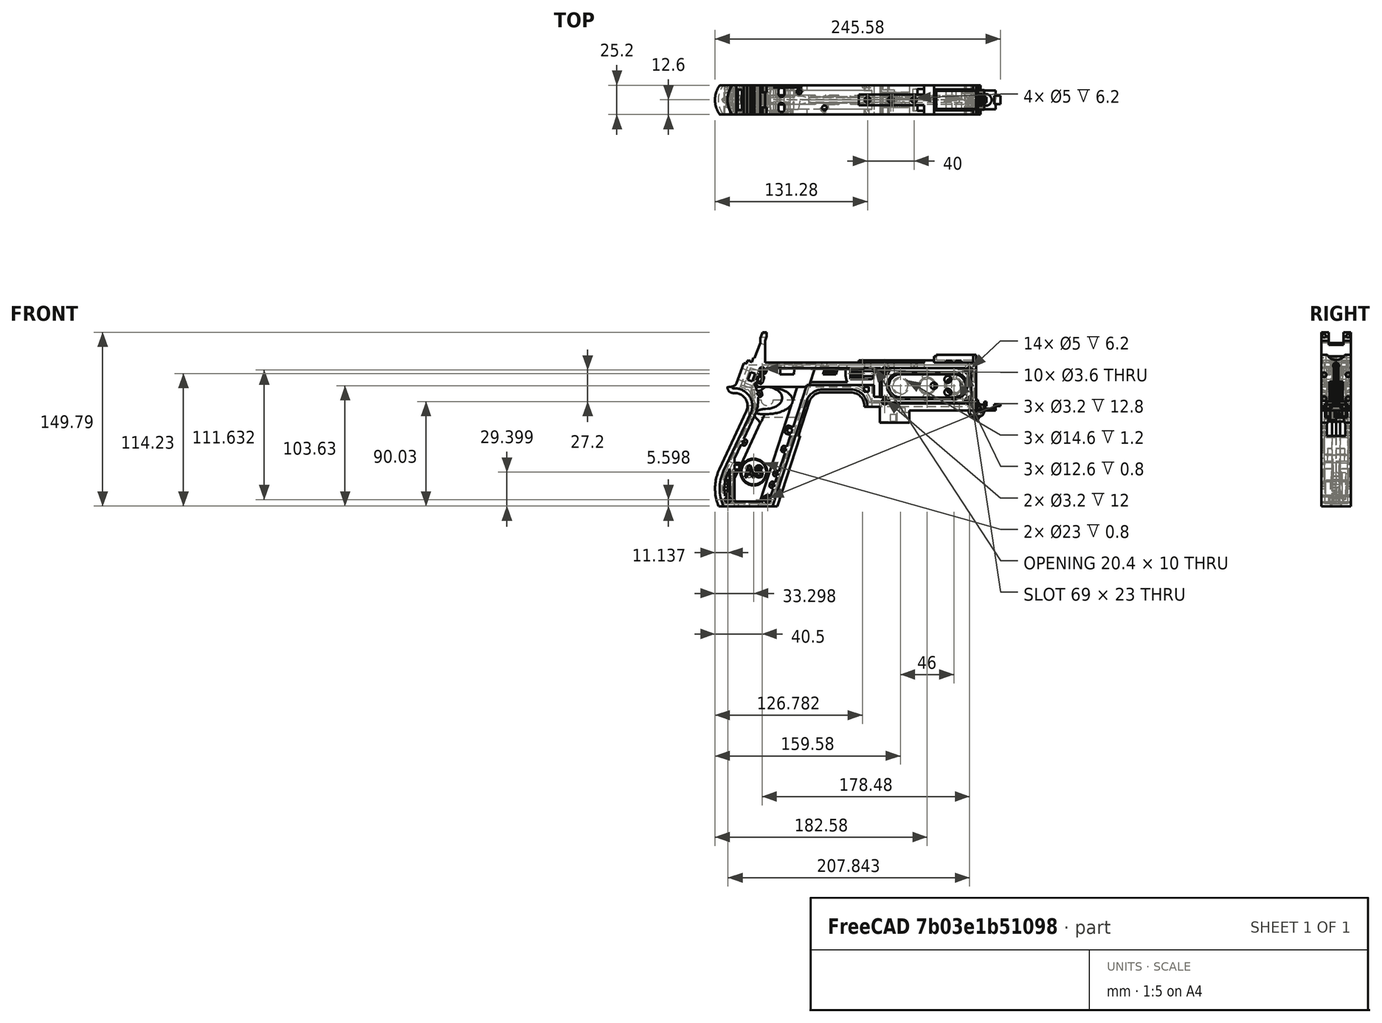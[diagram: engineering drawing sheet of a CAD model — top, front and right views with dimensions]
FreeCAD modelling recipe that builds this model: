
FCSTD DOCUMENT  (FreeCAD 1.0R39319 (Git))
Label: PICON-OF_ver_62
License: All rights reserved
LicenseURL: https://en.wikipedia.org/wiki/All_rights_reserved
objects: Sketcher::SketchObject×132, Part::Extrusion×66, Part::Cut×51, PartDesign::Pad×34, PartDesign::Pocket×21, PartDesign::Chamfer×15, PartDesign::Body×11, PartDesign::Fillet×6, Part::MultiFuse×5, Part::Part2DObjectPython×4, PartDesign::SubtractivePipe×4, PartDesign::SubtractiveLoft×4, PartDesign::Plane×3, PartDesign::SubShapeBinder×2, Part::Sweep×1, PartDesign::ShapeBinder×1, Mesh::Feature×1, PartDesign::Point×1, PartDesign::Groove×1
note: 664 computed .brp shape members not serialized (recipe doc carries the construction recipe); baked Part::Feature solids carry a one-line shape summary decoded from their .brp

FEATURE [Sketcher::SketchObject] Sketch  label="corpo principale"
  ArcFitTolerance = 1e-06
  AttacherType = Attacher::AttachEngine3D
  AttachmentSupport = -> [XZ_Plane]
  FullyConstrained = true
  MakeInternals = false
  MapMode = 5
  Placement = pos=(0,0,0) rot=(1,0,0;1.5708rad)
  sketch-geometry (65):
    g0: LineSegment StartX=0 StartY=0 StartZ=0 EndX=-57.2 EndY=0 EndZ=0
    g1: LineSegment StartX=-57.2 StartY=0 StartZ=0 EndX=-57.2 EndY=-10.4 EndZ=0
    g2: LineSegment StartX=-57.2 StartY=-10.4 StartZ=0 EndX=-82.8 EndY=-10.4 EndZ=0
    g3: LineSegment StartX=-82.8 StartY=-10.4 StartZ=0 EndX=-82.8 EndY=3.2 EndZ=0
    g4: LineSegment StartX=-82.8 StartY=3.2 StartZ=0 EndX=-93.6 EndY=3.2 EndZ=0
    g5: LineSegment StartX=-93.6 StartY=3.2 StartZ=0 EndX=-93.6 EndY=4 EndZ=0
    g6: LineSegment StartX=-107.6 StartY=18 StartZ=0 EndX=-132.428 EndY=18 EndZ=0
    g7: LineSegment StartX=-145.743 StartY=8.32624 StartZ=0 EndX=-175.232 EndY=-82.4316 EndZ=0
    g8: LineSegment StartX=-175.232 StartY=-82.4316 StartZ=0 EndX=-217.232 EndY=-82.4316 EndZ=0
    g9: LineSegment StartX=-217.232 StartY=-52.1862 StartZ=0 EndX=-193.988 EndY=-2.33927 EndZ=0
    g10: LineSegment StartX=-206.196 StartY=23.0857 StartZ=0 EndX=-199.861 EndY=40.4914 EndZ=0
    g11: LineSegment StartX=-199.861 StartY=40.4914 StartZ=0 EndX=-197.061 EndY=40.4914 EndZ=0
    g12: LineSegment StartX=-197.061 StartY=40.4914 StartZ=0 EndX=-197.061 EndY=42.8914 EndZ=0
    g13: LineSegment StartX=-197.061 StartY=42.8914 StartZ=0 EndX=-194.261 EndY=42.8914 EndZ=0
    g14: LineSegment StartX=-194.261 StartY=42.8914 StartZ=0 EndX=-194.535 EndY=42.1397 EndZ=0
    g15: LineSegment StartX=-194.535 StartY=42.1397 StartZ=0 EndX=-193.031 EndY=41.5924 EndZ=0
    g16: LineSegment StartX=-193.031 StartY=41.5924 StartZ=0 EndX=-191.663 EndY=45.3512 EndZ=0
    g17: LineSegment StartX=-191.663 StartY=45.3512 StartZ=0 EndX=-190.536 EndY=44.9408 EndZ=0
    g18: LineSegment StartX=-190.536 StartY=44.9408 StartZ=0 EndX=-185.747 EndY=58.0965 EndZ=0
    g19: LineSegment StartX=-185.747 StartY=58.0965 StartZ=0 EndX=-185.747 EndY=62.0965 EndZ=0
    g20: LineSegment StartX=-185.747 StartY=62.0965 StartZ=0 EndX=-183.832 EndY=67.3588 EndZ=0
    g21: LineSegment StartX=-183.832 StartY=67.3588 StartZ=0 EndX=-180.232 EndY=67.3588 EndZ=0
    g22: LineSegment StartX=-180.232 StartY=67.3588 StartZ=0 EndX=-180.232 EndY=63.7588 EndZ=0
    g23: LineSegment StartX=-180.232 StartY=63.7588 StartZ=0 EndX=-181.6 EndY=60 EndZ=0
    g24: LineSegment StartX=-181.6 StartY=60 StartZ=0 EndX=-181.6 EndY=41.2 EndZ=0
    g25: LineSegment StartX=-181.6 StartY=41.2 StartZ=0 EndX=-100.8 EndY=41.2 EndZ=0
    g26: LineSegment StartX=-36 StartY=43.2 StartZ=0 EndX=-36 EndY=41.2 EndZ=0
    g27: LineSegment StartX=0 StartY=48 StartZ=0 EndX=0 EndY=0 EndZ=0
    g28: LineSegment StartX=-209.901 StartY=19.85 StartZ=0 EndX=-209.901 EndY=20.1 EndZ=0
    g29: LineSegment StartX=-208.001 StartY=22 StartZ=0 EndX=-207.747 EndY=22 EndZ=0
    g30: LineSegment StartX=-207.583 StartY=19 StartZ=0 EndX=-209.051 EndY=19 EndZ=0
    g31: ArcOfCircle CenterX=-208.001 CenterY=20.1 CenterZ=0 NormalX=0 NormalY=0 NormalZ=1 AngleXU=0 Radius=1.9 StartAngle=1.5708 EndAngle=3.14159
    g32: GeomPoint [constr] X=-209.901 Y=22 Z=0
    g33: ArcOfCircle CenterX=-209.051 CenterY=19.85 CenterZ=0 NormalX=0 NormalY=0 NormalZ=1 AngleXU=0 Radius=0.85 StartAngle=3.14159 EndAngle=4.71239
    g34: GeomPoint [constr] X=-209.901 Y=19 Z=0
    g35: ArcOfCircle CenterX=-207.747 CenterY=23.65 CenterZ=0 NormalX=0 NormalY=0 NormalZ=1 AngleXU=0 Radius=1.65 StartAngle=4.71239 EndAngle=5.93412
    g36: GeomPoint [constr] X=-206.591 Y=22 Z=0
    g37: LineSegment StartX=-4 StartY=6 StartZ=0 EndX=-4 EndY=36.4 EndZ=0
    g38: LineSegment StartX=-4 StartY=36.4 StartZ=0 EndX=-185.2 EndY=36.4 EndZ=0
    g39: LineSegment StartX=-185.2 StartY=36.4 StartZ=0 EndX=-190.441 EndY=22 EndZ=0
    g40: LineSegment StartX=-214.575 StartY=-78.4316 StartZ=0 EndX=-178.142 EndY=-78.4316 EndZ=0
    g41: LineSegment StartX=-178.142 StartY=-78.4316 StartZ=0 EndX=-145.51 EndY=22 EndZ=0
    g42: LineSegment StartX=-145.51 StartY=22 StartZ=0 EndX=-87.91 EndY=22 EndZ=0
    g43: LineSegment StartX=-87.91 StartY=22 StartZ=0 EndX=-87.91 EndY=11.6 EndZ=0
    g44: LineSegment StartX=-87.91 StartY=11.6 StartZ=0 EndX=-80.11 EndY=11.6 EndZ=0
    g45: LineSegment StartX=-80.11 StartY=11.6 StartZ=0 EndX=-80.11 EndY=6 EndZ=0
    g46: LineSegment StartX=-80.11 StartY=6 StartZ=0 EndX=-4 EndY=6 EndZ=0
    g47: LineSegment StartX=-190.363 StartY=-4.02975 StartZ=0 EndX=-213.607 EndY=-53.8767 EndZ=0
    g48: ArcOfCircle CenterX=-132.428 CenterY=4 CenterZ=0 NormalX=0 NormalY=0 NormalZ=1 AngleXU=0 Radius=14 StartAngle=1.5708 EndAngle=2.82743
    g49: GeomPoint [constr] X=-142.6 Y=18 Z=0
    g50: ArcOfCircle CenterX=-107.6 CenterY=4 CenterZ=0 NormalX=0 NormalY=0 NormalZ=1 AngleXU=0 Radius=14 StartAngle=0 EndAngle=1.5708
    g51: GeomPoint [constr] X=-93.6 Y=18 Z=0
    g52: ArcOfCircle CenterX=-184.801 CenterY=-67.3089 CenterZ=0 NormalX=0 NormalY=0 NormalZ=1 AngleXU=0 Radius=35.7833 StartAngle=2.70526 EndAngle=3.57792
    g53: ArcOfCircle CenterX=-207.583 CenterY=4 CenterZ=0 NormalX=0 NormalY=0 NormalZ=1 AngleXU=0 Radius=15 StartAngle=5.84685 EndAngle=7.85398
    g54: LineSegment [constr] StartX=-213.607 StartY=-53.8767 StartZ=0 EndX=-217.232 EndY=-52.1862 EndZ=0
    g55: ArcOfCircle CenterX=-184.801 CenterY=-67.3089 CenterZ=0 NormalX=0 NormalY=0 NormalZ=1 AngleXU=0 Radius=31.7833 StartAngle=2.70526 EndAngle=3.49911
    g56: ArcOfCircle CenterX=-218.095 CenterY=8.90192 CenterZ=0 NormalX=0 NormalY=0 NormalZ=1 AngleXU=0 Radius=30.5989 StartAngle=5.84685 EndAngle=6.72553
    g57: LineSegment StartX=-44.6 StartY=43.2 StartZ=0 EndX=-36 EndY=43.2 EndZ=0
    g58: LineSegment StartX=-100.8 StartY=41.2 StartZ=0 EndX=-44.6 EndY=41.2 EndZ=0
    g59: LineSegment StartX=-44.6 StartY=41.2 StartZ=0 EndX=-44.6 EndY=43.2 EndZ=0
    g60: LineSegment StartX=-2.4 StartY=48 StartZ=0 EndX=0 EndY=48 EndZ=0
    g61: LineSegment StartX=-36 StartY=41.2 StartZ=0 EndX=-2.4 EndY=41.2 EndZ=0
    g62: LineSegment StartX=-2.4 StartY=41.2 StartZ=0 EndX=-2.4 EndY=48 EndZ=0
    g63: LineSegment [constr] StartX=-181.6 StartY=36.4 StartZ=0 EndX=-152.209 EndY=36.4 EndZ=0
    g64: LineSegment [constr] StartX=-181.6 StartY=36.4 StartZ=0 EndX=-130.41 EndY=36.4 EndZ=0
  constraints (183):
    c: Coincident(g-1,g0)
    c: PointOnObject(g0,g-1)
    c: Coincident(g0,g1)
    c: Vertical(g1)
    c: Coincident(g1,g2)
    c: Horizontal(g2)
    c: Coincident(g2,g3)
    c: Vertical(g3)
    c: Coincident(g3,g4)
    c: Coincident(g4,g5)
    c: Vertical(g5)
    c: Horizontal(g6)
    c: Coincident(g7,g8)
    c: Horizontal(g8)
    c: Coincident(g10,g11)
    c: Horizontal(g11)
    c: Coincident(g11,g12)
    c: Vertical(g12)
    c: Coincident(g12,g13)
    c: Horizontal(g13)
    c: Coincident(g13,g14)
    c: Coincident(g14,g15)
    c: Coincident(g15,g16)
    c: Coincident(g16,g17)
    c: Coincident(g17,g18)
    c: Coincident(g18,g19)
    c: Vertical(g19)
    c: Coincident(g19,g20)
    c: Coincident(g20,g21)
    c: Horizontal(g21)
    c: Coincident(g21,g22)
    c: Vertical(g22)
    c: Coincident(g22,g23)
    c: Coincident(g23,g24)
    c: Vertical(g24)
    c: Coincident(g24,g25)
    c: Horizontal(g25)
    c: Coincident(g57,g26)
    c: Vertical(g26)
    c: Coincident(g26,g61)
    c: PointOnObject(g60,g-2)
    c: Coincident(g60,g27)
    c: Coincident(g27,g0)
    c: DistanceY(g27,g27) = 48
    c: DistanceY(g1,g1) = 10.4
    c: DistanceX(g0,g0) = 57.2
    c: DistanceX(g2,g2) = 25.6
    c: Horizontal(g4)
    c: DistanceY(g3,g3) = 13.6
    c: DistanceX(g4,g4) = 10.8
    c: DistanceY(g5,g51) = 14.8
    c: DistanceX(g49,g51) = 49
    c: Distance(g7,g49) = 105.6
    c: DistanceX(g61,g60) = 36
    c: DistanceX(g25,g25) = 80.8
    c: DistanceY(g24,g24) = 18.8
    c: DistanceY(g22,g22) = 3.6
    c: Distance(g23) = 4
    c: Angle(g-1,g23) = 1.22173
    c: DistanceX(g21,g21) = 3.6
    c: Distance(g20) = 5.6
    c: Angle(g-1,g20) = 1.22173
    c: DistanceY(g19,g19) = 4
    c: Distance(g18) = 14
    c: Angle(g-1,g18) = 1.22173
    c: Distance(g17) = 1.2
    c: Distance(g16) = 4
    c: Angle(g16) = 1.22173
    c: Perpendicular(g18,g17)
    c: Distance(g15) = 1.6
    c: Perpendicular(g16,g15)
    c: Distance(g14) = 0.8
    c: DistanceX(g13,g13) = 2.8
    c: Perpendicular(g15,g14)
    c: DistanceY(g12,g12) = 2.4
    c: DistanceX(g11,g11) = 2.8
    c: Distance(g9) = 55
    c: Angle(g9,g-1) = 2.00713
    c: Horizontal(g29)
    c: Vertical(g28)
    c: Horizontal(g30)
    c: PointOnObject(g32,g29)
    c: PointOnObject(g32,g28)
    c: Tangent(g29,g31) = 1.5708
    c: Tangent(g28,g31) = 1.5708
    c: PointOnObject(g34,g28)
    c: PointOnObject(g34,g30)
    c: Tangent(g28,g33) = 1.5708
    c: Tangent(g30,g33) = 1.5708
    c: PointOnObject(g36,g29)
    c: PointOnObject(g36,g10)
    c: Tangent(g29,g35) = -1.5708
    c: Tangent(g10,g35) = -1.5708
    c: Angle(g-1,g10) = 1.22173
    c: Radius(g35) = 1.65
    c: Vertical(g37)
    c: Coincident(g37,g38)
    c: Horizontal(g38)
    c: Coincident(g38,g39)
    c: Horizontal(g40)
    c: Coincident(g40,g41)
    c: Coincident(g41,g42)
    c: Horizontal(g42)
    c: Coincident(g42,g43)
    c: Vertical(g43)
    c: Coincident(g43,g44)
    c: Horizontal(g44)
    c: Coincident(g44,g45)
    c: Vertical(g45)
    c: Coincident(g45,g46)
    c: Coincident(g46,g37)
    c: Horizontal(g46)
    c: DistanceY(g0,g37) = 6
    c: DistanceX(g37,g0) = 4
    c: DistanceY(g37,g25) = 4.8
    c: DistanceX(g38,g38) = 181.2
    c: DistanceX(g42,g42) = 57.6
    c: DistanceY(g49,g41) = 4
    c: DistanceX(g41,g49) = 2.91
    c: DistanceY(g43,g43) = 10.4
    c: DistanceX(g44,g44) = 7.8
    c: DistanceY(g7,g40) = 4
    c: Distance(g47) = 55
    c: Angle(g-1,g39) = 1.22173
    c: PointOnObject(g49,g7)
    c: PointOnObject(g49,g6)
    c: Tangent(g7,g48) = -1.5708
    c: Tangent(g6,g48) = -1.5708
    c: PointOnObject(g51,g5)
    c: PointOnObject(g51,g6)
    c: Tangent(g5,g50) = -1.5708
    c: Tangent(g6,g50) = -1.5708
    c: Radius(g50) = 14
    c: Radius(g48) = 14
    c: DistanceX(g8,g8) = 42
    c: Angle(g7,g-1) = 1.88496
    c: Parallel(g41,g7)
    c: Parallel(g47,g9)
    c: Coincident(g52,g8)
    c: Tangent(g52,g9) = 1.5708
    c: DistanceX(g9,g8) = 0
    c: Tangent(g53,g9) = -1.5708
    c: Tangent(g53,g30) = -1.5708
    c: Diameter(g53) = 30
    c: DistanceY(g53,g0) = -4
    c: Coincident(g54,g47)
    c: Distance(g54) = 4
    c: Coincident(g54,g9)
    c: Coincident(g55,g40)
    c: Tangent(g55,g47) = -1.5708
    c: Coincident(g52,g55)
    c: Coincident(g56,g39)
    c: Tangent(g56,g47) = 1.5708
    c: Horizontal(g57)
    c: DistanceX(g57,g57) = 8.6
    c: Coincident(g58,g25)
    c: Horizontal(g58)
    c: Coincident(g59,g58)
    c: Vertical(g59)
    c: DistanceY(g58,g57) = 2
    c: DistanceX(g58,g58) = 56.2
    c: Coincident(g59,g57)
    c: DistanceY(g41,g36) = 0
    c: DistanceY(g36,g39) = 0
    c: DistanceY(g28,g28) = 0.25
    c: DistanceX(g30,g36) = 2.46
    c: DistanceX(g28,g29) = 1.9
    c: Coincident(g62,g60)
    c: Horizontal(g60)
    c: DistanceX(g62,g27) = 2.4
    c: Coincident(g61,g62)
    c: DistanceY(g26,g26) = 2
    c: Vertical(g62)
    c: DistanceY(g61,g60) = 6.8
    c: Horizontal(g61)
    c: Distance(g63) = 29.391
    c: PointOnObject(g63,g38)
    c: PointOnObject(g63,g38)
    c: Distance(g64) = 51.19
    c: PointOnObject(g64,g38)
    c: PointOnObject(g64,g38)
    c: DistanceX(g24,g63) = 0
    c: DistanceX(g24,g64) = 0
FEATURE [Part::Extrusion] Extrude  label="Extrude corpo principale"
  Base = -> Sketch
  Dir = (0,-1,2e-16)
  DirMode = 2
  FaceMakerClass = Part::FaceMakerBullseye
  FaceMakerMode = 3
  LengthFwd = 25.2
  LengthRev = 12.6
  Solid = true
  Symmetric = true
FEATURE [Sketcher::SketchObject] Sketch002  label="scavo grilletto"
  ArcFitTolerance = 1e-06
  AttachmentSupport = -> [XZ_Plane]
  ExternalGeometry = -> [Sketch]
  FullyConstrained = true
  MakeInternals = false
  MapMode = 5
  Placement = pos=(0,0,0) rot=(1,0,0;1.5708rad)
  sketch-geometry (4):
    g0: LineSegment StartX=-89.51 StartY=22 StartZ=0 EndX=-152.71 EndY=22 EndZ=0
    g1: LineSegment StartX=-152.71 StartY=22 StartZ=0 EndX=-167.006 EndY=-22 EndZ=0
    g2: LineSegment StartX=-167.006 StartY=-22 StartZ=0 EndX=-89.51 EndY=-22 EndZ=0
    g3: LineSegment StartX=-89.51 StartY=-22 StartZ=0 EndX=-89.51 EndY=22 EndZ=0
  constraints (12):
    c: Horizontal(g0)
    c: Coincident(g0,g1)
    c: Coincident(g1,g2)
    c: Horizontal(g2)
    c: Coincident(g2,g3)
    c: Coincident(g3,g0)
    c: Vertical(g3)
    c: Angle(g1,g0) = 1.88496
    c: DistanceY(g3,g3) = 44
    c: DistanceX(g0,g0) = 63.2
    c: DistanceX(g0,g-3) = 1.6
    c: DistanceY(g-3,g0) = 0
FEATURE [Sketcher::SketchObject] Sketch004  label="traiettoria arrotondamento impugnatura anteriore"
  ArcFitTolerance = 1e-06
  AttachmentSupport = -> [XZ_Plane]
  ExternalGeometry = -> [Sketch]
  FullyConstrained = true
  MakeInternals = false
  MapMode = 5
  Placement = pos=(0,0,0) rot=(1,0,0;1.5708rad)
  sketch-geometry (13):
    g0: LineSegment StartX=-175.232 StartY=-82.4316 StartZ=0 EndX=-145.743 EndY=8.32624 EndZ=0
    g1: LineSegment StartX=-93.6 StartY=3.2 StartZ=0 EndX=-93.6 EndY=4 EndZ=0
    g2: LineSegment StartX=-132.428 StartY=18 StartZ=0 EndX=-107.6 EndY=18 EndZ=0
    g3: ArcOfCircle CenterX=-132.428 CenterY=4 CenterZ=0 NormalX=0 NormalY=0 NormalZ=1 AngleXU=0 Radius=14 StartAngle=1.5708 EndAngle=2.82743
    g4: ArcOfCircle CenterX=-107.6 CenterY=4 CenterZ=0 NormalX=0 NormalY=0 NormalZ=1 AngleXU=0 Radius=14 StartAngle=0 EndAngle=1.5708
    g5: LineSegment StartX=-175.232 StartY=-82.4316 StartZ=0 EndX=-217.232 EndY=-82.4316 EndZ=0
    g6: LineSegment StartX=-217.232 StartY=-52.1862 StartZ=0 EndX=-193.988 EndY=-2.33927 EndZ=0
    g7: LineSegment StartX=-209.051 StartY=19 StartZ=0 EndX=-207.583 EndY=19 EndZ=0
    g8: LineSegment StartX=-209.901 StartY=20.1 StartZ=0 EndX=-209.901 EndY=19.85 EndZ=0
    g9: ArcOfCircle CenterX=-184.801 CenterY=-67.3089 CenterZ=0 NormalX=0 NormalY=0 NormalZ=1 AngleXU=0 Radius=35.7833 StartAngle=2.70526 EndAngle=3.57792
    g10: ArcOfCircle CenterX=-207.583 CenterY=4 CenterZ=0 NormalX=0 NormalY=0 NormalZ=1 AngleXU=0 Radius=15 StartAngle=5.84685 EndAngle=7.85398
    g11: ArcOfCircle CenterX=-209.051 CenterY=19.85 CenterZ=0 NormalX=0 NormalY=0 NormalZ=1 AngleXU=0 Radius=0.85 StartAngle=3.14159 EndAngle=4.71239
    g12: ArcOfCircle CenterX=-208.001 CenterY=20.1 CenterZ=0 NormalX=0 NormalY=0 NormalZ=1 AngleXU=0 Radius=1.9 StartAngle=1.5708 EndAngle=3.14159
  constraints (26):
    c: Coincident(g0,g-3)
    c: Coincident(g0,g-6)
    c: Coincident(g1,g-8)
    c: Coincident(g1,g-7)
    c: Coincident(g2,g-5)
    c: Coincident(g2,g-4)
    c: Coincident(g3,g2)
    c: Tangent(g3,g0) = 1.5708
    c: Coincident(g4,g1)
    c: Tangent(g4,g2) = 1.5708
    c: Coincident(g5,g0)
    c: Coincident(g5,g-9)
    c: Coincident(g6,g-12)
    c: Coincident(g6,g-11)
    c: Coincident(g7,g-15)
    c: Coincident(g7,g-14)
    c: Coincident(g8,g-16)
    c: Coincident(g8,g-17)
    c: Tangent(g9,g6) = 1.5708
    c: Coincident(g9,g5)
    c: Coincident(g10,g7)
    c: Tangent(g10,g6) = -1.5708
    c: Tangent(g11,g7) = -1.5708
    c: Coincident(g11,g8)
    c: Tangent(g12,g8) = -1.5708
    c: Coincident(g12,g-17)
FEATURE [PartDesign::Plane] DatumPlane  label="Piano per disegno arrotondamento impugnatura"
  AttachmentSupport = -> [Sketch]
  Length = 73.6581
  MapMode = 7
  Placement = pos=(-145.743,1.8e-15,8.32624) rot=(0.154555,0.154555,0.97582;1.59527rad)
  ResizeMode = 0
  Width = 303.511
FEATURE [Sketcher::SketchObject] Sketch005  label="forma arrotondamento impugnatura anteriore"
  ArcFitTolerance = 1e-06
  AttachmentSupport = -> [DatumPlane]
  FullyConstrained = true
  MakeInternals = false
  MapMode = 5
  Placement = pos=(-145.743,1.8e-15,8.32624) rot=(0.154555,0.154555,0.97582;1.59527rad)
  sketch-geometry (5):
    g0: GeomPoint [constr] X=0 Y=-4 Z=0
    g1: GeomPoint [constr] X=-12.6 Y=7.1e-15 Z=0
    g2: GeomPoint [constr] X=12.6 Y=4.97e-14 Z=0
    g3: LineSegment StartX=-12.6 StartY=7.1e-15 StartZ=0 EndX=12.6 EndY=4.97e-14 EndZ=0
    g4: ArcOfCircle CenterX=-3.88e-14 CenterY=17.845 CenterZ=0 NormalX=0 NormalY=0 NormalZ=1 AngleXU=0 Radius=21.845 StartAngle=4.09759 EndAngle=5.32718
  constraints (11):
    c: DistanceY(g0,g-1) = 4
    c: DistanceX(g-1,g0) = 0
    c: DistanceX(g1,g-1) = 12.6
    c: DistanceX(g-1,g2) = 12.6
    c: DistanceY(g-1,g2) = 0
    c: DistanceY(g-1,g1) = 0
    c: Coincident(g3,g1)
    c: Coincident(g3,g2)
    c: Coincident(g4,g1)
    c: Coincident(g4,g2)
    c: PointOnObject(g0,g4)
FEATURE [Part::Sweep] Sweep  label="Sweep impugnatura"
  Frenet = true
  Sections = -> [Sketch005]
  Solid = true
  Spine = -> Sketch [Edge32,Edge33,Edge34,Edge35,Edge36,Edge37,Edge38,Edge39,Edge40,Edge41,Edge42,Edge43,Edge44]
  Transition = 1
FEATURE [Sketcher::SketchObject] Sketch008  label="buchi e pulizie varie"
  ArcFitTolerance = 1e-06
  AttachmentSupport = -> [XZ_Plane]
  ExternalGeometry = -> [Sketch]
  FullyConstrained = true
  MakeInternals = false
  MapMode = 5
  Placement = pos=(0,0,0) rot=(1,0,0;1.5708rad)
  sketch-geometry (26):
    g0: LineSegment StartX=-96.278 StartY=20.155 StartZ=0 EndX=-92.278 EndY=20.155 EndZ=0
    g1: LineSegment StartX=-92.278 StartY=20.155 StartZ=0 EndX=-92.278 EndY=16.155 EndZ=0
    g2: LineSegment StartX=-92.278 StartY=16.155 StartZ=0 EndX=-96.278 EndY=16.155 EndZ=0
    g3: LineSegment StartX=-96.278 StartY=16.155 StartZ=0 EndX=-96.278 EndY=20.155 EndZ=0
    g4: LineSegment StartX=-222.232 StartY=-82.4316 StartZ=0 EndX=-170.232 EndY=-82.4316 EndZ=0
    g5: LineSegment StartX=-170.232 StartY=-82.4316 StartZ=0 EndX=-170.232 EndY=-86.4316 EndZ=0
    g6: LineSegment StartX=-170.232 StartY=-86.4316 StartZ=0 EndX=-222.232 EndY=-86.4316 EndZ=0
    g7: LineSegment StartX=-222.232 StartY=-86.4316 StartZ=0 EndX=-222.232 EndY=-82.4316 EndZ=0
    g8: LineSegment StartX=-213.901 StartY=20.1 StartZ=0 EndX=-213.901 EndY=26 EndZ=0
    g9: LineSegment StartX=-213.901 StartY=26 StartZ=0 EndX=-206.196 EndY=26 EndZ=0
    g10: LineSegment StartX=-17.4 StartY=42.8 StartZ=0 EndX=-12.4 EndY=42.8 EndZ=0
    g11: LineSegment StartX=-12.4 StartY=42.8 StartZ=0 EndX=-12.4 EndY=41.2 EndZ=0
    g12: LineSegment StartX=-12.4 StartY=41.2 StartZ=0 EndX=-17.4 EndY=41.2 EndZ=0
    g13: LineSegment StartX=-17.4 StartY=41.2 StartZ=0 EndX=-17.4 EndY=42.8 EndZ=0
    g14: LineSegment StartX=-25.9 StartY=42.8 StartZ=0 EndX=-20.9 EndY=42.8 EndZ=0
    g15: LineSegment StartX=-20.9 StartY=42.8 StartZ=0 EndX=-20.9 EndY=41.2 EndZ=0
    g16: LineSegment StartX=-20.9 StartY=41.2 StartZ=0 EndX=-25.9 EndY=41.2 EndZ=0
    g17: LineSegment StartX=-25.9 StartY=41.2 StartZ=0 EndX=-25.9 EndY=42.8 EndZ=0
    g18: GeomPoint [constr] X=-206.196 Y=23.0857 Z=0
    g19: GeomPoint [constr] X=-213.901 Y=20.1 Z=0
    g20: BSplineCurve PolesCount=4 KnotsCount=2 Degree=3 IsPeriodic=0
    g21-g24: Circle [constr] x4 (B-spline internal-alignment scaffolding for g20; pole/knot coordinates omitted)
    g25: LineSegment StartX=-206.196 StartY=26 StartZ=0 EndX=-206.196 EndY=23.0857 EndZ=0
  constraints (73):
    c: Horizontal(g0)
    c: Coincident(g1,g0)
    c: Vertical(g1)
    c: Coincident(g2,g1)
    c: Horizontal(g2)
    c: Coincident(g3,g2)
    c: Coincident(g3,g0)
    c: Vertical(g3)
    c: DistanceX(g0,g-4) = 4.368
    c: DistanceY(g0,g-4) = 1.845
    c: DistanceY(g1,g1) = 4
    c: DistanceX(g2,g2) = 4
    c: Horizontal(g4)
    c: Coincident(g5,g4)
    c: Vertical(g5)
    c: Coincident(g6,g5)
    c: Horizontal(g6)
    c: Coincident(g7,g6)
    c: Coincident(g7,g4)
    c: Vertical(g7)
    c: DistanceY(g7,g7) = 4
    c: DistanceX(g4,g-5) = 5
    c: DistanceX(g-5,g4) = 5
    c: DistanceY(g4,g-5) = 0
    c: Coincident(g9,g8)
    c: Parallel(g9,g-6)
    c: DistanceX(g8,g-8) = 4
    c: Horizontal(g10)
    c: Coincident(g11,g10)
    c: Vertical(g11)
    c: Coincident(g12,g11)
    c: Horizontal(g12)
    c: Coincident(g13,g12)
    c: Coincident(g13,g10)
    c: Vertical(g13)
    c: Horizontal(g14)
    c: Coincident(g15,g14)
    c: Vertical(g15)
    c: Coincident(g16,g15)
    c: Horizontal(g16)
    c: Coincident(g17,g16)
    c: Coincident(g17,g14)
    c: Vertical(g17)
    c: DistanceY(g11,g10) = 1.6
    c: DistanceX(g10,g10) = 5
    c: DistanceY(g15,g14) = 1.6
    c: DistanceX(g14,g14) = 5
    c: DistanceX(g15,g12) = 3.5
    c: DistanceX(g11,g-9) = 10
    c: DistanceY(g-9,g11) = 0
    c: DistanceY(g-9,g15) = 0
    c: Perpendicular(g8,g9)
    c: DistanceY(g-7,g9) = 4
    c: DistanceY(g8,g-8) = 0
    c: InternalAlignment(g18,g20)
    c: InternalAlignment(g19,g20)
    c: InternalAlignment(g21,g20)
    c: Weight(g21) = 1
    c: InternalAlignment(g22,g20)
    c: Equal(g22,g21)
    c: InternalAlignment(g23,g20)
    c: Equal(g23,g21)
    c: InternalAlignment(g24,g20)
    c: Equal(g24,g21)
    c: Coincident(g18,g-12)
    c: Coincident(g19,g8)
    c: Coincident(g25,g9)
    c: Coincident(g25,g20)
    c: Vertical(g25)
    c: DistanceY(g20,g23) = 0
    c: DistanceY(g22,g18) = 2.26
    c: DistanceX(g22,g18) = 0.93
    c: DistanceX(g20,g23) = 2.9
FEATURE [Part::Extrusion] Extrude004  label="Extrude Buchi e pulizie varie"
  Base = -> Sketch008
  Dir = (0,-1,2e-16)
  DirMode = 2
  FaceMakerClass = Part::FaceMakerBullseye
  FaceMakerMode = 3
  LengthFwd = 25.2
  LengthRev = 0
  Solid = true
  Symmetric = true
FEATURE [Sketcher::SketchObject] Sketch009  label="rinforzi"
  ArcFitTolerance = 1e-06
  AttachmentSupport = -> [XZ_Plane]
  ExternalGeometry = -> [Sketch]
  FullyConstrained = true
  MakeInternals = false
  MapMode = 5
  Placement = pos=(0,0,0) rot=(1,0,0;1.5708rad)
  sketch-geometry (9):
    g0: LineSegment StartX=-87.91 StartY=22 StartZ=0 EndX=-87.91 EndY=36.4 EndZ=0
    g1: LineSegment StartX=-87.91 StartY=36.4 StartZ=0 EndX=-97.91 EndY=36.4 EndZ=0
    g2: LineSegment StartX=-97.91 StartY=36.4 StartZ=0 EndX=-97.91 EndY=22 EndZ=0
    g3: LineSegment StartX=-97.91 StartY=22 StartZ=0 EndX=-87.91 EndY=22 EndZ=0
    g4: LineSegment StartX=-149.713 StartY=9.06563 StartZ=0 EndX=-154.586 EndY=-5.93437 EndZ=0
    g5: LineSegment StartX=-154.586 StartY=-5.93437 StartZ=0 EndX=-191.863 EndY=-5.93437 EndZ=0
    g6: LineSegment StartX=-191.863 StartY=-5.93437 StartZ=0 EndX=-191.863 EndY=9.06563 EndZ=0
    g7: LineSegment StartX=-191.863 StartY=9.06563 StartZ=0 EndX=-149.713 EndY=9.06563 EndZ=0
    g8: LineSegment [constr] StartX=-145.51 StartY=22 StartZ=0 EndX=-149.713 EndY=9.06563 EndZ=0
  constraints (25):
    c: Vertical(g0)
    c: Coincident(g1,g0)
    c: Horizontal(g1)
    c: Coincident(g2,g1)
    c: Vertical(g2)
    c: Coincident(g3,g2)
    c: Coincident(g3,g0)
    c: Horizontal(g3)
    c: Coincident(g0,g-4)
    c: DistanceX(g3,g3) = 10
    c: DistanceY(g0,g-3) = 0
    c: Coincident(g5,g4)
    c: Horizontal(g5)
    c: Coincident(g6,g5)
    c: Vertical(g6)
    c: Coincident(g7,g6)
    c: Coincident(g7,g4)
    c: Horizontal(g7)
    c: Distance(g8) = 13.6
    c: Parallel(g-6,g8)
    c: Coincident(g-6,g8)
    c: Parallel(g4,g-6)
    c: DistanceY(g4,g4) = 15
    c: Coincident(g4,g8)
    c: DistanceX(g-5,g5) = -1.5
FEATURE [Part::Extrusion] Extrude001  label="Extrude scavo grilletto"
  Base = -> Sketch002
  Dir = (0,-1,2e-16)
  DirMode = 2
  FaceMakerClass = Part::FaceMakerBullseye
  FaceMakerMode = 3
  LengthFwd = 16
  LengthRev = 0
  Solid = true
  Symmetric = true
FEATURE [Part::Extrusion] Extrude005  label="Extrude Rinforzi"
  Base = -> Sketch009
  Dir = (0,-1,2e-16)
  DirMode = 2
  FaceMakerClass = Part::FaceMakerBullseye
  FaceMakerMode = 3
  LengthFwd = 2
  LengthRev = 0
  Placement = pos=(0,12.6,0) rot=(0,0,1;0rad)
  Solid = true
  Symmetric = false
FEATURE [PartDesign::ShapeBinder] CopyCut
  TraceSupport = false
FEATURE [PartDesign::Plane] DatumPlane001
  AttachmentSupport = -> [CopyCut]
  Length = 283.944
  MapMode = 5
  Placement = pos=(0,12.6,0) rot=(0,0.707107,0.707107;3.14159rad)
  ResizeMode = 0
  Width = 188.15
FEATURE [Sketcher::SketchObject] Sketch010  label="buco neopixel"
  ArcFitTolerance = 1e-06
  AttachmentSupport = -> [XZ_Plane]
  ExternalGeometry = -> [Sketch]
  FullyConstrained = true
  MakeInternals = false
  MapMode = 5
  Placement = pos=(0,0,0) rot=(1,0,0;1.5708rad)
  sketch-geometry (5):
    g0: LineSegment [constr] StartX=-199.861 StartY=40.4914 StartZ=0 EndX=-201.368 EndY=36.3521 EndZ=0
    g1: LineSegment StartX=-201.368 StartY=36.3521 StartZ=0 EndX=-204.932 EndY=26.5605 EndZ=0
    g2: LineSegment StartX=-201.368 StartY=36.3521 StartZ=0 EndX=-180.2 EndY=28.6477 EndZ=0
    g3: LineSegment StartX=-180.2 StartY=28.6477 StartZ=0 EndX=-183.764 EndY=18.8561 EndZ=0
    g4: LineSegment StartX=-183.764 StartY=18.8561 StartZ=0 EndX=-204.932 EndY=26.5605 EndZ=0
  constraints (14):
    c: Parallel(g0,g-3)
    c: Distance(g0) = 4.405
    c: Coincident(g0,g-3)
    c: Coincident(g2,g1)
    c: Coincident(g3,g2)
    c: Coincident(g4,g3)
    c: Coincident(g4,g1)
    c: Parallel(g1,g-3)
    c: Distance(g1) = 10.42
    c: Coincident(g1,g0)
    c: Parallel(g2,g4)
    c: Perpendicular(g1,g2)
    c: DistanceX(g-4,g2) = 5
    c: Parallel(g3,g1)
FEATURE [Part::Extrusion] Extrude006  label="Extrude buco neopixel"
  Base = -> Sketch010
  Dir = (0,-1,2e-16)
  DirMode = 2
  FaceMakerClass = Part::FaceMakerBullseye
  FaceMakerMode = 3
  LengthFwd = 17.2
  LengthRev = 0
  Solid = true
  Symmetric = true
FEATURE [Sketcher::SketchObject] Sketch011  label="fermo grilletto"
  ArcFitTolerance = 1e-06
  AttachmentSupport = -> [XZ_Plane]
  ExternalGeometry = -> [Sketch]
  FullyConstrained = true
  MakeInternals = false
  MapMode = 5
  Placement = pos=(0,0,0) rot=(1,0,0;1.5708rad)
  sketch-geometry (18):
    g0: LineSegment [constr] StartX=-145.51 StartY=22 StartZ=0 EndX=-157.347 EndY=-14.4293 EndZ=0
    g1: LineSegment [constr] StartX=-157.347 StartY=-14.4293 StartZ=0 EndX=-157.841 EndY=-15.951 EndZ=0
    g2: LineSegment StartX=-161.151 StartY=-13.1932 StartZ=0 EndX=-155.825 EndY=-14.9237 EndZ=0
    g3: LineSegment StartX=-163.167 StartY=-14.2205 StartZ=0 EndX=-164.403 EndY=-18.0247 EndZ=0
    g4: LineSegment StartX=-163.376 StartY=-20.0408 StartZ=0 EndX=-158.05 EndY=-21.7713 EndZ=0
    g5: LineSegment StartX=-158.05 StartY=-21.7713 StartZ=0 EndX=-155.825 EndY=-14.9237 EndZ=0
    g6: LineSegment StartX=-161.645 StartY=-14.7149 StartZ=0 EndX=-157.841 EndY=-15.951 EndZ=0
    g7: LineSegment StartX=-157.841 StartY=-15.951 StartZ=0 EndX=-159.077 EndY=-19.7552 EndZ=0
    g8: LineSegment StartX=-159.077 StartY=-19.7552 StartZ=0 EndX=-162.881 EndY=-18.5191 EndZ=0
    g9: LineSegment StartX=-162.881 StartY=-18.5191 StartZ=0 EndX=-161.645 EndY=-14.7149 EndZ=0
    g10: LineSegment [constr] StartX=-161.645 StartY=-14.7149 StartZ=0 EndX=-161.151 EndY=-13.1932 EndZ=0
    g11: LineSegment [constr] StartX=-159.077 StartY=-19.7552 StartZ=0 EndX=-157.555 EndY=-20.2496 EndZ=0
    g12: LineSegment [constr] StartX=-159.077 StartY=-19.7552 StartZ=0 EndX=-159.572 EndY=-21.2769 EndZ=0
    g13: LineSegment [constr] StartX=-161.645 StartY=-14.7149 StartZ=0 EndX=-163.167 EndY=-14.2205 EndZ=0
    g14: ArcOfCircle CenterX=-161.645 CenterY=-14.7149 CenterZ=0 NormalX=0 NormalY=0 NormalZ=1 AngleXU=0 Radius=1.6 StartAngle=1.25664 EndAngle=2.82743
    g15: GeomPoint [constr] X=-162.673 Y=-12.6988 Z=0
    g16: ArcOfCircle CenterX=-162.881 CenterY=-18.5191 CenterZ=0 NormalX=0 NormalY=0 NormalZ=1 AngleXU=0 Radius=1.6 StartAngle=2.82743 EndAngle=4.39823
    g17: GeomPoint [constr] X=-164.897 Y=-19.5464 Z=0
  constraints (48):
    c: Parallel(g0,g-3)
    c: Distance(g0) = 38.304
    c: Coincident(g0,g-3)
    c: Parallel(g1,g-3)
    c: Distance(g1) = 1.6
    c: Coincident(g1,g0)
    c: Coincident(g5,g4)
    c: Coincident(g5,g2)
    c: Coincident(g7,g6)
    c: Coincident(g8,g7)
    c: Coincident(g9,g8)
    c: Coincident(g9,g6)
    c: Parallel(g7,g-3)
    c: Parallel(g9,g7)
    c: Perpendicular(g6,g7)
    c: Parallel(g6,g8)
    c: Distance(g6) = 4
    c: Distance(g9) = 4
    c: Parallel(g5,g7)
    c: Parallel(g9,g3)
    c: Parallel(g2,g6)
    c: Parallel(g4,g8)
    c: Parallel(g13,g6)
    c: Parallel(g10,g9)
    c: Parallel(g11,g8)
    c: Parallel(g12,g7)
    c: Distance(g10) = 1.6
    c: Distance(g13) = 1.6
    c: Distance(g12) = 1.6
    c: Distance(g11) = 1.6
    c: Coincident(g10,g6)
    c: Coincident(g13,g6)
    c: Coincident(g12,g7)
    c: Coincident(g11,g7)
    c: Distance(g10,g15) = 1.6
    c: Distance(g15,g13) = 1.6
    c: Distance(g4,g12) = 1.6
    c: Distance(g4,g11) = 1.6
    c: PointOnObject(g15,g2)
    c: Tangent(g3,g14) = -1.5708
    c: Tangent(g2,g14) = 1.5708
    c: PointOnObject(g17,g4)
    c: PointOnObject(g17,g3)
    c: Tangent(g4,g16) = -1.5708
    c: Tangent(g3,g16) = -1.5708
    c: Equal(g16,g14)
    c: Coincident(g16,g8)
    c: Coincident(g6,g1)
FEATURE [Part::Extrusion] Extrude007  label="Extrude fermo grilletto"
  Base = -> Sketch011
  Dir = (0,-1,2e-16)
  DirMode = 2
  FaceMakerClass = Part::FaceMakerBullseye
  FaceMakerMode = 3
  LengthFwd = 25.2
  LengthRev = 0
  Solid = true
  Symmetric = true
FEATURE [Sketcher::SketchObject] Sketch012  label="buco oled"
  ArcFitTolerance = 1e-06
  AttachmentSupport = -> [XZ_Plane]
  ExternalGeometry = -> [Sketch]
  FullyConstrained = true
  MakeInternals = false
  MapMode = 5
  Placement = pos=(0,0,0) rot=(1,0,0;1.5708rad)
  sketch-geometry (4):
    g0: LineSegment StartX=-185.747 StartY=58.0965 StartZ=0 EndX=-180.232 EndY=56.0891 EndZ=0
    g1: LineSegment StartX=-185.747 StartY=58.0965 StartZ=0 EndX=-185.747 EndY=67.3588 EndZ=0
    g2: LineSegment StartX=-185.747 StartY=67.3588 StartZ=0 EndX=-180.232 EndY=67.3588 EndZ=0
    g3: LineSegment StartX=-180.232 StartY=67.3588 StartZ=0 EndX=-180.232 EndY=56.0891 EndZ=0
  constraints (10):
    c: Coincident(g1,g0)
    c: Coincident(g2,g1)
    c: Coincident(g3,g2)
    c: Coincident(g3,g0)
    c: Parallel(g1,g-5)
    c: Perpendicular(g-3,g0)
    c: Parallel(g2,g-6)
    c: Parallel(g3,g-4)
    c: Coincident(g0,g-5)
    c: Coincident(g2,g-6)
FEATURE [Part::Extrusion] Extrude008  label="Extrude buco oled"
  Base = -> Sketch012
  Dir = (0,-1,2e-16)
  DirMode = 2
  FaceMakerClass = Part::FaceMakerBullseye
  FaceMakerMode = 3
  LengthFwd = 12.8
  LengthRev = 0
  Solid = true
  Symmetric = true
FEATURE [Sketcher::SketchObject] Sketch013  label="buco pompa"
  ArcFitTolerance = 1e-06
  AttachmentSupport = -> [XZ_Plane]
  ExternalGeometry = -> [Sketch]
  FullyConstrained = true
  MakeInternals = false
  MapMode = 5
  Placement = pos=(0,0,0) rot=(1,0,0;1.5708rad)
  sketch-geometry (8):
    g0: LineSegment StartX=-82.8 StartY=-10.4 StartZ=0 EndX=-82.8 EndY=-9.6 EndZ=0
    g1: LineSegment StartX=-82.8 StartY=-9.6 StartZ=0 EndX=-67.9 EndY=-9.6 EndZ=0
    g2: LineSegment StartX=-67.9 StartY=-9.6 StartZ=0 EndX=-67.9 EndY=6 EndZ=0
    g3: LineSegment StartX=-67.9 StartY=6 StartZ=0 EndX=-65.9 EndY=6 EndZ=0
    g4: LineSegment StartX=-65.9 StartY=6 StartZ=0 EndX=-65.9 EndY=-1.7 EndZ=0
    g5: LineSegment StartX=-65.9 StartY=-1.7 StartZ=0 EndX=-57.2 EndY=-1.7 EndZ=0
    g6: LineSegment StartX=-57.2 StartY=-1.7 StartZ=0 EndX=-57.2 EndY=-10.4 EndZ=0
    g7: LineSegment StartX=-57.2 StartY=-10.4 StartZ=0 EndX=-82.8 EndY=-10.4 EndZ=0
  constraints (22):
    c: Vertical(g0)
    c: Coincident(g1,g0)
    c: Horizontal(g1)
    c: Coincident(g2,g1)
    c: Vertical(g2)
    c: Coincident(g3,g2)
    c: Horizontal(g3)
    c: Coincident(g4,g3)
    c: Vertical(g4)
    c: Coincident(g5,g4)
    c: Horizontal(g5)
    c: Coincident(g6,g5)
    c: Vertical(g6)
    c: Coincident(g7,g6)
    c: Coincident(g7,g0)
    c: DistanceY(g0,g0) = 0.8
    c: DistanceY(g6,g6) = 8.7
    c: DistanceX(g1,g1) = 14.9
    c: DistanceX(g3,g3) = 2
    c: Coincident(g0,g-4)
    c: DistanceY(g2,g-6) = 0
    c: Coincident(g6,g-5)
FEATURE [Part::Extrusion] Extrude009  label="Extrude buco pompa"
  Base = -> Sketch013
  Dir = (0,-1,2e-16)
  DirMode = 2
  FaceMakerClass = Part::FaceMakerBullseye
  FaceMakerMode = 3
  LengthFwd = 13.2
  LengthRev = 0
  Solid = true
  Symmetric = true
FEATURE [Sketcher::SketchObject] Sketch014  label="buco frontale"
  ArcFitTolerance = 1e-06
  AttachmentSupport = -> [XZ_Plane]
  ExternalGeometry = -> [Sketch]
  FullyConstrained = true
  MakeInternals = false
  MapMode = 5
  Placement = pos=(0,0,0) rot=(1,0,0;1.5708rad)
  sketch-geometry (10):
    g0: LineSegment StartX=0 StartY=0 StartZ=0 EndX=0 EndY=24.671 EndZ=0
    g1: LineSegment StartX=0 StartY=24.671 StartZ=0 EndX=-4 EndY=24.671 EndZ=0
    g2: LineSegment StartX=-4 StartY=24.671 StartZ=0 EndX=-4 EndY=16 EndZ=0
    g3: LineSegment StartX=-4 StartY=16 StartZ=0 EndX=-2.4 EndY=16 EndZ=0
    g4: LineSegment StartX=-2.4 StartY=16 StartZ=0 EndX=-2.4 EndY=10 EndZ=0
    g5: LineSegment StartX=-2.4 StartY=10 StartZ=0 EndX=-12 EndY=10 EndZ=0
    g6: LineSegment StartX=-12 StartY=10 StartZ=0 EndX=-12 EndY=6 EndZ=0
    g7: LineSegment StartX=-12 StartY=6 StartZ=0 EndX=-2.4 EndY=6 EndZ=0
    g8: LineSegment StartX=-2.4 StartY=6 StartZ=0 EndX=-2.4 EndY=0 EndZ=0
    g9: LineSegment StartX=-2.4 StartY=0 StartZ=0 EndX=0 EndY=0 EndZ=0
  constraints (29):
    c: Vertical(g0)
    c: Coincident(g1,g0)
    c: Horizontal(g1)
    c: Coincident(g2,g1)
    c: Vertical(g2)
    c: Coincident(g3,g2)
    c: Horizontal(g3)
    c: Coincident(g4,g3)
    c: Vertical(g4)
    c: Coincident(g5,g4)
    c: Horizontal(g5)
    c: Coincident(g6,g5)
    c: Vertical(g6)
    c: Coincident(g7,g6)
    c: Coincident(g8,g7)
    c: Vertical(g8)
    c: Coincident(g9,g8)
    c: Coincident(g9,g0)
    c: Horizontal(g9)
    c: DistanceY(g0,g0) = 24.671
    c: Horizontal(g7)
    c: DistanceY(g6,g6) = 4
    c: DistanceY(g4,g4) = 6
    c: DistanceX(g9,g9) = 2.4
    c: Coincident(g0,g-1)
    c: DistanceY(g-3,g7) = 0
    c: DistanceX(g8,g4) = 0
    c: DistanceX(g-3,g1) = 0
    c: DistanceX(g6,g-3) = 8
FEATURE [Part::Extrusion] Extrude010  label="Extrude buco frontale"
  Base = -> Sketch014
  Dir = (0,-1,2e-16)
  DirMode = 2
  FaceMakerClass = Part::FaceMakerBullseye
  FaceMakerMode = 3
  LengthFwd = 11.2
  LengthRev = 0
  Solid = true
  Symmetric = true
FEATURE [Sketcher::SketchObject] Sketch015  label="guida rail"
  ArcFitTolerance = 1e-06
  AttachmentSupport = -> [XZ_Plane]
  ExternalGeometry = -> [Sketch]
  FullyConstrained = true
  MakeInternals = false
  MapMode = 5
  Placement = pos=(0,0,0) rot=(1,0,0;1.5708rad)
  sketch-geometry (4):
    g0: LineSegment StartX=-100.8 StartY=43.2 StartZ=0 EndX=-44.6 EndY=43.2 EndZ=0
    g1: LineSegment StartX=-44.6 StartY=43.2 StartZ=0 EndX=-44.6 EndY=41.2 EndZ=0
    g2: LineSegment StartX=-44.6 StartY=41.2 StartZ=0 EndX=-100.8 EndY=41.2 EndZ=0
    g3: LineSegment StartX=-100.8 StartY=41.2 StartZ=0 EndX=-100.8 EndY=43.2 EndZ=0
  constraints (9):
    c: Horizontal(g0)
    c: Coincident(g1,g0)
    c: Coincident(g2,g1)
    c: Coincident(g3,g2)
    c: Coincident(g3,g0)
    c: Vertical(g3)
    c: Coincident(g2,g-3)
    c: Coincident(g1,g-3)
    c: Coincident(g0,g-4)
FEATURE [Part::Extrusion] Extrude011  label="Extrude guida rail"
  Base = -> Sketch015
  Dir = (0,-1,2e-16)
  DirMode = 2
  FaceMakerClass = Part::FaceMakerBullseye
  FaceMakerMode = 3
  LengthFwd = 9
  LengthRev = 0
  Solid = true
  Symmetric = true
FEATURE [Sketcher::SketchObject] Sketch016  label="guide per coperture laterali"
  ArcFitTolerance = 1e-06
  AttachmentSupport = -> [XZ_Plane]
  ExternalGeometry = -> [Sketch]
  FullyConstrained = true
  MakeInternals = false
  MapMode = 5
  Placement = pos=(0,0,0) rot=(1,0,0;1.5708rad)
  sketch-geometry (14):
    g0: Circle CenterX=-5.6 CenterY=7.6 CenterZ=0 NormalX=0 NormalY=0 NormalZ=1 AngleXU=0 Radius=1.6
    g1: Circle CenterX=-5.6 CenterY=7.6 CenterZ=0 NormalX=0 NormalY=0 NormalZ=1 AngleXU=0 Radius=4
    g2: Circle CenterX=-5.6 CenterY=34.8 CenterZ=0 NormalX=0 NormalY=0 NormalZ=1 AngleXU=0 Radius=1.6
    g3: Circle CenterX=-5.6 CenterY=34.8 CenterZ=0 NormalX=0 NormalY=0 NormalZ=1 AngleXU=0 Radius=4
    g4: Circle CenterX=-184.08 CenterY=34.8 CenterZ=0 NormalX=0 NormalY=0 NormalZ=1 AngleXU=0 Radius=1.6
    g5: Circle CenterX=-184.08 CenterY=34.8 CenterZ=0 NormalX=0 NormalY=0 NormalZ=1 AngleXU=0 Radius=4
    g6: Circle CenterX=-179.305 CenterY=-76.8316 CenterZ=0 NormalX=0 NormalY=0 NormalZ=1 AngleXU=0 Radius=1.6
    g7: Circle CenterX=-179.305 CenterY=-76.8316 CenterZ=0 NormalX=0 NormalY=0 NormalZ=1 AngleXU=0 Radius=4
    g8: Circle CenterX=-213.443 CenterY=-76.8316 CenterZ=0 NormalX=0 NormalY=0 NormalZ=1 AngleXU=0 Radius=1.6
    g9: Circle CenterX=-213.443 CenterY=-76.8316 CenterZ=0 NormalX=0 NormalY=0 NormalZ=1 AngleXU=0 Radius=4
    g10: Circle CenterX=-78.51 CenterY=7.6 CenterZ=0 NormalX=0 NormalY=0 NormalZ=1 AngleXU=0 Radius=1.6
    g11: Circle CenterX=-78.51 CenterY=7.6 CenterZ=0 NormalX=0 NormalY=0 NormalZ=1 AngleXU=0 Radius=4
    g12: Circle CenterX=-78.51 CenterY=34.8 CenterZ=0 NormalX=0 NormalY=0 NormalZ=1 AngleXU=0 Radius=1.6
    g13: Circle CenterX=-78.51 CenterY=34.8 CenterZ=0 NormalX=0 NormalY=0 NormalZ=1 AngleXU=0 Radius=4
  constraints (35):
    c: Diameter(g0) = 3.2
    c: Diameter(g1) = 8
    c: Coincident(g0,g1)
    c: Diameter(g2) = 3.2
    c: Diameter(g3) = 8
    c: Coincident(g3,g2)
    c: Tangent(g2,g-7)
    c: Diameter(g4) = 3.2
    c: Diameter(g5) = 8
    c: Coincident(g5,g4)
    c: Tangent(g4,g-7)
    c: Tangent(g4,g-8)
    c: Diameter(g6) = 3.2
    c: Diameter(g7) = 8
    c: Coincident(g7,g6)
    c: Tangent(g6,g-9)
    c: Tangent(g6,g-10)
    c: Diameter(g8) = 3.2
    c: Diameter(g9) = 8
    c: Coincident(g9,g8)
    c: Tangent(g8,g-10)
    c: Tangent(g8,g-11)
    c: Diameter(g10) = 3.2
    c: Diameter(g11) = 8
    c: Diameter(g12) = 3.2
    c: Diameter(g13) = 8
    c: Coincident(g12,g13)
    c: Coincident(g10,g11)
    c: Tangent(g12,g-7)
    c: DistanceX(g12,g10) = 0
    c: Tangent(g2,g-6)
    c: Tangent(g0,g-6)
    c: Tangent(g0,g-3)
    c: Tangent(g10,g-3)
    c: Tangent(g10,g-4)
FEATURE [Part::Extrusion] Extrude012  label="extrude guide per coperture laterali"
  Base = -> Sketch016
  Dir = (0,-1,2e-16)
  DirMode = 2
  FaceMakerClass = Part::FaceMakerBullseye
  FaceMakerMode = 3
  LengthFwd = 25.2
  LengthRev = 0
  Solid = true
  Symmetric = true
FEATURE [Sketcher::SketchObject] Sketch017  label="supporto CAM"
  ArcFitTolerance = 1e-06
  AttachmentSupport = -> [XZ_Plane]
  ExternalGeometry = -> [Sketch]
  FullyConstrained = true
  MakeInternals = false
  MapMode = 5
  Placement = pos=(0,0,0) rot=(1,0,0;1.5708rad)
  sketch-geometry (6):
    g0: LineSegment StartX=-2.4 StartY=48 StartZ=0 EndX=-2.4 EndY=41.2 EndZ=0
    g1: LineSegment StartX=-2.4 StartY=48 StartZ=0 EndX=-34 EndY=48 EndZ=0
    g2: LineSegment StartX=-34 StartY=48 StartZ=0 EndX=-34 EndY=46.72 EndZ=0
    g3: LineSegment StartX=-34 StartY=46.72 StartZ=0 EndX=-36 EndY=46.72 EndZ=0
    g4: LineSegment StartX=-36 StartY=46.72 StartZ=0 EndX=-36 EndY=41.2 EndZ=0
    g5: LineSegment StartX=-36 StartY=41.2 StartZ=0 EndX=-2.4 EndY=41.2 EndZ=0
  constraints (15):
    c: Coincident(g1,g0)
    c: Horizontal(g1)
    c: Coincident(g2,g1)
    c: Vertical(g2)
    c: Coincident(g3,g2)
    c: Horizontal(g3)
    c: Coincident(g4,g3)
    c: Coincident(g5,g4)
    c: DistanceX(g1,g0) = 31.6
    c: Coincident(g5,g0)
    c: Vertical(g4)
    c: DistanceY(g2,g1) = 1.28
    c: Coincident(g0,g-3)
    c: Coincident(g0,g-3)
    c: Coincident(g4,g-4)
FEATURE [Part::Extrusion] Extrude013  label="Extrude supporto CAM"
  Base = -> Sketch017
  Dir = (0,-1,2e-16)
  DirMode = 2
  FaceMakerClass = Part::FaceMakerBullseye
  FaceMakerMode = 3
  LengthFwd = 17.8
  LengthRev = 0
  Solid = true
  Symmetric = true
FEATURE [Sketcher::SketchObject] Sketch018  label="Scavo CAM"
  ArcFitTolerance = 1e-06
  AttachmentSupport = -> [YZ_Plane]
  ExternalGeometry = -> [Sketch]
  FullyConstrained = true
  MakeInternals = false
  MapMode = 5
  Placement = pos=(0,0,0) rot=(0.57735,0.57735,0.57735;2.0944rad)
  sketch-geometry (4):
    g0: LineSegment StartX=-7.73 StartY=48 StartZ=0 EndX=7.73 EndY=48 EndZ=0
    g1: LineSegment [constr] StartX=1.07e-14 StartY=48 StartZ=0 EndX=0 EndY=43.5155 EndZ=0
    g2: ArcOfCircle CenterX=9e-15 CenterY=52.42 CenterZ=0 NormalX=0 NormalY=0 NormalZ=1 AngleXU=0 Radius=8.90445 StartAngle=3.66102 EndAngle=5.76376
    g3: Circle [constr] CenterX=9e-15 CenterY=52.42 CenterZ=0 NormalX=0 NormalY=0 NormalZ=1 AngleXU=0 Radius=8.9
  constraints (13):
    c: Horizontal(g0)
    c: DistanceY(g-3,g0) = 0
    c: DistanceX(g0,g0) = 15.46
    c: DistanceX(g0,g-3) = 7.73
    c: DistanceX(g-3) = 0
    c: Coincident(g1,g-3)
    c: PointOnObject(g1,g-2)
    c: Coincident(g2,g0)
    c: Coincident(g2,g0)
    c: PointOnObject(g1,g2)
    c: Diameter(g3) = 17.8
    c: DistanceY(g1,g3) = 4.42
    c: Coincident(g2,g3)
FEATURE [Part::Extrusion] Extrude014  label="Extrude Scavo CAM"
  Base = -> Sketch018
  Dir = (1,0,0)
  DirMode = 2
  FaceMakerClass = Part::FaceMakerBullseye
  FaceMakerMode = 3
  LengthFwd = -34
  LengthRev = 0
  Solid = true
  Symmetric = false
FEATURE [Sketcher::SketchObject] Sketch019  label="scavo rumble"
  ArcFitTolerance = 1e-06
  AttachmentSupport = -> [XZ_Plane]
  ExternalGeometry = -> [Sketch]
  FullyConstrained = true
  MakeInternals = false
  MapMode = 5
  Placement = pos=(0,0,0) rot=(1,0,0;1.5708rad)
  sketch-geometry (6):
    g0: LineSegment StartX=-168.716 StartY=-37.1227 StartZ=0 EndX=-163.58 EndY=-38.7914 EndZ=0
    g1: LineSegment StartX=-163.58 StartY=-38.7914 StartZ=0 EndX=-170.687 EndY=-60.6657 EndZ=0
    g2: LineSegment StartX=-170.687 StartY=-60.6657 StartZ=0 EndX=-175.823 EndY=-58.997 EndZ=0
    g3: LineSegment StartX=-175.823 StartY=-58.997 StartZ=0 EndX=-168.716 EndY=-37.1227 EndZ=0
    g4: LineSegment [constr] StartX=-145.51 StartY=22 StartZ=0 EndX=-165.102 EndY=-38.297 EndZ=0
    g5: LineSegment [constr] StartX=-163.58 StartY=-38.7914 StartZ=0 EndX=-165.102 EndY=-38.297 EndZ=0
  constraints (17):
    c: Coincident(g1,g0)
    c: Coincident(g2,g1)
    c: Coincident(g3,g2)
    c: Coincident(g3,g0)
    c: Parallel(g3,g-3)
    c: Parallel(g3,g1)
    c: Perpendicular(g3,g0)
    c: Perpendicular(g2,g3)
    c: Distance(g2,g0) = 23
    c: Parallel(g4,g-3)
    c: Distance(g4) = 63.4
    c: Coincident(g4,g-3)
    c: Parallel(g5,g0)
    c: Coincident(g5,g0)
    c: Coincident(g5,g4)
    c: Distance(g4,g0) = 3.8
    c: Distance(g4,g0) = 1.6
FEATURE [Part::Extrusion] Extrude015  label="scavo rumble001"
  Base = -> Sketch019
  Dir = (0,-1,2e-16)
  DirMode = 2
  FaceMakerClass = Part::FaceMakerBullseye
  FaceMakerMode = 3
  LengthFwd = 21
  LengthRev = 0
  Solid = true
  Symmetric = true
FEATURE [Sketcher::SketchObject] Sketch020  label="fermo rumble"
  ArcFitTolerance = 1e-06
  AttachmentSupport = -> [XZ_Plane]
  ExternalGeometry = -> [Sketch019,Sketch]
  FullyConstrained = true
  MakeInternals = false
  MapMode = 5
  Placement = pos=(0,0,0) rot=(1,0,0;1.5708rad)
  sketch-geometry (16):
    g0: LineSegment [constr] StartX=-170.849 StartY=-55.9866 StartZ=0 EndX=-172.209 EndY=-60.1713 EndZ=0
    g1: LineSegment [constr] StartX=-172.209 StartY=-60.1713 StartZ=0 EndX=-170.687 EndY=-60.6657 EndZ=0
    g2: LineSegment StartX=-172.262 StartY=-53.2145 StartZ=0 EndX=-170.17 EndY=-53.8943 EndZ=0
    g3: LineSegment StartX=-170.17 StartY=-53.8943 StartZ=0 EndX=-170.849 EndY=-55.9866 EndZ=0
    g4: LineSegment StartX=-170.849 StartY=-55.9866 StartZ=0 EndX=-172.942 EndY=-55.3068 EndZ=0
    g5: LineSegment StartX=-172.942 StartY=-55.3068 StartZ=0 EndX=-172.262 EndY=-53.2145 EndZ=0
    g6: LineSegment StartX=-171.767 StartY=-51.6928 StartZ=0 EndX=-168.344 EndY=-52.8052 EndZ=0
    g7: LineSegment StartX=-168.344 StartY=-52.8052 StartZ=0 EndX=-169.951 EndY=-57.7507 EndZ=0
    g8: LineSegment StartX=-169.951 StartY=-57.7507 StartZ=0 EndX=-173.374 EndY=-56.6383 EndZ=0
    g9: LineSegment StartX=-174.402 StartY=-54.6222 StartZ=0 EndX=-173.784 EndY=-52.72 EndZ=0
    g10: LineSegment [constr] StartX=-173.784 StartY=-52.72 StartZ=0 EndX=-173.289 EndY=-51.1984 EndZ=0
    g11: LineSegment [constr] StartX=-173.289 StartY=-51.1984 StartZ=0 EndX=-171.767 EndY=-51.6928 EndZ=0
    g12: ArcOfCircle CenterX=-172.88 CenterY=-55.1166 CenterZ=0 NormalX=0 NormalY=0 NormalZ=1 AngleXU=0 Radius=1.6 StartAngle=2.82743 EndAngle=4.39823
    g13: GeomPoint [constr] X=-174.896 Y=-56.1438 Z=0
    g14: ArcOfCircle CenterX=-172.262 CenterY=-53.2145 CenterZ=0 NormalX=0 NormalY=0 NormalZ=1 AngleXU=0 Radius=1.6 StartAngle=1.25664 EndAngle=2.82743
    g15: GeomPoint [constr] X=-173.289 Y=-51.1984 Z=0
  constraints (42):
    c: Parallel(g0,g-4)
    c: Distance(g0) = 4.4
    c: Coincident(g1,g0)
    c: Perpendicular(g0,g1)
    c: Distance(g1) = 1.6
    c: Coincident(g1,g-5)
    c: Coincident(g3,g2)
    c: Coincident(g4,g3)
    c: Coincident(g5,g4)
    c: Coincident(g5,g2)
    c: Parallel(g3,g-4)
    c: Parallel(g3,g5)
    c: Perpendicular(g2,g3)
    c: Parallel(g4,g2)
    c: Distance(g2) = 2.2
    c: Distance(g3) = 2.2
    c: Coincident(g7,g6)
    c: Coincident(g8,g7)
    c: Parallel(g7,g-4)
    c: Parallel(g7,g9)
    c: Perpendicular(g6,g7)
    c: Parallel(g6,g8)
    c: Distance(g6,g15) = 5.2
    c: Distance(g7) = 5.2
    c: Coincident(g11,g10)
    c: Parallel(g10,g9)
    c: Parallel(g11,g6)
    c: Distance(g10) = 1.6
    c: Distance(g11) = 1.6
    c: Coincident(g10,g15)
    c: Distance(g11,g2) = 1.6
    c: Distance(g2,g10) = 1.6
    c: PointOnObject(g13,g8)
    c: PointOnObject(g13,g9)
    c: Tangent(g8,g12) = 1.5708
    c: Tangent(g9,g12) = 1.5708
    c: PointOnObject(g15,g9)
    c: Tangent(g6,g14) = 1.5708
    c: Tangent(g9,g14) = 1.5708
    c: Equal(g12,g14)
    c: Coincident(g6,g11)
    c: Coincident(g3,g0)
FEATURE [Part::Extrusion] Extrude016  label="Extrude fermo rumble"
  Base = -> Sketch020
  Dir = (0,-1,2e-16)
  DirMode = 2
  FaceMakerClass = Part::FaceMakerBullseye
  FaceMakerMode = 3
  LengthFwd = 25.2
  LengthRev = 0
  Solid = true
  Symmetric = true
FEATURE [Sketcher::SketchObject] Sketch021  label="perno fermo rumble001"
  ArcFitTolerance = 1e-06
  AttachmentSupport = -> [XZ_Plane001]
  FullyConstrained = true
  MakeInternals = false
  MapMode = 5
  Placement = pos=(0,0,0) rot=(1,0,0;1.5708rad)
  sketch-geometry (16):
    g0: LineSegment StartX=0 StartY=0.45 StartZ=0 EndX=0 EndY=1.55 EndZ=0
    g1: LineSegment StartX=0.45 StartY=2 StartZ=0 EndX=1.55 EndY=2 EndZ=0
    g2: LineSegment StartX=2 StartY=1.55 StartZ=0 EndX=2 EndY=0.45 EndZ=0
    g3: LineSegment StartX=1.55 StartY=0 StartZ=0 EndX=0.45 EndY=0 EndZ=0
    g4: ArcOfCircle [constr] CenterX=0.45 CenterY=1.55 CenterZ=0 NormalX=0 NormalY=0 NormalZ=1 AngleXU=0 Radius=0.45 StartAngle=1.5708 EndAngle=3.14159
    g5: GeomPoint [constr] X=0 Y=2 Z=0
    g6: LineSegment StartX=0.45 StartY=2 StartZ=0 EndX=0 EndY=1.55 EndZ=0
    g7: ArcOfCircle [constr] CenterX=1.55 CenterY=1.55 CenterZ=0 NormalX=0 NormalY=0 NormalZ=1 AngleXU=0 Radius=0.45 StartAngle=0 EndAngle=1.5708
    g8: GeomPoint [constr] X=2 Y=2 Z=0
    g9: LineSegment StartX=2 StartY=1.55 StartZ=0 EndX=1.55 EndY=2 EndZ=0
    g10: ArcOfCircle [constr] CenterX=1.55 CenterY=0.45 CenterZ=0 NormalX=0 NormalY=0 NormalZ=1 AngleXU=0 Radius=0.45 StartAngle=4.71239 EndAngle=6.28319
    g11: GeomPoint [constr] X=2 Y=0 Z=0
    g12: LineSegment StartX=1.55 StartY=0 StartZ=0 EndX=2 EndY=0.45 EndZ=0
    g13: ArcOfCircle [constr] CenterX=0.45 CenterY=0.45 CenterZ=0 NormalX=0 NormalY=0 NormalZ=1 AngleXU=0 Radius=0.45 StartAngle=3.14159 EndAngle=4.71239
    g14: GeomPoint [constr] X=0 Y=0 Z=0
    g15: LineSegment StartX=0 StartY=0.45 StartZ=0 EndX=0.45 EndY=0 EndZ=0
  constraints (35):
    c: Coincident(g14,g-1)
    c: PointOnObject(g5,g-2)
    c: Horizontal(g1)
    c: Vertical(g2)
    c: Horizontal(g3)
    c: DistanceX(g5,g8) = 2
    c: DistanceY(g11,g8) = 2
    c: PointOnObject(g5,g0)
    c: PointOnObject(g5,g1)
    c: Tangent(g0,g4) = 1.5708
    c: Tangent(g1,g4) = 1.5708
    c: Coincident(g6,g0)
    c: Coincident(g6,g1)
    c: PointOnObject(g8,g2)
    c: PointOnObject(g8,g1)
    c: Tangent(g2,g7) = 1.5708
    c: Tangent(g1,g7) = 1.5708
    c: Coincident(g9,g2)
    c: Coincident(g9,g1)
    c: PointOnObject(g11,g2)
    c: PointOnObject(g11,g3)
    c: Tangent(g2,g10) = 1.5708
    c: Tangent(g3,g10) = 1.5708
    c: Coincident(g12,g2)
    c: Coincident(g12,g3)
    c: PointOnObject(g14,g0)
    c: PointOnObject(g14,g3)
    c: Tangent(g0,g13) = 1.5708
    c: Tangent(g3,g13) = 1.5708
    c: Coincident(g15,g0)
    c: Coincident(g15,g3)
    c: Equal(g6,g9)
    c: Equal(g9,g12)
    c: Equal(g12,g15)
    c: DistanceX(g14,g3) = 0.45
FEATURE [Sketcher::SketchObject] Sketch022  label="fori per M3x5(OD)x6(L)"
  ArcFitTolerance = 1e-06
  AttachmentSupport = -> [XZ_Plane]
  ExternalGeometry = -> [Sketch016]
  FullyConstrained = true
  MakeInternals = false
  MapMode = 5
  Placement = pos=(0,0,0) rot=(1,0,0;1.5708rad)
  sketch-geometry (7):
    g0: Circle CenterX=-5.6 CenterY=34.8 CenterZ=0 NormalX=0 NormalY=0 NormalZ=1 AngleXU=0 Radius=2.5
    g1: Circle CenterX=-5.6 CenterY=7.6 CenterZ=0 NormalX=0 NormalY=0 NormalZ=1 AngleXU=0 Radius=2.5
    g2: Circle CenterX=-78.51 CenterY=34.8 CenterZ=0 NormalX=0 NormalY=0 NormalZ=1 AngleXU=0 Radius=2.5
    g3: Circle CenterX=-78.51 CenterY=7.6 CenterZ=0 NormalX=0 NormalY=0 NormalZ=1 AngleXU=0 Radius=2.5
    g4: Circle CenterX=-184.08 CenterY=34.8 CenterZ=0 NormalX=0 NormalY=0 NormalZ=1 AngleXU=0 Radius=2.5
    g5: Circle CenterX=-179.305 CenterY=-76.8316 CenterZ=0 NormalX=0 NormalY=0 NormalZ=1 AngleXU=0 Radius=2.5
    g6: Circle CenterX=-213.443 CenterY=-76.8316 CenterZ=0 NormalX=0 NormalY=0 NormalZ=1 AngleXU=0 Radius=2.5
  constraints (14):
    c: Diameter(g0) = 5
    c: Diameter(g1) = 5
    c: Diameter(g2) = 5
    c: Diameter(g3) = 5
    c: Diameter(g4) = 5
    c: Diameter(g5) = 5
    c: Diameter(g6) = 5
    c: Coincident(g0,g-8)
    c: Coincident(g1,g-9)
    c: Coincident(g2,g-6)
    c: Coincident(g3,g-7)
    c: Coincident(g4,g-5)
    c: Coincident(g5,g-4)
    c: Coincident(g6,g-3)
FEATURE [Part::Extrusion] Extrude018  label="Extrude fori M3x5x6 - dx"
  Base = -> Sketch022
  Dir = (0,-1,2e-16)
  DirMode = 2
  FaceMakerClass = Part::FaceMakerBullseye
  FaceMakerMode = 3
  LengthFwd = 6.2
  LengthRev = 0
  Placement = pos=(0,-9.5,0) rot=(0,0,1;0rad)
  Solid = true
  Symmetric = true
FEATURE [Part::Extrusion] Extrude019  label="Extrude fori M3x5x6 - sx"
  Base = -> Sketch022
  Dir = (0,-1,2e-16)
  DirMode = 2
  FaceMakerClass = Part::FaceMakerBullseye
  FaceMakerMode = 3
  LengthFwd = 6.2
  LengthRev = 0
  Placement = pos=(0,9.5,0) rot=(0,0,1;0rad)
  Solid = true
  Symmetric = true
FEATURE [Sketcher::SketchObject] Sketch023  label="foro anteriore M3x5x6"
  ArcFitTolerance = 1e-06
  AttachmentSupport = -> [YZ_Plane]
  FullyConstrained = true
  MakeInternals = false
  MapMode = 5
  Placement = pos=(0,0,0) rot=(0.57735,0.57735,0.57735;2.0944rad)
  sketch-geometry (2):
    g0: LineSegment [constr] StartX=0 StartY=0 StartZ=0 EndX=0 EndY=38.6 EndZ=0
    g1: Circle CenterX=0 CenterY=38.6 CenterZ=0 NormalX=0 NormalY=0 NormalZ=1 AngleXU=0 Radius=2.5
  constraints (5):
    c: Coincident(g0,g-1)
    c: PointOnObject(g0,g-2)
    c: DistanceY(g0,g0) = 38.6
    c: Diameter(g1) = 5
    c: Coincident(g1,g0)
FEATURE [Part::Extrusion] Extrude020  label="Extrude foro anteriore M3x5x6"
  Base = -> Sketch023
  Dir = (1,0,0)
  DirMode = 2
  FaceMakerClass = Part::FaceMakerBullseye
  FaceMakerMode = 3
  LengthFwd = -6.2
  LengthRev = 0
  Solid = true
  Symmetric = false
FEATURE [Sketcher::SketchObject] Sketch024  label="fori per viti frontale"
  ArcFitTolerance = 1e-06
  AttachmentSupport = -> [YZ_Plane]
  FullyConstrained = true
  MakeInternals = false
  MapMode = 5
  Placement = pos=(0,0,0) rot=(0.57735,0.57735,0.57735;2.0944rad)
  sketch-geometry (9):
    g0: LineSegment [constr] StartX=-10.3 StartY=30.721 StartZ=0 EndX=10.3 EndY=30.721 EndZ=0
    g1: LineSegment [constr] StartX=10.3 StartY=30.721 StartZ=0 EndX=10.3 EndY=10.121 EndZ=0
    g2: LineSegment [constr] StartX=10.3 StartY=10.121 StartZ=0 EndX=-10.3 EndY=10.121 EndZ=0
    g3: LineSegment [constr] StartX=-10.3 StartY=10.121 StartZ=0 EndX=-10.3 EndY=30.721 EndZ=0
    g4: LineSegment [constr] StartX=0 StartY=0 StartZ=0 EndX=0 EndY=10.121 EndZ=0
    g5: Circle CenterX=-10.3 CenterY=30.721 CenterZ=0 NormalX=0 NormalY=0 NormalZ=1 AngleXU=0 Radius=2
    g6: Circle CenterX=10.3 CenterY=30.721 CenterZ=0 NormalX=0 NormalY=0 NormalZ=1 AngleXU=0 Radius=2
    g7: Circle CenterX=-10.3 CenterY=10.121 CenterZ=0 NormalX=0 NormalY=0 NormalZ=1 AngleXU=0 Radius=2
    g8: Circle CenterX=10.3 CenterY=10.121 CenterZ=0 NormalX=0 NormalY=0 NormalZ=1 AngleXU=0 Radius=2
  constraints (22):
    c: Horizontal(g0)
    c: Coincident(g1,g0)
    c: Vertical(g1)
    c: Coincident(g2,g1)
    c: Horizontal(g2)
    c: Coincident(g3,g2)
    c: Coincident(g3,g0)
    c: Vertical(g3)
    c: DistanceX(g0,g0) = 20.6
    c: DistanceY(g3,g3) = 20.6
    c: Coincident(g4,g-1)
    c: PointOnObject(g4,g-2)
    c: DistanceY(g4,g4) = 10.121
    c: Symmetric(g2,g2,g4)
    c: Diameter(g5) = 4
    c: Diameter(g6) = 4
    c: Diameter(g7) = 4
    c: Diameter(g8) = 4
    c: Coincident(g5,g0)
    c: Coincident(g6,g0)
    c: Coincident(g7,g2)
    c: Coincident(g8,g1)
FEATURE [Part::Extrusion] Extrude021  label="Extrude fori per viti frontale"
  Base = -> Sketch024
  Dir = (1,0,0)
  DirMode = 2
  FaceMakerClass = Part::FaceMakerBullseye
  FaceMakerMode = 3
  LengthFwd = -2.4
  LengthRev = 0
  Solid = true
  Symmetric = false
FEATURE [Sketcher::SketchObject] Sketch025  label="foro per filo CAM"
  ArcFitTolerance = 1e-06
  AttachmentSupport = -> [XZ_Plane]
  ExternalGeometry = -> [Sketch]
  FullyConstrained = true
  MakeInternals = false
  MapMode = 5
  Placement = pos=(0,0,0) rot=(1,0,0;1.5708rad)
  sketch-geometry (4):
    g0: LineSegment StartX=-44.6 StartY=41.2 StartZ=0 EndX=-44.6 EndY=36.4 EndZ=0
    g1: LineSegment StartX=-44.6 StartY=36.4 StartZ=0 EndX=-54.6 EndY=36.4 EndZ=0
    g2: LineSegment StartX=-54.6 StartY=36.4 StartZ=0 EndX=-50.4 EndY=41.2 EndZ=0
    g3: LineSegment StartX=-50.4 StartY=41.2 StartZ=0 EndX=-44.6 EndY=41.2 EndZ=0
  constraints (11):
    c: Vertical(g0)
    c: Coincident(g1,g0)
    c: Horizontal(g1)
    c: Coincident(g2,g1)
    c: Coincident(g3,g2)
    c: Coincident(g3,g0)
    c: Horizontal(g3)
    c: Coincident(g0,g-3)
    c: DistanceY(g0,g-4) = 0
    c: DistanceX(g3,g3) = 5.8
    c: DistanceX(g1,g1) = 10
FEATURE [Part::Extrusion] Extrude022  label="Extrude foro per filo CAM dx"
  Base = -> Sketch025
  Dir = (0,-1,2e-16)
  DirMode = 2
  FaceMakerClass = Part::FaceMakerBullseye
  FaceMakerMode = 3
  LengthFwd = 4.9
  LengthRev = 0
  Placement = pos=(0,6.95,0) rot=(0,0,1;0rad)
  Solid = true
  Symmetric = true
FEATURE [Part::Extrusion] Extrude023  label="Extrude foro per filo CAM sx"
  Base = -> Sketch025
  Dir = (0,-1,2e-16)
  DirMode = 2
  FaceMakerClass = Part::FaceMakerBullseye
  FaceMakerMode = 3
  LengthFwd = 4.9
  LengthRev = 0
  Placement = pos=(0,-6.95,0) rot=(0,0,1;0rad)
  Solid = true
  Symmetric = true
FEATURE [Sketcher::SketchObject] Sketch026  label="foro sotto anteriore M3x5x6"
  ArcFitTolerance = 1e-06
  AttachmentSupport = -> [XY_Plane]
  FullyConstrained = true
  MakeInternals = false
  MapMode = 5
  sketch-geometry (2):
    g0: LineSegment [constr] StartX=0 StartY=0 StartZ=0 EndX=-16.5 EndY=0 EndZ=0
    g1: Circle CenterX=-16.5 CenterY=0 CenterZ=0 NormalX=0 NormalY=0 NormalZ=1 AngleXU=0 Radius=2.5
  constraints (5):
    c: Distance(g0) = 16.5
    c: Coincident(g0,g-1)
    c: PointOnObject(g0,g-1)
    c: Diameter(g1) = 5
    c: Coincident(g0,g1)
FEATURE [Sketcher::SketchObject] Sketch027  label="foro sotto posteriore M3x5x6"
  ArcFitTolerance = 1e-06
  AttachmentSupport = -> [XY_Plane]
  ExternalGeometry = -> [Sketch]
  FullyConstrained = true
  MakeInternals = false
  MapMode = 5
  sketch-geometry (2):
    g0: LineSegment [constr] StartX=-82.8 StartY=2e-16 StartZ=0 EndX=-71.3 EndY=2e-16 EndZ=0
    g1: Circle CenterX=-71.3 CenterY=2e-16 CenterZ=0 NormalX=0 NormalY=0 NormalZ=1 AngleXU=0 Radius=2.5
  constraints (5):
    c: Distance(g0) = 11.5
    c: Coincident(g0,g-3)
    c: PointOnObject(g0,g-3)
    c: Diameter(g1) = 5
    c: Coincident(g1,g0)
FEATURE [Sketcher::SketchObject] Sketch029  label="fori sotto impugnatura"
  ArcFitTolerance = 1e-06
  AttachmentSupport = -> [XY_Plane]
  ExternalGeometry = -> [Sketch]
  FullyConstrained = true
  MakeInternals = false
  MapMode = 5
  sketch-geometry (15):
    g0: LineSegment [constr] StartX=-175.232 StartY=-1.83e-14 StartZ=0 EndX=-191.232 EndY=0 EndZ=0
    g1: Circle CenterX=-191.232 CenterY=0 CenterZ=0 NormalX=0 NormalY=0 NormalZ=1 AngleXU=0 Radius=3.95
    g2: LineSegment [constr] StartX=-175.232 StartY=-1.83e-14 StartZ=0 EndX=-204.275 EndY=0 EndZ=0
    g3: LineSegment StartX=-204.275 StartY=3.525 StartZ=0 EndX=-204.275 EndY=-3.525 EndZ=0
    g4: LineSegment StartX=-205.4 StartY=-4.65 StartZ=0 EndX=-206.65 EndY=-4.65 EndZ=0
    g5: LineSegment StartX=-207.775 StartY=-3.525 StartZ=0 EndX=-207.775 EndY=3.525 EndZ=0
    g6: LineSegment StartX=-206.65 StartY=4.65 StartZ=0 EndX=-205.4 EndY=4.65 EndZ=0
    g7: ArcOfCircle CenterX=-206.65 CenterY=3.525 CenterZ=0 NormalX=0 NormalY=0 NormalZ=1 AngleXU=0 Radius=1.125 StartAngle=1.5708 EndAngle=3.14159
    g8: GeomPoint [constr] X=-207.775 Y=4.65 Z=0
    g9: ArcOfCircle CenterX=-205.4 CenterY=3.525 CenterZ=0 NormalX=0 NormalY=0 NormalZ=1 AngleXU=0 Radius=1.125 StartAngle=0 EndAngle=1.5708
    g10: GeomPoint [constr] X=-204.275 Y=4.65 Z=0
    g11: ArcOfCircle CenterX=-205.4 CenterY=-3.525 CenterZ=0 NormalX=0 NormalY=0 NormalZ=1 AngleXU=0 Radius=1.125 StartAngle=4.71239 EndAngle=6.28319
    g12: GeomPoint [constr] X=-204.275 Y=-4.65 Z=0
    g13: ArcOfCircle CenterX=-206.65 CenterY=-3.525 CenterZ=0 NormalX=0 NormalY=0 NormalZ=1 AngleXU=0 Radius=1.125 StartAngle=3.14159 EndAngle=4.71239
    g14: GeomPoint [constr] X=-207.775 Y=-4.65 Z=0
  constraints (35):
    c: Distance(g0) = 16
    c: Coincident(g0,g-3)
    c: PointOnObject(g0,g-1)
    c: Diameter(g1) = 7.9
    c: Coincident(g1,g0)
    c: Coincident(g2,g0)
    c: PointOnObject(g2,g-1)
    c: Vertical(g3)
    c: Horizontal(g4)
    c: Vertical(g5)
    c: Horizontal(g6)
    c: DistanceY(g12,g10) = 9.3
    c: DistanceX(g8,g10) = 3.5
    c: Symmetric(g10,g12,g2)
    c: PointOnObject(g8,g5)
    c: PointOnObject(g8,g6)
    c: Tangent(g5,g7) = 1.5708
    c: Tangent(g6,g7) = 1.5708
    c: PointOnObject(g10,g3)
    c: PointOnObject(g10,g6)
    c: Tangent(g3,g9) = 1.5708
    c: Tangent(g6,g9) = 1.5708
    c: PointOnObject(g12,g3)
    c: PointOnObject(g12,g4)
    c: Tangent(g3,g11) = 1.5708
    c: Tangent(g4,g11) = 1.5708
    c: PointOnObject(g14,g4)
    c: PointOnObject(g14,g5)
    c: Tangent(g4,g13) = 1.5708
    c: Tangent(g5,g13) = 1.5708
    c: Equal(g7,g9)
    c: Equal(g9,g11)
    c: Equal(g11,g13)
    c: DistanceX(g6,g6) = 1.25
    c: DistanceX(g-5,g5) = 6.8
FEATURE [Sketcher::SketchObject] Sketch030  label="fori superiori per solenoide e oled"
  ArcFitTolerance = 1e-06
  AttachmentSupport = -> [XY_Plane]
  ExternalGeometry = -> [Sketch]
  FullyConstrained = true
  MakeInternals = false
  MapMode = 5
  sketch-geometry (33):
    g0: LineSegment [constr] StartX=-181.6 StartY=1.12e-14 StartZ=0 EndX=-169.91 EndY=0 EndZ=0
    g1: LineSegment [constr] StartX=-169.91 StartY=0 StartZ=0 EndX=-169.91 EndY=-2.6 EndZ=0
    g2: LineSegment [constr] StartX=-169.91 StartY=0 StartZ=0 EndX=-169.91 EndY=2.6 EndZ=0
    g3: LineSegment StartX=-169.91 StartY=4.975 StartZ=0 EndX=-169.91 EndY=8.225 EndZ=0
    g4: LineSegment StartX=-167.535 StartY=10.6 StartZ=0 EndX=-167.285 EndY=10.6 EndZ=0
    g5: LineSegment StartX=-164.91 StartY=8.225 StartZ=0 EndX=-164.91 EndY=4.975 EndZ=0
    g6: LineSegment StartX=-167.285 StartY=2.6 StartZ=0 EndX=-167.535 EndY=2.6 EndZ=0
    g7: LineSegment StartX=-169.91 StartY=-4.975 StartZ=0 EndX=-169.91 EndY=-8.225 EndZ=0
    g8: LineSegment StartX=-167.535 StartY=-10.6 StartZ=0 EndX=-167.285 EndY=-10.6 EndZ=0
    g9: LineSegment StartX=-164.91 StartY=-8.225 StartZ=0 EndX=-164.91 EndY=-4.975 EndZ=0
    g10: LineSegment StartX=-167.285 StartY=-2.6 StartZ=0 EndX=-167.535 EndY=-2.6 EndZ=0
    g11: ArcOfCircle CenterX=-167.535 CenterY=8.225 CenterZ=0 NormalX=0 NormalY=0 NormalZ=1 AngleXU=0 Radius=2.375 StartAngle=1.5708 EndAngle=3.14159
    g12: GeomPoint [constr] X=-169.91 Y=10.6 Z=0
    g13: ArcOfCircle CenterX=-167.285 CenterY=8.225 CenterZ=0 NormalX=0 NormalY=0 NormalZ=1 AngleXU=0 Radius=2.375 StartAngle=0 EndAngle=1.5708
    g14: GeomPoint [constr] X=-164.91 Y=10.6 Z=0
    g15: ArcOfCircle CenterX=-167.285 CenterY=4.975 CenterZ=0 NormalX=0 NormalY=0 NormalZ=1 AngleXU=0 Radius=2.375 StartAngle=4.71239 EndAngle=6.28319
    g16: GeomPoint [constr] X=-164.91 Y=2.6 Z=0
    g17: ArcOfCircle CenterX=-167.535 CenterY=4.975 CenterZ=0 NormalX=0 NormalY=0 NormalZ=1 AngleXU=0 Radius=2.375 StartAngle=3.14159 EndAngle=4.71239
    g18: GeomPoint [constr] X=-169.91 Y=2.6 Z=0
    g19: ArcOfCircle CenterX=-167.535 CenterY=-4.975 CenterZ=0 NormalX=0 NormalY=0 NormalZ=1 AngleXU=0 Radius=2.375 StartAngle=1.5708 EndAngle=3.14159
    g20: GeomPoint [constr] X=-169.91 Y=-2.6 Z=0
    g21: ArcOfCircle CenterX=-167.285 CenterY=-4.975 CenterZ=0 NormalX=0 NormalY=0 NormalZ=1 AngleXU=0 Radius=2.375 StartAngle=0 EndAngle=1.5708
    g22: GeomPoint [constr] X=-164.91 Y=-2.6 Z=0
    g23: ArcOfCircle CenterX=-167.285 CenterY=-8.225 CenterZ=0 NormalX=0 NormalY=0 NormalZ=1 AngleXU=0 Radius=2.375 StartAngle=4.71239 EndAngle=6.28319
    g24: GeomPoint [constr] X=-164.91 Y=-10.6 Z=0
    g25: ArcOfCircle CenterX=-167.535 CenterY=-8.225 CenterZ=0 NormalX=0 NormalY=0 NormalZ=1 AngleXU=0 Radius=2.375 StartAngle=3.14159 EndAngle=4.71239
    g26: GeomPoint [constr] X=-169.91 Y=-10.6 Z=0
    g27: LineSegment [constr] StartX=-181.6 StartY=1.12e-14 StartZ=0 EndX=-152.209 EndY=0 EndZ=0
    g28: LineSegment [constr] StartX=-181.6 StartY=1.12e-14 StartZ=0 EndX=-130.41 EndY=0 EndZ=0
    g29: LineSegment [constr] StartX=-152.209 StartY=0 StartZ=0 EndX=-152.209 EndY=6.95 EndZ=0
    g30: LineSegment [constr] StartX=-130.41 StartY=0 StartZ=0 EndX=-130.41 EndY=-6.95 EndZ=0
    g31: Circle CenterX=-152.209 CenterY=6.95 CenterZ=0 NormalX=0 NormalY=0 NormalZ=1 AngleXU=0 Radius=2.1
    g32: Circle CenterX=-130.41 CenterY=-6.95 CenterZ=0 NormalX=0 NormalY=0 NormalZ=1 AngleXU=0 Radius=2.1
  constraints (79):
    c: Distance(g0) = 11.69
    c: PointOnObject(g0,g-1)
    c: Coincident(g-4,g0)
    c: Distance(g1) = 2.6
    c: Coincident(g1,g0)
    c: Vertical(g1)
    c: Distance(g2) = 2.6
    c: Coincident(g2,g0)
    c: Vertical(g2)
    c: Distance(g18,g12) = 8
    c: Coincident(g18,g2)
    c: Vertical(g3)
    c: Distance(g14,g12) = 5
    c: Horizontal(g4)
    c: Distance(g16,g14) = 8
    c: Vertical(g5)
    c: Distance(g26,g20) = 8
    c: Coincident(g20,g1)
    c: Vertical(g7)
    c: Distance(g26,g24) = 5
    c: Horizontal(g8)
    c: Distance(g24,g22) = 8
    c: Vertical(g9)
    c: PointOnObject(g12,g3)
    c: PointOnObject(g12,g4)
    c: Tangent(g3,g11) = 1.5708
    c: Tangent(g4,g11) = 1.5708
    c: PointOnObject(g14,g5)
    c: PointOnObject(g14,g4)
    c: Tangent(g5,g13) = 1.5708
    c: Tangent(g4,g13) = 1.5708
    c: PointOnObject(g16,g5)
    c: PointOnObject(g16,g6)
    c: Tangent(g5,g15) = 1.5708
    c: Tangent(g6,g15) = 1.5708
    c: PointOnObject(g18,g3)
    c: PointOnObject(g18,g6)
    c: Tangent(g3,g17) = 1.5708
    c: Tangent(g6,g17) = 1.5708
    c: Equal(g11,g13)
    c: Equal(g13,g15)
    c: Equal(g15,g17)
    c: DistanceX(g4,g4) = 0.25
    c: PointOnObject(g20,g7)
    c: PointOnObject(g20,g10)
    c: Tangent(g7,g19) = -1.5708
    c: Tangent(g10,g19) = -1.5708
    c: PointOnObject(g22,g9)
    c: PointOnObject(g22,g10)
    c: Tangent(g9,g21) = -1.5708
    c: Tangent(g10,g21) = -1.5708
    c: PointOnObject(g24,g9)
    c: PointOnObject(g24,g8)
    c: Tangent(g9,g23) = -1.5708
    c: Tangent(g8,g23) = -1.5708
    c: PointOnObject(g26,g8)
    c: PointOnObject(g26,g7)
    c: Tangent(g8,g25) = -1.5708
    c: Tangent(g7,g25) = -1.5708
    c: Equal(g19,g21)
    c: Equal(g21,g23)
    c: Equal(g23,g25)
    c: DistanceX(g10,g10) = 0.25
    c: Distance(g27) = 29.391
    c: Coincident(g27,g0)
    c: PointOnObject(g27,g-1)
    c: Distance(g28) = 51.19
    c: Coincident(g28,g0)
    c: PointOnObject(g28,g-1)
    c: Distance(g29) = 6.95
    c: Coincident(g29,g27)
    c: Vertical(g29)
    c: Distance(g30) = 6.95
    c: Coincident(g30,g28)
    c: Vertical(g30)
    c: Diameter(g31) = 4.2
    c: Diameter(g32) = 4.2
    c: Coincident(g32,g30)
    c: Coincident(g31,g29)
FEATURE [Sketcher::SketchObject] Sketch031  label="fori inferiori switch pompa"
  ArcFitTolerance = 1e-06
  AttachmentSupport = -> [XY_Plane]
  ExternalGeometry = -> [Sketch]
  FullyConstrained = true
  MakeInternals = false
  MapMode = 5
  sketch-geometry (4):
    g0: LineSegment [constr] StartX=-57.2 StartY=1.9e-15 StartZ=0 EndX=-62.45 EndY=1.9e-15 EndZ=0
    g1: LineSegment [constr] StartX=-62.45 StartY=3.25 StartZ=0 EndX=-62.45 EndY=-3.25 EndZ=0
    g2: Circle CenterX=-62.45 CenterY=3.25 CenterZ=0 NormalX=0 NormalY=0 NormalZ=1 AngleXU=0 Radius=1.6
    g3: Circle CenterX=-62.45 CenterY=-3.25 CenterZ=0 NormalX=0 NormalY=0 NormalZ=1 AngleXU=0 Radius=1.6
  constraints (10):
    c: Distance(g0) = 5.25
    c: Coincident(g0,g-3)
    c: PointOnObject(g0,g-3)
    c: Vertical(g1)
    c: DistanceY(g1,g1) = 6.5
    c: Symmetric(g1,g1,g0)
    c: Diameter(g2) = 3.2
    c: Diameter(g3) = 3.2
    c: Coincident(g2,g1)
    c: Coincident(g3,g1)
FEATURE [Sketcher::SketchObject] Sketch032  label="spazio per PILA 18650"
  ArcFitTolerance = 1e-06
  AttachmentSupport = -> [XY_Plane]
  ExternalGeometry = -> [Sketch]
  FullyConstrained = true
  MakeInternals = false
  MapMode = 5
  sketch-geometry (2):
    g0: LineSegment [constr] StartX=-178.142 StartY=-1.74e-14 StartZ=0 EndX=-191.142 EndY=-1.83e-14 EndZ=0
    g1: Circle CenterX=-191.142 CenterY=-1.83e-14 CenterZ=0 NormalX=0 NormalY=0 NormalZ=1 AngleXU=0 Radius=10.5
  constraints (5):
    c: Distance(g0) = 13
    c: Coincident(g0,g-3)
    c: PointOnObject(g0,g-4)
    c: Diameter(g1) = 21
    c: Coincident(g1,g0)
FEATURE [Part::Extrusion] Extrude030  label="Extrude spazio per PILA 18650"
  Base = -> Sketch032
  Dir = (0,0,1)
  DirLink = -> Sketch [Edge45]
  DirMode = 2
  FaceMakerClass = Part::FaceMakerBullseye
  FaceMakerMode = 3
  LengthFwd = 76
  LengthRev = 0
  Placement = pos=(6,0,-72) rot=(0,0,1;0rad)
  Solid = true
  Symmetric = false
FEATURE [Sketcher::SketchObject] Sketch033  label="fermo per scheda micro"
  ArcFitTolerance = 1e-06
  AttachmentSupport = -> [XZ_Plane]
  ExternalGeometry = -> [Sketch]
  FullyConstrained = true
  MakeInternals = false
  MapMode = 5
  Placement = pos=(0,0,0) rot=(1,0,0;1.5708rad)
  sketch-geometry (12):
    g0: LineSegment StartX=-11.6 StartY=6 StartZ=0 EndX=-4 EndY=6 EndZ=0
    g1: LineSegment StartX=-4 StartY=6 StartZ=0 EndX=-4 EndY=36.4 EndZ=0
    g2: LineSegment StartX=-4 StartY=36.4 StartZ=0 EndX=-11.6 EndY=36.4 EndZ=0
    g3: LineSegment StartX=-11.6 StartY=36.4 StartZ=0 EndX=-11.6 EndY=6 EndZ=0
    g4: LineSegment StartX=-80.11 StartY=11.6 StartZ=0 EndX=-70.51 EndY=11.6 EndZ=0
    g5: LineSegment StartX=-70.51 StartY=11.6 StartZ=0 EndX=-70.51 EndY=6 EndZ=0
    g6: LineSegment StartX=-70.51 StartY=6 StartZ=0 EndX=-80.11 EndY=6 EndZ=0
    g7: LineSegment StartX=-80.11 StartY=6 StartZ=0 EndX=-80.11 EndY=11.6 EndZ=0
    g8: LineSegment StartX=-78.51 StartY=36.4 StartZ=0 EndX=-70.51 EndY=36.4 EndZ=0
    g9: LineSegment StartX=-70.51 StartY=36.4 StartZ=0 EndX=-70.51 EndY=30.8 EndZ=0
    g10: LineSegment StartX=-70.51 StartY=30.8 StartZ=0 EndX=-78.51 EndY=30.8 EndZ=0
    g11: LineSegment StartX=-78.51 StartY=30.8 StartZ=0 EndX=-78.51 EndY=36.4 EndZ=0
  constraints (33):
    c: Horizontal(g0)
    c: Coincident(g1,g0)
    c: Coincident(g2,g1)
    c: Horizontal(g2)
    c: Coincident(g3,g2)
    c: Coincident(g3,g0)
    c: Vertical(g3)
    c: DistanceX(g2,g2) = 7.6
    c: Coincident(g1,g-3)
    c: Coincident(g0,g-3)
    c: Horizontal(g4)
    c: Coincident(g5,g4)
    c: Vertical(g5)
    c: Coincident(g6,g5)
    c: Horizontal(g6)
    c: Coincident(g7,g6)
    c: Coincident(g7,g4)
    c: Vertical(g7)
    c: DistanceY(g5,g5) = 5.6
    c: DistanceX(g4,g4) = 9.6
    c: Coincident(g9,g8)
    c: Vertical(g9)
    c: Coincident(g10,g9)
    c: Horizontal(g10)
    c: Coincident(g11,g10)
    c: Coincident(g11,g8)
    c: Vertical(g11)
    c: DistanceY(g9,g9) = 5.6
    c: DistanceX(g10,g10) = 8
    c: Coincident(g4,g-4)
    c: DistanceX(g4,g10) = 1.6
    c: Horizontal(g8)
    c: DistanceY(g8,g1) = 0
FEATURE [Sketcher::SketchObject] Sketch034  label="buchi guida rail"
  ArcFitTolerance = 1e-06
  AttachmentSupport = -> [XY_Plane]
  ExternalGeometry = -> [Sketch]
  FullyConstrained = true
  MakeInternals = false
  MapMode = 5
  sketch-geometry (6):
    g0: LineSegment [constr] StartX=-100.8 StartY=9.1e-15 StartZ=0 EndX=-93.3 EndY=0 EndZ=0
    g1: LineSegment [constr] StartX=-93.3 StartY=0 StartZ=0 EndX=-73.3 EndY=0 EndZ=0
    g2: LineSegment [constr] StartX=-73.3 StartY=0 StartZ=0 EndX=-53.3 EndY=0 EndZ=0
    g3: Circle CenterX=-93.3 CenterY=0 CenterZ=0 NormalX=0 NormalY=0 NormalZ=1 AngleXU=0 Radius=2.5
    g4: Circle CenterX=-73.3 CenterY=0 CenterZ=0 NormalX=0 NormalY=0 NormalZ=1 AngleXU=0 Radius=2.5
    g5: Circle CenterX=-53.3 CenterY=0 CenterZ=0 NormalX=0 NormalY=0 NormalZ=1 AngleXU=0 Radius=2.5
  constraints (15):
    c: Distance(g0) = 7.5
    c: Coincident(g0,g-3)
    c: PointOnObject(g0,g-1)
    c: Distance(g1) = 20
    c: Coincident(g1,g0)
    c: PointOnObject(g1,g-1)
    c: Distance(g2) = 20
    c: Coincident(g2,g1)
    c: PointOnObject(g2,g-1)
    c: Diameter(g3) = 5
    c: Diameter(g4) = 5
    c: Diameter(g5) = 5
    c: Coincident(g3,g0)
    c: Coincident(g4,g1)
    c: Coincident(g5,g2)
FEATURE [Part::Extrusion] Extrude032  label="Extrude buchi guida rail"
  Base = -> Sketch034
  Dir = (0,0,1)
  DirMode = 2
  FaceMakerClass = Part::FaceMakerBullseye
  FaceMakerMode = 3
  LengthFwd = -6.2
  LengthRev = 0
  Placement = pos=(0,0,43.2) rot=(0,0,1;0rad)
  Solid = true
  Symmetric = false
FEATURE [Part::Extrusion] Extrude033  label="Extrude fori superiori per solenoide e oled001"
  Base = -> Sketch030
  Dir = (0,0,1)
  DirMode = 2
  FaceMakerClass = Part::FaceMakerBullseye
  FaceMakerMode = 3
  LengthFwd = -4.8
  LengthRev = 0
  Placement = pos=(0,0,41.2) rot=(0,0,1;0rad)
  Solid = true
  Symmetric = false
FEATURE [Part::Extrusion] Extrude034  label="Extrude fori sotto impugnatura001"
  Base = -> Sketch029
  Dir = (0,0,1)
  DirMode = 2
  FaceMakerClass = Part::FaceMakerBullseye
  FaceMakerMode = 3
  LengthFwd = 5
  LengthRev = 0
  Placement = pos=(0,0,-83) rot=(0,0,1;0rad)
  Solid = true
  Symmetric = false
FEATURE [Part::Extrusion] Extrude035  label="Extrude fori inferiori switch pompa001"
  Base = -> Sketch031
  Dir = (0,0,1)
  DirMode = 2
  FaceMakerClass = Part::FaceMakerBullseye
  FaceMakerMode = 3
  LengthFwd = 4
  LengthRev = 0
  Placement = pos=(0,0,-1.7) rot=(0,0,1;0rad)
  Solid = true
  Symmetric = false
FEATURE [Part::Extrusion] Extrude036  label="Extrude foro sotto posteriore M3x5x007"
  Base = -> Sketch027
  Dir = (0,0,1)
  DirMode = 2
  FaceMakerClass = Part::FaceMakerBullseye
  FaceMakerMode = 3
  LengthFwd = 6.2
  LengthRev = 0
  Placement = pos=(0,0,-9.6) rot=(0,0,1;0rad)
  Solid = true
  Symmetric = false
FEATURE [Part::Extrusion] Extrude037  label="Extrude foro sotto anteriore M3x5x007"
  Base = -> Sketch026
  Dir = (0,0,1)
  DirMode = 2
  FaceMakerClass = Part::FaceMakerBullseye
  FaceMakerMode = 3
  LengthFwd = 6.2
  LengthRev = 0
  Solid = true
  Symmetric = false
FEATURE [Sketcher::SketchObject] Sketch035  label="foro per fissaggio micro"
  ArcFitTolerance = 1e-06
  AttachmentSupport = -> [XZ_Plane]
  ExternalGeometry = -> [Sketch,Sketch033]
  FullyConstrained = true
  MakeInternals = false
  MapMode = 5
  Placement = pos=(0,0,0) rot=(1,0,0;1.5708rad)
  sketch-geometry (3):
    g0: Circle CenterX=-7.8 CenterY=21.2 CenterZ=0 NormalX=0 NormalY=0 NormalZ=1 AngleXU=0 Radius=1.6
    g1: GeomPoint [constr] X=-4 Y=21.2 Z=0
    g2: LineSegment [constr] StartX=-4 StartY=21.2 StartZ=0 EndX=-11.6 EndY=21.2 EndZ=0
  constraints (6):
    c: Diameter(g0) = 3.2
    c: Symmetric(g-3,g-3,g1)
    c: Coincident(g2,g1)
    c: Horizontal(g2)
    c: DistanceX(g-4,g2) = 0
    c: Symmetric(g2,g1,g0)
FEATURE [Part::Extrusion] Extrude038  label="Extrude foro per fissaggio micro"
  Base = -> Sketch035
  Dir = (0,-1,2e-16)
  DirMode = 2
  FaceMakerClass = Part::FaceMakerBullseye
  FaceMakerMode = 3
  LengthFwd = 3
  LengthRev = 0
  Placement = pos=(0,8.6,0) rot=(0,0,1;0rad)
  Solid = true
  Symmetric = false
FEATURE [Sketcher::SketchObject] Sketch036  label="supporto per alimentatore"
  ArcFitTolerance = 1e-06
  AttachmentSupport = -> [XZ_Plane]
  ExternalGeometry = -> [Sketch,Sketch016,Sketch022]
  FullyConstrained = true
  MakeInternals = false
  MapMode = 5
  Placement = pos=(0,0,0) rot=(1,0,0;1.5708rad)
  sketch-geometry (5):
    g0: LineSegment StartX=-211.843 StartY=-50.0944 StartZ=0 EndX=-211.843 EndY=-80.4316 EndZ=0
    g1: LineSegment StartX=-211.843 StartY=-50.0944 StartZ=0 EndX=-207.775 EndY=-41.3701 EndZ=0
    g2: LineSegment [constr] StartX=-209.443 StartY=-50.0944 StartZ=0 EndX=-209.443 EndY=-80.4316 EndZ=0
    g3: LineSegment StartX=-207.775 StartY=-41.3701 StartZ=0 EndX=-207.775 EndY=-80.4316 EndZ=0
    g4: LineSegment StartX=-211.843 StartY=-80.4316 StartZ=0 EndX=-207.775 EndY=-80.4316 EndZ=0
  constraints (15):
    c: Vertical(g0)
    c: Coincident(g1,g0)
    c: Vertical(g2)
    c: Tangent(g2,g-5)
    c: Coincident(g3,g1)
    c: Vertical(g3)
    c: DistanceY(g-3,g3) = -2
    c: Tangent(g1,g-8)
    c: DistanceY(g-3,g0) = -2
    c: Coincident(g4,g0)
    c: Coincident(g4,g3)
    c: Tangent(g0,g-6)
    c: DistanceY(g-3,g2) = -2
    c: DistanceY(g2,g0) = 0
    c: DistanceX(g-3,g3) = 6.8
FEATURE [Part::Extrusion] Extrude039  label="Extrude039 supporto alimentatore"
  Base = -> Sketch036
  Dir = (0,-1,2e-16)
  DirMode = 2
  FaceMakerClass = Part::FaceMakerBullseye
  FaceMakerMode = 3
  LengthFwd = 25.2
  LengthRev = 0
  Solid = true
  Symmetric = true
FEATURE [Sketcher::SketchObject] Sketch037  label="scavo per alimentatore"
  ArcFitTolerance = 1e-06
  AttachmentSupport = -> [XZ_Plane]
  ExternalGeometry = -> [Sketch036]
  FullyConstrained = true
  MakeInternals = false
  MapMode = 5
  Placement = pos=(0,0,0) rot=(1,0,0;1.5708rad)
  sketch-geometry (4):
    g0: LineSegment StartX=-209.575 StartY=-50.4316 StartZ=0 EndX=-209.575 EndY=-80.4316 EndZ=0
    g1: LineSegment StartX=-209.575 StartY=-50.4316 StartZ=0 EndX=-207.775 EndY=-50.4316 EndZ=0
    g2: LineSegment StartX=-207.775 StartY=-50.4316 StartZ=0 EndX=-207.775 EndY=-80.4316 EndZ=0
    g3: LineSegment StartX=-207.775 StartY=-80.4316 StartZ=0 EndX=-209.575 EndY=-80.4316 EndZ=0
  constraints (11):
    c: Vertical(g0)
    c: Coincident(g1,g0)
    c: Horizontal(g1)
    c: Coincident(g2,g1)
    c: Vertical(g2)
    c: Coincident(g3,g2)
    c: Coincident(g3,g0)
    c: Horizontal(g3)
    c: DistanceX(g1,g1) = 1.8
    c: Coincident(g2,g-3)
    c: DistanceY(g2,g2) = 30
FEATURE [Part::Extrusion] Extrude040  label="Extrude040 scavo alimentatore"
  Base = -> Sketch037
  Dir = (0,-1,2e-16)
  DirMode = 2
  FaceMakerClass = Part::FaceMakerBullseye
  FaceMakerMode = 3
  LengthFwd = 19.5
  LengthRev = 0
  Solid = true
  Symmetric = true
FEATURE [Part::Extrusion] Extrude031  label="Extrude fermo per scheda micro"
  Base = -> Sketch033
  Dir = (0,-1,2e-16)
  DirMode = 2
  FaceMakerClass = Part::FaceMakerBullseye
  FaceMakerMode = 3
  LengthFwd = 3
  LengthRev = 0
  Placement = pos=(0,8.6,0) rot=(0,0,1;0rad)
  Solid = true
  Symmetric = false
FEATURE [Sketcher::SketchObject] Sketch038  label="scavo driver solenoide"
  ArcFitTolerance = 1e-06
  AttachmentSupport = -> [XZ_Plane]
  ExternalGeometry = -> [Sketch,Sketch036]
  FullyConstrained = true
  MakeInternals = false
  MapMode = 5
  Placement = pos=(0,0,0) rot=(1,0,0;1.5708rad)
  sketch-geometry (7):
    g0: LineSegment StartX=-192.222 StartY=-8.0175 StartZ=0 EndX=-194.941 EndY=-6.74965 EndZ=0
    g1: LineSegment StartX=-194.941 StartY=-6.74965 StartZ=0 EndX=-212.269 EndY=-43.9083 EndZ=0
    g2: LineSegment StartX=-192.222 StartY=-8.0175 StartZ=0 EndX=-188.779 EndY=-9.62345 EndZ=0
    g3: LineSegment StartX=-188.779 StartY=-9.62345 StartZ=0 EndX=-205.357 EndY=-45.1761 EndZ=0
    g4: LineSegment StartX=-205.357 StartY=-45.1761 StartZ=0 EndX=-209.55 EndY=-45.1761 EndZ=0
    g5: LineSegment [constr] StartX=-212.269 StartY=-43.9083 StartZ=0 EndX=-209.55 EndY=-45.1761 EndZ=0
    g6: LineSegment StartX=-212.269 StartY=-43.9083 StartZ=0 EndX=-209.55 EndY=-45.1761 EndZ=0
  constraints (20):
    c: Coincident(g1,g0)
    c: Coincident(g3,g2)
    c: Coincident(g4,g3)
    c: Distance(g2) = 3.8
    c: Distance(g1) = 41
    c: Coincident(g5,g1)
    c: Distance(g5) = 3
    c: Perpendicular(g5,g-3)
    c: Parallel(g1,g-3)
    c: Perpendicular(g1,g0)
    c: Distance(g0) = 3
    c: Coincident(g6,g1)
    c: Parallel(g3,g-3)
    c: Perpendicular(g2,g3)
    c: Coincident(g2,g0)
    c: Perpendicular(g-4,g4)
    c: PointOnObject(g5,g-3)
    c: Distance(g-3,g5) = 9.6
    c: Coincident(g4,g5)
    c: Coincident(g6,g4)
FEATURE [Part::Extrusion] Extrude041  label="Extrude scavo driver solenoide"
  Base = -> Sketch038
  Dir = (0,-1,2e-16)
  DirMode = 2
  FaceMakerClass = Part::FaceMakerBullseye
  FaceMakerMode = 3
  LengthFwd = 20.6
  LengthRev = 0
  Solid = true
  Symmetric = true
FEATURE [Sketcher::SketchObject] Sketch039  label="scavo per cavo usb per micro"
  ArcFitTolerance = 1e-06
  AttachmentSupport = -> [XZ_Plane]
  ExternalGeometry = -> [Sketch,Sketch016]
  FullyConstrained = true
  MakeInternals = false
  MapMode = 5
  Placement = pos=(0,0,0) rot=(1,0,0;1.5708rad)
  sketch-geometry (4):
    g0: LineSegment StartX=-82.51 StartY=36.4 StartZ=0 EndX=-74.51 EndY=36.4 EndZ=0
    g1: LineSegment StartX=-74.51 StartY=36.4 StartZ=0 EndX=-74.51 EndY=30.8 EndZ=0
    g2: LineSegment StartX=-74.51 StartY=30.8 StartZ=0 EndX=-82.51 EndY=30.8 EndZ=0
    g3: LineSegment StartX=-82.51 StartY=30.8 StartZ=0 EndX=-82.51 EndY=36.4 EndZ=0
  constraints (11):
    c: Coincident(g1,g0)
    c: Vertical(g1)
    c: Coincident(g2,g1)
    c: Horizontal(g2)
    c: Coincident(g3,g2)
    c: Coincident(g3,g0)
    c: Vertical(g3)
    c: Tangent(g0,g-3)
    c: Tangent(g2,g-4)
    c: Tangent(g3,g-4)
    c: Tangent(g1,g-4)
FEATURE [Part::Extrusion] Extrude042  label="Extrude scavo per cavo usb per micro"
  Base = -> Sketch039
  Dir = (0,-1,2e-16)
  DirMode = 2
  FaceMakerClass = Part::FaceMakerBullseye
  FaceMakerMode = 3
  LengthFwd = 11.2
  LengthRev = 0
  Solid = true
  Symmetric = true
FEATURE [Sketcher::SketchObject] Sketch040  label="scavo saldature alimentatore connettore 5v"
  ArcFitTolerance = 1e-06
  AttachmentSupport = -> [XZ_Plane]
  ExternalGeometry = -> [Sketch037]
  FullyConstrained = true
  MakeInternals = false
  MapMode = 5
  Placement = pos=(0,0,0) rot=(1,0,0;1.5708rad)
  sketch-geometry (4):
    g0: LineSegment StartX=-211.175 StartY=-52.4316 StartZ=0 EndX=-211.175 EndY=-56.4316 EndZ=0
    g1: LineSegment StartX=-211.175 StartY=-52.4316 StartZ=0 EndX=-209.575 EndY=-52.4316 EndZ=0
    g2: LineSegment StartX=-209.575 StartY=-52.4316 StartZ=0 EndX=-209.575 EndY=-56.4316 EndZ=0
    g3: LineSegment StartX=-209.575 StartY=-56.4316 StartZ=0 EndX=-211.175 EndY=-56.4316 EndZ=0
  constraints (11):
    c: Vertical(g0)
    c: Coincident(g1,g0)
    c: Horizontal(g1)
    c: Coincident(g2,g1)
    c: Coincident(g3,g2)
    c: Coincident(g3,g0)
    c: Horizontal(g3)
    c: DistanceX(g1,g1) = 1.6
    c: DistanceY(g2,g2) = 4
    c: Tangent(g2,g-3)
    c: DistanceY(g1,g-3) = 2
FEATURE [Part::Extrusion] Extrude043  label="Extrude scavo saldature alimentatore connettore 5v"
  Base = -> Sketch040
  Dir = (0,-1,2e-16)
  DirMode = 2
  FaceMakerClass = Part::FaceMakerBullseye
  FaceMakerMode = 3
  LengthFwd = 8
  LengthRev = 0
  Solid = true
  Symmetric = true
FEATURE [Sketcher::SketchObject] Sketch041  label="scavo saldature alimentatore connettore 5v verticali"
  ArcFitTolerance = 1e-06
  AttachmentSupport = -> [XZ_Plane]
  ExternalGeometry = -> [Sketch037]
  FullyConstrained = true
  MakeInternals = false
  MapMode = 5
  Placement = pos=(0,0,0) rot=(1,0,0;1.5708rad)
  sketch-geometry (4):
    g0: LineSegment StartX=-211.175 StartY=-53.6316 StartZ=0 EndX=-209.575 EndY=-53.6316 EndZ=0
    g1: LineSegment StartX=-209.575 StartY=-53.6316 StartZ=0 EndX=-209.575 EndY=-76.6316 EndZ=0
    g2: LineSegment StartX=-209.575 StartY=-76.6316 StartZ=0 EndX=-211.175 EndY=-76.6316 EndZ=0
    g3: LineSegment StartX=-211.175 StartY=-76.6316 StartZ=0 EndX=-211.175 EndY=-53.6316 EndZ=0
  constraints (11):
    c: Horizontal(g0)
    c: Coincident(g1,g0)
    c: Coincident(g2,g1)
    c: Horizontal(g2)
    c: Coincident(g3,g2)
    c: Coincident(g3,g0)
    c: Vertical(g3)
    c: DistanceY(g3,g3) = 23
    c: DistanceX(g0,g0) = 1.6
    c: Tangent(g1,g-3)
    c: DistanceY(g0,g-3) = 3.2
FEATURE [Part::Extrusion] Extrude044  label="Extrude scavo saldature alimentatore connettore 5v verticali"
  Base = -> Sketch041
  Dir = (0,-1,2e-16)
  DirMode = 2
  FaceMakerClass = Part::FaceMakerBullseye
  FaceMakerMode = 3
  LengthFwd = 3.2
  LengthRev = 0
  Placement = pos=(0,8.3,0) rot=(0,0,1;0rad)
  Solid = true
  Symmetric = false
FEATURE [Sketcher::SketchObject] Sketch042  label="fermi per driver solenoide e alimentatore"
  ArcFitTolerance = 1e-06
  AttachmentSupport = -> [XZ_Plane]
  ExternalGeometry = -> [Sketch036,Sketch037,Sketch,Sketch038]
  FullyConstrained = true
  MakeInternals = false
  MapMode = 5
  Placement = pos=(0,0,0) rot=(1,0,0;1.5708rad)
  sketch-geometry (27):
    g0: LineSegment StartX=-200.506 StartY=-25.7811 StartZ=0 EndX=-201.436 EndY=-27.775 EndZ=0
    g1: LineSegment StartX=-201.436 StartY=-27.775 StartZ=0 EndX=-199.442 EndY=-28.7048 EndZ=0
    g2: LineSegment StartX=-199.442 StartY=-28.7048 StartZ=0 EndX=-198.512 EndY=-26.7109 EndZ=0
    g3: LineSegment StartX=-198.512 StartY=-26.7109 StartZ=0 EndX=-200.506 EndY=-25.7811 EndZ=0
    g4: LineSegment StartX=-201.28 StartY=-23.6549 StartZ=0 EndX=-203.562 EndY=-28.5489 EndZ=0
    g5: LineSegment StartX=-203.562 StartY=-28.5489 StartZ=0 EndX=-200.118 EndY=-30.1549 EndZ=0
    g6: LineSegment StartX=-197.992 StartY=-29.381 StartZ=0 EndX=-197.062 EndY=-27.3871 EndZ=0
    g7: LineSegment StartX=-197.836 StartY=-25.2608 StartZ=0 EndX=-201.28 EndY=-23.6549 EndZ=0
    g8: LineSegment [constr] StartX=-198.668 StartY=-30.8311 StartZ=0 EndX=-197.992 EndY=-29.381 EndZ=0
    g9: LineSegment [constr] StartX=-198.668 StartY=-30.8311 StartZ=0 EndX=-200.118 EndY=-30.1549 EndZ=0
    g10: ArcOfCircle CenterX=-198.512 CenterY=-26.7109 CenterZ=0 NormalX=0 NormalY=0 NormalZ=1 AngleXU=0 Radius=1.6 StartAngle=5.84685 EndAngle=7.41765
    g11: GeomPoint [constr] X=-196.386 Y=-25.937 Z=0
    g12: ArcOfCircle CenterX=-199.442 CenterY=-28.7048 CenterZ=0 NormalX=0 NormalY=0 NormalZ=1 AngleXU=0 Radius=1.6 StartAngle=4.27606 EndAngle=5.84685
    g13: GeomPoint [constr] X=-198.668 Y=-30.8311 Z=0
    g14: LineSegment StartX=-207.775 StartY=-46.8316 StartZ=0 EndX=-207.775 EndY=-50.8316 EndZ=0
    g15: LineSegment StartX=-207.775 StartY=-46.8316 StartZ=0 EndX=-203.775 EndY=-46.8316 EndZ=0
    g16: LineSegment StartX=-203.775 StartY=-46.8316 StartZ=0 EndX=-203.775 EndY=-50.8316 EndZ=0
    g17: LineSegment StartX=-207.775 StartY=-50.8316 StartZ=0 EndX=-203.775 EndY=-50.8316 EndZ=0
    g18: LineSegment StartX=-209.375 StartY=-52.4316 StartZ=0 EndX=-203.775 EndY=-52.4316 EndZ=0
    g19: LineSegment StartX=-202.175 StartY=-50.8316 StartZ=0 EndX=-202.175 EndY=-46.8316 EndZ=0
    g20: LineSegment StartX=-203.775 StartY=-45.2316 StartZ=0 EndX=-209.375 EndY=-45.2316 EndZ=0
    g21: LineSegment StartX=-209.375 StartY=-45.2316 StartZ=0 EndX=-209.375 EndY=-52.4316 EndZ=0
    g22: ArcOfCircle CenterX=-203.775 CenterY=-46.8316 CenterZ=0 NormalX=0 NormalY=0 NormalZ=1 AngleXU=0 Radius=1.6 StartAngle=1.8e-15 EndAngle=1.5708
    g23: GeomPoint [constr] X=-202.175 Y=-45.2316 Z=0
    g24: ArcOfCircle CenterX=-203.775 CenterY=-50.8316 CenterZ=0 NormalX=0 NormalY=0 NormalZ=1 AngleXU=0 Radius=1.6 StartAngle=4.71239 EndAngle=6.28319
    g25: GeomPoint [constr] X=-202.175 Y=-52.4316 Z=0
    g26: LineSegment [constr] StartX=-207.775 StartY=-50.4316 StartZ=0 EndX=-207.775 EndY=-50.8316 EndZ=0
  constraints (69):
    c: Coincident(g1,g0)
    c: Coincident(g2,g1)
    c: Coincident(g3,g2)
    c: Coincident(g3,g0)
    c: Parallel(g0,g2)
    c: Perpendicular(g3,g0)
    c: Perpendicular(g1,g0)
    c: Coincident(g5,g4)
    c: Coincident(g7,g4)
    c: Distance(g3) = 2.2
    c: Distance(g2) = 2.2
    c: Parallel(g6,g2)
    c: Parallel(g6,g4)
    c: Perpendicular(g5,g6)
    c: Perpendicular(g7,g6)
    c: Distance(g13,g11) = 5.4
    c: Distance(g5,g13) = 5.4
    c: Coincident(g9,g8)
    c: Distance(g8) = 1.6
    c: Distance(g9) = 1.6
    c: Perpendicular(g9,g8)
    c: Parallel(g8,g6)
    c: Coincident(g8,g13)
    c: Distance(g8,g1) = 1.6
    c: Distance(g9,g1) = 1.6
    c: Tangent(g0,g-5)
    c: Distance(g0,g-6) = 19.2
    c: PointOnObject(g11,g7)
    c: PointOnObject(g11,g6)
    c: Tangent(g7,g10) = -1.5708
    c: Tangent(g6,g10) = -1.5708
    c: PointOnObject(g13,g5)
    c: Tangent(g5,g12) = -1.5708
    c: Tangent(g6,g12) = -1.5708
    c: Equal(g10,g12)
    c: Coincident(g10,g2)
    c: Vertical(g14)
    c: Coincident(g15,g14)
    c: Horizontal(g15)
    c: Coincident(g16,g15)
    c: Vertical(g16)
    c: Coincident(g17,g14)
    c: Coincident(g17,g16)
    c: Horizontal(g17)
    c: Distance(g16) = 4
    c: Distance(g15) = 4
    c: Horizontal(g18)
    c: Vertical(g19)
    c: Horizontal(g20)
    c: Coincident(g21,g20)
    c: Coincident(g21,g18)
    c: Vertical(g21)
    c: Distance(g20,g23) = 7.2
    c: Distance(g25,g23) = 7.2
    c: DistanceY(g18,g14) = 1.6
    c: DistanceX(g18,g14) = 1.6
    c: PointOnObject(g23,g20)
    c: PointOnObject(g23,g19)
    c: Tangent(g20,g22) = -1.5708
    c: Tangent(g19,g22) = -1.5708
    c: PointOnObject(g25,g19)
    c: Tangent(g18,g24) = -1.5708
    c: Tangent(g19,g24) = -1.5708
    c: Equal(g22,g24)
    c: Coincident(g22,g15)
    c: Vertical(g26)
    c: Distance(g26) = 0.4
    c: Coincident(g26,g-4)
    c: Coincident(g14,g26)
FEATURE [Part::Extrusion] Extrude045  label="Extrude fermi per driver solenoide e alimentatore"
  Base = -> Sketch042
  Dir = (0,-1,2e-16)
  DirMode = 2
  FaceMakerClass = Part::FaceMakerBullseye
  FaceMakerMode = 3
  LengthFwd = 25.2
  LengthRev = 0
  Solid = true
  Symmetric = true
FEATURE [Sketcher::SketchObject] Sketch043  label="scavo pulizia fermo alimentatore"
  ArcFitTolerance = 1e-06
  AttachmentSupport = -> [XZ_Plane]
  ExternalGeometry = -> [Sketch042,Sketch036,Sketch037]
  FullyConstrained = true
  MakeInternals = false
  MapMode = 5
  Placement = pos=(0,0,0) rot=(1,0,0;1.5708rad)
  sketch-geometry (6):
    g0: LineSegment StartX=-209.375 StartY=-52.4316 StartZ=0 EndX=-209.375 EndY=-50.4316 EndZ=0
    g1: LineSegment StartX=-209.375 StartY=-50.4316 StartZ=0 EndX=-207.775 EndY=-50.4316 EndZ=0
    g2: LineSegment StartX=-207.775 StartY=-50.4316 StartZ=0 EndX=-207.775 EndY=-45.2316 EndZ=0
    g3: LineSegment StartX=-207.775 StartY=-45.2316 StartZ=0 EndX=-202.175 EndY=-45.2316 EndZ=0
    g4: LineSegment StartX=-202.175 StartY=-45.2316 StartZ=0 EndX=-202.175 EndY=-52.4316 EndZ=0
    g5: LineSegment StartX=-202.175 StartY=-52.4316 StartZ=0 EndX=-209.375 EndY=-52.4316 EndZ=0
  constraints (13):
    c: Vertical(g0)
    c: Coincident(g1,g0)
    c: Coincident(g2,g1)
    c: Coincident(g3,g2)
    c: Coincident(g4,g3)
    c: Coincident(g5,g4)
    c: Coincident(g5,g0)
    c: Horizontal(g5)
    c: Coincident(g0,g-6)
    c: Tangent(g1,g-8)
    c: Tangent(g2,g-4)
    c: Tangent(g3,g-7)
    c: Tangent(g4,g-3)
FEATURE [Part::Extrusion] Extrude046  label="Extrude scavo pulizia fermo alimentatore"
  Base = -> Sketch043
  Dir = (0,-1,2e-16)
  DirMode = 2
  FaceMakerClass = Part::FaceMakerBullseye
  FaceMakerMode = 3
  LengthFwd = 19.5
  LengthRev = 0
  Solid = true
  Symmetric = true
FEATURE [Sketcher::SketchObject] Sketch044  label="buchini per fissaggio oled"
  ArcFitTolerance = 1e-06
  AttachmentSupport = -> [YZ_Plane]
  ExternalGeometry = -> [Sketch]
  FullyConstrained = true
  MakeInternals = false
  MapMode = 5
  Placement = pos=(0,0,0) rot=(0.57735,0.57735,0.57735;2.0944rad)
  sketch-geometry (5):
    g0: LineSegment [constr] StartX=1.5e-14 StartY=67.3588 StartZ=0 EndX=0 EndY=64.3588 EndZ=0
    g1: LineSegment [constr] StartX=0 StartY=64.3588 StartZ=0 EndX=10.4 EndY=64.3588 EndZ=0
    g2: LineSegment [constr] StartX=0 StartY=64.3588 StartZ=0 EndX=-10.4 EndY=64.3588 EndZ=0
    g3: Circle CenterX=10.4 CenterY=64.3588 CenterZ=0 NormalX=0 NormalY=0 NormalZ=1 AngleXU=0 Radius=1.5
    g4: Circle CenterX=-10.4 CenterY=64.3588 CenterZ=0 NormalX=0 NormalY=0 NormalZ=1 AngleXU=0 Radius=1.5
  constraints (13):
    c: Distance(g0) = 3
    c: PointOnObject(g0,g-2)
    c: Coincident(g1,g0)
    c: Horizontal(g1)
    c: Coincident(g2,g0)
    c: Horizontal(g2)
    c: DistanceX(g1,g1) = 10.4
    c: Coincident(g3,g1)
    c: Diameter(g4) = 3
    c: Coincident(g4,g2)
    c: Coincident(g0,g-7)
    c: Equal(g1,g2)
    c: Equal(g4,g3)
FEATURE [Part::Extrusion] Extrude047  label="Extrude buchini per fissaggio oled"
  Base = -> Sketch044
  Dir = (1,0,0)
  DirMode = 2
  FaceMakerClass = Part::FaceMakerBullseye
  FaceMakerMode = 3
  LengthFwd = 10
  LengthRev = 0
  Placement = pos=(-186,0,0) rot=(0,0,1;0rad)
  Solid = true
  Symmetric = false
FEATURE [Sketcher::SketchObject] Sketch046  label="scavo 5x5 neopixel"
  ArcFitTolerance = 1e-06
  AttachmentSupport = -> [YZ_Plane002]
  FullyConstrained = true
  MakeInternals = false
  MapMode = 5
  Placement = pos=(0,0,0) rot=(0.57735,0.57735,0.57735;2.0944rad)
  sketch-geometry (4):
    g0: LineSegment StartX=-2.7 StartY=2.7 StartZ=0 EndX=2.7 EndY=2.7 EndZ=0
    g1: LineSegment StartX=2.7 StartY=2.7 StartZ=0 EndX=2.7 EndY=-2.7 EndZ=0
    g2: LineSegment StartX=2.7 StartY=-2.7 StartZ=0 EndX=-2.7 EndY=-2.7 EndZ=0
    g3: LineSegment StartX=-2.7 StartY=-2.7 StartZ=0 EndX=-2.7 EndY=2.7 EndZ=0
  constraints (11):
    c: Horizontal(g0)
    c: Coincident(g1,g0)
    c: Vertical(g1)
    c: Coincident(g2,g1)
    c: Horizontal(g2)
    c: Coincident(g3,g2)
    c: Coincident(g3,g0)
    c: Vertical(g3)
    c: DistanceX(g0,g0) = 5.4
    c: DistanceY(g1,g1) = 5.4
    c: Symmetric(g0,g1,g-1)
FEATURE [Sketcher::SketchObject] Sketch047  label="scavo 10x10 neopixel corpo"
  ArcFitTolerance = 1e-06
  AttachmentOffset = pos=(0,0,1) rot=(0,0,1;0rad)
  AttachmentSupport = -> [YZ_Plane002]
  FullyConstrained = true
  MakeInternals = false
  MapMode = 5
  Placement = pos=(1,0,0) rot=(0.57735,0.57735,0.57735;2.0944rad)
  sketch-geometry (4):
    g0: LineSegment StartX=-5 StartY=5.1 StartZ=0 EndX=5 EndY=5.1 EndZ=0
    g1: LineSegment StartX=5 StartY=5.1 StartZ=0 EndX=5 EndY=-5.1 EndZ=0
    g2: LineSegment StartX=5 StartY=-5.1 StartZ=0 EndX=-5 EndY=-5.1 EndZ=0
    g3: LineSegment StartX=-5 StartY=-5.1 StartZ=0 EndX=-5 EndY=5.1 EndZ=0
  constraints (11):
    c: Horizontal(g0)
    c: Coincident(g1,g0)
    c: Vertical(g1)
    c: Coincident(g2,g1)
    c: Horizontal(g2)
    c: Coincident(g3,g2)
    c: Coincident(g3,g0)
    c: Vertical(g3)
    c: DistanceX(g0,g0) = 10
    c: DistanceY(g1,g1) = 10.2
    c: Symmetric(g0,g2,g-1)
FEATURE [Sketcher::SketchObject] Sketch048  label="buco per perno blocco neopixel"
  ArcFitTolerance = 1e-06
  AttachmentSupport = -> [XZ_Plane002]
  FullyConstrained = true
  MakeInternals = false
  MapMode = 5
  Placement = pos=(0,0,0) rot=(1,0,0;1.5708rad)
  sketch-geometry (4):
    g0: LineSegment StartX=3 StartY=1.2 StartZ=0 EndX=3 EndY=-1.2 EndZ=0
    g1: LineSegment StartX=3 StartY=-1.2 StartZ=0 EndX=5.4 EndY=-1.2 EndZ=0
    g2: LineSegment StartX=5.4 StartY=-1.2 StartZ=0 EndX=5.4 EndY=1.2 EndZ=0
    g3: LineSegment StartX=5.4 StartY=1.2 StartZ=0 EndX=3 EndY=1.2 EndZ=0
  constraints (11):
    c: Coincident(g1,g0)
    c: Horizontal(g1)
    c: Coincident(g2,g1)
    c: Vertical(g2)
    c: Coincident(g3,g2)
    c: Coincident(g3,g0)
    c: Horizontal(g3)
    c: DistanceX(g1,g1) = 2.4
    c: DistanceY(g2,g2) = 2.4
    c: Symmetric(g0,g0,g-1)
    c: DistanceX(g-1,g0) = 3
FEATURE [Sketcher::SketchObject] Sketch045  label="blocco principale per neopixel"
  ArcFitTolerance = 1e-06
  AttachmentSupport = -> [XZ_Plane002]
  ExternalGeometry = -> [Sketch048]
  FullyConstrained = true
  MakeInternals = false
  MapMode = 5
  Placement = pos=(0,0,0) rot=(1,0,0;1.5708rad)
  sketch-geometry (6):
    g0: LineSegment StartX=0 StartY=5.1 StartZ=0 EndX=0 EndY=-5.1 EndZ=0
    g1: LineSegment StartX=0 StartY=-5.1 StartZ=0 EndX=3 EndY=-5.1 EndZ=0
    g2: LineSegment StartX=7 StartY=-1.1 StartZ=0 EndX=7 EndY=5.1 EndZ=0
    g3: LineSegment StartX=7 StartY=5.1 StartZ=0 EndX=0 EndY=5.1 EndZ=0
    g4: ArcOfCircle CenterX=3 CenterY=-1.1 CenterZ=0 NormalX=0 NormalY=0 NormalZ=1 AngleXU=0 Radius=4 StartAngle=4.71239 EndAngle=6.28319
    g5: GeomPoint [constr] X=7 Y=-5.1 Z=0
  constraints (15):
    c: Vertical(g0)
    c: Coincident(g1,g0)
    c: Horizontal(g1)
    c: Vertical(g2)
    c: Coincident(g3,g2)
    c: Coincident(g3,g0)
    c: Horizontal(g3)
    c: DistanceY(g0,g0) = 10.2
    c: Symmetric(g0,g0,g-1)
    c: DistanceX(g3,g3) = 7
    c: PointOnObject(g5,g2)
    c: PointOnObject(g5,g1)
    c: Tangent(g2,g4) = -1.5708
    c: Tangent(g1,g4) = -1.5708
    c: DistanceX(g-3,g1) = 0
FEATURE [Sketcher::SketchObject] Sketch049  label="rinforzi esterni per corpo neopoixel"
  ArcFitTolerance = 1e-06
  AttachmentSupport = -> [XZ_Plane002]
  ExternalGeometry = -> [Sketch045]
  FullyConstrained = true
  MakeInternals = false
  MapMode = 5
  Placement = pos=(0,0,0) rot=(1,0,0;1.5708rad)
  sketch-geometry (8):
    g0: LineSegment StartX=1 StartY=-4.1 StartZ=0 EndX=2 EndY=-4.1 EndZ=0
    g1: LineSegment StartX=2 StartY=-4.1 StartZ=0 EndX=2 EndY=-5.1 EndZ=0
    g2: LineSegment StartX=2 StartY=-5.1 StartZ=0 EndX=1 EndY=-5.1 EndZ=0
    g3: LineSegment StartX=1 StartY=-5.1 StartZ=0 EndX=1 EndY=-4.1 EndZ=0
    g4: LineSegment StartX=1 StartY=5.1 StartZ=0 EndX=2 EndY=5.1 EndZ=0
    g5: LineSegment StartX=2 StartY=5.1 StartZ=0 EndX=2 EndY=4.1 EndZ=0
    g6: LineSegment StartX=2 StartY=4.1 StartZ=0 EndX=1 EndY=4.1 EndZ=0
    g7: LineSegment StartX=1 StartY=4.1 StartZ=0 EndX=1 EndY=5.1 EndZ=0
  constraints (24):
    c: Horizontal(g0)
    c: Coincident(g1,g0)
    c: Vertical(g1)
    c: Coincident(g2,g1)
    c: Horizontal(g2)
    c: Coincident(g3,g2)
    c: Coincident(g3,g0)
    c: Vertical(g3)
    c: Horizontal(g4)
    c: Coincident(g5,g4)
    c: Vertical(g5)
    c: Coincident(g6,g5)
    c: Horizontal(g6)
    c: Coincident(g7,g6)
    c: Coincident(g7,g4)
    c: Vertical(g7)
    c: DistanceX(g4,g4) = 1
    c: DistanceY(g5,g5) = 1
    c: DistanceX(g0,g0) = 1
    c: DistanceY(g1,g1) = 1
    c: DistanceX(g-3,g4) = 1
    c: DistanceY(g-3,g4) = 0
    c: DistanceX(g-4,g2) = 1
    c: DistanceY(g2,g-4) = 0
FEATURE [Sketcher::SketchObject] Sketch052  label="scavo saldature driver solenoide"
  ArcFitTolerance = 1e-06
  AttachmentSupport = -> [XZ_Plane]
  ExternalGeometry = -> [Sketch038]
  FullyConstrained = true
  MakeInternals = false
  MapMode = 5
  Placement = pos=(0,0,0) rot=(1,0,0;1.5708rad)
  sketch-geometry (4):
    g0: LineSegment StartX=-195.304 StartY=-6.5806 StartZ=0 EndX=-196.994 EndY=-10.2058 EndZ=0
    g1: LineSegment StartX=-196.994 StartY=-10.2058 StartZ=0 EndX=-196.632 EndY=-10.3749 EndZ=0
    g2: LineSegment StartX=-196.632 StartY=-10.3749 StartZ=0 EndX=-194.941 EndY=-6.74965 EndZ=0
    g3: LineSegment StartX=-194.941 StartY=-6.74965 StartZ=0 EndX=-195.304 EndY=-6.5806 EndZ=0
  constraints (11):
    c: Coincident(g1,g0)
    c: Coincident(g2,g1)
    c: Coincident(g3,g2)
    c: Coincident(g3,g0)
    c: Parallel(g2,g0)
    c: Perpendicular(g2,g3)
    c: Perpendicular(g1,g2,g1) = 1.5708
    c: Parallel(g2,g-3)
    c: Distance(g2) = 4
    c: Distance(g3) = 0.4
    c: Coincident(g2,g-3)
FEATURE [Part::Extrusion] Extrude055  label="Extrude scavo saldature driver solenoide"
  Base = -> Sketch052
  Dir = (0,-1,2e-16)
  DirMode = 2
  FaceMakerClass = Part::FaceMakerBullseye
  FaceMakerMode = 3
  LengthFwd = 6
  LengthRev = 0
  Solid = true
  Symmetric = true
FEATURE [Sketcher::SketchObject] Sketch053  label="scavo saldature rumble"
  ArcFitTolerance = 1e-06
  AttachmentSupport = -> [XZ_Plane]
  ExternalGeometry = -> [Sketch019]
  FullyConstrained = true
  MakeInternals = false
  MapMode = 5
  Placement = pos=(0,0,0) rot=(1,0,0;1.5708rad)
  sketch-geometry (4):
    g0: LineSegment StartX=-169.451 StartY=-56.8615 StartZ=0 EndX=-170.687 EndY=-60.6657 EndZ=0
    g1: LineSegment StartX=-170.687 StartY=-60.6657 StartZ=0 EndX=-169.546 EndY=-61.0365 EndZ=0
    g2: LineSegment StartX=-169.546 StartY=-61.0365 StartZ=0 EndX=-168.31 EndY=-57.2323 EndZ=0
    g3: LineSegment StartX=-168.31 StartY=-57.2323 StartZ=0 EndX=-169.451 EndY=-56.8615 EndZ=0
  constraints (11):
    c: Coincident(g1,g0)
    c: Coincident(g2,g1)
    c: Coincident(g3,g2)
    c: Coincident(g3,g0)
    c: Parallel(g0,g2)
    c: Perpendicular(g3,g0)
    c: Perpendicular(g1,g0)
    c: Parallel(g0,g-3)
    c: Distance(g0) = 4
    c: Coincident(g0,g-3)
    c: Distance(g1) = 1.2
FEATURE [Part::Extrusion] Extrude056  label="Extrude scavo saldature rumble"
  Base = -> Sketch053
  Dir = (0,-1,2e-16)
  DirMode = 2
  FaceMakerClass = Part::FaceMakerBullseye
  FaceMakerMode = 3
  LengthFwd = 8.4
  LengthRev = 0
  Solid = true
  Symmetric = true
FEATURE [Sketcher::SketchObject] Sketch054  label="scavo saldature alimentatore connettore USB"
  ArcFitTolerance = 1e-06
  AttachmentSupport = -> [XZ_Plane]
  ExternalGeometry = -> [Sketch037]
  FullyConstrained = true
  MakeInternals = false
  MapMode = 5
  Placement = pos=(0,0,0) rot=(1,0,0;1.5708rad)
  sketch-geometry (4):
    g0: LineSegment StartX=-209.575 StartY=-80.4316 StartZ=0 EndX=-210.375 EndY=-80.4316 EndZ=0
    g1: LineSegment StartX=-210.375 StartY=-80.4316 StartZ=0 EndX=-210.375 EndY=-72.4316 EndZ=0
    g2: LineSegment StartX=-210.375 StartY=-72.4316 StartZ=0 EndX=-209.575 EndY=-72.4316 EndZ=0
    g3: LineSegment StartX=-209.575 StartY=-72.4316 StartZ=0 EndX=-209.575 EndY=-80.4316 EndZ=0
  constraints (11):
    c: Horizontal(g0)
    c: Coincident(g1,g0)
    c: Vertical(g1)
    c: Coincident(g2,g1)
    c: Horizontal(g2)
    c: Coincident(g3,g2)
    c: Coincident(g3,g0)
    c: Vertical(g3)
    c: DistanceX(g0,g0) = 0.8
    c: DistanceY(g3,g3) = 8
    c: Coincident(g0,g-4)
FEATURE [Part::Extrusion] Extrude057  label="Extrude scavo saldature alimentatore connettore USB"
  Base = -> Sketch054
  Dir = (0,-1,2e-16)
  DirMode = 2
  FaceMakerClass = Part::FaceMakerBullseye
  FaceMakerMode = 3
  LengthFwd = 11
  LengthRev = 0
  Solid = true
  Symmetric = true
FEATURE [Sketcher::SketchObject] Sketch055  label="buco interno per micro switch"
  ArcFitTolerance = 1e-06
  AttachmentSupport = -> [XZ_Plane]
  ExternalGeometry = -> [Sketch]
  FullyConstrained = true
  MakeInternals = false
  MapMode = 5
  Placement = pos=(0,0,0) rot=(1,0,0;1.5708rad)
  sketch-geometry (11):
    g0: LineSegment [constr] StartX=-194.483 StartY=34.2854 StartZ=0 EndX=-196.022 EndY=30.0568 EndZ=0
    g1: LineSegment [constr] StartX=-196.022 StartY=30.0568 StartZ=0 EndX=-197.561 EndY=25.8282 EndZ=0
    g2: LineSegment [constr] StartX=-196.022 StartY=30.0568 StartZ=0 EndX=-194.143 EndY=29.3727 EndZ=0
    g3: LineSegment [constr] StartX=-196.022 StartY=30.0568 StartZ=0 EndX=-197.902 EndY=30.7408 EndZ=0
    g4: LineSegment StartX=-196.362 StartY=34.9694 StartZ=0 EndX=-192.604 EndY=33.6014 EndZ=0
    g5: LineSegment StartX=-199.441 StartY=26.5122 StartZ=0 EndX=-195.682 EndY=25.1441 EndZ=0
    g6: LineSegment StartX=-192.604 StartY=33.6014 StartZ=0 EndX=-195.682 EndY=25.1441 EndZ=0
    g7: LineSegment StartX=-196.362 StartY=34.9694 StartZ=0 EndX=-199.441 EndY=26.5122 EndZ=0
    g8: GeomPoint [constr] X=-187.821 Y=29.2 Z=0
    g9: LineSegment [constr] StartX=-188.505 StartY=27.3206 StartZ=0 EndX=-196.022 EndY=30.0568 EndZ=0
    g10: LineSegment [constr] StartX=-187.821 StartY=29.2 StartZ=0 EndX=-188.505 EndY=27.3206 EndZ=0
  constraints (27):
    c: Coincident(g2,g0)
    c: Parallel(g0,g-3)
    c: Tangent(g1,g0) = -1.5708
    c: Perpendicular(g0,g2)
    c: Tangent(g2,g3)
    c: Distance(g0,g1) = 9
    c: Equal(g0,g1)
    c: Distance(g3,g2) = 4
    c: Equal(g2,g3)
    c: Parallel(g3,g4)
    c: Symmetric(g4,g4,g0)
    c: Parallel(g6,g1)
    c: Parallel(g7,g1)
    c: Symmetric(g6,g6,g2)
    c: Symmetric(g5,g5,g1)
    c: Symmetric(g7,g7,g3)
    c: Coincident(g7,g4)
    c: Coincident(g6,g4)
    c: Coincident(g5,g6)
    c: Symmetric(g-3,g-3,g8)
    c: Perpendicular(g-3,g9)
    c: Distance(g9) = 8
    c: Coincident(g3,g9)
    c: Coincident(g10,g8)
    c: Parallel(g10,g-3)
    c: Distance(g10) = 2
    c: Coincident(g10,g9)
FEATURE [Sketcher::SketchObject] Sketch056  label="buco esterno per micro switch"
  ArcFitTolerance = 1e-06
  AttachmentSupport = -> [XZ_Plane]
  ExternalGeometry = -> [Sketch055]
  FullyConstrained = true
  MakeInternals = false
  MapMode = 5
  Placement = pos=(0,0,0) rot=(1,0,0;1.5708rad)
  sketch-geometry (17):
    g0: GeomPoint [constr] X=-194.143 Y=29.3727 Z=0
    g1: GeomPoint [constr] X=-194.483 Y=34.2854 Z=0
    g2: GeomPoint [constr] X=-197.902 Y=30.7408 Z=0
    g3: GeomPoint [constr] X=-197.561 Y=25.8282 Z=0
    g4: GeomPoint [constr] X=-196.022 Y=30.0568 Z=0
    g5: LineSegment [constr] StartX=-194.483 StartY=34.2854 StartZ=0 EndX=-196.022 EndY=30.0568 EndZ=0
    g6: LineSegment [constr] StartX=-196.022 StartY=30.0568 StartZ=0 EndX=-197.561 EndY=25.8282 EndZ=0
    g7: LineSegment [constr] StartX=-197.902 StartY=30.7408 StartZ=0 EndX=-196.022 EndY=30.0568 EndZ=0
    g8: LineSegment [constr] StartX=-196.022 StartY=30.0568 StartZ=0 EndX=-194.143 EndY=29.3727 EndZ=0
    g9: LineSegment [constr] StartX=-195.338 StartY=31.9362 StartZ=0 EndX=-196.022 EndY=30.0568 EndZ=0
    g10: LineSegment [constr] StartX=-196.022 StartY=30.0568 StartZ=0 EndX=-196.706 EndY=28.1774 EndZ=0
    g11: LineSegment [constr] StartX=-196.022 StartY=30.0568 StartZ=0 EndX=-196.821 EndY=30.3475 EndZ=0
    g12: LineSegment [constr] StartX=-196.022 StartY=30.0568 StartZ=0 EndX=-195.223 EndY=29.7661 EndZ=0
    g13: LineSegment StartX=-194.539 StartY=31.6454 StartZ=0 EndX=-195.907 EndY=27.8867 EndZ=0
    g14: LineSegment StartX=-196.137 StartY=32.2269 StartZ=0 EndX=-197.505 EndY=28.4681 EndZ=0
    g15: LineSegment StartX=-196.137 StartY=32.2269 StartZ=0 EndX=-194.539 EndY=31.6454 EndZ=0
    g16: LineSegment StartX=-197.505 StartY=28.4681 StartZ=0 EndX=-195.907 EndY=27.8867 EndZ=0
  constraints (34):
    c: Symmetric(g-5,g-5,g1)
    c: Symmetric(g-5,g-6,g0)
    c: Symmetric(g-6,g-6,g3)
    c: Symmetric(g-5,g-6,g2)
    c: Coincident(g5,g1)
    c: Coincident(g5,g4)
    c: Coincident(g6,g4)
    c: Coincident(g6,g3)
    c: Equal(g5,g6)
    c: Coincident(g7,g2)
    c: Coincident(g7,g4)
    c: Coincident(g8,g4)
    c: Coincident(g8,g0)
    c: Equal(g7,g8)
    c: Coincident(g11,g9)
    c: Coincident(g12,g9)
    c: Tangent(g10,g9) = -1.5708
    c: Perpendicular(g11,g9)
    c: Parallel(g9,g-4)
    c: Equal(g9,g10)
    c: Parallel(g12,g11)
    c: Equal(g11,g12)
    c: Distance(g11,g12) = 1.7
    c: Distance(g9,g10) = 4
    c: Symmetric(g13,g13,g12)
    c: Parallel(g13,g9)
    c: Symmetric(g14,g14,g11)
    c: Symmetric(g15,g15,g9)
    c: Parallel(g15,g11)
    c: Symmetric(g16,g16,g10)
    c: Coincident(g16,g14)
    c: Coincident(g15,g14)
    c: Coincident(g13,g15)
    c: Coincident(g9,g4)
FEATURE [Sketcher::SketchObject] Sketch057  label="buco interno per SWITCH"
  ArcFitTolerance = 1e-06
  AttachmentSupport = -> [XZ_Plane]
  ExternalGeometry = -> [Sketch]
  FullyConstrained = true
  MakeInternals = false
  MapMode = 5
  Placement = pos=(0,0,0) rot=(1,0,0;1.5708rad)
  sketch-geometry (10):
    g0: GeomPoint [constr] X=-187.821 Y=29.2 Z=0
    g1: LineSegment [constr] StartX=-188.505 StartY=27.3206 StartZ=0 EndX=-193.203 EndY=29.0307 EndZ=0
    g2: LineSegment [constr] StartX=-190.809 StartY=35.6086 StartZ=0 EndX=-195.597 EndY=22.4529 EndZ=0
    g3: GeomPoint [constr] X=-193.203 Y=29.0307 Z=0
    g4: LineSegment [constr] StartX=-196.492 StartY=30.2278 StartZ=0 EndX=-189.914 EndY=27.8336 EndZ=0
    g5: LineSegment StartX=-194.098 StartY=36.8056 StartZ=0 EndX=-187.52 EndY=34.4115 EndZ=0
    g6: LineSegment StartX=-194.098 StartY=36.8056 StartZ=0 EndX=-198.886 EndY=23.6499 EndZ=0
    g7: LineSegment StartX=-187.52 StartY=34.4115 StartZ=0 EndX=-192.308 EndY=21.2558 EndZ=0
    g8: LineSegment StartX=-198.886 StartY=23.6499 StartZ=0 EndX=-192.308 EndY=21.2558 EndZ=0
    g9: LineSegment [constr] StartX=-187.821 StartY=29.2 StartZ=0 EndX=-188.505 EndY=27.3206 EndZ=0
  constraints (23):
    c: Symmetric(g-3,g-3,g0)
    c: Perpendicular(g1,g-3)
    c: Parallel(g2,g-3)
    c: Symmetric(g2,g2,g3)
    c: Perpendicular(g2,g4)
    c: Symmetric(g4,g4,g3)
    c: Distance(g2) = 14
    c: Distance(g4) = 7
    c: Distance(g1) = 5
    c: Parallel(g5,g4)
    c: Parallel(g7,g2)
    c: Symmetric(g5,g5,g2)
    c: Symmetric(g6,g6,g4)
    c: Symmetric(g7,g7,g4)
    c: Symmetric(g8,g8,g2)
    c: Coincident(g6,g5)
    c: Coincident(g7,g5)
    c: Coincident(g8,g7)
    c: Coincident(g3,g1)
    c: Coincident(g9,g0)
    c: Parallel(g9,g-3)
    c: Distance(g9) = 2
    c: Coincident(g1,g9)
FEATURE [Sketcher::SketchObject] Sketch058  label="buco esterno per SWITCH"
  ArcFitTolerance = 1e-06
  AttachmentSupport = -> [XZ_Plane]
  ExternalGeometry = -> [Sketch057]
  FullyConstrained = true
  MakeInternals = false
  MapMode = 5
  Placement = pos=(0,0,0) rot=(1,0,0;1.5708rad)
  sketch-geometry (12):
    g0: GeomPoint [constr] X=-190.809 Y=35.6086 Z=0
    g1: GeomPoint [constr] X=-196.492 Y=30.2278 Z=0
    g2: GeomPoint [constr] X=-189.914 Y=27.8336 Z=0
    g3: GeomPoint [constr] X=-195.597 Y=22.4529 Z=0
    g4: GeomPoint [constr] X=-193.203 Y=29.0307 Z=0
    g5: LineSegment [constr] StartX=-192.006 StartY=32.3196 StartZ=0 EndX=-194.4 EndY=25.7418 EndZ=0
    g6: GeomPoint [constr] X=-193.203 Y=29.0307 Z=0
    g7: LineSegment [constr] StartX=-195.082 StartY=29.7148 StartZ=0 EndX=-191.324 EndY=28.3467 EndZ=0
    g8: LineSegment StartX=-193.885 StartY=33.0037 StartZ=0 EndX=-190.127 EndY=31.6356 EndZ=0
    g9: LineSegment StartX=-190.127 StartY=31.6356 StartZ=0 EndX=-192.521 EndY=25.0578 EndZ=0
    g10: LineSegment StartX=-196.28 StartY=26.4258 StartZ=0 EndX=-192.521 EndY=25.0578 EndZ=0
    g11: LineSegment StartX=-193.885 StartY=33.0037 StartZ=0 EndX=-196.28 EndY=26.4258 EndZ=0
  constraints (21):
    c: Symmetric(g-6,g-6,g3)
    c: Symmetric(g-4,g-6,g2)
    c: Symmetric(g-5,g-4,g0)
    c: Symmetric(g-5,g-6,g1)
    c: Symmetric(g1,g2,g4)
    c: Parallel(g5,g-4)
    c: Symmetric(g5,g5,g6)
    c: Perpendicular(g7,g5)
    c: Symmetric(g7,g7,g6)
    c: Distance(g5) = 7
    c: Distance(g7) = 4
    c: Parallel(g8,g7)
    c: Parallel(g11,g5)
    c: Symmetric(g8,g8,g5)
    c: Symmetric(g9,g9,g7)
    c: Symmetric(g10,g10,g5)
    c: Symmetric(g11,g11,g7)
    c: Coincident(g11,g8)
    c: Coincident(g9,g8)
    c: Coincident(g9,g10)
    c: Coincident(g6,g4)
FEATURE [Part::Extrusion] Extrude060  label="Extrude buco interno per SWITCH destro"
  Base = -> Sketch057
  Dir = (0,-1,2e-16)
  DirMode = 2
  FaceMakerClass = Part::FaceMakerBullseye
  FaceMakerMode = 3
  LengthFwd = 13.2
  LengthRev = 0
  Placement = pos=(0,2.6,0) rot=(0,0,1;0rad)
  Solid = true
  Symmetric = false
FEATURE [Part::Extrusion] Extrude061  label="Extrude buco esterno per SWITCH destro"
  Base = -> Sketch058
  Dir = (0,-1,2e-16)
  DirMode = 2
  FaceMakerClass = Part::FaceMakerBullseye
  FaceMakerMode = 3
  LengthFwd = 2
  LengthRev = 0
  Placement = pos=(0,-10.6,0) rot=(0,0,1;0rad)
  Solid = true
  Symmetric = false
FEATURE [Sketcher::SketchObject] Sketch059  label="buco per spazio introduzione SWITCH"
  ArcFitTolerance = 1e-06
  AttachmentSupport = -> [XZ_Plane]
  ExternalGeometry = -> [Sketch057,Sketch010]
  FullyConstrained = true
  MakeInternals = false
  MapMode = 5
  Placement = pos=(0,0,0) rot=(1,0,0;1.5708rad)
  sketch-geometry (8):
    g0: LineSegment [constr] StartX=-201.368 StartY=36.3521 StartZ=0 EndX=-195.094 EndY=34.0687 EndZ=0
    g1: LineSegment [constr] StartX=-194.098 StartY=36.8056 StartZ=0 EndX=-195.094 EndY=34.0687 EndZ=0
    g2: LineSegment StartX=-198.658 StartY=24.2771 StartZ=0 EndX=-199.654 EndY=21.5401 EndZ=0
    g3: LineSegment StartX=-199.654 StartY=21.5401 StartZ=0 EndX=-181.196 EndY=14.822 EndZ=0
    g4: LineSegment StartX=-181.196 StartY=14.822 StartZ=0 EndX=-180.2 EndY=17.559 EndZ=0
    g5: LineSegment StartX=-180.2 StartY=17.559 StartZ=0 EndX=-198.658 EndY=24.2771 EndZ=0
    g6: LineSegment [constr] StartX=-204.932 StartY=26.5605 StartZ=0 EndX=-198.658 EndY=24.2771 EndZ=0
    g7: LineSegment [constr] StartX=-198.658 StartY=24.2771 StartZ=0 EndX=-199.654 EndY=21.5401 EndZ=0
  constraints (20):
    c: Parallel(g1,g-3)
    c: Parallel(g0,g-4)
    c: Coincident(g0,g-4)
    c: Coincident(g1,g-3)
    c: Coincident(g0,g1)
    c: Coincident(g3,g2)
    c: Coincident(g4,g3)
    c: Coincident(g5,g4)
    c: Coincident(g5,g2)
    c: Parallel(g5,g-5)
    c: Parallel(g3,g-5)
    c: Parallel(g4,g-6)
    c: DistanceX(g-6,g4) = 0
    c: Coincident(g6,g-5)
    c: Equal(g6,g0)
    c: Coincident(g7,g6)
    c: Equal(g7,g1)
    c: Tangent(g7,g-3)
    c: Coincident(g2,g6)
    c: Coincident(g2,g7)
FEATURE [Part::Extrusion] Extrude062  label="Extrude buco per spazio introduzione SWITCH"
  Base = -> Sketch059
  Dir = (0,-1,2e-16)
  DirMode = 2
  FaceMakerClass = Part::FaceMakerBullseye
  FaceMakerMode = 3
  LengthFwd = 13.2
  LengthRev = 0
  Solid = true
  Symmetric = true
FEATURE [Part::Extrusion] Extrude063  label="Extrude buco interno per SWITCH sinistro"
  Base = -> Sketch057
  Dir = (0,-1,2e-16)
  DirMode = 2
  FaceMakerClass = Part::FaceMakerBullseye
  FaceMakerMode = 3
  LengthFwd = 13.2
  LengthRev = 0
  Placement = pos=(0,10.6,0) rot=(0,0,1;0rad)
  Solid = true
  Symmetric = false
FEATURE [Part::Extrusion] Extrude064  label="Extrude buco esterno per SWITCH sinistro"
  Base = -> Sketch058
  Dir = (0,-1,2e-16)
  DirMode = 2
  FaceMakerClass = Part::FaceMakerBullseye
  FaceMakerMode = 3
  LengthFwd = 2
  LengthRev = 0
  Placement = pos=(0,12.6,0) rot=(0,0,1;0rad)
  Solid = true
  Symmetric = false
FEATURE [Sketcher::SketchObject] Sketch061  label="struttura esterna blocco switch"
  ArcFitTolerance = 1e-06
  AttachmentSupport = -> [XZ_Plane003]
  FullyConstrained = true
  MakeInternals = false
  MapMode = 5
  Placement = pos=(0,0,0) rot=(1,0,0;1.5708rad)
  sketch-geometry (5):
    g0: LineSegment StartX=-1 StartY=-5.1 StartZ=0 EndX=1 EndY=-5.1 EndZ=0
    g1: LineSegment StartX=1 StartY=-5.1 StartZ=0 EndX=1 EndY=5.1 EndZ=0
    g2: LineSegment StartX=1 StartY=5.1 StartZ=0 EndX=-1 EndY=5.1 EndZ=0
    g3: LineSegment StartX=-1 StartY=5.1 StartZ=0 EndX=-1 EndY=-5.1 EndZ=0
    g4: GeomPoint [constr] X=0 Y=0 Z=0
  constraints (12):
    c: Coincident(g0,g1)
    c: Coincident(g1,g2)
    c: Coincident(g2,g3)
    c: Coincident(g3,g0)
    c: Horizontal(g0)
    c: Horizontal(g2)
    c: Vertical(g1)
    c: Vertical(g3)
    c: Symmetric(g2,g0,g4)
    c: Distance(g1,g3) = 2
    c: Distance(g0,g2) = 10.2
    c: Coincident(g4,g-1)
FEATURE [Sketcher::SketchObject] Sketch062  label="struttura interna blocco switch"
  ArcFitTolerance = 1e-06
  AttachmentSupport = -> [XZ_Plane003]
  ExternalGeometry = -> [Sketch061]
  FullyConstrained = true
  MakeInternals = false
  MapMode = 5
  Placement = pos=(0,0,0) rot=(1,0,0;1.5708rad)
  sketch-geometry (5):
    g0: LineSegment StartX=-1 StartY=3.1 StartZ=0 EndX=-1 EndY=-3.1 EndZ=0
    g1: LineSegment StartX=-1 StartY=-3.1 StartZ=0 EndX=1 EndY=-3.1 EndZ=0
    g2: LineSegment StartX=1 StartY=-3.1 StartZ=0 EndX=1 EndY=3.1 EndZ=0
    g3: LineSegment StartX=1 StartY=3.1 StartZ=0 EndX=-1 EndY=3.1 EndZ=0
    g4: GeomPoint [constr] X=0 Y=0 Z=0
  constraints (12):
    c: Coincident(g0,g1)
    c: Coincident(g1,g2)
    c: Coincident(g2,g3)
    c: Coincident(g3,g0)
    c: Vertical(g0)
    c: Vertical(g2)
    c: Horizontal(g1)
    c: Horizontal(g3)
    c: Symmetric(g2,g0,g4)
    c: Coincident(g4,g-1)
    c: Distance(g0) = 6.2
    c: Equal(g3,g-3)
FEATURE [Sketcher::SketchObject] Sketch063  label="blocchi tra switch"
  ArcFitTolerance = 1e-06
  AttachmentSupport = -> [XZ_Plane003]
  ExternalGeometry = -> [Sketch061,Sketch062]
  FullyConstrained = true
  MakeInternals = false
  MapMode = 5
  Placement = pos=(0,0,0) rot=(1,0,0;1.5708rad)
  sketch-geometry (8):
    g0: LineSegment StartX=-3 StartY=5.1 StartZ=0 EndX=-1 EndY=5.1 EndZ=0
    g1: LineSegment StartX=-1 StartY=5.1 StartZ=0 EndX=-1 EndY=3.1 EndZ=0
    g2: LineSegment StartX=-1 StartY=3.1 StartZ=0 EndX=-3 EndY=3.1 EndZ=0
    g3: LineSegment StartX=-3 StartY=3.1 StartZ=0 EndX=-3 EndY=5.1 EndZ=0
    g4: LineSegment StartX=-3 StartY=-3.1 StartZ=0 EndX=-1 EndY=-3.1 EndZ=0
    g5: LineSegment StartX=-1 StartY=-3.1 StartZ=0 EndX=-1 EndY=-5.1 EndZ=0
    g6: LineSegment StartX=-1 StartY=-5.1 StartZ=0 EndX=-3 EndY=-5.1 EndZ=0
    g7: LineSegment StartX=-3 StartY=-5.1 StartZ=0 EndX=-3 EndY=-3.1 EndZ=0
  constraints (20):
    c: Horizontal(g0)
    c: Coincident(g1,g0)
    c: Coincident(g2,g1)
    c: Horizontal(g2)
    c: Coincident(g3,g2)
    c: Coincident(g3,g0)
    c: Vertical(g3)
    c: Horizontal(g4)
    c: Coincident(g5,g4)
    c: Coincident(g6,g5)
    c: Horizontal(g6)
    c: Coincident(g7,g6)
    c: Coincident(g7,g4)
    c: Vertical(g7)
    c: Coincident(g0,g-4)
    c: Coincident(g1,g-5)
    c: Coincident(g4,g-6)
    c: Coincident(g5,g-7)
    c: Distance(g0) = 2
    c: Distance(g4) = 2
FEATURE [Sketcher::SketchObject] Sketch066  label="piano per rampino"
  ArcFitTolerance = 1e-06
  AttachmentSupport = -> [XZ_Plane002]
  ExternalGeometry = -> [Sketch045]
  FullyConstrained = true
  MakeInternals = false
  MapMode = 5
  Placement = pos=(0,0,0) rot=(1,0,0;1.5708rad)
  sketch-geometry (4):
    g0: LineSegment StartX=5.4 StartY=5.1 StartZ=0 EndX=5.4 EndY=3.9 EndZ=0
    g1: LineSegment StartX=5.4 StartY=3.9 StartZ=0 EndX=7 EndY=3.9 EndZ=0
    g2: LineSegment StartX=7 StartY=3.9 StartZ=0 EndX=7 EndY=5.1 EndZ=0
    g3: LineSegment StartX=7 StartY=5.1 StartZ=0 EndX=5.4 EndY=5.1 EndZ=0
  constraints (11):
    c: Coincident(g0,g1)
    c: Coincident(g1,g2)
    c: Coincident(g2,g3)
    c: Coincident(g3,g0)
    c: Vertical(g0)
    c: Vertical(g2)
    c: Horizontal(g1)
    c: Horizontal(g3)
    c: Distance(g0,g2) = 1.6
    c: Distance(g1,g3) = 1.2
    c: Coincident(g2,g-3)
FEATURE [Sketcher::SketchObject] Sketch064  label="rampini_per_serraggio_struttura"
  ArcFitTolerance = 1e-06
  AttachmentSupport = -> [XZ_Plane002]
  ExternalGeometry = -> [Sketch066,Sketch045]
  FullyConstrained = true
  MakeInternals = false
  MapMode = 5
  Placement = pos=(0,0,0) rot=(1,0,0;1.5708rad)
  sketch-geometry (7):
    g0: LineSegment StartX=7 StartY=5.1 StartZ=0 EndX=7 EndY=3.9 EndZ=0
    g1: LineSegment StartX=7 StartY=3.9 StartZ=0 EndX=9 EndY=3.9 EndZ=0
    g2: LineSegment StartX=7 StartY=5.1 StartZ=0 EndX=7 EndY=5.1 EndZ=0
    g3: LineSegment StartX=7 StartY=5.1 StartZ=0 EndX=7 EndY=7.5 EndZ=0
    g4: LineSegment StartX=9 StartY=5.1 StartZ=0 EndX=9 EndY=3.9 EndZ=0
    g5: LineSegment StartX=7 StartY=7.5 StartZ=0 EndX=9 EndY=7.5 EndZ=0
    g6: LineSegment StartX=9 StartY=7.5 StartZ=0 EndX=9 EndY=5.1 EndZ=0
  constraints (20):
    c: Vertical(g0)
    c: Coincident(g1,g0)
    c: Horizontal(g1)
    c: Coincident(g2,g0)
    c: Horizontal(g2)
    c: Coincident(g3,g2)
    c: Vertical(g3)
    c: Coincident(g5,g3)
    c: Coincident(g4,g6)
    c: Coincident(g4,g1)
    c: Vertical(g4)
    c: Coincident(g0,g-3)
    c: DistanceY(g-4,g3) = 2.4
    c: DistanceX(g1,g1) = 2
    c: DistanceY(g2,g6) = 0
    c: DistanceX(g2,g2) = 0
    c: DistanceY(g0,g0) = 1.2
    c: Coincident(g5,g6)
    c: Horizontal(g5)
    c: Vertical(g6)
FEATURE [Sketcher::SketchObject] Sketch067  label="perno per blocco switch"
  ArcFitTolerance = 1e-06
  AttachmentSupport = -> [XZ_Plane]
  ExternalGeometry = -> [Sketch,Sketch010]
  FullyConstrained = true
  MakeInternals = false
  MapMode = 5
  Placement = pos=(0,0,0) rot=(1,0,0;1.5708rad)
  sketch-geometry (14):
    g0: LineSegment StartX=-191.073 StartY=24.9429 StartZ=0 EndX=-185.81 EndY=23.0276 EndZ=0
    g1: LineSegment StartX=-183.76 StartY=23.9839 StartZ=0 EndX=-182.392 EndY=27.7427 EndZ=0
    g2: LineSegment StartX=-183.348 StartY=29.7934 StartZ=0 EndX=-188.61 EndY=31.7087 EndZ=0
    g3: LineSegment StartX=-188.61 StartY=31.7087 StartZ=0 EndX=-191.073 EndY=24.9429 EndZ=0
    g4: GeomPoint [constr] X=-186.459 Y=27.0946 Z=0
    g5: LineSegment StartX=-189.022 StartY=25.8992 StartZ=0 EndX=-185.263 EndY=24.5311 EndZ=0
    g6: LineSegment StartX=-185.263 StartY=24.5311 StartZ=0 EndX=-183.895 EndY=28.2899 EndZ=0
    g7: LineSegment StartX=-183.895 StartY=28.2899 StartZ=0 EndX=-187.654 EndY=29.658 EndZ=0
    g8: LineSegment StartX=-187.654 StartY=29.658 StartZ=0 EndX=-189.022 EndY=25.8992 EndZ=0
    g9: GeomPoint [constr] X=-186.459 Y=27.0946 Z=0
    g10: ArcOfCircle CenterX=-185.263 CenterY=24.5311 CenterZ=0 NormalX=0 NormalY=0 NormalZ=1 AngleXU=0 Radius=1.6 StartAngle=4.36332 EndAngle=5.93412
    g11: GeomPoint [constr] X=-184.307 Y=22.4804 Z=0
    g12: ArcOfCircle CenterX=-183.895 CenterY=28.2899 CenterZ=0 NormalX=0 NormalY=0 NormalZ=1 AngleXU=0 Radius=1.6 StartAngle=5.93412 EndAngle=7.50492
    g13: GeomPoint [constr] X=-181.844 Y=29.2462 Z=0
  constraints (30):
    c: Coincident(g2,g3)
    c: Coincident(g3,g0)
    c: Symmetric(g13,g0,g4)
    c: Distance(g11,g3) = 7.2
    c: Distance(g0,g2) = 7.2
    c: Parallel(g3,g1)
    c: Parallel(g2,g0)
    c: Perpendicular(g2,g3)
    c: Coincident(g5,g6)
    c: Coincident(g6,g7)
    c: Coincident(g7,g8)
    c: Coincident(g8,g5)
    c: Symmetric(g7,g5,g9)
    c: Distance(g6,g8) = 4
    c: Distance(g5,g7) = 4
    c: Coincident(g9,g4)
    c: Parallel(g8,g6)
    c: Parallel(g7,g5)
    c: Perpendicular(g7,g8)
    c: Tangent(g8,g-3)
    c: Tangent(g2,g-4)
    c: PointOnObject(g11,g1)
    c: PointOnObject(g11,g0)
    c: Tangent(g1,g10) = -1.5708
    c: Tangent(g0,g10) = -1.5708
    c: PointOnObject(g13,g1)
    c: Tangent(g1,g12) = -1.5708
    c: Tangent(g2,g12) = -1.5708
    c: Equal(g10,g12)
    c: Coincident(g10,g5)
FEATURE [Part::Extrusion] Extrude072  label="Extrude perno per blocco switch"
  Base = -> Sketch067
  Dir = (0,-1,2e-16)
  DirMode = 2
  FaceMakerClass = Part::FaceMakerBullseye
  FaceMakerMode = 3
  LengthFwd = 25.2
  LengthRev = 0
  Solid = true
  Symmetric = true
FEATURE [Part::MultiFuse] Fusion
  Refine = true
  Shapes = -> [Extrude,Sweep,Extrude007,Extrude011,Extrude005,Extrude012,Extrude013,Extrude016,Extrude031,Extrude039,Extrude045,Extrude072]
FEATURE [Part::Cut] Cut
  Base = -> Fusion
  Refine = true
  Tool = -> Extrude001
FEATURE [Part::Cut] Cut001
  Base = -> Cut
  Refine = true
  Tool = -> Extrude004
FEATURE [Part::Cut] Cut002
  Base = -> Cut001
  Refine = true
  Tool = -> Extrude006
FEATURE [Part::Cut] Cut003
  Base = -> Cut002
  Refine = true
  Tool = -> Extrude008
FEATURE [Part::Cut] Cut004
  Base = -> Cut003
  Refine = true
  Tool = -> Extrude009
FEATURE [Part::Cut] Cut005
  Base = -> Cut004
  Refine = true
  Tool = -> Extrude010
FEATURE [Part::Cut] Cut006
  Base = -> Cut005
  Refine = true
  Tool = -> Extrude014
FEATURE [Part::Cut] Cut007
  Base = -> Cut006
  Refine = true
  Tool = -> Extrude015
FEATURE [Part::Cut] Cut008
  Base = -> Cut007
  Refine = true
  Tool = -> Extrude018
FEATURE [Part::Cut] Cut009
  Base = -> Cut008
  Refine = true
  Tool = -> Extrude019
FEATURE [Part::Cut] Cut010
  Base = -> Cut009
  Refine = true
  Tool = -> Extrude020
FEATURE [Part::Cut] Cut011
  Base = -> Cut010
  Refine = true
  Tool = -> Extrude021
FEATURE [Part::Cut] Cut012
  Base = -> Cut011
  Refine = true
  Tool = -> Extrude022
FEATURE [Part::Cut] Cut013
  Base = -> Cut012
  Refine = true
  Tool = -> Extrude023
FEATURE [Part::Cut] Cut014
  Base = -> Cut013
  Refine = true
  Tool = -> Extrude032
FEATURE [Part::Cut] Cut015
  Base = -> Cut014
  Refine = true
  Tool = -> Extrude033
FEATURE [Part::Cut] Cut016
  Base = -> Cut015
  Refine = true
  Tool = -> Extrude034
FEATURE [Part::Cut] Cut017
  Base = -> Cut016
  Refine = true
  Tool = -> Extrude035
FEATURE [Part::Cut] Cut018
  Base = -> Cut017
  Refine = true
  Tool = -> Extrude036
FEATURE [Part::Cut] Cut019
  Base = -> Cut018
  Refine = true
  Tool = -> Extrude037
FEATURE [Part::Cut] Cut020
  Base = -> Cut019
  Refine = true
  Tool = -> Extrude030
FEATURE [Part::Cut] Cut022
  Base = -> Cut020
  Refine = true
  Tool = -> Extrude038
FEATURE [Part::Cut] Cut023
  Base = -> Cut022
  Refine = true
  Tool = -> Extrude041
FEATURE [Part::Cut] Cut024
  Base = -> Cut023
  Refine = true
  Tool = -> Extrude040
FEATURE [Part::Cut] Cut025
  Base = -> Cut024
  Refine = true
  Tool = -> Extrude042
FEATURE [Part::Cut] Cut026
  Base = -> Cut025
  Refine = true
  Tool = -> Extrude043
FEATURE [Part::Cut] Cut027
  Base = -> Cut026
  Refine = true
  Tool = -> Extrude044
FEATURE [Part::Cut] Cut028
  Base = -> Cut027
  Refine = true
  Tool = -> Extrude046
FEATURE [Part::Cut] Cut029
  Base = -> Cut028
  Refine = true
  Tool = -> Extrude047
FEATURE [Part::Cut] Cut033
  Base = -> Cut029
  Refine = true
  Tool = -> Extrude055
FEATURE [Part::Cut] Cut034
  Base = -> Cut033
  Refine = true
  Tool = -> Extrude056
FEATURE [Part::Cut] Cut035
  Base = -> Cut034
  Refine = true
  Tool = -> Extrude057
FEATURE [Part::Cut] Cut037
  Base = -> Cut035
  Refine = true
  Tool = -> Extrude060
FEATURE [Part::Cut] Cut038
  Base = -> Cut037
  Refine = true
  Tool = -> Extrude061
FEATURE [Part::Cut] Cut039
  Base = -> Cut038
  Refine = true
  Tool = -> Extrude063
FEATURE [Part::Cut] Cut040
  Base = -> Cut039
  Refine = true
  Tool = -> Extrude064
FEATURE [Part::Cut] Cut041
  Base = -> Cut040
  Refine = true
  Tool = -> Extrude062
FEATURE [Sketcher::SketchObject] Sketch068  label="base con smusso sopra neopixel"
  ArcFitTolerance = 1e-06
  AttachmentSupport = -> [YZ_Plane002]
  FullyConstrained = true
  MakeInternals = false
  MapMode = 5
  Placement = pos=(0,0,0) rot=(0.57735,0.57735,0.57735;2.0944rad)
  sketch-geometry (5):
    g0: LineSegment StartX=-9.5 StartY=-6.1 StartZ=0 EndX=9.5 EndY=-6.1 EndZ=0
    g1: LineSegment StartX=9.5 StartY=-6.1 StartZ=0 EndX=9.5 EndY=6.1 EndZ=0
    g2: LineSegment StartX=9.5 StartY=6.1 StartZ=0 EndX=-9.5 EndY=6.1 EndZ=0
    g3: LineSegment StartX=-9.5 StartY=6.1 StartZ=0 EndX=-9.5 EndY=-6.1 EndZ=0
    g4: GeomPoint [constr] X=0 Y=0 Z=0
  constraints (12):
    c: Coincident(g0,g1)
    c: Coincident(g1,g2)
    c: Coincident(g2,g3)
    c: Coincident(g3,g0)
    c: Horizontal(g0)
    c: Horizontal(g2)
    c: Vertical(g1)
    c: Vertical(g3)
    c: Symmetric(g2,g0,g4)
    c: Distance(g1,g3) = 19
    c: Distance(g0,g2) = 12.2
    c: Coincident(g4,g-1)
FEATURE [Sketcher::SketchObject] Sketch069  label="cilindro minore"
  ArcFitTolerance = 1e-06
  AttachmentSupport = -> [XZ_Plane004]
  FullyConstrained = true
  MakeInternals = false
  MapMode = 5
  Placement = pos=(0,0,0) rot=(1,0,0;1.5708rad)
  sketch-geometry (1):
    g0: Circle CenterX=0 CenterY=0 CenterZ=0 NormalX=0 NormalY=0 NormalZ=1 AngleXU=0 Radius=5.8
  constraints (2):
    c: Diameter(g0) = 11.6
    c: Coincident(g0,g-1)
FEATURE [Sketcher::SketchObject] Sketch070  label="cilindro maggiore"
  ArcFitTolerance = 1e-06
  AttachmentSupport = -> [XZ_Plane004]
  ExternalGeometry = -> [Sketch069]
  FullyConstrained = true
  MakeInternals = false
  MapMode = 5
  Placement = pos=(0,0,0) rot=(1,0,0;1.5708rad)
  sketch-geometry (1):
    g0: Circle CenterX=0 CenterY=0 CenterZ=0 NormalX=0 NormalY=0 NormalZ=1 AngleXU=0 Radius=6.5
  constraints (2):
    c: Coincident(g0,g-1)
    c: Diameter(g0) = 13
FEATURE [Sketcher::SketchObject] Sketch071  label="buco interno"
  ArcFitTolerance = 1e-06
  AttachmentSupport = -> [XZ_Plane004]
  ExternalGeometry = -> [Sketch069]
  FullyConstrained = true
  MakeInternals = false
  MapMode = 5
  Placement = pos=(0,0,0) rot=(1,0,0;1.5708rad)
  sketch-geometry (1):
    g0: Circle CenterX=0 CenterY=0 CenterZ=0 NormalX=0 NormalY=0 NormalZ=1 AngleXU=0 Radius=5
  constraints (2):
    c: Coincident(g0,g-1)
    c: Diameter(g0) = 10
FEATURE [PartDesign::Pad] Pad
  Direction = (0,-1,2e-16)
  Length = 1.2
  Length2 = 10
  Placement = pos=(0,0,0) rot=(1,0,0;1.5708rad)
  Profile = -> Sketch070
  ReferenceAxis = -> Sketch070 [N_Axis]
  Refine = true
  Suppressed = false
  Type = 0
FEATURE [PartDesign::Pad] Pad001
  BaseFeature = -> Pad
  Direction = (0,-1,2e-16)
  Length = 5.6
  Length2 = 10
  Placement = pos=(0,0,0) rot=(1,0,0;1.5708rad)
  Profile = -> Sketch069
  ReferenceAxis = -> Sketch069 [N_Axis]
  Refine = true
  Suppressed = false
  Type = 0
FEATURE [PartDesign::Pocket] Pocket
  BaseFeature = -> Pad001
  Direction = (0,1,-2e-16)
  Length = 7
  Length2 = 5
  Midplane = true
  Placement = pos=(0,0,0) rot=(1,0,0;1.5708rad)
  Profile = -> Sketch071
  ReferenceAxis = -> Sketch071 [N_Axis]
  Refine = true
  Suppressed = false
  Type = 0
FEATURE [PartDesign::Fillet] Fillet
  Base = -> Pocket [Face7]
  BaseFeature = -> Pocket
  Placement = pos=(0,0,0) rot=(1,0,0;1.5708rad)
  Radius = 1
  Refine = true
  SupportTransform = false
  Suppressed = false
  UseAllEdges = false
FEATURE [PartDesign::Body] Body004  label="pulsanti lato sinistro"
  AllowCompound = false
  Group = -> [Sketch069,Sketch070,Sketch071,Pad,Pad001,Pocket,Fillet]
  Origin = -> Origin004
  Tip = -> Fillet
FEATURE [Sketcher::SketchObject] Sketch072  label="buco per saldature e diodo driver solenoide"
  ArcFitTolerance = 1e-06
  AttachmentSupport = -> [XZ_Plane]
  ExternalGeometry = -> [Sketch038]
  FullyConstrained = true
  MakeInternals = false
  MapMode = 5
  Placement = pos=(0,0,0) rot=(1,0,0;1.5708rad)
  sketch-geometry (4):
    g0: LineSegment StartX=-212.269 StartY=-43.9083 StartZ=0 EndX=-207.197 EndY=-33.0326 EndZ=0
    g1: LineSegment StartX=-207.197 StartY=-33.0326 StartZ=0 EndX=-207.56 EndY=-32.8635 EndZ=0
    g2: LineSegment StartX=-207.56 StartY=-32.8635 StartZ=0 EndX=-212.631 EndY=-43.7392 EndZ=0
    g3: LineSegment StartX=-212.631 StartY=-43.7392 StartZ=0 EndX=-212.269 EndY=-43.9083 EndZ=0
  constraints (11):
    c: Coincident(g1,g0)
    c: Coincident(g2,g1)
    c: Coincident(g3,g2)
    c: Coincident(g3,g0)
    c: Parallel(g-3,g0)
    c: Parallel(g0,g2)
    c: Perpendicular(g0,g3)
    c: Perpendicular(g1,g0)
    c: Distance(g3) = 0.4
    c: Distance(g2) = 12
    c: Coincident(g0,g-3)
FEATURE [Part::Extrusion] Extrude074  label="Extrude buco per saldature e diodo driver solenoide"
  Base = -> Sketch072
  Dir = (0,-1,2e-16)
  DirMode = 2
  FaceMakerClass = Part::FaceMakerBullseye
  FaceMakerMode = 3
  LengthFwd = 14.6
  LengthRev = 0
  Solid = true
  Symmetric = true
FEATURE [Part::Cut] Cut042
  Base = -> Cut041
  Refine = true
  Tool = -> Extrude074
FEATURE [Sketcher::SketchObject] Sketch073  label="fori slargati blocco solenoide"
  ArcFitTolerance = 1e-06
  AttachmentSupport = -> [XY_Plane]
  ExternalGeometry = -> [Sketch030]
  FullyConstrained = true
  MakeInternals = false
  MapMode = 5
  sketch-geometry (2):
    g0: Circle CenterX=-152.209 CenterY=6.95 CenterZ=0 NormalX=0 NormalY=0 NormalZ=1 AngleXU=0 Radius=3.7
    g1: Circle CenterX=-130.41 CenterY=-6.95 CenterZ=0 NormalX=0 NormalY=0 NormalZ=1 AngleXU=0 Radius=3.7
  constraints (4):
    c: Diameter(g0) = 7.4
    c: Coincident(g0,g-3)
    c: Diameter(g1) = 7.4
    c: Coincident(g1,g-4)
FEATURE [Part::Extrusion] Extrude075  label="Extrude fori slargati blocco solenoide"
  Base = -> Sketch073
  Dir = (0,0,1)
  DirMode = 2
  FaceMakerClass = Part::FaceMakerBullseye
  FaceMakerMode = 3
  LengthFwd = 1.5
  LengthRev = 0
  Placement = pos=(0,0,36.4) rot=(0,0,1;0rad)
  Solid = true
  Symmetric = false
FEATURE [Part::Cut] Cut043
  Base = -> Cut042
  Refine = true
  Tool = -> Extrude075
FEATURE [Sketcher::SketchObject] Sketch074  label="lato sx pistola"
  ArcFitTolerance = 1e-06
  AttachmentSupport = -> [XZ_Plane]
  ExternalGeometry = -> [Sketch016,Sketch,Sketch058]
  FullyConstrained = true
  MakeInternals = false
  MapMode = 5
  Placement = pos=(0,0,0) rot=(1,0,0;1.5708rad)
  sketch-geometry (37):
    g0: LineSegment StartX=-82.8 StartY=3.2 StartZ=0 EndX=0 EndY=3.2 EndZ=0
    g1: LineSegment StartX=-82.8 StartY=3.2 StartZ=0 EndX=-82.8 EndY=6.2 EndZ=0
    g2: LineSegment [constr] StartX=-107.6 StartY=18 StartZ=0 EndX=-107.6 EndY=20 EndZ=0
    g3: LineSegment [constr] StartX=-132.428 StartY=18 StartZ=0 EndX=-132.428 EndY=20 EndZ=0
    g4: LineSegment StartX=-132.428 StartY=20 StartZ=0 EndX=-107.6 EndY=20 EndZ=0
    g5: ArcOfCircle CenterX=-107.6 CenterY=4 CenterZ=0 NormalX=0 NormalY=0 NormalZ=1 AngleXU=0 Radius=16 StartAngle=0.137937 EndAngle=1.5708
    g6: LineSegment StartX=-82.8 StartY=6.2 StartZ=0 EndX=-91.752 EndY=6.2 EndZ=0
    g7: LineSegment [constr] StartX=-145.743 StartY=8.32624 StartZ=0 EndX=-147.645 EndY=8.94427 EndZ=0
    g8: ArcOfCircle CenterX=-132.428 CenterY=4 CenterZ=0 NormalX=0 NormalY=0 NormalZ=1 AngleXU=0 Radius=16 StartAngle=1.5708 EndAngle=2.82743
    g9: LineSegment StartX=-215.932 StartY=-80.4316 StartZ=0 EndX=-176.685 EndY=-80.4316 EndZ=0
    g10: LineSegment StartX=-147.645 StartY=8.94427 StartZ=0 EndX=-176.685 EndY=-80.4316 EndZ=0
    g11: LineSegment [constr] StartX=-193.988 StartY=-2.33927 StartZ=0 EndX=-192.176 EndY=-3.18451 EndZ=0
    g12: LineSegment [constr] StartX=-217.232 StartY=-52.1862 StartZ=0 EndX=-215.42 EndY=-53.0314 EndZ=0
    g13: LineSegment StartX=-192.176 StartY=-3.18451 StartZ=0 EndX=-215.42 EndY=-53.0314 EndZ=0
    g14: ArcOfCircle CenterX=-184.801 CenterY=-67.3089 CenterZ=0 NormalX=0 NormalY=0 NormalZ=1 AngleXU=0 Radius=33.7833 StartAngle=2.70526 EndAngle=3.54053
    g15: ArcOfCircle CenterX=-207.583 CenterY=4 CenterZ=0 NormalX=0 NormalY=0 NormalZ=1 AngleXU=0 Radius=17 StartAngle=5.84685 EndAngle=7.56663
    g16: LineSegment StartX=-202.765 StartY=20.303 StartZ=0 EndX=-195.887 EndY=39.2 EndZ=0
    g17: LineSegment [constr] StartX=-193.885 StartY=33.0037 StartZ=0 EndX=-197.644 EndY=34.3718 EndZ=0
    g18: LineSegment StartX=-195.887 StartY=39.2 StartZ=0 EndX=0 EndY=39.2 EndZ=0
    g19: LineSegment StartX=0 StartY=3.2 StartZ=0 EndX=0 EndY=39.2 EndZ=0
    g20: LineSegment StartX=-189.939 StartY=31.5672 StartZ=0 EndX=-192.333 EndY=24.9893 EndZ=0
    g21: LineSegment StartX=-196.467 StartY=26.4942 StartZ=0 EndX=-194.073 EndY=33.0721 EndZ=0
    g22: Circle CenterX=-213.443 CenterY=-76.8316 CenterZ=0 NormalX=0 NormalY=0 NormalZ=1 AngleXU=0 Radius=1.8
    g23: Circle CenterX=-179.305 CenterY=-76.8316 CenterZ=0 NormalX=0 NormalY=0 NormalZ=1 AngleXU=0 Radius=1.8
    g24: Circle CenterX=-184.08 CenterY=34.8 CenterZ=0 NormalX=0 NormalY=0 NormalZ=1 AngleXU=0 Radius=1.8
    g25: Circle CenterX=-78.51 CenterY=34.8 CenterZ=0 NormalX=0 NormalY=0 NormalZ=1 AngleXU=0 Radius=1.8
    g26: Circle CenterX=-78.51 CenterY=7.6 CenterZ=0 NormalX=0 NormalY=0 NormalZ=1 AngleXU=0 Radius=1.8
    g27: Circle CenterX=-5.6 CenterY=34.8 CenterZ=0 NormalX=0 NormalY=0 NormalZ=1 AngleXU=0 Radius=1.8
    g28: Circle CenterX=-5.6 CenterY=7.6 CenterZ=0 NormalX=0 NormalY=0 NormalZ=1 AngleXU=0 Radius=1.8
    g29: LineSegment StartX=-190.127 StartY=31.6356 StartZ=0 EndX=-189.939 EndY=31.5672 EndZ=0
    g30: LineSegment StartX=-194.073 StartY=33.0721 StartZ=0 EndX=-193.885 EndY=33.0037 EndZ=0
    g31: LineSegment StartX=-193.885 StartY=33.0037 StartZ=0 EndX=-190.127 EndY=31.6356 EndZ=0
    g32: LineSegment StartX=-196.467 StartY=26.4942 StartZ=0 EndX=-192.333 EndY=24.9893 EndZ=0
    g33: Circle CenterX=-19 CenterY=21.2 CenterZ=0 NormalX=0 NormalY=0 NormalZ=1 AngleXU=0 Radius=6.3
    g34: Circle CenterX=-42 CenterY=21.2 CenterZ=0 NormalX=0 NormalY=0 NormalZ=1 AngleXU=0 Radius=6.3
    g35: Circle CenterX=-65 CenterY=21.2 CenterZ=0 NormalX=0 NormalY=0 NormalZ=1 AngleXU=0 Radius=6.3
    g36: LineSegment [constr] StartX=-4 StartY=21.2 StartZ=0 EndX=-65 EndY=21.2 EndZ=0
  constraints (96):
    c: Coincident(g0,g-41)
    c: Horizontal(g0)
    c: PointOnObject(g0,g-39)
    c: Coincident(g1,g0)
    c: Vertical(g1)
    c: DistanceY(g1,g1) = 3
    c: Coincident(g2,g-17)
    c: Vertical(g2)
    c: Coincident(g3,g-16)
    c: Vertical(g3)
    c: DistanceY(g2,g2) = 2
    c: DistanceY(g3,g3) = 2
    c: Coincident(g4,g3)
    c: Coincident(g4,g2)
    c: Coincident(g5,g-17)
    c: Coincident(g5,g2)
    c: Coincident(g6,g1)
    c: Horizontal(g6)
    c: Coincident(g6,g5)
    c: Coincident(g7,g-15)
    c: Coincident(g8,g7)
    c: Coincident(g8,g3)
    c: Coincident(g8,g-15)
    c: Horizontal(g9)
    c: DistanceY(g-13,g9) = 2
    c: Coincident(g10,g7)
    c: Parallel(g10,g-14)
    c: Coincident(g9,g10)
    c: Distance(g11) = 2
    c: Coincident(g11,g-11)
    c: Perpendicular(g-11,g11)
    c: Distance(g12) = 2
    c: Coincident(g12,g-12)
    c: Perpendicular(g-11,g12)
    c: Coincident(g13,g11)
    c: Coincident(g13,g12)
    c: Coincident(g14,g-32)
    c: Coincident(g14,g12)
    c: Coincident(g14,g9)
    c: Coincident(g15,g-10)
    c: Coincident(g15,g11)
    c: Parallel(g16,g-22)
    c: Distance(g17) = 4
    c: PointOnObject(g17,g16)
    c: Coincident(g15,g16)
    c: Horizontal(g18)
    c: Coincident(g18,g16)
    c: Coincident(g19,g0)
    c: PointOnObject(g19,g-39)
    c: DistanceY(g19,g-36) = 2
    c: Coincident(g18,g19)
    c: Diameter(g22) = 3.6
    c: Coincident(g22,g-9)
    c: Diameter(g23) = 3.6
    c: Coincident(g23,g-8)
    c: Diameter(g24) = 3.6
    c: Diameter(g25) = 3.6
    c: Diameter(g26) = 3.6
    c: Diameter(g27) = 3.6
    c: Diameter(g28) = 3.6
    c: Coincident(g27,g-4)
    c: Coincident(g28,g-3)
    c: Coincident(g25,g-6)
    c: Coincident(g26,g-5)
    c: Coincident(g24,g-7)
    c: Parallel(g20,g-21)
    c: Equal(g20,g-21)
    c: Parallel(g21,g-19)
    c: Equal(g21,g-19)
    c: Distance(g29) = 0.2
    c: Distance(g30) = 0.2
    c: Parallel(g29,g-20)
    c: Parallel(g31,g-20)
    c: Equal(g31,g-20)
    c: Coincident(g30,g31)
    c: Coincident(g31,g29)
    c: Coincident(g29,g-21)
    c: Parallel(g30,g31)
    c: Coincident(g17,g30)
    c: Coincident(g20,g29)
    c: Coincident(g21,g30)
    c: Perpendicular(g16,g17)
    c: Coincident(g32,g21)
    c: Coincident(g32,g20)
    c: Perpendicular(g10,g7)
    c: Diameter(g33) = 12.6
    c: Diameter(g34) = 12.6
    c: Diameter(g35) = 12.6
    c: Horizontal(g36)
    c: PointOnObject(g33,g36)
    c: PointOnObject(g34,g36)
    c: DistanceX(g34,g33) = 23
    c: DistanceX(g35,g34) = 23
    c: DistanceX(g33,g36) = 15
    c: Symmetric(g-24,g-24,g36)
    c: Coincident(g36,g35)
FEATURE [Sketcher::SketchObject] Sketch075  label="lato dx pistola"
  ArcFitTolerance = 1e-06
  AttachmentSupport = -> [XZ_Plane]
  ExternalGeometry = -> [Sketch016,Sketch,Sketch058,Sketch074]
  FullyConstrained = true
  MakeInternals = false
  MapMode = 5
  Placement = pos=(0,0,0) rot=(1,0,0;1.5708rad)
  sketch-geometry (61):
    g0: LineSegment StartX=-82.8 StartY=3.2 StartZ=0 EndX=0 EndY=3.2 EndZ=0
    g1: LineSegment StartX=-82.8 StartY=3.2 StartZ=0 EndX=-82.8 EndY=6.2 EndZ=0
    g2: LineSegment [constr] StartX=-107.6 StartY=18 StartZ=0 EndX=-107.6 EndY=20 EndZ=0
    g3: LineSegment [constr] StartX=-132.428 StartY=18 StartZ=0 EndX=-132.428 EndY=20 EndZ=0
    g4: LineSegment StartX=-132.428 StartY=20 StartZ=0 EndX=-107.6 EndY=20 EndZ=0
    g5: ArcOfCircle CenterX=-107.6 CenterY=4 CenterZ=0 NormalX=0 NormalY=0 NormalZ=1 AngleXU=0 Radius=16 StartAngle=0.137937 EndAngle=1.5708
    g6: LineSegment StartX=-82.8 StartY=6.2 StartZ=0 EndX=-91.752 EndY=6.2 EndZ=0
    g7: LineSegment [constr] StartX=-145.743 StartY=8.32624 StartZ=0 EndX=-147.645 EndY=8.94427 EndZ=0
    g8: ArcOfCircle CenterX=-132.428 CenterY=4 CenterZ=0 NormalX=0 NormalY=0 NormalZ=1 AngleXU=0 Radius=16 StartAngle=1.5708 EndAngle=2.82743
    g9: LineSegment StartX=-215.932 StartY=-80.4316 StartZ=0 EndX=-176.685 EndY=-80.4316 EndZ=0
    g10: LineSegment StartX=-147.645 StartY=8.94427 StartZ=0 EndX=-176.685 EndY=-80.4316 EndZ=0
    g11: LineSegment [constr] StartX=-193.988 StartY=-2.33927 StartZ=0 EndX=-192.176 EndY=-3.18451 EndZ=0
    g12: LineSegment [constr] StartX=-217.232 StartY=-52.1862 StartZ=0 EndX=-215.42 EndY=-53.0314 EndZ=0
    g13: LineSegment StartX=-192.176 StartY=-3.18451 StartZ=0 EndX=-215.42 EndY=-53.0314 EndZ=0
    g14: ArcOfCircle CenterX=-184.801 CenterY=-67.3089 CenterZ=0 NormalX=0 NormalY=0 NormalZ=1 AngleXU=0 Radius=33.7833 StartAngle=2.70526 EndAngle=3.54053
    g15: ArcOfCircle CenterX=-207.583 CenterY=4 CenterZ=0 NormalX=0 NormalY=0 NormalZ=1 AngleXU=0 Radius=17 StartAngle=5.84685 EndAngle=7.56663
    g16: LineSegment StartX=-202.765 StartY=20.303 StartZ=0 EndX=-195.887 EndY=39.2 EndZ=0
    g17: LineSegment [constr] StartX=-193.885 StartY=33.0037 StartZ=0 EndX=-197.644 EndY=34.3718 EndZ=0
    g18: LineSegment StartX=-195.887 StartY=39.2 StartZ=0 EndX=0 EndY=39.2 EndZ=0
    g19: LineSegment StartX=0 StartY=3.2 StartZ=0 EndX=0 EndY=39.2 EndZ=0
    g20: LineSegment StartX=-189.939 StartY=31.5672 StartZ=0 EndX=-192.333 EndY=24.9893 EndZ=0
    g21: LineSegment StartX=-196.467 StartY=26.4942 StartZ=0 EndX=-194.073 EndY=33.0721 EndZ=0
    g22: Circle CenterX=-213.443 CenterY=-76.8316 CenterZ=0 NormalX=0 NormalY=0 NormalZ=1 AngleXU=0 Radius=1.8
    g23: Circle CenterX=-179.305 CenterY=-76.8316 CenterZ=0 NormalX=0 NormalY=0 NormalZ=1 AngleXU=0 Radius=1.8
    g24: Circle CenterX=-184.08 CenterY=34.8 CenterZ=0 NormalX=0 NormalY=0 NormalZ=1 AngleXU=0 Radius=1.8
    g25: Circle CenterX=-78.51 CenterY=34.8 CenterZ=0 NormalX=0 NormalY=0 NormalZ=1 AngleXU=0 Radius=1.8
    g26: Circle CenterX=-78.51 CenterY=7.6 CenterZ=0 NormalX=0 NormalY=0 NormalZ=1 AngleXU=0 Radius=1.8
    g27: Circle CenterX=-5.6 CenterY=34.8 CenterZ=0 NormalX=0 NormalY=0 NormalZ=1 AngleXU=0 Radius=1.8
    g28: Circle CenterX=-5.6 CenterY=7.6 CenterZ=0 NormalX=0 NormalY=0 NormalZ=1 AngleXU=0 Radius=1.8
    g29: LineSegment StartX=-190.127 StartY=31.6356 StartZ=0 EndX=-189.939 EndY=31.5672 EndZ=0
    g30: LineSegment StartX=-194.073 StartY=33.0721 StartZ=0 EndX=-193.885 EndY=33.0037 EndZ=0
    g31: LineSegment StartX=-193.885 StartY=33.0037 StartZ=0 EndX=-190.127 EndY=31.6356 EndZ=0
    g32: LineSegment StartX=-196.467 StartY=26.4942 StartZ=0 EndX=-192.333 EndY=24.9893 EndZ=0
    g33: LineSegment [constr] StartX=-4 StartY=21.2 StartZ=0 EndX=-87.91 EndY=21.2 EndZ=0
    g34: GeomPoint [constr] X=-4 Y=21.2 Z=0
    g35: LineSegment [constr] StartX=-15.2 StartY=33.7 StartZ=0 EndX=-15.2 EndY=8.7 EndZ=0
    g36: LineSegment [constr] StartX=-15.2 StartY=33.7 StartZ=0 EndX=-56.2 EndY=33.7 EndZ=0
    g37: LineSegment [constr] StartX=-15.2 StartY=8.7 StartZ=0 EndX=-56.2 EndY=8.7 EndZ=0
    g38: LineSegment [constr] StartX=-56.2 StartY=33.7 StartZ=0 EndX=-56.2 EndY=8.7 EndZ=0
    g39: Circle CenterX=-18.6 CenterY=30.3 CenterZ=0 NormalX=0 NormalY=0 NormalZ=1 AngleXU=0 Radius=3.4
    g40: Circle CenterX=-18.6 CenterY=12.1 CenterZ=0 NormalX=0 NormalY=0 NormalZ=1 AngleXU=0 Radius=3.4
    g41: Circle CenterX=-43.2 CenterY=30.3 CenterZ=0 NormalX=0 NormalY=0 NormalZ=1 AngleXU=0 Radius=3.4
    g42: Circle CenterX=-43.2 CenterY=12.1 CenterZ=0 NormalX=0 NormalY=0 NormalZ=1 AngleXU=0 Radius=3.4
    g43: LineSegment [constr] StartX=-4 StartY=21.2 StartZ=0 EndX=-15.2 EndY=21.2 EndZ=0
    g44: LineSegment [constr] StartX=-15.2 StartY=21.2 StartZ=0 EndX=-36.2 EndY=21.2 EndZ=0
    g45: LineSegment [constr] StartX=-41.5 StartY=16.2 StartZ=0 EndX=-30.9 EndY=16.2 EndZ=0
    g46: LineSegment [constr] StartX=-30.9 StartY=16.2 StartZ=0 EndX=-30.9 EndY=26.2 EndZ=0
    g47: LineSegment [constr] StartX=-30.9 StartY=26.2 StartZ=0 EndX=-41.5 EndY=26.2 EndZ=0
    g48: LineSegment [constr] StartX=-41.5 StartY=26.2 StartZ=0 EndX=-41.5 EndY=16.2 EndZ=0
    g49: GeomPoint [constr] X=-36.2 Y=21.2 Z=0
    g50: Circle CenterX=-36.2 CenterY=21.2 CenterZ=0 NormalX=0 NormalY=0 NormalZ=1 AngleXU=0 Radius=2.8
    g51: LineSegment [constr] StartX=-24.2 StartY=26.7 StartZ=0 EndX=-24.2 EndY=15.7 EndZ=0
    g52: Circle CenterX=-24.2 CenterY=26.7 CenterZ=0 NormalX=0 NormalY=0 NormalZ=1 AngleXU=0 Radius=3
    g53: Circle CenterX=-24.2 CenterY=15.7 CenterZ=0 NormalX=0 NormalY=0 NormalZ=1 AngleXU=0 Radius=3
    g54: GeomPoint X=-18.6 Y=30.3 Z=0
    g55: GeomPoint X=-18.6 Y=12.1 Z=0
    g56: GeomPoint X=-43.2 Y=12.1 Z=0
    g57: GeomPoint X=-43.2 Y=30.3 Z=0
    g58: Circle CenterX=-65 CenterY=21.2 CenterZ=0 NormalX=0 NormalY=0 NormalZ=1 AngleXU=0 Radius=1.5
    g59: Circle CenterX=-42 CenterY=21.2 CenterZ=0 NormalX=0 NormalY=0 NormalZ=1 AngleXU=0 Radius=1.5
    g60: Circle CenterX=-19 CenterY=21.2 CenterZ=0 NormalX=0 NormalY=0 NormalZ=1 AngleXU=0 Radius=1.5
  constraints (149):
    c: Coincident(g0,g-41)
    c: Horizontal(g0)
    c: PointOnObject(g0,g-39)
    c: Coincident(g1,g0)
    c: Vertical(g1)
    c: DistanceY(g1,g1) = 3
    c: Coincident(g2,g-17)
    c: Vertical(g2)
    c: Coincident(g3,g-16)
    c: Vertical(g3)
    c: DistanceY(g2,g2) = 2
    c: DistanceY(g3,g3) = 2
    c: Coincident(g4,g3)
    c: Coincident(g4,g2)
    c: Coincident(g5,g-17)
    c: Coincident(g5,g2)
    c: Coincident(g6,g1)
    c: Horizontal(g6)
    c: Coincident(g6,g5)
    c: Coincident(g7,g-15)
    c: Coincident(g8,g7)
    c: Coincident(g8,g3)
    c: Coincident(g8,g-15)
    c: Horizontal(g9)
    c: DistanceY(g-13,g9) = 2
    c: Coincident(g10,g7)
    c: Parallel(g10,g-14)
    c: Coincident(g9,g10)
    c: Distance(g11) = 2
    c: Coincident(g11,g-11)
    c: Perpendicular(g-11,g11)
    c: Distance(g12) = 2
    c: Coincident(g12,g-12)
    c: Perpendicular(g-11,g12)
    c: Coincident(g13,g11)
    c: Coincident(g13,g12)
    c: Coincident(g14,g-32)
    c: Coincident(g14,g12)
    c: Coincident(g14,g9)
    c: Coincident(g15,g-10)
    c: Coincident(g15,g11)
    c: Parallel(g16,g-22)
    c: Distance(g17) = 4
    c: PointOnObject(g17,g16)
    c: Coincident(g15,g16)
    c: Horizontal(g18)
    c: Coincident(g18,g16)
    c: Coincident(g19,g0)
    c: PointOnObject(g19,g-39)
    c: DistanceY(g19,g-36) = 2
    c: Coincident(g18,g19)
    c: Diameter(g22) = 3.6
    c: Coincident(g22,g-9)
    c: Diameter(g23) = 3.6
    c: Coincident(g23,g-8)
    c: Diameter(g24) = 3.6
    c: Diameter(g25) = 3.6
    c: Diameter(g26) = 3.6
    c: Diameter(g27) = 3.6
    c: Diameter(g28) = 3.6
    c: Coincident(g27,g-4)
    c: Coincident(g28,g-3)
    c: Coincident(g25,g-6)
    c: Coincident(g26,g-5)
    c: Coincident(g24,g-7)
    c: Parallel(g20,g-21)
    c: Equal(g20,g-21)
    c: Parallel(g21,g-19)
    c: Equal(g21,g-19)
    c: Distance(g29) = 0.2
    c: Distance(g30) = 0.2
    c: Parallel(g29,g-20)
    c: Parallel(g31,g-20)
    c: Equal(g31,g-20)
    c: Coincident(g30,g31)
    c: Coincident(g31,g29)
    c: Coincident(g29,g-21)
    c: Parallel(g30,g31)
    c: Coincident(g17,g30)
    c: Coincident(g20,g29)
    c: Coincident(g21,g30)
    c: Perpendicular(g16,g17)
    c: Coincident(g32,g21)
    c: Coincident(g32,g20)
    c: Perpendicular(g10,g7)
    c: Horizontal(g33)
    c: Symmetric(g-24,g-24,g33)
    c: PointOnObject(g33,g-28)
    c: Symmetric(g-24,g-24,g34)
    c: DistanceY(g35,g35) = 25
    c: Symmetric(g35,g35,g33)
    c: Distance(g36) = 41
    c: Coincident(g36,g35)
    c: Horizontal(g36)
    c: Coincident(g37,g35)
    c: Horizontal(g37)
    c: Coincident(g38,g36)
    c: Vertical(g38)
    c: Coincident(g37,g38)
    c: Diameter(g39) = 6.8
    c: Diameter(g40) = 6.8
    c: Tangent(g39,g36)
    c: Tangent(g40,g37)
    c: Tangent(g39,g35)
    c: Tangent(g40,g35)
    c: Diameter(g41) = 6.8
    c: Diameter(g42) = 6.8
    c: Tangent(g41,g36)
    c: Tangent(g42,g37)
    c: DistanceX(g41,g39) = 24.6
    c: DistanceX(g42,g40) = 24.6
    c: Distance(g43) = 11.2
    c: Coincident(g43,g33)
    c: PointOnObject(g43,g33)
    c: PointOnObject(g43,g35)
    c: Distance(g44) = 21
    c: Coincident(g44,g43)
    c: PointOnObject(g44,g33)
    c: Coincident(g45,g46)
    c: Coincident(g46,g47)
    c: Coincident(g47,g48)
    c: Coincident(g48,g45)
    c: Horizontal(g45)
    c: Horizontal(g47)
    c: Vertical(g46)
    c: Vertical(g48)
    c: Symmetric(g47,g45,g49)
    c: Distance(g46,g48) = 10.6
    c: Distance(g45,g47) = 10
    c: Coincident(g49,g44)
    c: Diameter(g50) = 5.6
    c: Coincident(g50,g44)
    c: Distance(g51) = 11
    c: Symmetric(g51,g51,g33)
    c: DistanceX(g51,g43) = 9
    c: Diameter(g52) = 6
    c: Coincident(g52,g51)
    c: Diameter(g53) = 6
    c: Coincident(g53,g51)
    c: Coincident(g40,g55)
    c: Coincident(g39,g54)
    c: Coincident(g41,g57)
    c: Coincident(g42,g56)
    c: Diameter(g58) = 3
    c: Diameter(g59) = 3
    c: Diameter(g60) = 3
    c: Coincident(g58,g-44)
    c: Coincident(g59,g-46)
    c: Coincident(g60,g-45)
FEATURE [Sketcher::SketchObject] Sketch078
  ArcFitTolerance = 1e-06
  AttachmentSupport = -> [XZ_Plane005]
  FullyConstrained = true
  MakeInternals = false
  MapMode = 5
  Placement = pos=(0,0,0) rot=(1,0,0;1.5708rad)
  sketch-geometry (5):
    g0: LineSegment [constr] StartX=0 StartY=5.5 StartZ=0 EndX=0 EndY=-5.5 EndZ=0
    g1: ArcOfCircle CenterX=0 CenterY=5.5 CenterZ=0 NormalX=0 NormalY=0 NormalZ=1 AngleXU=0 Radius=2.7 StartAngle=0 EndAngle=3.14159
    g2: ArcOfCircle CenterX=0 CenterY=-5.5 CenterZ=0 NormalX=0 NormalY=0 NormalZ=1 AngleXU=0 Radius=2.7 StartAngle=3.1416 EndAngle=6.28318
    g3: LineSegment StartX=-2.7 StartY=5.5 StartZ=0 EndX=-2.7 EndY=-5.50001 EndZ=0
    g4: LineSegment StartX=2.7 StartY=5.5 StartZ=0 EndX=2.7 EndY=-5.50001 EndZ=0
  constraints (13):
    c: Distance(g0) = 11
    c: Vertical(g0)
    c: Symmetric(g0,g0,g-1)
    c: Radius(g1) = 2.7
    c: Coincident(g1,g0)
    c: Radius(g2) = 2.7
    c: Coincident(g2,g0)
    c: Vertical(g3)
    c: Vertical(g4)
    c: Coincident(g2,g4)
    c: Coincident(g2,g3)
    c: Tangent(g3,g1) = -1.5708
    c: Tangent(g4,g1) = 1.5708
FEATURE [PartDesign::Pad] Pad002
  Direction = (0,-1,2e-16)
  Length = 0.8
  Length2 = 10
  Placement = pos=(0,0,0) rot=(1,0,0;1.5708rad)
  Profile = -> Sketch078
  ReferenceAxis = -> Sketch078 [N_Axis]
  Refine = true
  Suppressed = false
  Type = 0
FEATURE [Sketcher::SketchObject] Sketch079
  ArcFitTolerance = 1e-06
  AttachmentSupport = -> [XZ_Plane005]
  ExternalGeometry = -> [Sketch078]
  FullyConstrained = true
  MakeInternals = false
  MapMode = 5
  Placement = pos=(0,0,0) rot=(1,0,0;1.5708rad)
  sketch-geometry (2):
    g0: Circle CenterX=-1e-16 CenterY=5.5 CenterZ=0 NormalX=0 NormalY=0 NormalZ=1 AngleXU=0 Radius=2.7
    g1: Circle CenterX=0 CenterY=-5.5 CenterZ=0 NormalX=0 NormalY=0 NormalZ=1 AngleXU=0 Radius=2.7
  constraints (4):
    c: Coincident(g0,g-3)
    c: PointOnObject(g-3,g0)
    c: Coincident(g1,g-4)
    c: Equal(g1,g-4)
FEATURE [PartDesign::Pad] Pad003
  BaseFeature = -> Pad002
  Direction = (0,-1,2e-16)
  Length = 5
  Length2 = 10
  Placement = pos=(0,0,0) rot=(1,0,0;1.5708rad)
  Profile = -> Sketch079
  ReferenceAxis = -> Sketch079 [N_Axis]
  Refine = true
  Suppressed = false
  Type = 0
FEATURE [PartDesign::Fillet] Fillet001
  Base = -> Pad003 [Edge16,Edge14]
  BaseFeature = -> Pad003
  Placement = pos=(0,0,0) rot=(1,0,0;1.5708rad)
  Radius = 0.4
  Refine = true
  SupportTransform = false
  Suppressed = false
  UseAllEdges = false
FEATURE [PartDesign::Body] Body005  label="pulsanti lato destro"
  AllowCompound = false
  Group = -> [Sketch078,Pad002,Sketch079,Pad003,Fillet001]
  Origin = -> Origin005
  Tip = -> Fillet001
FEATURE [PartDesign::SubShapeBinder] Binder
  BindCopyOnChange = 0
  BindMode = 0
  ClaimChildren = false
  Context = -> Body006 [Binder.]
  Fuse = false
  MakeFace = true
  OffsetFill = false
  OffsetIntersection = false
  OffsetJoinType = 0
  OffsetOpenResult = false
  PartialLoad = false
  Refine = true
  Relative = true
  Support = -> [Body[Sketch074.]]
  _Version = 2
FEATURE [PartDesign::SubShapeBinder] Binder001
  BindCopyOnChange = 0
  BindMode = 0
  ClaimChildren = false
  Context = -> Body007 [Binder001.]
  Fuse = false
  MakeFace = true
  OffsetFill = false
  OffsetIntersection = false
  OffsetJoinType = 0
  OffsetOpenResult = false
  PartialLoad = false
  Refine = true
  Relative = true
  Support = -> [Body[Sketch075.]]
  _Version = 2
FEATURE [Mesh::Feature] logo_per_PCB_definitivo_positivo
  Placement = pos=(-191,17,-66) rot=(0,1,1;0rad)
FEATURE [Sketcher::SketchObject] Sketch114  label="Sketch114 - base lato DX"
  ArcFitTolerance = 1e-06
  AttachmentSupport = -> [Binder001]
  ExternalGeometry = -> [Binder001]
  FullyConstrained = true
  MakeInternals = false
  MapMode = 5
  Placement = pos=(0,1e-15,0) rot=(0,0.707107,0.707107;3.14159rad)
  sketch-geometry (30):
    g0: Circle CenterX=5.6 CenterY=34.8 CenterZ=0 NormalX=0 NormalY=0 NormalZ=1 AngleXU=0 Radius=1.8
    g1: Circle CenterX=5.6 CenterY=7.6 CenterZ=0 NormalX=0 NormalY=0 NormalZ=1 AngleXU=0 Radius=1.8
    g2: Circle CenterX=24.2 CenterY=26.7 CenterZ=0 NormalX=0 NormalY=0 NormalZ=1 AngleXU=0 Radius=3
    g3: Circle CenterX=24.2 CenterY=15.7 CenterZ=0 NormalX=0 NormalY=0 NormalZ=1 AngleXU=0 Radius=3
    g4: Circle CenterX=36.2 CenterY=21.2 CenterZ=0 NormalX=0 NormalY=0 NormalZ=1 AngleXU=0 Radius=2.8
    g5: Circle CenterX=78.51 CenterY=34.8 CenterZ=0 NormalX=0 NormalY=0 NormalZ=1 AngleXU=0 Radius=1.8
    g6: Circle CenterX=78.51 CenterY=7.6 CenterZ=0 NormalX=0 NormalY=0 NormalZ=1 AngleXU=0 Radius=1.8
    g7: Circle CenterX=184.08 CenterY=34.8 CenterZ=0 NormalX=0 NormalY=0 NormalZ=1 AngleXU=0 Radius=1.8
    g8: Circle CenterX=213.443 CenterY=-76.8316 CenterZ=0 NormalX=0 NormalY=0 NormalZ=1 AngleXU=0 Radius=1.8
    g9: Circle CenterX=179.305 CenterY=-76.8316 CenterZ=0 NormalX=0 NormalY=0 NormalZ=1 AngleXU=0 Radius=1.8
    g10: ArcOfCircle [constr] CenterX=132.428 CenterY=4 CenterZ=0 NormalX=0 NormalY=0 NormalZ=1 AngleXU=0 Radius=16 StartAngle=0.314159 EndAngle=1.5708
    g11: ArcOfCircle CenterX=107.6 CenterY=4 CenterZ=0 NormalX=0 NormalY=0 NormalZ=1 AngleXU=0 Radius=16 StartAngle=1.5708 EndAngle=3.00366
    g12: ArcOfCircle CenterX=207.583 CenterY=4 CenterZ=0 NormalX=0 NormalY=0 NormalZ=1 AngleXU=0 Radius=17 StartAngle=1.85815 EndAngle=3.57792
    g13: ArcOfCircle CenterX=184.801 CenterY=-67.3089 CenterZ=0 NormalX=0 NormalY=0 NormalZ=1 AngleXU=0 Radius=33.7833 StartAngle=5.88425 EndAngle=6.71952
    g14: LineSegment StartX=0 StartY=39.2 StartZ=0 EndX=0 EndY=3.2 EndZ=0
    g15: LineSegment StartX=0 StartY=3.2 StartZ=0 EndX=82.8 EndY=3.2 EndZ=0
    g16: LineSegment StartX=82.8 StartY=3.2 StartZ=0 EndX=82.8 EndY=6.2 EndZ=0
    g17: LineSegment StartX=82.8 StartY=6.2 StartZ=0 EndX=91.752 EndY=6.2 EndZ=0
    g18: LineSegment StartX=107.6 StartY=20 StartZ=0 EndX=132.428 EndY=20 EndZ=0
    g19: LineSegment StartX=147.645 StartY=8.94427 StartZ=0 EndX=176.685 EndY=-80.4316 EndZ=0
    g20: LineSegment StartX=176.685 StartY=-80.4316 StartZ=0 EndX=215.932 EndY=-80.4316 EndZ=0
    g21: LineSegment StartX=215.42 StartY=-53.0314 StartZ=0 EndX=192.176 EndY=-3.18451 EndZ=0
    g22: LineSegment StartX=202.765 StartY=20.303 StartZ=0 EndX=195.887 EndY=39.2 EndZ=0
    g23: LineSegment StartX=195.887 StartY=39.2 StartZ=0 EndX=0 EndY=39.2 EndZ=0
    g24: LineSegment StartX=196.467 StartY=26.4942 StartZ=0 EndX=194.073 EndY=33.0721 EndZ=0
    g25: LineSegment StartX=194.073 StartY=33.0721 StartZ=0 EndX=189.939 EndY=31.5672 EndZ=0
    g26: LineSegment StartX=189.939 StartY=31.5672 StartZ=0 EndX=192.333 EndY=24.9893 EndZ=0
    g27: LineSegment StartX=192.333 StartY=24.9893 StartZ=0 EndX=196.467 EndY=26.4942 EndZ=0
    g28: LineSegment StartX=132.428 StartY=20 StartZ=0 EndX=144.053 EndY=20 EndZ=0
    g29: LineSegment StartX=144.053 StartY=20 StartZ=0 EndX=147.645 EndY=8.94427 EndZ=0
  constraints (65):
    c: Equal(g0,g-25)
    c: Equal(g2,g-29)
    c: Equal(g3,g-30)
    c: Equal(g4,g-28)
    c: Equal(g1,g-26)
    c: Coincident(g0,g-25)
    c: Coincident(g1,g-26)
    c: Coincident(g2,g-29)
    c: Coincident(g3,g-30)
    c: Coincident(g4,g-28)
    c: Equal(g5,g-23)
    c: Equal(g6,g-24)
    c: Coincident(g5,g-23)
    c: Coincident(g6,g-24)
    c: Equal(g7,g-20)
    c: Coincident(g7,g-20)
    c: Equal(g9,g-22)
    c: Coincident(g9,g-22)
    c: Equal(g8,g-21)
    c: Coincident(g8,g-21)
    c: Equal(g13,g-12)
    c: Equal(g12,g-14)
    c: Equal(g10,g-9)
    c: Equal(g11,g-7)
    c: Coincident(g14,g-27)
    c: Coincident(g14,g-27)
    c: Coincident(g15,g14)
    c: Coincident(g15,g-5)
    c: Coincident(g16,g15)
    c: Coincident(g16,g-6)
    c: Coincident(g17,g16)
    c: Coincident(g17,g-7)
    c: Coincident(g11,g17)
    c: Coincident(g11,g-8)
    c: Coincident(g18,g11)
    c: Coincident(g18,g-9)
    c: Coincident(g10,g18)
    c: Coincident(g10,g-10)
    c: Coincident(g19,g10)
    c: Coincident(g19,g-11)
    c: Coincident(g20,g19)
    c: Coincident(g20,g-12)
    c: Coincident(g13,g20)
    c: Coincident(g13,g-13)
    c: Coincident(g21,g13)
    c: Coincident(g21,g-14)
    c: Coincident(g12,g21)
    c: Coincident(g12,g-15)
    c: Coincident(g22,g12)
    c: Coincident(g22,g-15)
    c: Coincident(g23,g22)
    c: Coincident(g23,g14)
    c: Coincident(g24,g-18)
    c: Coincident(g24,g-16)
    c: Coincident(g25,g24)
    c: Coincident(g25,g-19)
    c: Coincident(g26,g25)
    c: Coincident(g26,g-19)
    c: Coincident(g27,g26)
    c: Coincident(g27,g24)
    c: Coincident(g29,g10)
    c: Coincident(g28,g10)
    c: Coincident(g29,g28)
    c: Parallel(g28,g18)
    c: Parallel(g29,g19)
FEATURE [PartDesign::Pad] Pad011
  Direction = (0,1,-2e-16)
  Length = 2
  Length2 = 10
  Profile = -> Sketch114
  ReferenceAxis = -> Sketch114 [N_Axis]
  Refine = true
  Reversed = true
  Suppressed = false
  Type = 0
FEATURE [Sketcher::SketchObject] Sketch115
  ArcFitTolerance = 1e-06
  AttachmentSupport = -> [Pad011]
  ExternalGeometry = -> [Binder001]
  FullyConstrained = true
  MakeInternals = false
  MapMode = 5
  Placement = pos=(0,1.7e-15,0) rot=(0,0.707107,0.707107;3.14159rad)
  sketch-geometry (4):
    g0: ArcOfCircle CenterX=24.2 CenterY=26.7 CenterZ=0 NormalX=0 NormalY=0 NormalZ=1 AngleXU=0 Radius=3 StartAngle=4.48384e-08 EndAngle=3.14159
    g1: ArcOfCircle CenterX=24.2 CenterY=15.7 CenterZ=0 NormalX=0 NormalY=0 NormalZ=1 AngleXU=0 Radius=3 StartAngle=3.14159 EndAngle=6.28318
    g2: LineSegment StartX=21.2 StartY=26.7 StartZ=0 EndX=21.2 EndY=15.7 EndZ=0
    g3: LineSegment StartX=27.2 StartY=26.7 StartZ=0 EndX=27.2 EndY=15.7 EndZ=0
  constraints (12):
    c: Equal(g1,g-4)
    c: Equal(g0,g-3)
    c: Coincident(g0,g-3)
    c: Coincident(g1,g-4)
    c: Vertical(g2)
    c: Vertical(g3)
    c: Tangent(g3,g-3)
    c: Tangent(g2,g-3)
    c: Coincident(g0,g2)
    c: Coincident(g0,g3)
    c: Coincident(g1,g2)
    c: Coincident(g3,g1)
FEATURE [Sketcher::SketchObject] Sketch117  label="Sketch117 - fori per inserto M3 x 3 x 4.5"
  ArcFitTolerance = 1e-06
  AttachmentSupport = -> [Pad011]
  ExternalGeometry = -> [Binder001]
  FullyConstrained = true
  MakeInternals = false
  MapMode = 5
  Placement = pos=(0,1.7e-15,0) rot=(0,0.707107,0.707107;3.14159rad)
  sketch-geometry (4):
    g0: Circle CenterX=43.2 CenterY=30.3 CenterZ=0 NormalX=0 NormalY=0 NormalZ=1 AngleXU=0 Radius=2.25
    g1: Circle CenterX=43.2 CenterY=12.1 CenterZ=0 NormalX=0 NormalY=0 NormalZ=1 AngleXU=0 Radius=2.25
    g2: Circle CenterX=18.6 CenterY=30.3 CenterZ=0 NormalX=0 NormalY=0 NormalZ=1 AngleXU=0 Radius=2.25
    g3: Circle CenterX=18.6 CenterY=12.1 CenterZ=0 NormalX=0 NormalY=0 NormalZ=1 AngleXU=0 Radius=2.25
  constraints (8):
    c: Diameter(g0) = 4.5
    c: Diameter(g1) = 4.5
    c: Diameter(g2) = 4.5
    c: Diameter(g3) = 4.5
    c: Coincident(g2,g-3)
    c: Coincident(g3,g-6)
    c: Coincident(g0,g-4)
    c: Coincident(g1,g-5)
FEATURE [Sketcher::SketchObject] Sketch118
  ArcFitTolerance = 1e-06
  AttachmentSupport = -> [Pad011]
  ExternalGeometry = -> [Binder001]
  FullyConstrained = true
  MakeInternals = false
  MapMode = 5
  Placement = pos=(0,-2,0) rot=(1,0,0;1.5708rad)
  sketch-geometry (12):
    g0: Circle CenterX=-78.51 CenterY=34.8 CenterZ=0 NormalX=0 NormalY=0 NormalZ=1 AngleXU=0 Radius=1.8
    g1: Circle CenterX=-78.51 CenterY=7.6 CenterZ=0 NormalX=0 NormalY=0 NormalZ=1 AngleXU=0 Radius=1.8
    g2: Circle CenterX=-5.6 CenterY=34.8 CenterZ=0 NormalX=0 NormalY=0 NormalZ=1 AngleXU=0 Radius=1.8
    g3: Circle CenterX=-5.6 CenterY=7.6 CenterZ=0 NormalX=0 NormalY=0 NormalZ=1 AngleXU=0 Radius=1.8
    g4: LineSegment StartX=0 StartY=39.2 StartZ=0 EndX=0 EndY=3.2 EndZ=0
    g5: LineSegment StartX=0 StartY=3.2 StartZ=0 EndX=-82.8 EndY=3.2 EndZ=0
    g6: LineSegment StartX=-82.8 StartY=3.2 StartZ=0 EndX=-82.8 EndY=39.2 EndZ=0
    g7: LineSegment StartX=-82.8 StartY=39.2 StartZ=0 EndX=0 EndY=39.2 EndZ=0
    g8: ArcOfCircle CenterX=-65 CenterY=21.2 CenterZ=0 NormalX=0 NormalY=0 NormalZ=1 AngleXU=0 Radius=10 StartAngle=1.5708 EndAngle=4.71239
    g9: ArcOfCircle CenterX=-19 CenterY=21.2 CenterZ=0 NormalX=0 NormalY=0 NormalZ=1 AngleXU=0 Radius=10 StartAngle=4.71239 EndAngle=7.85398
    g10: LineSegment StartX=-65 StartY=31.2 StartZ=0 EndX=-19 EndY=31.2 EndZ=0
    g11: LineSegment StartX=-65 StartY=11.2 StartZ=0 EndX=-19 EndY=11.2 EndZ=0
  constraints (25):
    c: Equal(g2,g-5)
    c: Equal(g3,g-7)
    c: Equal(g1,g-6)
    c: Equal(g0,g-4)
    c: Coincident(g0,g-4)
    c: Coincident(g1,g-6)
    c: Coincident(g3,g-7)
    c: Coincident(g2,g-5)
    c: Coincident(g4,g-8)
    c: Coincident(g4,g-9)
    c: Coincident(g5,g4)
    c: Coincident(g5,g-10)
    c: Coincident(g6,g5)
    c: PointOnObject(g6,g-3)
    c: Vertical(g6)
    c: Coincident(g7,g6)
    c: Coincident(g7,g4)
    c: Tangent(g8,g10) = 1.5708
    c: Tangent(g8,g11) = -1.5708
    c: Tangent(g9,g10) = 1.5708
    c: Tangent(g9,g11) = -1.5708
    c: Equal(g8,g9)
    c: Radius(g8) = 10
    c: Coincident(g8,g-11)
    c: Coincident(g9,g-12)
FEATURE [Sketcher::SketchObject] Sketch120
  ArcFitTolerance = 1e-06
  AttachmentSupport = -> [Pad011]
  ExternalGeometry = -> [Binder001]
  FullyConstrained = true
  MakeInternals = false
  MapMode = 5
  Placement = pos=(0,-2,0) rot=(1,0,0;1.5708rad)
  sketch-geometry (4):
    g0: LineSegment StartX=-137.815 StartY=39.2 StartZ=0 EndX=-142.655 EndY=24.303 EndZ=0
    g1: LineSegment StartX=-137.815 StartY=39.2 StartZ=0 EndX=-110.815 EndY=39.2 EndZ=0
    g2: LineSegment StartX=-142.655 StartY=24.303 StartZ=0 EndX=-110.815 EndY=24.303 EndZ=0
    g3: ArcOfCircle CenterX=-92.2534 CenterY=31.7515 CenterZ=0 NormalX=0 NormalY=0 NormalZ=1 AngleXU=0 Radius=20 StartAngle=2.75997 EndAngle=3.52321
  constraints (12):
    c: PointOnObject(g0,g-3)
    c: Coincident(g1,g0)
    c: PointOnObject(g1,g-3)
    c: Coincident(g2,g0)
    c: Horizontal(g2)
    c: Tangent(g0,g-4)
    c: Vertical(g2,g1)
    c: DistanceX(g1,g1) = 27
    c: DistanceY(g-6,g0) = 4
    c: Radius(g3) = 20
    c: Coincident(g3,g1)
    c: Coincident(g3,g2)
FEATURE [Sketcher::SketchObject] Sketch121
  ArcFitTolerance = 1e-06
  AttachmentSupport = -> [Pad011]
  ExternalGeometry = -> [Binder001]
  FullyConstrained = true
  MakeInternals = false
  MapMode = 5
  Placement = pos=(0,-2,0) rot=(1,0,0;1.5708rad)
  sketch-geometry (15):
    g0: LineSegment StartX=-137.815 StartY=39.2 StartZ=0 EndX=-143.955 EndY=20.303 EndZ=0
    g1: LineSegment StartX=-143.955 StartY=20.303 StartZ=0 EndX=-190.141 EndY=20.303 EndZ=0
    g2: LineSegment StartX=-190.141 StartY=20.303 StartZ=0 EndX=-186.139 EndY=31.3 EndZ=0
    g3: LineSegment StartX=-178.754 StartY=39.2 StartZ=0 EndX=-180.791 EndY=33.6029 EndZ=0
    g4: ArcOfCircle CenterX=-184.08 CenterY=34.8 CenterZ=0 NormalX=0 NormalY=0 NormalZ=1 AngleXU=0 Radius=3.5 StartAngle=4.71239 EndAngle=5.93412
    g5: LineSegment StartX=-184.08 StartY=31.3 StartZ=0 EndX=-186.139 EndY=31.3 EndZ=0
    g6: LineSegment StartX=-137.815 StartY=39.2 StartZ=0 EndX=-156.815 EndY=39.2 EndZ=0
    g7: LineSegment StartX=-168.815 StartY=39.2 StartZ=0 EndX=-178.754 EndY=39.2 EndZ=0
    g8: LineSegment StartX=-157.815 StartY=39.2 StartZ=0 EndX=-167.815 EndY=39.2 EndZ=0
    g9: LineSegment StartX=-168.815 StartY=31.2 StartZ=0 EndX=-156.815 EndY=31.2 EndZ=0
    g10: LineSegment StartX=-167.436 StartY=36.2 StartZ=0 EndX=-157.436 EndY=36.2 EndZ=0
    g11: ArcOfCircle CenterX=-176.411 CenterY=35.2 CenterZ=0 NormalX=0 NormalY=0 NormalZ=1 AngleXU=0 Radius=20 StartAngle=6.08183 EndAngle=6.48454
    g12: ArcOfCircle CenterX=-188.411 CenterY=35.2 CenterZ=0 NormalX=0 NormalY=0 NormalZ=1 AngleXU=0 Radius=20 StartAngle=6.08183 EndAngle=6.48454
    g13: ArcOfCircle CenterX=-177.411 CenterY=35.2 CenterZ=0 NormalX=0 NormalY=0 NormalZ=1 AngleXU=0 Radius=20 StartAngle=0.0500209 EndAngle=0.201358
    g14: ArcOfCircle CenterX=-187.411 CenterY=35.2 CenterZ=0 NormalX=0 NormalY=0 NormalZ=1 AngleXU=0 Radius=20 StartAngle=0.0500209 EndAngle=0.201358
  constraints (46):
    c: PointOnObject(g0,g-3)
    c: Tangent(g0,g-5)
    c: Coincident(g1,g0)
    c: Horizontal(g1)
    c: Coincident(g2,g1)
    c: PointOnObject(g3,g-3)
    c: Parallel(g3,g-6)
    c: Parallel(g2,g-6)
    c: Radius(g4) = 3.5
    c: Coincident(g4,g-7)
    c: Tangent(g3,g4) = 1.5708
    c: Horizontal(g5)
    c: Tangent(g5,g4) = 1.5708
    c: DistanceX(g-8,g5) = 3.8
    c: Coincident(g2,g5)
    c: Coincident(g6,g0)
    c: PointOnObject(g6,g-3)
    c: DistanceX(g6,g6) = 19
    c: PointOnObject(g7,g-3)
    c: DistanceX(g7,g6) = 12
    c: Coincident(g7,g3)
    c: PointOnObject(g8,g-3)
    c: PointOnObject(g8,g-3)
    c: DistanceX(g8,g8) = 10
    c: DistanceX(g8,g6) = 1
    c: Horizontal(g9)
    c: Vertical(g7,g9)
    c: Vertical(g6,g9)
    c: DistanceY(g9,g7) = 8
    c: Horizontal(g10)
    c: Equal(g8,g10)
    c: DistanceY(g10,g8) = 3
    c: Radius(g11) = 20
    c: Coincident(g11,g6)
    c: Coincident(g11,g9)
    c: Radius(g12) = 20
    c: Coincident(g12,g7)
    c: Coincident(g12,g9)
    c: Equal(g13,g11)
    c: Coincident(g13,g8)
    c: Coincident(g13,g10)
    c: Horizontal(g13,g11)
    c: Equal(g14,g12)
    c: Coincident(g14,g8)
    c: Coincident(g14,g10)
    c: Horizontal(g1,g-6)
FEATURE [Sketcher::SketchObject] Sketch122
  ArcFitTolerance = 1e-06
  AttachmentSupport = -> [Pad011]
  ExternalGeometry = -> [Binder001]
  FullyConstrained = true
  MakeInternals = false
  MapMode = 5
  Placement = pos=(0,-2,0) rot=(1,0,0;1.5708rad)
  sketch-geometry (8):
    g0: ArcOfCircle CenterX=-184.801 CenterY=-67.3089 CenterZ=0 NormalX=0 NormalY=0 NormalZ=1 AngleXU=0 Radius=33.7833 StartAngle=2.70526 EndAngle=3.54053
    g1: LineSegment StartX=-176.685 StartY=-80.4316 StartZ=0 EndX=-215.932 EndY=-80.4316 EndZ=0
    g2: LineSegment StartX=-215.42 StartY=-53.0314 StartZ=0 EndX=-192.176 EndY=-3.18454 EndZ=0
    g3: ArcOfCircle CenterX=-207.583 CenterY=4 CenterZ=0 NormalX=0 NormalY=0 NormalZ=1 AngleXU=0 Radius=17 StartAngle=5.84685 EndAngle=7.56663
    g4: Circle CenterX=-213.443 CenterY=-76.8316 CenterZ=0 NormalX=0 NormalY=0 NormalZ=1 AngleXU=0 Radius=3
    g5: Circle CenterX=-179.305 CenterY=-76.8316 CenterZ=0 NormalX=0 NormalY=0 NormalZ=1 AngleXU=0 Radius=3
    g6: LineSegment StartX=-143.955 StartY=20.303 StartZ=0 EndX=-176.685 EndY=-80.4316 EndZ=0
    g7: LineSegment StartX=-202.765 StartY=20.303 StartZ=0 EndX=-143.955 EndY=20.303 EndZ=0
  constraints (18):
    c: Coincident(g0,g-7)
    c: Coincident(g0,g-8)
    c: Coincident(g1,g0)
    c: Tangent(g2,g-5)
    c: Coincident(g3,g-6)
    c: Coincident(g2,g3)
    c: Coincident(g0,g2)
    c: Diameter(g4) = 6
    c: Diameter(g5) = 6
    c: Coincident(g4,g-9)
    c: Coincident(g5,g-10)
    c: Horizontal(g1)
    c: Coincident(g6,g1)
    c: Tangent(g6,g-4)
    c: Coincident(g3,g-6)
    c: Coincident(g7,g3)
    c: Horizontal(g7)
    c: Coincident(g7,g6)
FEATURE [Sketcher::SketchObject] Sketch123
  ArcFitTolerance = 1e-06
  AttachmentSupport = -> [Pad011]
  ExternalGeometry = -> [Binder001]
  FullyConstrained = true
  MakeInternals = false
  MapMode = 5
  Placement = pos=(0,-2,0) rot=(1,0,0;1.5708rad)
  sketch-geometry (4):
    g0: LineSegment StartX=-108 StartY=36.8 StartZ=0 EndX=-90 EndY=36.8 EndZ=0
    g1: LineSegment StartX=-108 StartY=36.8 StartZ=0 EndX=-108 EndY=26.8 EndZ=0
    g2: LineSegment StartX=-108 StartY=26.8 StartZ=0 EndX=-90 EndY=26.8 EndZ=0
    g3: ArcOfCircle CenterX=-94 CenterY=31.8 CenterZ=0 NormalX=0 NormalY=0 NormalZ=1 AngleXU=0 Radius=6.40312 StartAngle=5.38713 EndAngle=7.17924
  constraints (13):
    c: Horizontal(g0)
    c: Coincident(g1,g0)
    c: Vertical(g1)
    c: Coincident(g2,g1)
    c: Horizontal(g2)
    c: DistanceX(g0,g0) = 18
    c: DistanceY(g1,g1) = 10
    c: Equal(g0,g2)
    c: DistanceX(g0,g-3) = 90
    c: DistanceY(g0,g-3) = 2.4
    c: Coincident(g3,g0)
    c: Coincident(g3,g2)
    c: DistanceX(g3,g0) = 4
FEATURE [PartDesign::Chamfer] Chamfer014
  Angle = 45
  Base = -> Pad011 [Edge80,Edge4,Edge7]
  BaseFeature = -> Pad011
  ChamferType = 0
  FlipDirection = false
  Refine = true
  Size = 1.9
  Size2 = 1
  SupportTransform = false
  Suppressed = false
  UseAllEdges = false
FEATURE [PartDesign::Pocket] Pocket006
  BaseFeature = -> Chamfer014
  Direction = (0,-1,2e-16)
  Length = 1.2
  Length2 = 5
  Profile = -> Sketch115
  ReferenceAxis = -> Sketch115 [N_Axis]
  Refine = true
  Suppressed = false
  Type = 0
FEATURE [Sketcher::SketchObject] Sketch116  label="Sketch116 - pieno per inserto M3 x 3 x 4,5"
  ArcFitTolerance = 1e-06
  AttachmentSupport = -> [Pocket006]
  ExternalGeometry = -> [Binder001]
  FullyConstrained = true
  MakeInternals = false
  MapMode = 5
  Placement = pos=(0,1.7e-15,0) rot=(0,0.707107,0.707107;3.14159rad)
  sketch-geometry (4):
    g0: Circle CenterX=43.2 CenterY=30.3 CenterZ=0 NormalX=0 NormalY=0 NormalZ=1 AngleXU=0 Radius=3.4
    g1: Circle CenterX=43.2 CenterY=12.1 CenterZ=0 NormalX=0 NormalY=0 NormalZ=1 AngleXU=0 Radius=3.4
    g2: Circle CenterX=18.6 CenterY=30.3 CenterZ=0 NormalX=0 NormalY=0 NormalZ=1 AngleXU=0 Radius=3.4
    g3: Circle CenterX=18.6 CenterY=12.1 CenterZ=0 NormalX=0 NormalY=0 NormalZ=1 AngleXU=0 Radius=3.4
  constraints (8):
    c: Diameter(g0) = 6.8
    c: Diameter(g1) = 6.8
    c: Diameter(g2) = 6.8
    c: Diameter(g3) = 6.8
    c: Coincident(g2,g-3)
    c: Coincident(g0,g-4)
    c: Coincident(g3,g-6)
    c: Coincident(g1,g-5)
FEATURE [PartDesign::Pad] Pad012
  BaseFeature = -> Pocket006
  Direction = (0,1,-2e-16)
  Length = 2.4
  Length2 = 10
  Profile = -> Sketch116
  ReferenceAxis = -> Sketch116 [N_Axis]
  Refine = true
  Suppressed = false
  Type = 0
FEATURE [PartDesign::Pocket] Pocket007
  BaseFeature = -> Pad012
  Direction = (0,-1,2e-16)
  Length = 0.6
  Length2 = 2.4
  Profile = -> Sketch117
  ReferenceAxis = -> Sketch117 [N_Axis]
  Refine = true
  Suppressed = false
  Type = 4
FEATURE [PartDesign::Pad] Pad013
  BaseFeature = -> Pocket007
  Direction = (0,-1,2e-16)
  Length = 1.6
  Length2 = 10
  Profile = -> Sketch118
  ReferenceAxis = -> Sketch118 [N_Axis]
  Refine = true
  Suppressed = false
  Type = 0
FEATURE [Sketcher::SketchObject] Sketch119
  ArcFitTolerance = 1e-06
  AttachmentSupport = -> [Pad013]
  ExternalGeometry = -> [Binder001]
  FullyConstrained = true
  MakeInternals = false
  MapMode = 5
  Placement = pos=(0,-3.6,0) rot=(1,0,0;1.5708rad)
  sketch-geometry (21):
    g0: LineSegment [constr] StartX=-82.8 StartY=3.2 StartZ=0 EndX=-82.8 EndY=39.2 EndZ=0
    g1: ArcOfCircle CenterX=-78.51 CenterY=34.8 CenterZ=0 NormalX=0 NormalY=0 NormalZ=1 AngleXU=0 Radius=3.5 StartAngle=4.71239 EndAngle=6.28319
    g2: ArcOfCircle CenterX=-78.51 CenterY=7.6 CenterZ=0 NormalX=0 NormalY=0 NormalZ=1 AngleXU=0 Radius=3.5 StartAngle=0 EndAngle=1.5708
    g3: ArcOfCircle CenterX=-5.6 CenterY=34.8 CenterZ=0 NormalX=0 NormalY=0 NormalZ=1 AngleXU=0 Radius=3.5 StartAngle=3.14159 EndAngle=4.71239
    g4: ArcOfCircle CenterX=-5.6 CenterY=7.6 CenterZ=0 NormalX=0 NormalY=0 NormalZ=1 AngleXU=0 Radius=3.5 StartAngle=1.5708 EndAngle=3.14159
    g5: LineSegment StartX=0 StartY=39.2 StartZ=0 EndX=0 EndY=31.3 EndZ=0
    g6: LineSegment StartX=0 StartY=39.2 StartZ=0 EndX=-9.1 EndY=39.2 EndZ=0
    g7: LineSegment StartX=0 StartY=3.2 StartZ=0 EndX=0 EndY=11.1 EndZ=0
    g8: LineSegment StartX=0 StartY=3.2 StartZ=0 EndX=-9.1 EndY=3.2 EndZ=0
    g9: LineSegment StartX=-82.8 StartY=3.2 StartZ=0 EndX=-75.01 EndY=3.2 EndZ=0
    g10: LineSegment StartX=-82.8 StartY=3.2 StartZ=0 EndX=-82.8 EndY=11.1 EndZ=0
    g11: LineSegment StartX=-82.8 StartY=39.2 StartZ=0 EndX=-82.8 EndY=31.3 EndZ=0
    g12: LineSegment StartX=-82.8 StartY=39.2 StartZ=0 EndX=-75.01 EndY=39.2 EndZ=0
    g13: LineSegment StartX=-82.8 StartY=31.3 StartZ=0 EndX=-78.51 EndY=31.3 EndZ=0
    g14: LineSegment StartX=-75.01 StartY=39.2 StartZ=0 EndX=-75.01 EndY=34.8 EndZ=0
    g15: LineSegment StartX=-82.8 StartY=11.1 StartZ=0 EndX=-78.51 EndY=11.1 EndZ=0
    g16: LineSegment StartX=-75.01 StartY=3.2 StartZ=0 EndX=-75.01 EndY=7.6 EndZ=0
    g17: LineSegment StartX=-9.1 StartY=39.2 StartZ=0 EndX=-9.1 EndY=34.8 EndZ=0
    g18: LineSegment StartX=0 StartY=31.3 StartZ=0 EndX=-5.6 EndY=31.3 EndZ=0
    g19: LineSegment StartX=0 StartY=11.1 StartZ=0 EndX=-5.6 EndY=11.1 EndZ=0
    g20: LineSegment StartX=-9.1 StartY=3.2 StartZ=0 EndX=-9.1 EndY=7.6 EndZ=0
  constraints (51):
    c: Coincident(g0,g-10)
    c: PointOnObject(g0,g-8)
    c: Vertical(g0)
    c: Coincident(g1,g-3)
    c: Coincident(g2,g-4)
    c: Coincident(g3,g-5)
    c: Coincident(g4,g-6)
    c: Radius(g4) = 3.5
    c: Radius(g3) = 3.5
    c: Radius(g1) = 3.5
    c: Radius(g2) = 3.5
    c: Coincident(g5,g-9)
    c: PointOnObject(g5,g-9)
    c: Coincident(g6,g5)
    c: PointOnObject(g6,g-8)
    c: Coincident(g7,g-9)
    c: PointOnObject(g7,g-9)
    c: Coincident(g8,g7)
    c: PointOnObject(g8,g-7)
    c: Coincident(g9,g0)
    c: PointOnObject(g9,g-7)
    c: Coincident(g10,g0)
    c: PointOnObject(g10,g0)
    c: Coincident(g11,g0)
    c: PointOnObject(g11,g0)
    c: Coincident(g12,g0)
    c: PointOnObject(g12,g-8)
    c: Coincident(g13,g11)
    c: Horizontal(g13)
    c: Coincident(g14,g12)
    c: Vertical(g14)
    c: Coincident(g15,g10)
    c: Horizontal(g15)
    c: Coincident(g16,g9)
    c: Vertical(g16)
    c: Coincident(g17,g6)
    c: Vertical(g17)
    c: Coincident(g18,g5)
    c: Horizontal(g18)
    c: Coincident(g19,g7)
    c: Horizontal(g19)
    c: Coincident(g20,g8)
    c: Vertical(g20)
    c: Tangent(g20,g4) = 1.5708
    c: Tangent(g4,g19) = -1.5708
    c: Tangent(g18,g3) = 1.5708
    c: Tangent(g3,g17) = -1.5708
    c: Tangent(g13,g1) = -1.5708
    c: Tangent(g1,g14) = 1.5708
    c: Tangent(g16,g2) = -1.5708
    c: Tangent(g2,g15) = 1.5708
FEATURE [PartDesign::Pocket] Pocket008
  BaseFeature = -> Pad013
  Direction = (0,1,-2e-16)
  Length = 1.6
  Length2 = 5
  Profile = -> Sketch119
  ReferenceAxis = -> Sketch119 [N_Axis]
  Refine = true
  Suppressed = false
  Type = 0
FEATURE [PartDesign::Pad] Pad017
  BaseFeature = -> Pocket008
  Direction = (0,-1,2e-16)
  Length = 1.6
  Length2 = 10
  Profile = -> Sketch123
  ReferenceAxis = -> Sketch123 [N_Axis]
  Refine = true
  Suppressed = false
  Type = 0
FEATURE [Sketcher::SketchObject] Sketch125
  ArcFitTolerance = 1e-06
  AttachmentSupport = -> [Pad017]
  ExternalGeometry = -> [Pad017]
  FullyConstrained = true
  MakeInternals = false
  MapMode = 5
  Placement = pos=(0,-3.6,8e-16) rot=(1,0,0;1.5708rad)
  sketch-geometry (20):
    g0: LineSegment StartX=-108 StartY=35.8 StartZ=0 EndX=-108 EndY=35 EndZ=0
    g1: LineSegment StartX=-108 StartY=35 StartZ=0 EndX=-97 EndY=35 EndZ=0
    g2: LineSegment StartX=-97 StartY=35 StartZ=0 EndX=-97 EndY=35.8 EndZ=0
    g3: LineSegment StartX=-97 StartY=35.8 StartZ=0 EndX=-108 EndY=35.8 EndZ=0
    g4: LineSegment StartX=-108 StartY=28.6 StartZ=0 EndX=-108 EndY=27.8 EndZ=0
    g5: LineSegment StartX=-108 StartY=27.8 StartZ=0 EndX=-97 EndY=27.8 EndZ=0
    g6: LineSegment StartX=-97 StartY=27.8 StartZ=0 EndX=-97 EndY=28.6 EndZ=0
    g7: LineSegment StartX=-97 StartY=28.6 StartZ=0 EndX=-108 EndY=28.6 EndZ=0
    g8: LineSegment StartX=-108 StartY=30.4 StartZ=0 EndX=-108 EndY=29.6 EndZ=0
    g9: LineSegment StartX=-108 StartY=29.6 StartZ=0 EndX=-97 EndY=29.6 EndZ=0
    g10: LineSegment StartX=-97 StartY=29.6 StartZ=0 EndX=-97 EndY=30.4 EndZ=0
    g11: LineSegment StartX=-97 StartY=30.4 StartZ=0 EndX=-108 EndY=30.4 EndZ=0
    g12: LineSegment StartX=-108 StartY=32.2 StartZ=0 EndX=-108 EndY=31.4 EndZ=0
    g13: LineSegment StartX=-108 StartY=31.4 StartZ=0 EndX=-97 EndY=31.4 EndZ=0
    g14: LineSegment StartX=-97 StartY=31.4 StartZ=0 EndX=-97 EndY=32.2 EndZ=0
    g15: LineSegment StartX=-97 StartY=32.2 StartZ=0 EndX=-108 EndY=32.2 EndZ=0
    g16: LineSegment StartX=-108 StartY=34 StartZ=0 EndX=-108 EndY=33.2 EndZ=0
    g17: LineSegment StartX=-108 StartY=33.2 StartZ=0 EndX=-97 EndY=33.2 EndZ=0
    g18: LineSegment StartX=-97 StartY=33.2 StartZ=0 EndX=-97 EndY=34 EndZ=0
    g19: LineSegment StartX=-97 StartY=34 StartZ=0 EndX=-108 EndY=34 EndZ=0
  constraints (55):
    c: Coincident(g1,g0)
    c: Horizontal(g1)
    c: Coincident(g2,g1)
    c: Vertical(g2)
    c: Coincident(g3,g2)
    c: Horizontal(g3)
    c: Coincident(g3,g0)
    c: DistanceX(g1,g1) = 11
    c: DistanceY(g2,g2) = 0.8
    c: Coincident(g5,g4)
    c: Horizontal(g5)
    c: Coincident(g6,g5)
    c: Vertical(g6)
    c: Coincident(g7,g6)
    c: Horizontal(g7)
    c: Coincident(g7,g4)
    c: Coincident(g9,g8)
    c: Horizontal(g9)
    c: Coincident(g10,g9)
    c: Vertical(g10)
    c: Coincident(g11,g10)
    c: Horizontal(g11)
    c: Coincident(g11,g8)
    c: Coincident(g13,g12)
    c: Horizontal(g13)
    c: Coincident(g14,g13)
    c: Vertical(g14)
    c: Coincident(g15,g14)
    c: Horizontal(g15)
    c: Coincident(g15,g12)
    c: Coincident(g17,g16)
    c: Horizontal(g17)
    c: Coincident(g18,g17)
    c: Vertical(g18)
    c: Coincident(g19,g18)
    c: Horizontal(g19)
    c: Coincident(g19,g16)
    c: Equal(g3,g19)
    c: Equal(g3,g15)
    c: Equal(g3,g11)
    c: Equal(g3,g7)
    c: Equal(g2,g18)
    c: Equal(g2,g14)
    c: Equal(g2,g10)
    c: Equal(g2,g6)
    c: DistanceY(g-4,g4) = 1
    c: DistanceY(g4,g8) = 1
    c: DistanceY(g8,g12) = 1
    c: DistanceY(g12,g16) = 1
    c: DistanceY(g16,g0) = 1
    c: Tangent(g0,g-5)
    c: Tangent(g16,g-5)
    c: Tangent(g12,g-5)
    c: Tangent(g8,g-5)
    c: Tangent(g4,g-5)
FEATURE [PartDesign::Chamfer] Chamfer009
  Angle = 45
  Base = -> Pad017 [Edge151,Edge154]
  BaseFeature = -> Pad017
  ChamferType = 1
  FlipDirection = false
  Refine = true
  Size = 1.5
  Size2 = 2.8
  SupportTransform = false
  Suppressed = false
  UseAllEdges = false
FEATURE [PartDesign::Pocket] Pocket009
  BaseFeature = -> Chamfer009
  Direction = (0,1,-2e-16)
  Length = 1
  Length2 = 5
  Profile = -> Sketch125
  ReferenceAxis = -> Sketch125 [N_Axis]
  Refine = true
  Suppressed = false
  Type = 0
FEATURE [PartDesign::Pad] Pad014
  BaseFeature = -> Pocket009
  Direction = (0,-1,2e-16)
  Length = 0.8
  Length2 = 10
  Profile = -> Sketch120
  ReferenceAxis = -> Sketch120 [N_Axis]
  Refine = true
  Suppressed = false
  Type = 0
FEATURE [Sketcher::SketchObject] Sketch124
  ArcFitTolerance = 1e-06
  AttachmentSupport = -> [Pad014]
  ExternalGeometry = -> [Binder001]
  FullyConstrained = true
  MakeInternals = false
  MapMode = 5
  Placement = pos=(0,-2.8,6e-16) rot=(1,0,0;1.5708rad)
  sketch-geometry (4):
    g0: LineSegment StartX=-129 StartY=39.2 StartZ=0 EndX=-131.599 EndY=31.2 EndZ=0
    g1: LineSegment StartX=-118 StartY=39.2 StartZ=0 EndX=-120.599 EndY=31.2 EndZ=0
    g2: LineSegment StartX=-129 StartY=39.2 StartZ=0 EndX=-118 EndY=39.2 EndZ=0
    g3: LineSegment StartX=-120.599 StartY=31.2 StartZ=0 EndX=-131.599 EndY=31.2 EndZ=0
  constraints (12):
    c: PointOnObject(g0,g-3)
    c: PointOnObject(g1,g-3)
    c: Parallel(g-4,g0)
    c: Parallel(g-4,g1)
    c: Coincident(g2,g0)
    c: Coincident(g2,g1)
    c: DistanceX(g2,g2) = 11
    c: DistanceY(g1,g1) = 8
    c: Coincident(g3,g1)
    c: Horizontal(g3)
    c: Coincident(g3,g0)
    c: DistanceX(g1,g-3) = 118
FEATURE [PartDesign::Pad] Pad018
  BaseFeature = -> Pad014
  Direction = (0,-1,2e-16)
  Length = 1.2
  Length2 = 10
  Profile = -> Sketch124
  ReferenceAxis = -> Sketch124 [N_Axis]
  Refine = true
  Suppressed = false
  Type = 0
FEATURE [Sketcher::SketchObject] Sketch126
  ArcFitTolerance = 1e-06
  AttachmentSupport = -> [Pad018]
  ExternalGeometry = -> [Pad018]
  FullyConstrained = true
  MakeInternals = false
  MapMode = 5
  Placement = pos=(0,-4,0) rot=(1,0,0;1.5708rad)
  sketch-geometry (8):
    g0: LineSegment StartX=-129.877 StartY=36.5 StartZ=0 EndX=-130.137 EndY=35.7 EndZ=0
    g1: LineSegment StartX=-130.69 StartY=34 StartZ=0 EndX=-130.95 EndY=33.2 EndZ=0
    g2: LineSegment StartX=-129.877 StartY=36.5 StartZ=0 EndX=-118.877 EndY=36.5 EndZ=0
    g3: LineSegment StartX=-130.137 StartY=35.7 StartZ=0 EndX=-119.137 EndY=35.7 EndZ=0
    g4: LineSegment StartX=-130.69 StartY=34 StartZ=0 EndX=-119.69 EndY=34 EndZ=0
    g5: LineSegment StartX=-130.95 StartY=33.2 StartZ=0 EndX=-119.95 EndY=33.2 EndZ=0
    g6: LineSegment StartX=-118.877 StartY=36.5 StartZ=0 EndX=-119.137 EndY=35.7 EndZ=0
    g7: LineSegment StartX=-119.69 StartY=34 StartZ=0 EndX=-119.95 EndY=33.2 EndZ=0
  constraints (20):
    c: Coincident(g2,g0)
    c: Horizontal(g2)
    c: Coincident(g3,g0)
    c: Horizontal(g3)
    c: Coincident(g4,g1)
    c: Horizontal(g4)
    c: Coincident(g5,g1)
    c: Horizontal(g5)
    c: Coincident(g6,g2)
    c: Coincident(g6,g3)
    c: Coincident(g7,g4)
    c: Coincident(g7,g5)
    c: Tangent(g0,g-4)
    c: Tangent(g6,g-5)
    c: Tangent(g1,g-4)
    c: Tangent(g7,g-5)
    c: DistanceY(g3,g2) = 0.8
    c: DistanceY(g5,g4) = 0.8
    c: DistanceY(g-6,g1) = 2
    c: DistanceY(g-6,g0) = 4.5
FEATURE [PartDesign::Chamfer] Chamfer008
  Angle = 45
  Base = -> Pad018 [Edge257]
  BaseFeature = -> Pad018
  ChamferType = 1
  FlipDirection = false
  Refine = true
  Size = 1
  Size2 = 6
  SupportTransform = false
  Suppressed = false
  UseAllEdges = false
FEATURE [PartDesign::Pocket] Pocket010
  BaseFeature = -> Chamfer008
  Direction = (0,1,-2e-16)
  Length = 1
  Length2 = 5
  Profile = -> Sketch126
  ReferenceAxis = -> Sketch126 [N_Axis]
  Refine = true
  Suppressed = false
  Type = 0
FEATURE [PartDesign::Pad] Pad015
  BaseFeature = -> Pocket010
  Direction = (0,-1,2e-16)
  Length = 2
  Length2 = 10
  Profile = -> Sketch121
  ReferenceAxis = -> Sketch121 [N_Axis]
  Refine = true
  Suppressed = false
  Type = 0
FEATURE [PartDesign::Pad] Pad016
  BaseFeature = -> Pad015
  Direction = (0,-1,2e-16)
  Length = 1.6
  Length2 = 10
  Profile = -> Sketch122
  ReferenceAxis = -> Sketch122 [N_Axis]
  Refine = true
  Suppressed = false
  Type = 0
FEATURE [Sketcher::SketchObject] Sketch129
  ArcFitTolerance = 1e-06
  AttachmentSupport = -> [Pad016]
  ExternalGeometry = -> [Binder001]
  FullyConstrained = true
  MakeInternals = false
  MapMode = 5
  Placement = pos=(0,-3.6,0) rot=(1,0,0;1.5708rad)
  sketch-geometry (12):
    g0: LineSegment [constr] StartX=-192.176 StartY=-3.18451 StartZ=0 EndX=-181.223 EndY=20.303 EndZ=0
    g1: LineSegment [constr] StartX=-202.765 StartY=20.303 StartZ=0 EndX=-181.223 EndY=20.303 EndZ=0
    g2: LineSegment StartX=-202.765 StartY=20.303 StartZ=0 EndX=-181.223 EndY=20.303 EndZ=0
    g3: LineSegment StartX=-192.176 StartY=-3.18451 StartZ=0 EndX=-196.804 EndY=-13.1107 EndZ=0
    g4: ArcOfCircle CenterX=-207.583 CenterY=4 CenterZ=0 NormalX=0 NormalY=0 NormalZ=1 AngleXU=0 Radius=17 StartAngle=5.84685 EndAngle=7.56663
    g5: ArcOfEllipse CenterX=-181.223 CenterY=8.55923 CenterZ=0 NormalX=0 NormalY=0 NormalZ=1 MajorRadius=23.4779 MinorRadius=11.7437 AngleXU=2e-16 StartAngle=4.71239 EndAngle=7.85398
    g6: LineSegment [constr] StartX=-157.745 StartY=8.55923 StartZ=0 EndX=-204.701 EndY=8.55923 EndZ=0
    g7: LineSegment [constr] StartX=-181.223 StartY=20.303 StartZ=0 EndX=-181.223 EndY=-3.18451 EndZ=0
    g8: GeomPoint [constr] X=-160.894 Y=8.55923 Z=0
    g9: GeomPoint [constr] X=-201.553 Y=8.55923 Z=0
    g10: ArcOfCircle CenterX=-181.223 CenterY=-20.3763 CenterZ=0 NormalX=0 NormalY=0 NormalZ=1 AngleXU=0 Radius=17.1918 StartAngle=1.57079 EndAngle=2.70526
    g11: GeomPoint [constr] X=-181.223 Y=-3.18451 Z=0
  constraints (23):
    c: Coincident(g0,g-5)
    c: Coincident(g1,g-6)
    c: Horizontal(g1)
    c: Coincident(g1,g0)
    c: Parallel(g0,g-4)
    c: Coincident(g2,g1)
    c: Coincident(g2,g0)
    c: Coincident(g3,g0)
    c: Equal(g4,g-5)
    c: Coincident(g4,g1)
    c: Coincident(g4,g0)
    c: InternalAlignment(g6-g9 -> g5) x4
    c: Vertical(g5,g0)
    c: Horizontal(g6)
    c: Coincident(g5,g0)
    c: DistanceX(g6,g-3) = 10.1
    c: Tangent(g10,g3) = -1.5708
    c: PointOnObject(g11,g10)
    c: Tangent(g5,g10,g11) = 1.5708
    c: Coincident(g10,g5)
    c: Coincident(g11,g7)
    c: Parallel(g3,g-4)
    c: Horizontal(g5,g0)
FEATURE [Sketcher::SketchObject] Sketch130
  ArcFitTolerance = 1e-06
  AttachmentOffset = pos=(0,0,-1.6) rot=(0,0,1;0rad)
  AttachmentSupport = -> [Pad016]
  ExternalGeometry = -> [Binder001]
  FullyConstrained = true
  MakeInternals = false
  MapMode = 5
  Placement = pos=(0,-2,-4e-16) rot=(1,0,0;1.5708rad)
  sketch-geometry (12):
    g0: LineSegment [constr] StartX=-192.176 StartY=-3.18451 StartZ=0 EndX=-181.223 EndY=20.303 EndZ=0
    g1: LineSegment [constr] StartX=-202.765 StartY=20.303 StartZ=0 EndX=-181.223 EndY=20.303 EndZ=0
    g2: LineSegment StartX=-202.765 StartY=20.303 StartZ=0 EndX=-181.223 EndY=20.303 EndZ=0
    g3: LineSegment StartX=-192.176 StartY=-3.18451 StartZ=0 EndX=-193.827 EndY=-6.72678 EndZ=0
    g4: ArcOfCircle CenterX=-207.583 CenterY=4 CenterZ=0 NormalX=0 NormalY=0 NormalZ=1 AngleXU=0 Radius=17 StartAngle=5.84685 EndAngle=7.56663
    g5: ArcOfEllipse CenterX=-181.223 CenterY=10.803 CenterZ=0 NormalX=0 NormalY=0 NormalZ=1 MajorRadius=14.4779 MinorRadius=9.5 AngleXU=0 StartAngle=4.71239 EndAngle=7.85398
    g6: LineSegment [constr] StartX=-166.745 StartY=10.803 StartZ=0 EndX=-195.701 EndY=10.803 EndZ=0
    g7: LineSegment [constr] StartX=-181.223 StartY=20.303 StartZ=0 EndX=-181.223 EndY=1.30297 EndZ=0
    g8: GeomPoint [constr] X=-170.298 Y=10.803 Z=0
    g9: GeomPoint [constr] X=-192.148 Y=10.803 Z=0
    g10: ArcOfCircle CenterX=-181.223 CenterY=-12.6042 CenterZ=0 NormalX=0 NormalY=0 NormalZ=1 AngleXU=0 Radius=13.9072 StartAngle=1.5708 EndAngle=2.70526
    g11: GeomPoint [constr] X=-181.223 Y=1.30297 Z=0
  constraints (23):
    c: Coincident(g0,g-5)
    c: Coincident(g1,g-6)
    c: Horizontal(g1)
    c: Coincident(g1,g0)
    c: Parallel(g0,g-4)
    c: Coincident(g2,g1)
    c: Coincident(g2,g0)
    c: Coincident(g3,g0)
    c: Equal(g4,g-5)
    c: Coincident(g4,g1)
    c: Coincident(g4,g0)
    c: InternalAlignment(g6-g9 -> g5) x4
    c: Vertical(g5,g0)
    c: Horizontal(g6)
    c: Coincident(g5,g0)
    c: DistanceX(g6,g-3) = 19.1
    c: Tangent(g10,g3) = -1.5708
    c: PointOnObject(g11,g10)
    c: Tangent(g5,g10,g11) = 1.5708
    c: Coincident(g10,g5)
    c: Coincident(g11,g7)
    c: Parallel(g3,g-4)
    c: DistanceY(g5,g0) = 19
FEATURE [Part::Part2DObjectPython] Clone2D001  label="Sketch130 (2D)"  # Draft 2D object (typed FeaturePython)
  Fuse = false
  Objects = -> [Sketch130]
  Placement = pos=(0,-2,-4e-16) rot=(1,0,0;1.5708rad)
  Scale = (1,1,1)
FEATURE [Sketcher::SketchObject] Sketch131
  ArcFitTolerance = 1e-06
  AttachmentOffset = pos=(0,0,-3.5) rot=(0,0,1;0rad)
  AttachmentSupport = -> [Pad016]
  ExternalGeometry = -> [Binder001]
  FullyConstrained = true
  MakeInternals = false
  MapMode = 5
  Placement = pos=(0,-0.1,-8e-16) rot=(1,0,0;1.5708rad)
  sketch-geometry (1):
    g0: GeomPoint X=-197.47 Y=8.55923 Z=0
  constraints (1):
    c: Symmetric(g-6,g-4,g0)
FEATURE [Sketcher::SketchObject] Sketch132
  ArcFitTolerance = 1e-06
  AttachmentSupport = -> [Pad016]
  ExternalGeometry = -> [Binder001]
  FullyConstrained = true
  MakeInternals = false
  MapMode = 5
  Placement = pos=(0,-3.6,0) rot=(1,0,0;1.5708rad)
  sketch-geometry (3):
    g0: LineSegment [constr] StartX=-215.42 StartY=-53.0314 StartZ=0 EndX=-167.782 EndY=-53.0314 EndZ=0
    g1: Circle CenterX=-191.282 CenterY=-53.0314 CenterZ=0 NormalX=0 NormalY=0 NormalZ=1 AngleXU=0 Radius=11.5
    g2: Circle CenterX=-191.282 CenterY=-53.0314 CenterZ=0 NormalX=0 NormalY=0 NormalZ=1 AngleXU=0 Radius=10.7
  constraints (8):
    c: Coincident(g0,g-3)
    c: PointOnObject(g0,g-4)
    c: Horizontal(g0)
    c: Diameter(g1) = 23
    c: PointOnObject(g1,g0)
    c: DistanceX(g1,g0) = 23.5
    c: Diameter(g2) = 21.4
    c: Coincident(g2,g1)
FEATURE [Part::Part2DObjectPython] ShapeString  # Draft 2D object (typed FeaturePython)
  FontFile = <path>
  Fuse = false
  Justification = 6
  JustificationReference = 0
  KeepLeftMargin = false
  MakeFace = true
  ObliqueAngle = 0
  Placement = pos=(-199,-3.6,-57.5) rot=(1,0,0;1.5708rad)
  ScaleToSize = true
  Size = 10
  String = AS
  Tracking = 0
FEATURE [Sketcher::SketchObject] Sketch133
  ArcFitTolerance = 1e-06
  AttachmentSupport = -> [Binder]
  ExternalGeometry = -> [Binder]
  FullyConstrained = true
  MakeInternals = false
  MapMode = 5
  Placement = pos=(0,9e-16,0) rot=(0,0.707107,0.707107;3.14159rad)
  sketch-geometry (30):
    g0: LineSegment StartX=0 StartY=39.2 StartZ=0 EndX=0 EndY=3.2 EndZ=0
    g1: LineSegment StartX=0 StartY=3.2 StartZ=0 EndX=82.8 EndY=3.2 EndZ=0
    g2: LineSegment StartX=82.8 StartY=3.2 StartZ=0 EndX=82.8 EndY=6.2 EndZ=0
    g3: LineSegment StartX=82.8 StartY=6.2 StartZ=0 EndX=91.752 EndY=6.2 EndZ=0
    g4: LineSegment StartX=0 StartY=39.2 StartZ=0 EndX=195.887 EndY=39.2 EndZ=0
    g5: LineSegment StartX=195.887 StartY=39.2 StartZ=0 EndX=202.765 EndY=20.303 EndZ=0
    g6: LineSegment StartX=192.333 StartY=24.9893 StartZ=0 EndX=196.467 EndY=26.4942 EndZ=0
    g7: LineSegment StartX=196.467 StartY=26.4942 StartZ=0 EndX=194.073 EndY=33.0721 EndZ=0
    g8: LineSegment StartX=194.073 StartY=33.0721 StartZ=0 EndX=189.939 EndY=31.5672 EndZ=0
    g9: LineSegment StartX=189.939 StartY=31.5672 StartZ=0 EndX=192.333 EndY=24.9893 EndZ=0
    g10: ArcOfCircle CenterX=107.6 CenterY=4 CenterZ=0 NormalX=0 NormalY=0 NormalZ=1 AngleXU=0 Radius=16 StartAngle=1.5708 EndAngle=3.00366
    g11: LineSegment StartX=107.6 StartY=20 StartZ=0 EndX=132.428 EndY=20 EndZ=0
    g12: ArcOfCircle [constr] CenterX=132.428 CenterY=4 CenterZ=0 NormalX=0 NormalY=0 NormalZ=1 AngleXU=0 Radius=16 StartAngle=0.314159 EndAngle=1.5708
    g13: LineSegment StartX=147.645 StartY=8.94427 StartZ=0 EndX=176.685 EndY=-80.4316 EndZ=0
    g14: LineSegment StartX=176.685 StartY=-80.4316 StartZ=0 EndX=215.932 EndY=-80.4316 EndZ=0
    g15: ArcOfCircle CenterX=207.583 CenterY=4 CenterZ=0 NormalX=0 NormalY=0 NormalZ=1 AngleXU=0 Radius=17 StartAngle=1.85815 EndAngle=3.57792
    g16: ArcOfCircle CenterX=184.801 CenterY=-67.3089 CenterZ=0 NormalX=0 NormalY=0 NormalZ=1 AngleXU=0 Radius=33.7833 StartAngle=5.88425 EndAngle=6.71952
    g17: LineSegment StartX=192.176 StartY=-3.18451 StartZ=0 EndX=215.42 EndY=-53.0314 EndZ=0
    g18: Circle CenterX=5.6 CenterY=34.8 CenterZ=0 NormalX=0 NormalY=0 NormalZ=1 AngleXU=0 Radius=1.8
    g19: Circle CenterX=5.6 CenterY=7.6 CenterZ=0 NormalX=0 NormalY=0 NormalZ=1 AngleXU=0 Radius=1.8
    g20: Circle CenterX=78.51 CenterY=34.8 CenterZ=0 NormalX=0 NormalY=0 NormalZ=1 AngleXU=0 Radius=1.8
    g21: Circle CenterX=78.51 CenterY=7.6 CenterZ=0 NormalX=0 NormalY=0 NormalZ=1 AngleXU=0 Radius=1.8
    g22: Circle CenterX=184.08 CenterY=34.8 CenterZ=0 NormalX=0 NormalY=0 NormalZ=1 AngleXU=0 Radius=1.8
    g23: Circle CenterX=179.305 CenterY=-76.8316 CenterZ=0 NormalX=0 NormalY=0 NormalZ=1 AngleXU=0 Radius=1.8
    g24: Circle CenterX=213.443 CenterY=-76.8316 CenterZ=0 NormalX=0 NormalY=0 NormalZ=1 AngleXU=0 Radius=1.8
    g25: Circle CenterX=19 CenterY=21.2 CenterZ=0 NormalX=0 NormalY=0 NormalZ=1 AngleXU=0 Radius=6.3
    g26: Circle CenterX=42 CenterY=21.2 CenterZ=0 NormalX=0 NormalY=0 NormalZ=1 AngleXU=0 Radius=6.3
    g27: Circle CenterX=65 CenterY=21.2 CenterZ=0 NormalX=0 NormalY=0 NormalZ=1 AngleXU=0 Radius=6.3
    g28: LineSegment StartX=132.428 StartY=20 StartZ=0 EndX=144.053 EndY=20 EndZ=0
    g29: LineSegment StartX=147.645 StartY=8.94427 StartZ=0 EndX=144.053 EndY=20 EndZ=0
  constraints (65):
    c: Coincident(g0,g-4)
    c: Coincident(g0,g-5)
    c: Coincident(g1,g0)
    c: Coincident(g1,g-6)
    c: Coincident(g2,g1)
    c: Coincident(g2,g-7)
    c: Coincident(g3,g2)
    c: Coincident(g3,g-8)
    c: Coincident(g4,g0)
    c: Coincident(g4,g-16)
    c: Coincident(g5,g4)
    c: Coincident(g5,g-16)
    c: Coincident(g6,g-20)
    c: Coincident(g6,g-21)
    c: Coincident(g7,g6)
    c: Coincident(g7,g-23)
    c: Coincident(g8,g7)
    c: Coincident(g8,g-22)
    c: Coincident(g9,g8)
    c: Coincident(g9,g6)
    c: Equal(g10,g-8)
    c: Coincident(g10,g3)
    c: Coincident(g10,g-9)
    c: Coincident(g11,g10)
    c: Coincident(g11,g-10)
    c: Equal(g12,g-10)
    c: Coincident(g12,g11)
    c: Coincident(g12,g-11)
    c: Coincident(g13,g12)
    c: Coincident(g13,g-12)
    c: Coincident(g14,g13)
    c: Coincident(g14,g-13)
    c: Equal(g15,g-15)
    c: Coincident(g15,g5)
    c: Coincident(g15,g-15)
    c: Equal(g16,g-13)
    c: Coincident(g16,g14)
    c: Coincident(g16,g-14)
    c: Coincident(g17,g15)
    c: Coincident(g17,g16)
    c: Equal(g18,g-28)
    c: Equal(g19,g-29)
    c: Equal(g20,g-26)
    c: Equal(g21,g-27)
    c: Equal(g22,g-17)
    c: Equal(g24,g-25)
    c: Equal(g23,g-24)
    c: Coincident(g23,g-24)
    c: Coincident(g24,g-25)
    c: Coincident(g22,g-17)
    c: Coincident(g20,g-26)
    c: Coincident(g21,g-27)
    c: Coincident(g18,g-28)
    c: Coincident(g19,g-29)
    c: Equal(g25,g-30)
    c: Equal(g26,g-31)
    c: Equal(g27,g-32)
    c: Coincident(g25,g-30)
    c: Coincident(g26,g-31)
    c: Coincident(g27,g-32)
    c: Parallel(g28,g11)
    c: Parallel(g29,g13)
    c: Coincident(g28,g11)
    c: Coincident(g29,g12)
    c: Coincident(g29,g28)
FEATURE [PartDesign::Pad] Pad019
  Direction = (0,1,-2e-16)
  Length = 2
  Length2 = 10
  Profile = -> Sketch133
  ReferenceAxis = -> Sketch133 [N_Axis]
  Refine = true
  Suppressed = false
  Type = 0
FEATURE [Sketcher::SketchObject] Sketch091  label="Sketch091 - forma anteriore"
  ArcFitTolerance = 1e-06
  AttachmentSupport = -> [Pad019]
  ExternalGeometry = -> [Binder]
  FullyConstrained = true
  MakeInternals = false
  MapMode = 5
  Placement = pos=(0,2,0) rot=(0,0.707107,0.707107;3.14159rad)
  sketch-geometry (12):
    g0: Circle CenterX=5.6 CenterY=34.8 CenterZ=0 NormalX=0 NormalY=0 NormalZ=1 AngleXU=0 Radius=1.8
    g1: Circle CenterX=5.6 CenterY=7.6 CenterZ=0 NormalX=0 NormalY=0 NormalZ=1 AngleXU=0 Radius=1.8
    g2: Circle CenterX=78.51 CenterY=34.8 CenterZ=0 NormalX=0 NormalY=0 NormalZ=1 AngleXU=0 Radius=1.8
    g3: Circle CenterX=78.51 CenterY=7.6 CenterZ=0 NormalX=0 NormalY=0 NormalZ=1 AngleXU=0 Radius=1.8
    g4: LineSegment StartX=0 StartY=39.2 StartZ=0 EndX=0 EndY=3.2 EndZ=0
    g5: LineSegment StartX=0 StartY=3.2 StartZ=0 EndX=82.8 EndY=3.2 EndZ=0
    g6: LineSegment StartX=82.8 StartY=3.2 StartZ=0 EndX=82.8 EndY=39.2 EndZ=0
    g7: LineSegment StartX=82.8 StartY=39.2 StartZ=0 EndX=0 EndY=39.2 EndZ=0
    g8: ArcOfCircle CenterX=19 CenterY=21.2 CenterZ=0 NormalX=0 NormalY=0 NormalZ=1 AngleXU=0 Radius=10 StartAngle=1.5708 EndAngle=4.71239
    g9: ArcOfCircle CenterX=65 CenterY=21.2 CenterZ=0 NormalX=0 NormalY=0 NormalZ=1 AngleXU=0 Radius=10 StartAngle=4.71239 EndAngle=7.85398
    g10: LineSegment StartX=19 StartY=31.2 StartZ=0 EndX=65 EndY=31.2 EndZ=0
    g11: LineSegment StartX=19 StartY=11.2 StartZ=0 EndX=65 EndY=11.2 EndZ=0
  constraints (25):
    c: Equal(g2,g-7)
    c: Equal(g3,g-8)
    c: Equal(g1,g-13)
    c: Equal(g0,g-12)
    c: Coincident(g0,g-12)
    c: Coincident(g1,g-13)
    c: Coincident(g3,g-8)
    c: Coincident(g2,g-7)
    c: Coincident(g4,g-4)
    c: Coincident(g4,g-5)
    c: Coincident(g5,g4)
    c: Coincident(g5,g-6)
    c: Coincident(g6,g5)
    c: PointOnObject(g6,g-3)
    c: Vertical(g6)
    c: Coincident(g7,g6)
    c: Coincident(g7,g4)
    c: Tangent(g8,g10) = 1.5708
    c: Tangent(g8,g11) = -1.5708
    c: Tangent(g9,g10) = 1.5708
    c: Tangent(g9,g11) = -1.5708
    c: Equal(g8,g9)
    c: Radius(g8) = 10
    c: Coincident(g8,g-11)
    c: Coincident(g9,g-9)
FEATURE [Sketcher::SketchObject] Sketch093  label="Sketch093 - scavi interni pulsanti"
  ArcFitTolerance = 1e-06
  AttachmentSupport = -> [Pad019]
  ExternalGeometry = -> [Binder]
  FullyConstrained = true
  MakeInternals = false
  MapMode = 5
  Placement = pos=(0,1.8e-15,0) rot=(1,0,0;1.5708rad)
  sketch-geometry (3):
    g0: Circle CenterX=-65 CenterY=21.2 CenterZ=0 NormalX=0 NormalY=0 NormalZ=1 AngleXU=0 Radius=7.3
    g1: Circle CenterX=-42 CenterY=21.2 CenterZ=0 NormalX=0 NormalY=0 NormalZ=1 AngleXU=0 Radius=7.3
    g2: Circle CenterX=-19 CenterY=21.2 CenterZ=0 NormalX=0 NormalY=0 NormalZ=1 AngleXU=0 Radius=7.3
  constraints (6):
    c: Coincident(g0,g-3)
    c: Coincident(g1,g-4)
    c: Coincident(g2,g-5)
    c: Diameter(g0) = 14.6
    c: Diameter(g1) = 14.6
    c: Diameter(g2) = 14.6
FEATURE [Sketcher::SketchObject] Sketch094  label="Sketch094 - forma centrale"
  ArcFitTolerance = 1e-06
  AttachmentSupport = -> [Pad019]
  ExternalGeometry = -> [Binder]
  FullyConstrained = true
  MakeInternals = false
  MapMode = 5
  Placement = pos=(0,2,0) rot=(0,0.707107,0.707107;3.14159rad)
  sketch-geometry (4):
    g0: LineSegment StartX=137.815 StartY=39.2 StartZ=0 EndX=142.655 EndY=24.303 EndZ=0
    g1: LineSegment StartX=110.815 StartY=24.303 StartZ=0 EndX=142.655 EndY=24.303 EndZ=0
    g2: LineSegment StartX=137.815 StartY=39.2 StartZ=0 EndX=110.815 EndY=39.2 EndZ=0
    g3: ArcOfCircle CenterX=92.2534 CenterY=31.7515 CenterZ=0 NormalX=0 NormalY=0 NormalZ=1 AngleXU=0 Radius=20 StartAngle=5.90156 EndAngle=6.66481
  constraints (12):
    c: PointOnObject(g0,g-3)
    c: Tangent(g0,g-5)
    c: Horizontal(g1)
    c: Coincident(g1,g0)
    c: Coincident(g2,g0)
    c: PointOnObject(g2,g-3)
    c: DistanceX(g2,g2) = 27
    c: Vertical(g1,g2)
    c: Coincident(g3,g2)
    c: Radius(g3) = 20
    c: Coincident(g3,g1)
    c: DistanceY(g-6,g0) = 4
FEATURE [Sketcher::SketchObject] Sketch095  label="Sketch095 - forma posteriore"
  ArcFitTolerance = 1e-06
  AttachmentSupport = -> [Pad019]
  ExternalGeometry = -> [Binder]
  FullyConstrained = true
  MakeInternals = false
  MapMode = 5
  Placement = pos=(0,2,0) rot=(0,0.707107,0.707107;3.14159rad)
  sketch-geometry (15):
    g0: LineSegment StartX=137.815 StartY=39.2 StartZ=0 EndX=143.955 EndY=20.303 EndZ=0
    g1: LineSegment StartX=143.955 StartY=20.303 StartZ=0 EndX=190.141 EndY=20.303 EndZ=0
    g2: ArcOfCircle CenterX=184.08 CenterY=34.8 CenterZ=0 NormalX=0 NormalY=0 NormalZ=1 AngleXU=0 Radius=3.5 StartAngle=3.49066 EndAngle=4.71239
    g3: LineSegment StartX=180.791 StartY=33.6029 StartZ=0 EndX=178.754 EndY=39.2 EndZ=0
    g4: LineSegment StartX=184.08 StartY=31.3 StartZ=0 EndX=186.139 EndY=31.3 EndZ=0
    g5: LineSegment StartX=190.141 StartY=20.303 StartZ=0 EndX=186.139 EndY=31.3 EndZ=0
    g6: LineSegment StartX=137.815 StartY=39.2 StartZ=0 EndX=156.815 EndY=39.2 EndZ=0
    g7: LineSegment StartX=178.754 StartY=39.2 StartZ=0 EndX=168.815 EndY=39.2 EndZ=0
    g8: LineSegment StartX=156.815 StartY=31.2 StartZ=0 EndX=168.815 EndY=31.2 EndZ=0
    g9: ArcOfCircle CenterX=176.411 CenterY=35.2 CenterZ=0 NormalX=0 NormalY=0 NormalZ=1 AngleXU=0 Radius=20 StartAngle=2.94023 EndAngle=3.34295
    g10: ArcOfCircle CenterX=188.411 CenterY=35.2 CenterZ=0 NormalX=0 NormalY=0 NormalZ=1 AngleXU=0 Radius=20 StartAngle=2.94023 EndAngle=3.34295
    g11: LineSegment StartX=157.815 StartY=39.2 StartZ=0 EndX=167.815 EndY=39.2 EndZ=0
    g12: LineSegment StartX=157.436 StartY=36.2 StartZ=0 EndX=167.436 EndY=36.2 EndZ=0
    g13: ArcOfCircle CenterX=177.411 CenterY=35.2 CenterZ=0 NormalX=0 NormalY=0 NormalZ=1 AngleXU=0 Radius=20 StartAngle=2.94023 EndAngle=3.09157
    g14: ArcOfCircle CenterX=187.411 CenterY=35.2 CenterZ=0 NormalX=0 NormalY=0 NormalZ=1 AngleXU=0 Radius=20 StartAngle=2.94023 EndAngle=3.09157
  constraints (46):
    c: PointOnObject(g0,g-3)
    c: Tangent(g0,g-6)
    c: Coincident(g1,g0)
    c: Horizontal(g1)
    c: Radius(g2) = 3.5
    c: Coincident(g2,g-5)
    c: PointOnObject(g3,g-3)
    c: Parallel(g3,g-4)
    c: Tangent(g3,g2) = 1.5708
    c: Horizontal(g4)
    c: Tangent(g4,g2) = -1.5708
    c: Coincident(g5,g1)
    c: Parallel(g5,g-4)
    c: Coincident(g5,g4)
    c: DistanceX(g4,g-8) = 3.8
    c: Coincident(g6,g0)
    c: PointOnObject(g6,g-3)
    c: Coincident(g7,g3)
    c: PointOnObject(g7,g-3)
    c: Horizontal(g8)
    c: DistanceX(g6,g7) = 12
    c: Vertical(g8,g6)
    c: Vertical(g7,g8)
    c: DistanceY(g8,g6) = 8
    c: Coincident(g9,g8)
    c: Coincident(g9,g6)
    c: Coincident(g10,g7)
    c: Coincident(g10,g8)
    c: Radius(g9) = 20
    c: Radius(g10) = 20
    c: PointOnObject(g11,g-3)
    c: PointOnObject(g11,g-3)
    c: DistanceX(g11,g11) = 10
    c: DistanceX(g6,g11) = 1
    c: Horizontal(g12)
    c: Equal(g12,g11)
    c: DistanceY(g12,g11) = 3
    c: Coincident(g13,g11)
    c: Coincident(g13,g12)
    c: Radius(g13) = 20
    c: Coincident(g14,g11)
    c: Coincident(g14,g12)
    c: Radius(g14) = 20
    c: DistanceX(g0,g6) = 19
    c: Horizontal(g9,g13)
    c: Horizontal(g0,g-4)
FEATURE [Sketcher::SketchObject] Sketch096  label="Sketch096 - forma impugnatura"
  ArcFitTolerance = 1e-06
  AttachmentSupport = -> [Pad019]
  ExternalGeometry = -> [Binder]
  FullyConstrained = true
  MakeInternals = false
  MapMode = 5
  Placement = pos=(0,2,0) rot=(0,0.707107,0.707107;3.14159rad)
  sketch-geometry (8):
    g0: LineSegment StartX=176.685 StartY=-80.4316 StartZ=0 EndX=143.955 EndY=20.303 EndZ=0
    g1: LineSegment StartX=176.685 StartY=-80.4316 StartZ=0 EndX=215.932 EndY=-80.4316 EndZ=0
    g2: Circle CenterX=179.305 CenterY=-76.8316 CenterZ=0 NormalX=0 NormalY=0 NormalZ=1 AngleXU=0 Radius=3
    g3: Circle CenterX=213.443 CenterY=-76.8316 CenterZ=0 NormalX=0 NormalY=0 NormalZ=1 AngleXU=0 Radius=3
    g4: LineSegment StartX=143.955 StartY=20.303 StartZ=0 EndX=202.765 EndY=20.303 EndZ=0
    g5: LineSegment StartX=215.42 StartY=-53.0314 StartZ=0 EndX=192.176 EndY=-3.18451 EndZ=0
    g6: ArcOfCircle CenterX=184.801 CenterY=-67.3089 CenterZ=0 NormalX=0 NormalY=0 NormalZ=1 AngleXU=0 Radius=33.7833 StartAngle=5.88425 EndAngle=6.71952
    g7: ArcOfCircle CenterX=207.583 CenterY=4 CenterZ=0 NormalX=0 NormalY=0 NormalZ=1 AngleXU=0 Radius=17 StartAngle=1.85815 EndAngle=3.57792
  constraints (19):
    c: Coincident(g0,g-4)
    c: PointOnObject(g0,g-3)
    c: Horizontal(g0,g-7)
    c: Coincident(g1,g0)
    c: Coincident(g1,g-5)
    c: Diameter(g2) = 6
    c: Diameter(g3) = 6
    c: Coincident(g2,g-9)
    c: Coincident(g3,g-10)
    c: Coincident(g4,g0)
    c: Coincident(g5,g-6)
    c: Coincident(g6,g1)
    c: Coincident(g6,g5)
    c: Equal(g-5,g6)
    c: Coincident(g5,g-7)
    c: Coincident(g4,g-7)
    c: Tangent(g7,g-7)
    c: Coincident(g7,g4)
    c: Coincident(g7,g5)
FEATURE [Sketcher::SketchObject] Sketch097
  ArcFitTolerance = 1e-06
  AttachmentSupport = -> [Pad019]
  ExternalGeometry = -> [Binder]
  FullyConstrained = true
  MakeInternals = false
  MapMode = 5
  Placement = pos=(0,2,0) rot=(0,0.707107,0.707107;3.14159rad)
  sketch-geometry (4):
    g0: LineSegment StartX=90 StartY=36.8 StartZ=0 EndX=108 EndY=36.8 EndZ=0
    g1: LineSegment StartX=108 StartY=36.8 StartZ=0 EndX=108 EndY=26.8 EndZ=0
    g2: LineSegment StartX=108 StartY=26.8 StartZ=0 EndX=90 EndY=26.8 EndZ=0
    g3: ArcOfCircle CenterX=94 CenterY=31.8 CenterZ=0 NormalX=0 NormalY=0 NormalZ=1 AngleXU=0 Radius=6.40312 StartAngle=2.24554 EndAngle=4.03765
  constraints (13):
    c: Horizontal(g0)
    c: Coincident(g1,g0)
    c: Vertical(g1)
    c: DistanceX(g0,g0) = 18
    c: DistanceY(g1,g1) = 10
    c: Coincident(g2,g1)
    c: Horizontal(g2)
    c: Equal(g2,g0)
    c: DistanceY(g0,g-3) = 2.4
    c: Coincident(g3,g0)
    c: Coincident(g3,g2)
    c: DistanceX(g2,g3) = 4
    c: DistanceX(g-3,g0) = 90
FEATURE [PartDesign::Chamfer] Chamfer015
  Angle = 45
  Base = -> Pad019 [Edge19,Edge22,Edge79]
  BaseFeature = -> Pad019
  ChamferType = 0
  FlipDirection = false
  Refine = true
  Size = 1.9
  Size2 = 1
  SupportTransform = false
  Suppressed = false
  UseAllEdges = false
FEATURE [PartDesign::Pocket] Pocket002
  BaseFeature = -> Chamfer015
  Direction = (0,1,-2e-16)
  Length = 1.2
  Length2 = 5
  Profile = -> Sketch093
  ReferenceAxis = -> Sketch093 [N_Axis]
  Refine = true
  Suppressed = false
  Type = 0
FEATURE [PartDesign::Pad] Pad005
  BaseFeature = -> Pocket002
  Direction = (0,1,-2e-16)
  Length = 1.6
  Length2 = 10
  Profile = -> Sketch091
  ReferenceAxis = -> Sketch091 [N_Axis]
  Refine = true
  Suppressed = false
  Type = 0
FEATURE [Sketcher::SketchObject] Sketch092  label="Sketch092 - scavi per viti anteriori"
  ArcFitTolerance = 1e-06
  AttachmentSupport = -> [Pad005]
  ExternalGeometry = -> [Binder]
  FullyConstrained = true
  MakeInternals = false
  MapMode = 5
  Placement = pos=(0,3.6,0) rot=(0,0.707107,0.707107;3.14159rad)
  sketch-geometry (20):
    g0: ArcOfCircle CenterX=5.6 CenterY=7.6 CenterZ=0 NormalX=0 NormalY=0 NormalZ=1 AngleXU=0 Radius=3.5 StartAngle=0 EndAngle=1.5708
    g1: ArcOfCircle CenterX=5.6 CenterY=34.8 CenterZ=0 NormalX=0 NormalY=0 NormalZ=1 AngleXU=0 Radius=3.5 StartAngle=4.71239 EndAngle=6.28319
    g2: ArcOfCircle CenterX=78.51 CenterY=34.8 CenterZ=0 NormalX=0 NormalY=0 NormalZ=1 AngleXU=0 Radius=3.5 StartAngle=3.14159 EndAngle=4.71239
    g3: ArcOfCircle CenterX=78.51 CenterY=7.6 CenterZ=0 NormalX=0 NormalY=0 NormalZ=1 AngleXU=0 Radius=3.5 StartAngle=1.5708 EndAngle=3.14159
    g4: LineSegment StartX=0 StartY=3.2 StartZ=0 EndX=0 EndY=11.1 EndZ=0
    g5: LineSegment StartX=0 StartY=11.1 StartZ=0 EndX=5.6 EndY=11.1 EndZ=0
    g6: LineSegment StartX=0 StartY=3.2 StartZ=0 EndX=9.1 EndY=3.2 EndZ=0
    g7: LineSegment StartX=9.1 StartY=3.2 StartZ=0 EndX=9.1 EndY=7.6 EndZ=0
    g8: LineSegment StartX=0 StartY=39.2 StartZ=0 EndX=0 EndY=31.3 EndZ=0
    g9: LineSegment StartX=0 StartY=31.3 StartZ=0 EndX=5.6 EndY=31.3 EndZ=0
    g10: LineSegment StartX=0 StartY=39.2 StartZ=0 EndX=9.1 EndY=39.2 EndZ=0
    g11: LineSegment StartX=9.1 StartY=39.2 StartZ=0 EndX=9.1 EndY=34.8 EndZ=0
    g12: LineSegment StartX=82.8 StartY=39.2 StartZ=0 EndX=75.01 EndY=39.2 EndZ=0
    g13: LineSegment StartX=82.8 StartY=39.2 StartZ=0 EndX=82.8 EndY=31.3 EndZ=0
    g14: LineSegment StartX=82.8 StartY=31.3 StartZ=0 EndX=78.51 EndY=31.3 EndZ=0
    g15: LineSegment StartX=82.8 StartY=3.2 StartZ=0 EndX=75.01 EndY=3.2 EndZ=0
    g16: LineSegment StartX=75.01 StartY=3.2 StartZ=0 EndX=75.01 EndY=7.6 EndZ=0
    g17: LineSegment StartX=82.8 StartY=3.2 StartZ=0 EndX=82.8 EndY=11.1 EndZ=0
    g18: LineSegment StartX=82.8 StartY=11.1 StartZ=0 EndX=78.51 EndY=11.1 EndZ=0
    g19: LineSegment StartX=75.01 StartY=39.2 StartZ=0 EndX=75.01 EndY=34.8 EndZ=0
  constraints (48):
    c: Radius(g0) = 3.5
    c: Coincident(g0,g-10)
    c: Radius(g1) = 3.5
    c: Coincident(g1,g-9)
    c: Radius(g2) = 3.5
    c: Coincident(g2,g-8)
    c: Radius(g3) = 3.5
    c: Coincident(g3,g-7)
    c: Coincident(g4,g-5)
    c: PointOnObject(g4,g-4)
    c: Coincident(g5,g4)
    c: Horizontal(g5)
    c: Coincident(g6,g4)
    c: PointOnObject(g6,g-5)
    c: Coincident(g7,g6)
    c: Vertical(g7)
    c: Coincident(g8,g-4)
    c: PointOnObject(g8,g-4)
    c: Coincident(g9,g8)
    c: Horizontal(g9)
    c: Coincident(g10,g8)
    c: PointOnObject(g10,g-3)
    c: Coincident(g11,g10)
    c: Vertical(g11)
    c: PointOnObject(g12,g-3)
    c: PointOnObject(g12,g-3)
    c: Coincident(g13,g12)
    c: Vertical(g13)
    c: Coincident(g14,g13)
    c: Horizontal(g14)
    c: Coincident(g15,g-6)
    c: PointOnObject(g15,g-5)
    c: Coincident(g16,g15)
    c: Vertical(g16)
    c: Coincident(g17,g15)
    c: Coincident(g18,g17)
    c: Horizontal(g18)
    c: Tangent(g3,g18) = -1.5708
    c: Tangent(g16,g3) = 1.5708
    c: Coincident(g19,g12)
    c: Vertical(g19)
    c: Tangent(g2,g19) = -1.5708
    c: Tangent(g2,g14) = 1.5708
    c: Tangent(g0,g7) = -1.5708
    c: Tangent(g0,g5) = 1.5708
    c: Tangent(g9,g1) = -1.5708
    c: Tangent(g1,g11) = 1.5708
    c: Tangent(g17,g13)
FEATURE [PartDesign::Pocket] Pocket001
  BaseFeature = -> Pad005
  Direction = (0,-1,2e-16)
  Length = 1.6
  Length2 = 5
  Profile = -> Sketch092
  ReferenceAxis = -> Sketch092 [N_Axis]
  Refine = true
  Suppressed = false
  Type = 0
FEATURE [PartDesign::Pad] Pad006
  BaseFeature = -> Pocket001
  Direction = (0,1,-2e-16)
  Length = 0.8
  Length2 = 10
  Profile = -> Sketch094
  ReferenceAxis = -> Sketch094 [N_Axis]
  Refine = true
  Suppressed = false
  Type = 0
FEATURE [PartDesign::Pad] Pad007
  BaseFeature = -> Pad006
  Direction = (0,1,-2e-16)
  Length = 2
  Length2 = 10
  Profile = -> Sketch095
  ReferenceAxis = -> Sketch095 [N_Axis]
  Refine = true
  Suppressed = false
  Type = 0
FEATURE [PartDesign::Pad] Pad008  label="Pad008 - forma impugnatura"
  BaseFeature = -> Pad007
  Direction = (0,1,-2e-16)
  Length = 1.6
  Length2 = 10
  Profile = -> Sketch096
  ReferenceAxis = -> Sketch096 [N_Axis]
  Refine = true
  Suppressed = false
  Type = 0
FEATURE [PartDesign::Pad] Pad009
  BaseFeature = -> Pad008
  Direction = (0,1,-2e-16)
  Length = 1.6
  Length2 = 10
  Profile = -> Sketch097
  ReferenceAxis = -> Sketch097 [N_Axis]
  Refine = true
  Suppressed = false
  Type = 0
FEATURE [Sketcher::SketchObject] Sketch098
  ArcFitTolerance = 1e-06
  AttachmentSupport = -> [Pad006]
  ExternalGeometry = -> [Binder]
  FullyConstrained = true
  MakeInternals = false
  MapMode = 5
  Placement = pos=(0,2.8,-7e-16) rot=(0,0.707107,0.707107;3.14159rad)
  sketch-geometry (4):
    g0: LineSegment StartX=118 StartY=39.2 StartZ=0 EndX=129 EndY=39.2 EndZ=0
    g1: LineSegment StartX=120.599 StartY=31.2 StartZ=0 EndX=131.599 EndY=31.2 EndZ=0
    g2: LineSegment StartX=129 StartY=39.2 StartZ=0 EndX=131.599 EndY=31.2 EndZ=0
    g3: LineSegment StartX=118 StartY=39.2 StartZ=0 EndX=120.599 EndY=31.2 EndZ=0
  constraints (12):
    c: PointOnObject(g0,g-3)
    c: PointOnObject(g0,g-3)
    c: DistanceX(g0,g0) = 11
    c: Horizontal(g1)
    c: Equal(g1,g0)
    c: Coincident(g2,g0)
    c: Coincident(g3,g0)
    c: Parallel(g-4,g2)
    c: Coincident(g1,g2)
    c: Coincident(g1,g3)
    c: DistanceY(g1,g0) = 8
    c: DistanceX(g-3,g0) = 118
FEATURE [Sketcher::SketchObject] Sketch099
  ArcFitTolerance = 1e-06
  AttachmentSupport = -> [Pad008]
  ExternalGeometry = -> [Binder]
  FullyConstrained = true
  MakeInternals = false
  MapMode = 5
  Placement = pos=(0,3.6,0) rot=(0,0.707107,0.707107;3.14159rad)
  sketch-geometry (13):
    g0: LineSegment StartX=192.176 StartY=-3.18451 StartZ=0 EndX=196.804 EndY=-13.1108 EndZ=0
    g1: LineSegment [constr] StartX=202.765 StartY=20.303 StartZ=0 EndX=181.223 EndY=20.303 EndZ=0
    g2: LineSegment [constr] StartX=181.223 StartY=20.303 StartZ=0 EndX=181.223 EndY=-3.18451 EndZ=0
    g3: ArcOfCircle CenterX=181.223 CenterY=-20.3764 CenterZ=0 NormalX=0 NormalY=0 NormalZ=1 AngleXU=0 Radius=17.1918 StartAngle=0.436332 EndAngle=1.57079
    g4: ArcOfEllipse CenterX=181.223 CenterY=8.55923 CenterZ=0 NormalX=0 NormalY=0 NormalZ=1 MajorRadius=23.4779 MinorRadius=11.7437 AngleXU=0 StartAngle=1.5708 EndAngle=4.71239
    g5: LineSegment [constr] StartX=204.701 StartY=8.55923 StartZ=0 EndX=157.745 EndY=8.55923 EndZ=0
    g6: LineSegment [constr] StartX=181.223 StartY=20.303 StartZ=0 EndX=181.223 EndY=-3.18451 EndZ=0
    g7: GeomPoint [constr] X=201.553 Y=8.55923 Z=0
    g8: GeomPoint [constr] X=160.894 Y=8.55923 Z=0
    g9: GeomPoint [constr] X=181.223 Y=-3.18451 Z=0
    g10: LineSegment StartX=181.223 StartY=20.303 StartZ=0 EndX=202.765 EndY=20.303 EndZ=0
    g11: ArcOfCircle CenterX=207.583 CenterY=4 CenterZ=0 NormalX=0 NormalY=0 NormalZ=1 AngleXU=0 Radius=17 StartAngle=1.85815 EndAngle=3.57792
    g12: LineSegment [constr] StartX=172.411 StartY=39.2 StartZ=0 EndX=192.176 EndY=-3.18451 EndZ=0
  constraints (27):
    c: Coincident(g1,g-7)
    c: Horizontal(g1)
    c: Coincident(g2,g1)
    c: Vertical(g2)
    c: Horizontal(g2,g0)
    c: Coincident(g3,g0)
    c: Coincident(g3,g2)
    c: InternalAlignment(g5-g8 -> g4) x4
    c: Horizontal(g5)
    c: PointOnObject(g4,g2)
    c: Coincident(g4,g1)
    c: DistanceX(g-3,g5) = 10.1
    c: Coincident(g4,g2)
    c: Tangent(g3,g-5)
    c: PointOnObject(g9,g4)
    c: PointOnObject(g9,g3)
    c: Tangent(g4,g3,g9) = 1.5708
    c: Coincident(g10,g1)
    c: Coincident(g10,g1)
    c: Equal(g11,g-4)
    c: Coincident(g11,g1)
    c: Coincident(g11,g0)
    c: PointOnObject(g12,g-6)
    c: PointOnObject(g1,g12)
    c: Tangent(g12,g-5) = -1.5708
    c: Tangent(g0,g-5) = -1.5708
    c: Horizontal(g9,g12)
FEATURE [Sketcher::SketchObject] Sketch106  label="Sketch106 - smusso impuniatura interno"
  ArcFitTolerance = 1e-06
  AttachmentSupport = -> [Pad008]
  ExternalGeometry = -> [Pad008]
  FullyConstrained = true
  MakeInternals = false
  MapMode = 5
  Placement = pos=(0,-1.585e-13,-80.4316) rot=(1,0,0;3.14159rad)
  sketch-geometry (9):
    g0: LineSegment StartX=-176.685 StartY=-3.6 StartZ=0 EndX=-176.685 EndY=-2.691e-13 EndZ=0
    g1: LineSegment [constr] StartX=-176.685 StartY=-1.416e-13 StartZ=0 EndX=-176.685 EndY=-2.691e-13 EndZ=0
    g2: LineSegment [constr] StartX=-186.685 StartY=-3.6 StartZ=0 EndX=-186.685 EndY=-2.691e-13 EndZ=0
    g3: ArcOfEllipse CenterX=-186.685 CenterY=-2.691e-13 CenterZ=0 NormalX=0 NormalY=0 NormalZ=1 MajorRadius=10 MinorRadius=3.6 AngleXU=3.14159 StartAngle=1.5708 EndAngle=3.14159
    g4: LineSegment [constr] StartX=-196.685 StartY=-1.416e-13 StartZ=0 EndX=-176.685 EndY=-1.416e-13 EndZ=0
    g5: LineSegment [constr] StartX=-186.685 StartY=-3.6 StartZ=0 EndX=-186.685 EndY=3.6 EndZ=0
    g6: GeomPoint [constr] X=-196.015 Y=-1.41e-13 Z=0
    g7: GeomPoint [constr] X=-177.356 Y=-1.416e-13 Z=0
    g8: LineSegment StartX=-176.685 StartY=-3.6 StartZ=0 EndX=-186.685 EndY=-3.6 EndZ=0
  constraints (15):
    c: PointOnObject(g2,g-3)
    c: Coincident(g1,g-5)
    c: DistanceY(g1,g1) = 0
    c: Coincident(g0,g1)
    c: DistanceX(g2,g-5) = 10
    c: Vertical(g2)
    c: Horizontal(g2,g0)
    c: InternalAlignment(g4-g7 -> g3) x4
    c: Coincident(g3,g2)
    c: Horizontal(g4)
    c: Coincident(g3,g0)
    c: Tangent(g0,g-5) = 1.5708
    c: Coincident(g3,g2)
    c: Coincident(g8,g0)
    c: Coincident(g8,g2)
FEATURE [Sketcher::SketchObject] Sketch107  label="Sketch107 - smusso impugnatura esterno"
  ArcFitTolerance = 1e-06
  AttachmentSupport = -> [Pad008]
  ExternalGeometry = -> [Pad008]
  FullyConstrained = true
  MakeInternals = false
  MapMode = 5
  Placement = pos=(0,-1.585e-13,-80.4316) rot=(1,0,0;3.14159rad)
  sketch-geometry (9):
    g0: LineSegment [constr] StartX=-215.932 StartY=-1.416e-13 StartZ=0 EndX=-215.932 EndY=-5.88e-14 EndZ=0
    g1: LineSegment StartX=-215.932 StartY=-3.6 StartZ=0 EndX=-215.932 EndY=-5.86e-14 EndZ=0
    g2: LineSegment StartX=-215.932 StartY=-3.6 StartZ=0 EndX=-205.932 EndY=-3.6 EndZ=0
    g3: LineSegment [constr] StartX=-205.932 StartY=-3.6 StartZ=0 EndX=-205.932 EndY=-5.86e-14 EndZ=0
    g4: ArcOfEllipse CenterX=-205.932 CenterY=-5.88e-14 CenterZ=0 NormalX=0 NormalY=0 NormalZ=1 MajorRadius=10 MinorRadius=3.6 AngleXU=-3.14159 StartAngle=-2.66e-14 EndAngle=1.5708
    g5: LineSegment [constr] StartX=-215.932 StartY=-1.416e-13 StartZ=0 EndX=-195.932 EndY=-1.416e-13 EndZ=0
    g6: LineSegment [constr] StartX=-205.932 StartY=-3.6 StartZ=0 EndX=-205.932 EndY=3.6 EndZ=0
    g7: GeomPoint [constr] X=-215.262 Y=-1.483e-13 Z=0
    g8: GeomPoint [constr] X=-196.602 Y=-1.551e-13 Z=0
  constraints (16):
    c: Coincident(g0,g-6)
    c: PointOnObject(g0,g-6)
    c: DistanceY(g0,g0) = 0
    c: Coincident(g1,g-6)
    c: Coincident(g1,g0)
    c: Tangent(g2,g-3)
    c: DistanceX(g2,g2) = 10
    c: Coincident(g3,g2)
    c: Vertical(g3)
    c: Horizontal(g3,g0)
    c: InternalAlignment(g5-g8 -> g4) x4
    c: Coincident(g4,g3)
    c: Horizontal(g5)
    c: Coincident(g4,g0)
    c: Coincident(g4,g2)
    c: PointOnObject(g2,g1)
FEATURE [Sketcher::SketchObject] Sketch108
  ArcFitTolerance = 1e-06
  AttachmentOffset = pos=(0,0,-1.6) rot=(0,0,1;0rad)
  AttachmentSupport = -> [Pad008]
  ExternalGeometry = -> [Binder]
  FullyConstrained = true
  MakeInternals = false
  MapMode = 5
  Placement = pos=(0,2,4e-16) rot=(0,0.707107,0.707107;3.14159rad)
  sketch-geometry (14):
    g0: LineSegment StartX=192.176 StartY=-3.18451 StartZ=0 EndX=193.827 EndY=-6.72678 EndZ=0
    g1: LineSegment [constr] StartX=202.765 StartY=20.303 StartZ=0 EndX=181.223 EndY=20.303 EndZ=0
    g2: LineSegment [constr] StartX=181.223 StartY=20.303 StartZ=0 EndX=181.223 EndY=1.30297 EndZ=0
    g3: ArcOfCircle CenterX=181.223 CenterY=-12.6042 CenterZ=0 NormalX=0 NormalY=0 NormalZ=1 AngleXU=0 Radius=13.9072 StartAngle=0.436332 EndAngle=1.5708
    g4: ArcOfEllipse CenterX=181.223 CenterY=10.803 CenterZ=0 NormalX=0 NormalY=0 NormalZ=1 MajorRadius=14.4779 MinorRadius=9.5 AngleXU=0 StartAngle=1.5708 EndAngle=4.71239
    g5: LineSegment [constr] StartX=195.701 StartY=10.803 StartZ=0 EndX=166.745 EndY=10.803 EndZ=0
    g6: LineSegment [constr] StartX=181.223 StartY=20.303 StartZ=0 EndX=181.223 EndY=1.30297 EndZ=0
    g7: GeomPoint [constr] X=192.148 Y=10.803 Z=0
    g8: GeomPoint [constr] X=170.298 Y=10.803 Z=0
    g9: LineSegment StartX=181.223 StartY=20.303 StartZ=0 EndX=202.765 EndY=20.303 EndZ=0
    g10: ArcOfCircle CenterX=207.583 CenterY=4 CenterZ=0 NormalX=0 NormalY=0 NormalZ=1 AngleXU=0 Radius=17 StartAngle=1.85815 EndAngle=3.57792
    g11: LineSegment [constr] StartX=172.411 StartY=39.2 StartZ=0 EndX=192.176 EndY=-3.18451 EndZ=0
    g12: GeomPoint [constr] X=181.223 Y=1.30297 Z=0
    g13: GeomPoint [constr] X=181.223 Y=1.30297 Z=0
  constraints (28):
    c: Coincident(g1,g-7)
    c: Horizontal(g1)
    c: Coincident(g2,g1)
    c: Vertical(g2)
    c: Coincident(g3,g2)
    c: InternalAlignment(g5-g8 -> g4) x4
    c: Horizontal(g5)
    c: PointOnObject(g4,g2)
    c: Coincident(g4,g1)
    c: DistanceX(g-3,g5) = 19.1
    c: Coincident(g4,g2)
    c: Coincident(g9,g1)
    c: Coincident(g9,g1)
    c: Coincident(g10,g1)
    c: Coincident(g10,g0)
    c: PointOnObject(g11,g-6)
    c: PointOnObject(g1,g11)
    c: DistanceY(g2,g1) = 19
    c: Coincident(g10,g-4)
    c: PointOnObject(g12,g4)
    c: PointOnObject(g12,g3)
    c: Tangent(g11,g-5) = -1.5708
    c: Tangent(g0,g-5) = -1.5708
    c: Tangent(g3,g0) = 1.5708
    c: PointOnObject(g13,g4)
    c: PointOnObject(g13,g3)
    c: Tangent(g4,g3,g13) = 1.5708
    c: Horizontal(g11,g0)
FEATURE [Part::Part2DObjectPython] Clone2D  label="Sketch108 (2D)"  # Draft 2D object (typed FeaturePython)
  Fuse = false
  Objects = -> [Sketch108]
  Placement = pos=(0,2,4e-16) rot=(0,0.707107,0.707107;3.14159rad)
  Scale = (1,1,1)
FEATURE [Sketcher::SketchObject] Sketch109
  ArcFitTolerance = 1e-06
  AttachmentOffset = pos=(0,0,-3.5) rot=(0,0,1;0rad)
  AttachmentSupport = -> [Pad008]
  ExternalGeometry = -> [Binder]
  FullyConstrained = true
  MakeInternals = false
  MapMode = 5
  Placement = pos=(0,0.1,8e-16) rot=(0,0.707107,0.707107;3.14159rad)
  sketch-geometry (1):
    g0: GeomPoint X=197.47 Y=8.55923 Z=0
  constraints (1):
    c: Symmetric(g-7,g-5,g0)
FEATURE [PartDesign::Chamfer] Chamfer005
  Angle = 45
  Base = -> Pad009 [Edge215,Edge212]
  BaseFeature = -> Pad009
  ChamferType = 1
  FlipDirection = false
  Refine = true
  Size = 1.5
  Size2 = 2.8
  SupportTransform = false
  Suppressed = false
  UseAllEdges = false
FEATURE [Sketcher::SketchObject] Sketch111
  ArcFitTolerance = 1e-06
  AttachmentSupport = -> [Pad009]
  ExternalGeometry = -> [Pad009]
  FullyConstrained = true
  MakeInternals = false
  MapMode = 5
  Placement = pos=(0,3.6,-8e-16) rot=(0,0.707107,0.707107;3.14159rad)
  sketch-geometry (21):
    g0: LineSegment [constr] StartX=97 StartY=36.8 StartZ=0 EndX=97 EndY=26.8 EndZ=0
    g1: LineSegment StartX=97 StartY=28.6 StartZ=0 EndX=97 EndY=27.8 EndZ=0
    g2: LineSegment StartX=97 StartY=27.8 StartZ=0 EndX=108 EndY=27.8 EndZ=0
    g3: LineSegment StartX=108 StartY=27.8 StartZ=0 EndX=108 EndY=28.6 EndZ=0
    g4: LineSegment StartX=108 StartY=28.6 StartZ=0 EndX=97 EndY=28.6 EndZ=0
    g5: LineSegment StartX=97 StartY=35.8 StartZ=0 EndX=97 EndY=35 EndZ=0
    g6: LineSegment StartX=97 StartY=35 StartZ=0 EndX=108 EndY=35 EndZ=0
    g7: LineSegment StartX=108 StartY=35 StartZ=0 EndX=108 EndY=35.8 EndZ=0
    g8: LineSegment StartX=108 StartY=35.8 StartZ=0 EndX=97 EndY=35.8 EndZ=0
    g9: LineSegment StartX=97 StartY=30.4 StartZ=0 EndX=97 EndY=29.6 EndZ=0
    g10: LineSegment StartX=97 StartY=29.6 StartZ=0 EndX=108 EndY=29.6 EndZ=0
    g11: LineSegment StartX=108 StartY=29.6 StartZ=0 EndX=108 EndY=30.4 EndZ=0
    g12: LineSegment StartX=108 StartY=30.4 StartZ=0 EndX=97 EndY=30.4 EndZ=0
    g13: LineSegment StartX=97 StartY=34 StartZ=0 EndX=97 EndY=33.2 EndZ=0
    g14: LineSegment StartX=97 StartY=33.2 StartZ=0 EndX=108 EndY=33.2 EndZ=0
    g15: LineSegment StartX=108 StartY=33.2 StartZ=0 EndX=108 EndY=34 EndZ=0
    g16: LineSegment StartX=108 StartY=34 StartZ=0 EndX=97 EndY=34 EndZ=0
    g17: LineSegment StartX=97 StartY=32.2 StartZ=0 EndX=97 EndY=31.4 EndZ=0
    g18: LineSegment StartX=97 StartY=31.4 StartZ=0 EndX=108 EndY=31.4 EndZ=0
    g19: LineSegment StartX=108 StartY=31.4 StartZ=0 EndX=108 EndY=32.2 EndZ=0
    g20: LineSegment StartX=108 StartY=32.2 StartZ=0 EndX=97 EndY=32.2 EndZ=0
  constraints (54):
    c: Vertical(g0)
    c: PointOnObject(g0,g-3)
    c: PointOnObject(g0,g-4)
    c: DistanceX(g0,g-5) = 11
    c: Coincident(g1,g2)
    c: Coincident(g2,g3)
    c: Coincident(g3,g4)
    c: Coincident(g4,g1)
    c: Horizontal(g2)
    c: Horizontal(g4)
    c: Tangent(g1,g0)
    c: Tangent(g3,g-5)
    c: DistanceY(g2,g3) = 0.8
    c: Coincident(g5,g6)
    c: Coincident(g6,g7)
    c: Coincident(g7,g8)
    c: Coincident(g8,g5)
    c: Horizontal(g6)
    c: Horizontal(g8)
    c: DistanceY(g6,g7) = 0.8
    c: Coincident(g9,g10)
    c: Coincident(g10,g11)
    c: Coincident(g11,g12)
    c: Coincident(g12,g9)
    c: Horizontal(g10)
    c: Horizontal(g12)
    c: DistanceY(g10,g11) = 0.8
    c: Tangent(g5,g0)
    c: Tangent(g7,g-5)
    c: Tangent(g9,g0)
    c: Tangent(g11,g-5)
    c: Coincident(g13,g14)
    c: Coincident(g14,g15)
    c: Coincident(g15,g16)
    c: Coincident(g16,g13)
    c: Horizontal(g14)
    c: Horizontal(g16)
    c: DistanceY(g14,g15) = 0.8
    c: Tangent(g13,g0)
    c: Tangent(g15,g-5)
    c: Coincident(g17,g18)
    c: Coincident(g18,g19)
    c: Coincident(g19,g20)
    c: Coincident(g20,g17)
    c: Horizontal(g18)
    c: Horizontal(g20)
    c: DistanceY(g18,g19) = 0.8
    c: Tangent(g17,g0)
    c: Tangent(g19,g-5)
    c: DistanceY(g1,g9) = 1
    c: DistanceY(g9,g17) = 1
    c: DistanceY(g17,g13) = 1
    c: DistanceY(g13,g5) = 1
    c: DistanceY(g0,g1) = 1
FEATURE [PartDesign::Pocket] Pocket004
  BaseFeature = -> Chamfer005
  Direction = (0,-1,2e-16)
  Length = 1
  Length2 = 5
  Profile = -> Sketch111
  ReferenceAxis = -> Sketch111 [N_Axis]
  Refine = true
  Suppressed = false
  Type = 0
FEATURE [PartDesign::Pad] Pad010
  BaseFeature = -> Pocket004
  Direction = (0,1,-2e-16)
  Length = 1.2
  Length2 = 10
  Profile = -> Sketch098
  ReferenceAxis = -> Sketch098 [N_Axis]
  Refine = true
  Suppressed = false
  Type = 0
FEATURE [PartDesign::Chamfer] Chamfer006
  Angle = 45
  Base = -> Pad010 [Edge291]
  BaseFeature = -> Pad010
  ChamferType = 1
  FlipDirection = false
  Refine = true
  Size = 1
  Size2 = 6
  SupportTransform = false
  Suppressed = false
  UseAllEdges = false
FEATURE [Sketcher::SketchObject] Sketch110
  ArcFitTolerance = 1e-06
  AttachmentSupport = -> [Pad010]
  ExternalGeometry = -> [Sketch098]
  FullyConstrained = true
  MakeInternals = false
  MapMode = 5
  Placement = pos=(0,4,-9e-16) rot=(0,0.707107,0.707107;3.14159rad)
  sketch-geometry (8):
    g0: LineSegment StartX=119.69 StartY=34 StartZ=0 EndX=130.69 EndY=34 EndZ=0
    g1: LineSegment StartX=119.95 StartY=33.2 StartZ=0 EndX=130.95 EndY=33.2 EndZ=0
    g2: LineSegment StartX=119.137 StartY=35.7 StartZ=0 EndX=130.137 EndY=35.7 EndZ=0
    g3: LineSegment StartX=118.877 StartY=36.5 StartZ=0 EndX=129.877 EndY=36.5 EndZ=0
    g4: LineSegment StartX=118.877 StartY=36.5 StartZ=0 EndX=119.137 EndY=35.7 EndZ=0
    g5: LineSegment StartX=129.877 StartY=36.5 StartZ=0 EndX=130.137 EndY=35.7 EndZ=0
    g6: LineSegment StartX=119.69 StartY=34 StartZ=0 EndX=119.95 EndY=33.2 EndZ=0
    g7: LineSegment StartX=130.69 StartY=34 StartZ=0 EndX=130.95 EndY=33.2 EndZ=0
  constraints (24):
    c: Horizontal(g0)
    c: Horizontal(g1)
    c: Horizontal(g2)
    c: Horizontal(g3)
    c: Equal(g1,g-5)
    c: Equal(g0,g-5)
    c: Equal(g2,g-5)
    c: Equal(g3,g-5)
    c: PointOnObject(g0,g-3)
    c: PointOnObject(g1,g-3)
    c: PointOnObject(g2,g-3)
    c: PointOnObject(g3,g-3)
    c: Coincident(g4,g3)
    c: Coincident(g4,g2)
    c: Coincident(g5,g3)
    c: Coincident(g5,g2)
    c: Coincident(g6,g0)
    c: Coincident(g6,g1)
    c: Coincident(g7,g0)
    c: Coincident(g7,g1)
    c: DistanceY(g1,g0) = 0.8
    c: DistanceY(g2,g3) = 0.8
    c: DistanceY(g-5,g1) = 2
    c: DistanceY(g-5,g2) = 4.5
FEATURE [PartDesign::Pocket] Pocket003
  BaseFeature = -> Chamfer006
  Direction = (0,-1,2e-16)
  Length = 1
  Length2 = 5
  Profile = -> Sketch110
  ReferenceAxis = -> Sketch110 [N_Axis]
  Refine = true
  Suppressed = false
  Type = 0
FEATURE [PartDesign::SubtractivePipe] SubtractivePipe
  AuxilleryCurvelinear = true
  AuxillerySpineTangent = false
  BaseFeature = -> Pocket003
  Binormal = (0,0,0)
  Mode = 0
  Profile = -> Sketch106
  Refine = true
  Spine = -> Pad008 [Edge215]
  SpineTangent = false
  Suppressed = false
  Transformation = 0
  Transition = 0
FEATURE [PartDesign::SubtractivePipe] SubtractivePipe001
  AuxilleryCurvelinear = true
  AuxillerySpineTangent = false
  BaseFeature = -> SubtractivePipe
  Binormal = (0,0,0)
  Mode = 0
  Profile = -> Sketch107
  Refine = true
  Spine = -> Pad008 [Edge213,Edge216,Edge210]
  SpineTangent = false
  Suppressed = false
  Transformation = 0
  Transition = 0
FEATURE [PartDesign::SubtractiveLoft] SubtractiveLoft
  BaseFeature = -> SubtractivePipe001
  Closed = false
  Profile = -> Sketch099
  Refine = true
  Ruled = false
  Sections = -> [Sketch108]
  Suppressed = false
FEATURE [PartDesign::SubtractiveLoft] SubtractiveLoft001
  BaseFeature = -> SubtractiveLoft
  Closed = false
  Profile = -> Clone2D
  Refine = true
  Ruled = false
  Sections = -> [Sketch109]
  Suppressed = false
FEATURE [Sketcher::SketchObject] Sketch112
  ArcFitTolerance = 1e-06
  AttachmentSupport = -> [Pad008]
  ExternalGeometry = -> [Binder]
  FullyConstrained = true
  MakeInternals = false
  MapMode = 5
  Placement = pos=(0,3.6,0) rot=(0,0.707107,0.707107;3.14159rad)
  sketch-geometry (4):
    g0: LineSegment [constr] StartX=167.782 StartY=-53.0314 StartZ=0 EndX=215.42 EndY=-53.0314 EndZ=0
    g1: GeomPoint [constr] X=191.282 Y=-53.0314 Z=0
    g2: Circle CenterX=191.282 CenterY=-53.0314 CenterZ=0 NormalX=0 NormalY=0 NormalZ=1 AngleXU=0 Radius=11.5
    g3: Circle CenterX=191.282 CenterY=-53.0314 CenterZ=0 NormalX=0 NormalY=0 NormalZ=1 AngleXU=0 Radius=10.7
  constraints (9):
    c: Horizontal(g0)
    c: PointOnObject(g0,g-3)
    c: Diameter(g2) = 23
    c: Coincident(g2,g1)
    c: Diameter(g3) = 21.4
    c: Coincident(g3,g1)
    c: DistanceX(g0,g1) = 23.5
    c: PointOnObject(g1,g0)
    c: Coincident(g0,g-4)
FEATURE [PartDesign::Chamfer] Chamfer016
  Angle = 45
  Base = -> SubtractiveLoft001 [Edge118,Edge117,Edge119,Edge120,Edge109]
  BaseFeature = -> SubtractiveLoft001
  ChamferType = 0
  FlipDirection = false
  Refine = true
  Size = 1.5
  Size2 = 1
  SupportTransform = false
  Suppressed = false
  UseAllEdges = false
FEATURE [PartDesign::Chamfer] Chamfer017
  Angle = 45
  Base = -> Chamfer016 [Edge15]
  BaseFeature = -> Chamfer016
  ChamferType = 0
  FlipDirection = false
  Refine = true
  Size = 1.6
  Size2 = 1
  SupportTransform = false
  Suppressed = false
  UseAllEdges = false
FEATURE [PartDesign::Chamfer] Chamfer018
  Angle = 45
  Base = -> Chamfer017 [Edge10]
  BaseFeature = -> Chamfer017
  ChamferType = 0
  FlipDirection = false
  Refine = true
  Size = 3.5
  Size2 = 1
  SupportTransform = false
  Suppressed = false
  UseAllEdges = false
FEATURE [PartDesign::Chamfer] Chamfer019
  Angle = 45
  Base = -> Chamfer018 [Edge94]
  BaseFeature = -> Chamfer018
  ChamferType = 0
  FlipDirection = false
  Refine = true
  Size = 1.9
  Size2 = 1
  SupportTransform = false
  Suppressed = false
  UseAllEdges = false
FEATURE [PartDesign::Fillet] Fillet009
  Base = -> Chamfer019 [Edge83]
  BaseFeature = -> Chamfer019
  Radius = 1.1
  Refine = true
  SupportTransform = false
  Suppressed = false
  UseAllEdges = false
FEATURE [PartDesign::Fillet] Fillet010
  Base = -> Fillet009 [Edge77]
  BaseFeature = -> Fillet009
  Radius = 1.9
  Refine = true
  SupportTransform = false
  Suppressed = false
  UseAllEdges = false
FEATURE [PartDesign::Pocket] Pocket005
  BaseFeature = -> Fillet010
  Direction = (0,-1,2e-16)
  Length = 0.8
  Length2 = 5
  Profile = -> Sketch112
  ReferenceAxis = -> Sketch112 [N_Axis]
  Refine = true
  Suppressed = false
  Type = 0
FEATURE [Part::Part2DObjectPython] ShapeString001  # Draft 2D object (typed FeaturePython)
  FontFile = <path>
  Fuse = false
  Justification = 6
  JustificationReference = 0
  KeepLeftMargin = false
  MakeFace = true
  ObliqueAngle = 0
  Placement = pos=(-183.5,3.6,-57.5) rot=(0,0.707107,0.707107;3.14159rad)
  ScaleToSize = true
  Size = 10
  String = AS
  Tracking = 0
FEATURE [PartDesign::Pocket] Pocket013
  BaseFeature = -> Pocket005
  Direction = (-1e-16,-1,2e-16)
  Length = 1
  Length2 = 5
  Profile = -> ShapeString001
  ReferenceAxis = -> ShapeString001 [N_Axis]
  Refine = true
  Suppressed = false
  Type = 0
FEATURE [PartDesign::Pad] Pad020
  Direction = (0,-1,2e-16)
  Length = 25.2
  Length2 = 10
  Midplane = true
  Placement = pos=(0,0,0) rot=(1,0,0;1.5708rad)
  Profile = -> Sketch021
  ReferenceAxis = -> Sketch021 [N_Axis]
  Refine = true
  Suppressed = false
  Type = 0
FEATURE [PartDesign::Body] Body001  label="perno fermo rumble e driver solenoide"
  AllowCompound = false
  Group = -> [Sketch021,Pad020]
  Origin = -> Origin001
  Tip = -> Pad020
FEATURE [PartDesign::Pad] Pad021
  Direction = (0,-1,2e-16)
  Length = 16.8
  Length2 = 10
  Midplane = true
  Placement = pos=(0,0,0) rot=(1,0,0;1.5708rad)
  Profile = -> Sketch061
  ReferenceAxis = -> Sketch061 [N_Axis]
  Refine = true
  Suppressed = false
  Type = 0
FEATURE [PartDesign::Pocket] Pocket014
  BaseFeature = -> Pad021
  Direction = (0,1,-2e-16)
  Length = 12.8
  Length2 = 5
  Midplane = true
  Placement = pos=(0,0,0) rot=(1,0,0;1.5708rad)
  Profile = -> Sketch062
  ReferenceAxis = -> Sketch062 [N_Axis]
  Refine = true
  Suppressed = false
  Type = 0
FEATURE [PartDesign::Pad] Pad022
  BaseFeature = -> Pocket014
  Direction = (0,-1,2e-16)
  Length = 7.6
  Length2 = 10
  Midplane = true
  Placement = pos=(0,0,0) rot=(1,0,0;1.5708rad)
  Profile = -> Sketch063
  ReferenceAxis = -> Sketch063 [N_Axis]
  Refine = true
  Suppressed = false
  Type = 0
FEATURE [PartDesign::Body] Body003  label="blocco switch"
  AllowCompound = false
  Group = -> [Sketch061,Sketch062,Sketch063,Pad021,Pocket014,Pad022]
  Origin = -> Origin003
  Tip = -> Pad022
FEATURE [PartDesign::Pad] Pad024
  Direction = (0,-1,2e-16)
  Length = 17
  Length2 = 10
  Midplane = true
  Placement = pos=(0,0,0) rot=(1,0,0;1.5708rad)
  Profile = -> Sketch045
  ReferenceAxis = -> Sketch045 [N_Axis]
  Refine = true
  Suppressed = false
  Type = 0
FEATURE [PartDesign::Pocket] Pocket015
  BaseFeature = -> Pad024
  Direction = (-1,0,0)
  Length = 8
  Length2 = 5
  Placement = pos=(0,0,0) rot=(1,0,0;1.5708rad)
  Profile = -> Sketch047
  ReferenceAxis = -> Sketch047 [N_Axis]
  Refine = true
  Reversed = true
  Suppressed = false
  Type = 0
FEATURE [PartDesign::Pocket] Pocket016
  BaseFeature = -> Pocket015
  Direction = (-1,0,0)
  Length = 1
  Length2 = 5
  Placement = pos=(0,0,0) rot=(1,0,0;1.5708rad)
  Profile = -> Sketch046
  ReferenceAxis = -> Sketch046 [N_Axis]
  Refine = true
  Reversed = true
  Suppressed = false
  Type = 0
FEATURE [PartDesign::Pocket] Pocket017
  BaseFeature = -> Pocket016
  Direction = (0,1,-2e-16)
  Length = 17
  Length2 = 5
  Midplane = true
  Placement = pos=(0,0,0) rot=(1,0,0;1.5708rad)
  Profile = -> Sketch048
  ReferenceAxis = -> Sketch048 [N_Axis]
  Refine = true
  Suppressed = false
  Type = 0
FEATURE [PartDesign::Pad] Pad025
  BaseFeature = -> Pocket017
  Direction = (0,-1,2e-16)
  Length = 17
  Length2 = 10
  Midplane = true
  Placement = pos=(0,0,0) rot=(1,0,0;1.5708rad)
  Profile = -> Sketch049
  ReferenceAxis = -> Sketch049 [N_Axis]
  Refine = true
  Suppressed = false
  Type = 0
FEATURE [PartDesign::Pad] Pad026
  BaseFeature = -> Pad025
  Direction = (0,-1,2e-16)
  Length = 17
  Length2 = 10
  Midplane = true
  Placement = pos=(0,0,0) rot=(1,0,0;1.5708rad)
  Profile = -> Sketch066
  ReferenceAxis = -> Sketch066 [N_Axis]
  Refine = true
  Suppressed = false
  Type = 0
FEATURE [PartDesign::Pad] Pad027
  BaseFeature = -> Pad026
  Direction = (0,-1,2e-16)
  Length = 5
  Length2 = 10
  Midplane = true
  Placement = pos=(0,0,0) rot=(1,0,0;1.5708rad)
  Profile = -> Sketch064
  ReferenceAxis = -> Sketch064 [N_Axis]
  Refine = true
  Suppressed = false
  Type = 0
FEATURE [PartDesign::Pad] Pad028
  BaseFeature = -> Pad027
  Direction = (1,0,0)
  Length = 1
  Length2 = 10
  Placement = pos=(0,0,0) rot=(1,0,0;1.5708rad)
  Profile = -> Sketch068
  ReferenceAxis = -> Sketch068 [N_Axis]
  Refine = true
  Reversed = true
  Suppressed = false
  Type = 0
FEATURE [PartDesign::Chamfer] Chamfer020
  Angle = 45
  Base = -> Pad028 [Edge73,Edge75,Edge78,Edge77]
  BaseFeature = -> Pad028
  ChamferType = 0
  FlipDirection = false
  Placement = pos=(0,0,0) rot=(1,0,0;1.5708rad)
  Refine = true
  Size = 0.5
  Size2 = 1
  SupportTransform = false
  Suppressed = false
  UseAllEdges = false
FEATURE [PartDesign::Body] Body002  label="supporto per neopixel"
  AllowCompound = false
  Group = -> [Sketch045,Sketch047,Sketch046,Sketch048,Sketch049,Sketch066,Sketch064,Sketch068,Pad024,Pocket015,Pocket016,Pocket017,Pad025,Pad026,Pad027,Pad028,Chamfer020]
  Origin = -> Origin002
  Tip = -> Chamfer020
FEATURE [Sketcher::SketchObject] Sketch134  label="perno fermo rumble002"
  ArcFitTolerance = 1e-06
  AttachmentSupport = -> [XZ_Plane008]
  FullyConstrained = true
  MakeInternals = false
  MapMode = 5
  Placement = pos=(0,0,0) rot=(1,0,0;1.5708rad)
  sketch-geometry (16):
    g0: LineSegment StartX=0 StartY=0.45 StartZ=0 EndX=0 EndY=1.55 EndZ=0
    g1: LineSegment StartX=0.45 StartY=2 StartZ=0 EndX=1.55 EndY=2 EndZ=0
    g2: LineSegment StartX=2 StartY=1.55 StartZ=0 EndX=2 EndY=0.45 EndZ=0
    g3: LineSegment StartX=1.55 StartY=0 StartZ=0 EndX=0.45 EndY=0 EndZ=0
    g4: ArcOfCircle [constr] CenterX=0.45 CenterY=1.55 CenterZ=0 NormalX=0 NormalY=0 NormalZ=1 AngleXU=0 Radius=0.45 StartAngle=1.5708 EndAngle=3.14159
    g5: GeomPoint [constr] X=0 Y=2 Z=0
    g6: LineSegment StartX=0.45 StartY=2 StartZ=0 EndX=0 EndY=1.55 EndZ=0
    g7: ArcOfCircle [constr] CenterX=1.55 CenterY=1.55 CenterZ=0 NormalX=0 NormalY=0 NormalZ=1 AngleXU=0 Radius=0.45 StartAngle=0 EndAngle=1.5708
    g8: GeomPoint [constr] X=2 Y=2 Z=0
    g9: LineSegment StartX=2 StartY=1.55 StartZ=0 EndX=1.55 EndY=2 EndZ=0
    g10: ArcOfCircle [constr] CenterX=1.55 CenterY=0.45 CenterZ=0 NormalX=0 NormalY=0 NormalZ=1 AngleXU=0 Radius=0.45 StartAngle=4.71239 EndAngle=6.28319
    g11: GeomPoint [constr] X=2 Y=0 Z=0
    g12: LineSegment StartX=1.55 StartY=0 StartZ=0 EndX=2 EndY=0.45 EndZ=0
    g13: ArcOfCircle [constr] CenterX=0.45 CenterY=0.45 CenterZ=0 NormalX=0 NormalY=0 NormalZ=1 AngleXU=0 Radius=0.45 StartAngle=3.14159 EndAngle=4.71239
    g14: GeomPoint [constr] X=0 Y=0 Z=0
    g15: LineSegment StartX=0 StartY=0.45 StartZ=0 EndX=0.45 EndY=0 EndZ=0
  constraints (35):
    c: Coincident(g14,g-1)
    c: PointOnObject(g5,g-2)
    c: Horizontal(g1)
    c: Vertical(g2)
    c: Horizontal(g3)
    c: DistanceX(g5,g8) = 2
    c: DistanceY(g11,g8) = 2
    c: PointOnObject(g5,g0)
    c: PointOnObject(g5,g1)
    c: Tangent(g0,g4) = 1.5708
    c: Tangent(g1,g4) = 1.5708
    c: Coincident(g6,g0)
    c: Coincident(g6,g1)
    c: PointOnObject(g8,g2)
    c: PointOnObject(g8,g1)
    c: Tangent(g2,g7) = 1.5708
    c: Tangent(g1,g7) = 1.5708
    c: Coincident(g9,g2)
    c: Coincident(g9,g1)
    c: PointOnObject(g11,g2)
    c: PointOnObject(g11,g3)
    c: Tangent(g2,g10) = 1.5708
    c: Tangent(g3,g10) = 1.5708
    c: Coincident(g12,g2)
    c: Coincident(g12,g3)
    c: PointOnObject(g14,g0)
    c: PointOnObject(g14,g3)
    c: Tangent(g0,g13) = 1.5708
    c: Tangent(g3,g13) = 1.5708
    c: Coincident(g15,g0)
    c: Coincident(g15,g3)
    c: Equal(g6,g9)
    c: Equal(g9,g12)
    c: Equal(g12,g15)
    c: DistanceX(g14,g3) = 0.45
FEATURE [PartDesign::Pad] Pad029
  Direction = (0,-1,2e-16)
  Length = 17
  Length2 = 10
  Midplane = true
  Placement = pos=(0,0,0) rot=(1,0,0;1.5708rad)
  Profile = -> Sketch134
  ReferenceAxis = -> Sketch134 [N_Axis]
  Refine = true
  Suppressed = false
  Type = 0
FEATURE [PartDesign::Body] Body008  label="perno fermo neopixel"
  AllowCompound = false
  Group = -> [Sketch134,Pad029]
  Origin = -> Origin008
  Tip = -> Pad029
FEATURE [Sketcher::SketchObject] Sketch135  label="perno fermo rumble003"
  ArcFitTolerance = 1e-06
  AttachmentSupport = -> [XZ_Plane009]
  FullyConstrained = true
  MakeInternals = false
  MapMode = 5
  Placement = pos=(0,0,0) rot=(1,0,0;1.5708rad)
  sketch-geometry (16):
    g0: LineSegment StartX=4.69e-14 StartY=0.8 StartZ=0 EndX=-3.04e-14 EndY=3.1 EndZ=0
    g1: LineSegment StartX=0.8 StartY=3.9 StartZ=0 EndX=3.1 EndY=3.9 EndZ=0
    g2: LineSegment StartX=3.9 StartY=3.1 StartZ=0 EndX=3.9 EndY=0.8 EndZ=0
    g3: LineSegment StartX=3.1 StartY=0 StartZ=0 EndX=0.8 EndY=0 EndZ=0
    g4: ArcOfCircle [constr] CenterX=0.8 CenterY=3.1 CenterZ=0 NormalX=0 NormalY=0 NormalZ=1 AngleXU=0 Radius=0.8 StartAngle=1.5708 EndAngle=3.14159
    g5: GeomPoint [constr] X=0 Y=3.9 Z=0
    g6: LineSegment StartX=0.8 StartY=3.9 StartZ=0 EndX=-3.04e-14 EndY=3.1 EndZ=0
    g7: ArcOfCircle [constr] CenterX=3.1 CenterY=3.1 CenterZ=0 NormalX=0 NormalY=0 NormalZ=1 AngleXU=0 Radius=0.8 StartAngle=-2.4e-14 EndAngle=1.5708
    g8: GeomPoint [constr] X=3.9 Y=3.9 Z=0
    g9: LineSegment StartX=3.9 StartY=3.1 StartZ=0 EndX=3.1 EndY=3.9 EndZ=0
    g10: ArcOfCircle [constr] CenterX=3.1 CenterY=0.8 CenterZ=0 NormalX=0 NormalY=0 NormalZ=1 AngleXU=0 Radius=0.8 StartAngle=4.71239 EndAngle=6.28319
    g11: GeomPoint [constr] X=3.9 Y=0 Z=0
    g12: LineSegment StartX=3.1 StartY=0 StartZ=0 EndX=3.9 EndY=0.8 EndZ=0
    g13: ArcOfCircle [constr] CenterX=0.8 CenterY=0.8 CenterZ=0 NormalX=0 NormalY=0 NormalZ=1 AngleXU=0 Radius=0.8 StartAngle=3.14159 EndAngle=4.71239
    g14: GeomPoint [constr] X=0 Y=0 Z=0
    g15: LineSegment StartX=4.69e-14 StartY=0.8 StartZ=0 EndX=0.8 EndY=0 EndZ=0
  constraints (35):
    c: Coincident(g14,g-1)
    c: PointOnObject(g5,g-2)
    c: Horizontal(g1)
    c: Vertical(g2)
    c: Horizontal(g3)
    c: DistanceX(g5,g8) = 3.9
    c: DistanceY(g11,g8) = 3.9
    c: PointOnObject(g5,g0)
    c: PointOnObject(g5,g1)
    c: Tangent(g0,g4) = 1.5708
    c: Tangent(g1,g4) = 1.5708
    c: Coincident(g6,g0)
    c: Coincident(g6,g1)
    c: PointOnObject(g8,g2)
    c: PointOnObject(g8,g1)
    c: Tangent(g2,g7) = 1.5708
    c: Tangent(g1,g7) = 1.5708
    c: Coincident(g9,g2)
    c: Coincident(g9,g1)
    c: PointOnObject(g11,g2)
    c: PointOnObject(g11,g3)
    c: Tangent(g2,g10) = 1.5708
    c: Tangent(g3,g10) = 1.5708
    c: Coincident(g12,g2)
    c: Coincident(g12,g3)
    c: PointOnObject(g14,g0)
    c: PointOnObject(g14,g3)
    c: Tangent(g0,g13) = 1.5708
    c: Tangent(g3,g13) = 1.5708
    c: Coincident(g15,g0)
    c: Coincident(g15,g3)
    c: Equal(g6,g9)
    c: Equal(g9,g12)
    c: Equal(g12,g15)
    c: DistanceX(g14,g3) = 0.8
FEATURE [PartDesign::Pad] Pad030
  Direction = (0,-1,2e-16)
  Length = 25.2
  Length2 = 10
  Midplane = true
  Placement = pos=(0,0,0) rot=(1,0,0;1.5708rad)
  Profile = -> Sketch135
  ReferenceAxis = -> Sketch135 [N_Axis]
  Refine = true
  Suppressed = false
  Type = 0
FEATURE [PartDesign::Body] Body009  label="perno fermo switch - caricabatterie - grilletto"
  AllowCompound = false
  Group = -> [Sketch135,Pad030]
  Origin = -> Origin009
  Tip = -> Pad030
FEATURE [Sketcher::SketchObject] Sketch136  label="scavo_rele"
  ArcFitTolerance = 1e-06
  AttachmentSupport = -> [XZ_Plane]
  ExternalGeometry = -> [Sketch]
  FullyConstrained = true
  MakeInternals = false
  MapMode = 5
  Placement = pos=(0,0,0) rot=(1,0,0;1.5708rad)
  sketch-geometry (7):
    g0: LineSegment [constr] StartX=-172.456 StartY=-60.9321 StartZ=0 EndX=-176.597 EndY=-73.6763 EndZ=0
    g1: LineSegment [constr] StartX=-172.456 StartY=-60.9321 StartZ=0 EndX=-170.364 EndY=-61.612 EndZ=0
    g2: LineSegment [constr] StartX=-172.456 StartY=-60.9321 StartZ=0 EndX=-176.07 EndY=-59.7579 EndZ=0
    g3: LineSegment StartX=-176.07 StartY=-59.7579 StartZ=0 EndX=-170.364 EndY=-61.612 EndZ=0
    g4: LineSegment StartX=-176.07 StartY=-59.7579 StartZ=0 EndX=-180.211 EndY=-72.502 EndZ=0
    g5: LineSegment StartX=-170.364 StartY=-61.612 StartZ=0 EndX=-174.505 EndY=-74.3561 EndZ=0
    g6: LineSegment StartX=-180.211 StartY=-72.502 StartZ=0 EndX=-174.505 EndY=-74.3561 EndZ=0
  constraints (19):
    c: Tangent(g0,g-3)
    c: Distance(g0,g-3) = 87.2
    c: Distance(g0,g0) = 13.4
    c: Coincident(g1,g0)
    c: Coincident(g2,g0)
    c: Distance(g2) = 3.8
    c: Distance(g1) = 2.2
    c: Perpendicular(g0,g1)
    c: Perpendicular(g0,g2)
    c: Coincident(g3,g2)
    c: Coincident(g3,g1)
    c: Equal(g4,g0)
    c: Equal(g5,g0)
    c: Parallel(g4,g0)
    c: Parallel(g5,g0)
    c: Coincident(g4,g2)
    c: Coincident(g5,g1)
    c: Coincident(g6,g4)
    c: Coincident(g6,g5)
FEATURE [Part::Extrusion] Extrude076  label="Extrude076 - scavo_rele"
  Base = -> Sketch136
  Dir = (0,-1,2e-16)
  DirMode = 2
  FaceMakerClass = Part::FaceMakerBullseye
  FaceMakerMode = 3
  LengthFwd = 18.2
  LengthRev = 0
  Solid = true
  Symmetric = true
FEATURE [Sketcher::SketchObject] Sketch137  label="scavo_nuovo_driver"
  ArcFitTolerance = 1e-06
  AttachmentSupport = -> [XZ_Plane]
  ExternalGeometry = -> [Sketch]
  FullyConstrained = true
  MakeInternals = false
  MapMode = 5
  Placement = pos=(0,0,0) rot=(1,0,0;1.5708rad)
  sketch-geometry (7):
    g0: LineSegment [constr] StartX=-160.034 StartY=-22.6997 StartZ=0 EndX=-164.854 EndY=-37.5361 EndZ=0
    g1: LineSegment [constr] StartX=-160.034 StartY=-22.6997 StartZ=0 EndX=-156.99 EndY=-23.6885 EndZ=0
    g2: LineSegment [constr] StartX=-160.034 StartY=-22.6997 StartZ=0 EndX=-163.648 EndY=-21.5254 EndZ=0
    g3: LineSegment StartX=-163.648 StartY=-21.5254 StartZ=0 EndX=-156.99 EndY=-23.6885 EndZ=0
    g4: LineSegment StartX=-163.648 StartY=-21.5254 StartZ=0 EndX=-168.468 EndY=-36.3619 EndZ=0
    g5: LineSegment StartX=-156.99 StartY=-23.6885 StartZ=0 EndX=-161.811 EndY=-38.525 EndZ=0
    g6: LineSegment StartX=-168.468 StartY=-36.3619 StartZ=0 EndX=-161.811 EndY=-38.525 EndZ=0
  constraints (19):
    c: Distance(g0,g-3) = 47
    c: Distance(g0) = 15.6
    c: Tangent(g0,g-3)
    c: Coincident(g1,g0)
    c: Coincident(g2,g0)
    c: Distance(g1) = 3.2
    c: Distance(g2) = 3.8
    c: Perpendicular(g0,g1)
    c: Perpendicular(g0,g2)
    c: Coincident(g3,g2)
    c: Coincident(g3,g1)
    c: Equal(g4,g0)
    c: Equal(g5,g0)
    c: Parallel(g4,g0)
    c: Parallel(g5,g0)
    c: Coincident(g4,g2)
    c: Coincident(g5,g1)
    c: Coincident(g6,g4)
    c: Coincident(g6,g5)
FEATURE [Part::Extrusion] Extrude077  label="Extrude077 - scavo_nuovo_driver"
  Base = -> Sketch137
  Dir = (0,-1,2e-16)
  DirMode = 2
  FaceMakerClass = Part::FaceMakerBullseye
  FaceMakerMode = 3
  LengthFwd = 20.8
  LengthRev = 0
  Solid = true
  Symmetric = true
FEATURE [Sketcher::SketchObject] Sketch138  label="scavo_nuovo_driver_alto"
  ArcFitTolerance = 1e-06
  AttachmentSupport = -> [XZ_Plane]
  ExternalGeometry = -> [Sketch]
  FullyConstrained = true
  MakeInternals = false
  MapMode = 5
  Placement = pos=(0,0,0) rot=(1,0,0;1.5708rad)
  sketch-geometry (7):
    g0: LineSegment [constr] StartX=-188.917 StartY=18.1185 StartZ=0 EndX=-187.75 EndY=4.97025 EndZ=0
    g1: LineSegment StartX=-187.75 StartY=4.97025 StartZ=0 EndX=-189.742 EndY=4.79337 EndZ=0
    g2: LineSegment StartX=-187.75 StartY=4.97025 StartZ=0 EndX=-182.769 EndY=5.41245 EndZ=0
    g3: LineSegment StartX=-190.909 StartY=17.9416 StartZ=0 EndX=-189.742 EndY=4.79337 EndZ=0
    g4: LineSegment StartX=-183.937 StartY=18.5607 StartZ=0 EndX=-182.769 EndY=5.41245 EndZ=0
    g5: LineSegment StartX=-190.909 StartY=17.9416 StartZ=0 EndX=-188.917 EndY=18.1185 EndZ=0
    g6: LineSegment StartX=-188.917 StartY=18.1185 StartZ=0 EndX=-183.937 EndY=18.5607 EndZ=0
  constraints (20):
    c: Distance(g0) = 13.2
    c: DistanceY(g-3,g0) = 9
    c: PointOnObject(g0,g-4)
    c: PointOnObject(g0,g-4)
    c: Coincident(g1,g0)
    c: Coincident(g2,g0)
    c: Distance(g1) = 2
    c: Distance(g2) = 5
    c: Perpendicular(g0,g1)
    c: Perpendicular(g0,g2)
    c: Equal(g3,g0)
    c: Parallel(g3,g0)
    c: Coincident(g3,g1)
    c: Equal(g4,g0)
    c: Parallel(g4,g0)
    c: Coincident(g4,g2)
    c: Coincident(g5,g3)
    c: Coincident(g5,g0)
    c: Coincident(g6,g0)
    c: Coincident(g6,g4)
FEATURE [Part::Extrusion] Extrude078  label="Extrude078 - scavo_nuovo_driver_alto"
  Base = -> Sketch138
  Dir = (0,-1,2e-16)
  DirMode = 2
  FaceMakerClass = Part::FaceMakerBullseye
  FaceMakerMode = 3
  LengthFwd = 17.2
  LengthRev = 0
  Solid = true
  Symmetric = true
FEATURE [Sketcher::SketchObject] Sketch139  label="fermi_nuovo_driver_alto"
  ArcFitTolerance = 1e-06
  AttachmentSupport = -> [XZ_Plane]
  ExternalGeometry = -> [Sketch138,Sketch]
  FullyConstrained = true
  MakeInternals = false
  MapMode = 5
  Placement = pos=(0,0,0) rot=(1,0,0;1.5708rad)
  sketch-geometry (17):
    g0: LineSegment [constr] StartX=-188.41 StartY=16.8018 StartZ=0 EndX=-187.948 EndY=14.1416 EndZ=0
    g1: LineSegment [constr] StartX=-187.948 StartY=14.1416 StartZ=0 EndX=-187.486 EndY=11.4815 EndZ=0
    g2: LineSegment StartX=-187.948 StartY=14.1416 StartZ=0 EndX=-187.76 EndY=13.0579 EndZ=0
    g3: LineSegment StartX=-187.948 StartY=14.1416 StartZ=0 EndX=-188.136 EndY=15.2254 EndZ=0
    g4: LineSegment StartX=-187.76 StartY=13.0579 StartZ=0 EndX=-185.592 EndY=13.4346 EndZ=0
    g5: LineSegment StartX=-188.136 StartY=15.2254 StartZ=0 EndX=-185.969 EndY=15.6021 EndZ=0
    g6: LineSegment StartX=-185.969 StartY=15.6021 StartZ=0 EndX=-185.592 EndY=13.4346 EndZ=0
    g7: LineSegment StartX=-187.486 StartY=11.4815 StartZ=0 EndX=-189.062 EndY=11.2075 EndZ=0
    g8: LineSegment StartX=-188.41 StartY=16.8018 StartZ=0 EndX=-189.987 EndY=16.5278 EndZ=0
    g9: LineSegment StartX=-189.987 StartY=16.5278 StartZ=0 EndX=-189.062 EndY=11.2075 EndZ=0
    g10: LineSegment StartX=-187.486 StartY=11.4815 StartZ=0 EndX=-185.318 EndY=11.8582 EndZ=0
    g11: LineSegment StartX=-188.41 StartY=16.8018 StartZ=0 EndX=-186.243 EndY=17.1785 EndZ=0
    g12: LineSegment StartX=-184.393 StartY=15.8761 StartZ=0 EndX=-184.016 EndY=13.7086 EndZ=0
    g13: ArcOfCircle CenterX=-185.969 CenterY=15.6021 CenterZ=0 NormalX=0 NormalY=0 NormalZ=1 AngleXU=0 Radius=1.6 StartAngle=0.172085 EndAngle=1.74288
    g14: GeomPoint [constr] X=-184.667 Y=17.4525 Z=0
    g15: ArcOfCircle CenterX=-185.592 CenterY=13.4346 CenterZ=0 NormalX=0 NormalY=0 NormalZ=1 AngleXU=0 Radius=1.6 StartAngle=4.88447 EndAngle=6.45527
    g16: GeomPoint [constr] X=-183.742 Y=12.1322 Z=0
  constraints (43):
    c: Tangent(g1,g0) = -1.5708
    c: Distance(g0) = 2.7
    c: Equal(g1,g0)
    c: Tangent(g1,g-5)
    c: Coincident(g2,g0)
    c: Coincident(g3,g0)
    c: Distance(g2) = 1.1
    c: Equal(g3,g2)
    c: PointOnObject(g3,g2)
    c: Coincident(g4,g2)
    c: Coincident(g5,g3)
    c: Distance(g4) = 2.2
    c: Equal(g4,g5)
    c: Perpendicular(g1,g4)
    c: Perpendicular(g0,g5)
    c: Coincident(g6,g5)
    c: Coincident(g6,g4)
    c: Coincident(g7,g1)
    c: Coincident(g8,g0)
    c: Distance(g7) = 1.6
    c: Equal(g7,g8)
    c: Perpendicular(g1,g7)
    c: Perpendicular(g8,g0)
    c: Coincident(g9,g8)
    c: Coincident(g9,g7)
    c: Coincident(g10,g1)
    c: Coincident(g11,g0)
    c: Distance(g10,g16) = 3.8
    c: Perpendicular(g1,g10)
    c: Perpendicular(g1,g11)
    c: DistanceY(g0,g-4) = 3.8
    c: PointOnObject(g14,g12)
    c: PointOnObject(g14,g11)
    c: Tangent(g12,g13) = 1.5708
    c: Tangent(g11,g13) = 1.5708
    c: PointOnObject(g16,g12)
    c: PointOnObject(g16,g10)
    c: Tangent(g12,g15) = 1.5708
    c: Tangent(g10,g15) = -1.5708
    c: Equal(g13,g15)
    c: Coincident(g13,g5)
    c: Parallel(g2,g0)
    c: PointOnObject(g0,g-5)
FEATURE [Part::Extrusion] Extrude079  label="Extrude079 - fermi_nuovo_driver_alto"
  Base = -> Sketch139
  Dir = (0,-1,2e-16)
  DirMode = 2
  FaceMakerClass = Part::FaceMakerBullseye
  FaceMakerMode = 3
  LengthFwd = 25.2
  LengthRev = 0
  Solid = true
  Symmetric = true
FEATURE [Sketcher::SketchObject] Sketch140  label="scavo_diodo_nuovo_driver_alto"
  ArcFitTolerance = 1e-06
  AttachmentSupport = -> [XZ_Plane]
  ExternalGeometry = -> [Sketch138]
  FullyConstrained = true
  MakeInternals = false
  MapMode = 5
  Placement = pos=(0,0,0) rot=(1,0,0;1.5708rad)
  sketch-geometry (4):
    g0: LineSegment StartX=-190.909 StartY=17.9416 StartZ=0 EndX=-189.742 EndY=4.79337 EndZ=0
    g1: LineSegment StartX=-193.898 StartY=17.6763 StartZ=0 EndX=-192.73 EndY=4.52805 EndZ=0
    g2: LineSegment StartX=-190.909 StartY=17.9416 StartZ=0 EndX=-193.898 EndY=17.6763 EndZ=0
    g3: LineSegment StartX=-192.73 StartY=4.52805 StartZ=0 EndX=-189.742 EndY=4.79337 EndZ=0
  constraints (11):
    c: Equal(g0,g-3)
    c: Parallel(g0,g-3)
    c: Equal(g1,g-3)
    c: Parallel(g1,g-3)
    c: Coincident(g2,g0)
    c: Distance(g2) = 3
    c: Perpendicular(g0,g2)
    c: Coincident(g1,g2)
    c: Coincident(g3,g1)
    c: Coincident(g3,g0)
    c: Coincident(g0,g-3)
FEATURE [Part::Extrusion] Extrude080  label="Extrude080 - scavo_diodo_nuovo_driver_alto"
  Base = -> Sketch140
  Dir = (0,-1,2e-16)
  DirMode = 2
  FaceMakerClass = Part::FaceMakerBullseye
  FaceMakerMode = 3
  LengthFwd = 4
  LengthRev = 0
  Placement = pos=(0,7.8,0) rot=(0,0,1;0rad)
  Solid = true
  Symmetric = false
FEATURE [Part::MultiFuse] Fusion001
  Refine = true
  Shapes = -> [Cut043,Extrude079]
FEATURE [Part::Cut] Cut044
  Base = -> Fusion001
  Refine = true
  Tool = -> Extrude078
FEATURE [Part::Cut] Cut045
  Base = -> Cut044
  Refine = true
  Tool = -> Extrude080
FEATURE [Sketcher::SketchObject] Sketch141  label="fermi_nuovo_driver"
  ArcFitTolerance = 1e-06
  AttachmentSupport = -> [XZ_Plane]
  ExternalGeometry = -> [Sketch,Sketch137]
  FullyConstrained = true
  MakeInternals = false
  MapMode = 5
  Placement = pos=(0,0,0) rot=(1,0,0;1.5708rad)
  sketch-geometry (17):
    g0: LineSegment [constr] StartX=-156.99 StartY=-23.6885 StartZ=0 EndX=-160.034 EndY=-22.6997 EndZ=0
    g1: LineSegment [constr] StartX=-160.034 StartY=-22.6997 StartZ=0 EndX=-162.815 EndY=-31.2592 EndZ=0
    g2: LineSegment [constr] StartX=-162.815 StartY=-31.2592 StartZ=0 EndX=-164.484 EndY=-36.3949 EndZ=0
    g3: LineSegment StartX=-164.484 StartY=-36.3949 StartZ=0 EndX=-166.576 EndY=-35.715 EndZ=0
    g4: LineSegment StartX=-167.603 StartY=-33.6989 StartZ=0 EndX=-166.923 EndY=-31.6066 EndZ=0
    g5: LineSegment StartX=-164.907 StartY=-30.5793 StartZ=0 EndX=-161.293 EndY=-31.7536 EndZ=0
    g6: LineSegment StartX=-161.293 StartY=-31.7536 StartZ=0 EndX=-162.962 EndY=-36.8893 EndZ=0
    g7: LineSegment StartX=-164.484 StartY=-36.3949 StartZ=0 EndX=-162.962 EndY=-36.8893 EndZ=0
    g8: LineSegment StartX=-165.402 StartY=-32.101 StartZ=0 EndX=-166.082 EndY=-34.1933 EndZ=0
    g9: LineSegment StartX=-166.082 StartY=-34.1933 StartZ=0 EndX=-163.989 EndY=-34.8732 EndZ=0
    g10: LineSegment StartX=-163.989 StartY=-34.8732 StartZ=0 EndX=-163.309 EndY=-32.7809 EndZ=0
    g11: LineSegment StartX=-163.309 StartY=-32.7809 StartZ=0 EndX=-165.402 EndY=-32.101 EndZ=0
    g12: ArcOfCircle CenterX=-165.402 CenterY=-32.101 CenterZ=0 NormalX=0 NormalY=0 NormalZ=1 AngleXU=0 Radius=1.6 StartAngle=1.25664 EndAngle=2.82743
    g13: GeomPoint [constr] X=-166.429 Y=-30.0849 Z=0
    g14: ArcOfCircle CenterX=-166.082 CenterY=-34.1933 CenterZ=0 NormalX=0 NormalY=0 NormalZ=1 AngleXU=0 Radius=1.6 StartAngle=2.82743 EndAngle=4.39823
    g15: GeomPoint [constr] X=-168.098 Y=-35.2206 Z=0
    g16: LineSegment [constr] StartX=-160.034 StartY=-22.6997 StartZ=0 EndX=-164.854 EndY=-37.5361 EndZ=0
  constraints (44):
    c: Coincident(g0,g-4)
    c: PointOnObject(g0,g-3)
    c: Parallel(g0,g-4)
    c: Coincident(g1,g0)
    c: Parallel(g1,g-3)
    c: Coincident(g2,g1)
    c: Distance(g2) = 5.4
    c: Coincident(g3,g2)
    c: Parallel(g2,g-3)
    c: Distance(g15,g13) = 5.4
    c: Perpendicular(g3,g2)
    c: Parallel(g4,g2)
    c: Distance(g5,g13) = 5.4
    c: Distance(g3,g15) = 3.8
    c: Perpendicular(g4,g5)
    c: Coincident(g6,g5)
    c: Distance(g6) = 5.4
    c: Parallel(g6,g4)
    c: Coincident(g7,g2)
    c: Coincident(g7,g6)
    c: Coincident(g8,g9)
    c: Coincident(g9,g10)
    c: Coincident(g10,g11)
    c: Coincident(g11,g8)
    c: Distance(g8,g10) = 2.2
    c: Distance(g9,g11) = 2.2
    c: Perpendicular(g11,g8)
    c: Equal(g8,g10)
    c: Equal(g11,g9)
    c: Tangent(g10,g2)
    c: Distance(g10,g1) = 1.6
    c: PointOnObject(g13,g4)
    c: PointOnObject(g13,g5)
    c: Tangent(g4,g12) = 1.5708
    c: Tangent(g5,g12) = 1.5708
    c: PointOnObject(g15,g4)
    c: Tangent(g4,g14) = 1.5708
    c: Tangent(g3,g14) = 1.5708
    c: Equal(g14,g12)
    c: Coincident(g12,g8)
    c: Coincident(g16,g0)
    c: PointOnObject(g16,g-5)
    c: Parallel(g16,g-3)
    c: Distance(g16,g2) = 1.2
FEATURE [Part::Extrusion] Extrude081  label="Extrude081 - fermi_nuovo_driver"
  Base = -> Sketch141
  Dir = (0,-1,2e-16)
  DirMode = 2
  FaceMakerClass = Part::FaceMakerBullseye
  FaceMakerMode = 3
  LengthFwd = 25.2
  LengthRev = 0
  Solid = true
  Symmetric = true
FEATURE [Part::MultiFuse] Fusion002
  Refine = true
  Shapes = -> [Cut045,Extrude081]
FEATURE [Part::Cut] Cut046
  Base = -> Fusion002
  Refine = true
  Tool = -> Extrude077
FEATURE [Sketcher::SketchObject] Sketch142  label="fermi_rele"
  ArcFitTolerance = 1e-06
  AttachmentSupport = -> [XZ_Plane]
  ExternalGeometry = -> [Sketch,Sketch136]
  FullyConstrained = true
  MakeInternals = false
  MapMode = 5
  Placement = pos=(0,0,0) rot=(1,0,0;1.5708rad)
  sketch-geometry (15):
    g0: LineSegment StartX=-176.936 StartY=-62.4208 StartZ=0 EndX=-177.615 EndY=-64.5131 EndZ=0
    g1: LineSegment StartX=-174.919 StartY=-61.3936 StartZ=0 EndX=-171.305 EndY=-62.5678 EndZ=0
    g2: LineSegment StartX=-171.305 StartY=-62.5678 StartZ=0 EndX=-172.974 EndY=-67.7035 EndZ=0
    g3: LineSegment StartX=-176.588 StartY=-66.5293 StartZ=0 EndX=-172.974 EndY=-67.7035 EndZ=0
    g4: LineSegment StartX=-175.414 StartY=-62.9152 StartZ=0 EndX=-173.322 EndY=-63.5951 EndZ=0
    g5: LineSegment StartX=-175.414 StartY=-62.9152 StartZ=0 EndX=-176.094 EndY=-65.0076 EndZ=0
    g6: LineSegment StartX=-173.322 StartY=-63.5951 StartZ=0 EndX=-174.001 EndY=-65.6874 EndZ=0
    g7: LineSegment StartX=-176.094 StartY=-65.0076 StartZ=0 EndX=-174.001 EndY=-65.6874 EndZ=0
    g8: LineSegment [constr] StartX=-173.322 StartY=-63.5951 StartZ=0 EndX=-172.827 EndY=-62.0734 EndZ=0
    g9: LineSegment [constr] StartX=-173.322 StartY=-63.5951 StartZ=0 EndX=-171.8 EndY=-64.0895 EndZ=0
    g10: LineSegment [constr] StartX=-170.364 StartY=-61.612 StartZ=0 EndX=-172.456 EndY=-60.9321 EndZ=0
    g11: ArcOfCircle CenterX=-175.414 CenterY=-62.9152 CenterZ=0 NormalX=0 NormalY=0 NormalZ=1 AngleXU=0 Radius=1.6 StartAngle=1.25664 EndAngle=2.82743
    g12: GeomPoint [constr] X=-176.441 Y=-60.8991 Z=0
    g13: ArcOfCircle CenterX=-176.094 CenterY=-65.0076 CenterZ=0 NormalX=0 NormalY=0 NormalZ=1 AngleXU=0 Radius=1.6 StartAngle=2.82743 EndAngle=4.39823
    g14: GeomPoint [constr] X=-178.11 Y=-66.0348 Z=0
  constraints (39):
    c: Distance(g14,g12) = 5.4
    c: Distance(g1,g12) = 5.4
    c: Perpendicular(g1,g0)
    c: Coincident(g2,g1)
    c: Parallel(g2,g0)
    c: Coincident(g3,g2)
    c: Parallel(g2,g-3)
    c: Coincident(g5,g4)
    c: Distance(g5) = 2.2
    c: Distance(g4) = 2.2
    c: Perpendicular(g4,g5)
    c: Coincident(g6,g4)
    c: Equal(g6,g5)
    c: Parallel(g6,g5)
    c: Coincident(g7,g5)
    c: Coincident(g7,g6)
    c: Coincident(g8,g4)
    c: Coincident(g9,g4)
    c: Distance(g8) = 1.6
    c: Distance(g9) = 1.6
    c: Parallel(g8,g6)
    c: Parallel(g9,g4)
    c: PointOnObject(g8,g1)
    c: PointOnObject(g9,g2)
    c: Coincident(g10,g-4)
    c: Parallel(g10,g-4)
    c: PointOnObject(g10,g-3)
    c: Tangent(g6,g-3) = 1.5708
    c: Distance(g4,g10) = 2.8
    c: PointOnObject(g12,g1)
    c: Tangent(g1,g11) = 1.5708
    c: Tangent(g0,g11) = -1.5708
    c: PointOnObject(g14,g3)
    c: PointOnObject(g14,g0)
    c: Tangent(g3,g13) = -1.5708
    c: Tangent(g0,g13) = -1.5708
    c: Equal(g11,g13)
    c: Coincident(g11,g4)
    c: Parallel(g3,g1)
FEATURE [Part::Extrusion] Extrude082  label="Extrude082 - fermi_rele"
  Base = -> Sketch142
  Dir = (0,-1,2e-16)
  DirMode = 2
  FaceMakerClass = Part::FaceMakerBullseye
  FaceMakerMode = 3
  LengthFwd = 25.2
  LengthRev = 0
  Solid = true
  Symmetric = true
FEATURE [Part::MultiFuse] Fusion003
  Refine = true
  Shapes = -> [Cut046,Extrude082]
FEATURE [Part::Cut] Cut047
  Base = -> Fusion003
  Refine = true
  Tool = -> Extrude076
FEATURE [Sketcher::SketchObject] Sketch143  label="foro_passaggio_cavi_led_batteria"
  ArcFitTolerance = 1e-06
  AttachmentSupport = -> [XZ_Plane]
  ExternalGeometry = -> [Sketch,Sketch042,Sketch036]
  FullyConstrained = true
  MakeInternals = false
  MapMode = 5
  Placement = pos=(0,0,0) rot=(1,0,0;1.5708rad)
  sketch-geometry (4):
    g0: LineSegment StartX=-207.775 StartY=-41.3701 StartZ=0 EndX=-213.607 EndY=-53.8767 EndZ=0
    g1: LineSegment StartX=-213.607 StartY=-53.8767 StartZ=0 EndX=-211.843 EndY=-59.5559 EndZ=0
    g2: LineSegment StartX=-207.775 StartY=-41.3701 StartZ=0 EndX=-207.775 EndY=-50.8316 EndZ=0
    g3: LineSegment StartX=-207.775 StartY=-50.8316 StartZ=0 EndX=-211.843 EndY=-59.5559 EndZ=0
  constraints (9):
    c: Coincident(g0,g-3)
    c: PointOnObject(g1,g-6)
    c: Coincident(g1,g0)
    c: Coincident(g2,g0)
    c: Coincident(g2,g-7)
    c: Coincident(g3,g2)
    c: Parallel(g3,g0)
    c: Coincident(g3,g1)
    c: Coincident(g0,g-5)
FEATURE [Part::Extrusion] Extrude083  label="Extrude083 - foro_passaggio_cavi_led_batteria"
  Base = -> Sketch143
  Dir = (0,-1,2e-16)
  DirMode = 2
  FaceMakerClass = Part::FaceMakerBullseye
  FaceMakerMode = 3
  LengthFwd = 6
  LengthRev = 0
  Solid = true
  Symmetric = true
FEATURE [Part::Cut] Cut048
  Base = -> Cut047
  Refine = true
  Tool = -> Extrude083
FEATURE [Sketcher::SketchObject] Sketch144  label="foro_areazione_alimentatore"
  ArcFitTolerance = 1e-06
  AttachmentSupport = -> [XZ_Plane]
  ExternalGeometry = -> [Sketch036]
  FullyConstrained = true
  MakeInternals = false
  MapMode = 5
  Placement = pos=(0,0,0) rot=(1,0,0;1.5708rad)
  sketch-geometry (4):
    g0: LineSegment StartX=-211.843 StartY=-60.3701 StartZ=0 EndX=-207.775 EndY=-60.3701 EndZ=0
    g1: LineSegment StartX=-207.775 StartY=-60.3701 StartZ=0 EndX=-207.775 EndY=-70.3701 EndZ=0
    g2: LineSegment StartX=-211.843 StartY=-60.3701 StartZ=0 EndX=-211.843 EndY=-70.3701 EndZ=0
    g3: LineSegment StartX=-207.775 StartY=-70.3701 StartZ=0 EndX=-211.843 EndY=-70.3701 EndZ=0
  constraints (11):
    c: Horizontal(g0)
    c: Distance(g1) = 10
    c: Coincident(g1,g0)
    c: Tangent(g1,g-3)
    c: PointOnObject(g0,g-4)
    c: Coincident(g2,g0)
    c: PointOnObject(g2,g-4)
    c: Coincident(g3,g1)
    c: Horizontal(g3)
    c: Coincident(g3,g2)
    c: DistanceY(g0,g-3) = 19
FEATURE [Part::Extrusion] Extrude084  label="Extrude084 - foro_areazione_alimentatore"
  Base = -> Sketch144
  Dir = (0,-1,2e-16)
  DirMode = 2
  FaceMakerClass = Part::FaceMakerBullseye
  FaceMakerMode = 3
  LengthFwd = 10
  LengthRev = 0
  Solid = true
  Symmetric = true
FEATURE [Part::Cut] Cut049
  Base = -> Cut048
  Refine = true
  Tool = -> Extrude084
FEATURE [Sketcher::SketchObject] Sketch145  label="foro_per_condesatore"
  ArcFitTolerance = 1e-06
  AttachmentSupport = -> [XZ_Plane]
  ExternalGeometry = -> [Sketch138]
  FullyConstrained = true
  MakeInternals = false
  MapMode = 5
  Placement = pos=(0,0,0) rot=(1,0,0;1.5708rad)
  sketch-geometry (1):
    g0: Circle CenterX=-179.742 CenterY=9.59337 CenterZ=0 NormalX=0 NormalY=0 NormalZ=1 AngleXU=0 Radius=5.4
  constraints (3):
    c: Diameter(g0) = 10.8
    c: DistanceX(g-3,g0) = 10
    c: DistanceY(g-3,g0) = 4.8
FEATURE [Part::Extrusion] Extrude085  label="Extrude085 - foro_per_condesatore"
  Base = -> Sketch145
  Dir = (0,-1,2e-16)
  DirMode = 2
  FaceMakerClass = Part::FaceMakerBullseye
  FaceMakerMode = 3
  LengthFwd = 25.2
  LengthRev = 0
  Solid = true
  Symmetric = true
FEATURE [Part::Cut] Cut050
  Base = -> Cut049
  Refine = true
  Tool = -> Extrude085
FEATURE [Sketcher::SketchObject] Sketch146  label="scavo_pulsante_6x6_per_led_batteria"
  ArcFitTolerance = 1e-06
  AttachmentSupport = -> [XZ_Plane]
  ExternalGeometry = -> [Sketch016]
  FullyConstrained = true
  MakeInternals = false
  MapMode = 5
  Placement = pos=(0,0,0) rot=(1,0,0;1.5708rad)
  sketch-geometry (5):
    g0: LineSegment StartX=-216.643 StartY=-65.8316 StartZ=0 EndX=-216.643 EndY=-72.8316 EndZ=0
    g1: LineSegment StartX=-216.643 StartY=-72.8316 StartZ=0 EndX=-210.243 EndY=-72.8316 EndZ=0
    g2: LineSegment StartX=-210.243 StartY=-72.8316 StartZ=0 EndX=-210.243 EndY=-65.8316 EndZ=0
    g3: LineSegment StartX=-210.243 StartY=-65.8316 StartZ=0 EndX=-216.643 EndY=-65.8316 EndZ=0
    g4: GeomPoint [constr] X=-213.443 Y=-69.3316 Z=0
  constraints (13):
    c: Coincident(g0,g1)
    c: Coincident(g1,g2)
    c: Coincident(g2,g3)
    c: Coincident(g3,g0)
    c: Vertical(g0)
    c: Vertical(g2)
    c: Horizontal(g1)
    c: Horizontal(g3)
    c: Distance(g0,g2) = 6.4
    c: Distance(g1,g3) = 7
    c: Tangent(g1,g-3)
    c: Symmetric(g0,g2,g4)
    c: Vertical(g-3,g4)
FEATURE [Part::Extrusion] Extrude086  label="Extrude086 - scavo_pulsante_6x6_per_led_batteria"
  Base = -> Sketch146
  Dir = (0,-1,2e-16)
  DirMode = 2
  FaceMakerClass = Part::FaceMakerBullseye
  FaceMakerMode = 3
  LengthFwd = 4
  LengthRev = 0
  Placement = pos=(0,12.6,0) rot=(0,0,1;0rad)
  Solid = true
  Symmetric = false
FEATURE [Sketcher::SketchObject] Sketch147  label="scavo_led_stato_batteria"
  ArcFitTolerance = 1e-06
  AttachmentSupport = -> [XZ_Plane]
  ExternalGeometry = -> [Sketch016]
  FullyConstrained = true
  MakeInternals = false
  MapMode = 5
  Placement = pos=(0,0,0) rot=(1,0,0;1.5708rad)
  sketch-geometry (5):
    g0: LineSegment StartX=-215.843 StartY=-56.2316 StartZ=0 EndX=-215.843 EndY=-65.4316 EndZ=0
    g1: LineSegment StartX=-215.843 StartY=-65.4316 StartZ=0 EndX=-211.043 EndY=-65.4316 EndZ=0
    g2: LineSegment StartX=-211.043 StartY=-65.4316 StartZ=0 EndX=-211.043 EndY=-56.2316 EndZ=0
    g3: LineSegment StartX=-211.043 StartY=-56.2316 StartZ=0 EndX=-215.843 EndY=-56.2316 EndZ=0
    g4: GeomPoint [constr] X=-213.443 Y=-60.8316 Z=0
  constraints (13):
    c: Coincident(g0,g1)
    c: Coincident(g1,g2)
    c: Coincident(g2,g3)
    c: Coincident(g3,g0)
    c: Distance(g0,g2) = 4.8
    c: Distance(g1,g3) = 9.2
    c: Equal(g0,g2)
    c: Equal(g1,g3)
    c: Perpendicular(g3,g0)
    c: DistanceY(g-3,g0) = 11.4
    c: Vertical(g2)
    c: Symmetric(g0,g2,g4)
    c: Vertical(g4,g-3)
FEATURE [Part::Extrusion] Extrude087  label="Extrude087 - scavo_led_stato_batteria"
  Base = -> Sketch147
  Dir = (0,-1,2e-16)
  DirMode = 2
  FaceMakerClass = Part::FaceMakerBullseye
  FaceMakerMode = 3
  LengthFwd = 2.2
  LengthRev = 0
  Placement = pos=(0,12.6,0) rot=(0,0,1;0rad)
  Solid = true
  Symmetric = false
FEATURE [Sketcher::SketchObject] Sketch148
  ArcFitTolerance = 1e-06
  AttachmentSupport = -> [Pad016]
  ExternalGeometry = -> [Pad016]
  FullyConstrained = true
  MakeInternals = false
  MapMode = 5
  Placement = pos=(0,0,-80.4316) rot=(1,0,0;3.14159rad)
  sketch-geometry (8):
    g0: LineSegment StartX=-176.685 StartY=3.6 StartZ=0 EndX=-186.685 EndY=3.6 EndZ=0
    g1: LineSegment StartX=-176.685 StartY=3.6 StartZ=0 EndX=-176.685 EndY=-9e-16 EndZ=0
    g2: LineSegment [constr] StartX=-186.685 StartY=3.6 StartZ=0 EndX=-186.685 EndY=-9e-16 EndZ=0
    g3: ArcOfEllipse CenterX=-186.685 CenterY=-9e-16 CenterZ=0 NormalX=0 NormalY=0 NormalZ=1 MajorRadius=10 MinorRadius=3.6 AngleXU=0 StartAngle=0 EndAngle=1.5708
    g4: LineSegment [constr] StartX=-176.685 StartY=-1e-15 StartZ=0 EndX=-196.685 EndY=-1e-15 EndZ=0
    g5: LineSegment [constr] StartX=-186.685 StartY=3.6 StartZ=0 EndX=-186.685 EndY=-3.6 EndZ=0
    g6: GeomPoint [constr] X=-177.356 Y=-1e-15 Z=0
    g7: GeomPoint [constr] X=-196.015 Y=-1e-15 Z=0
  constraints (13):
    c: Distance(g0) = 10
    c: Coincident(g0,g-5)
    c: PointOnObject(g0,g-3)
    c: Coincident(g1,g0)
    c: Coincident(g1,g-5)
    c: Coincident(g2,g0)
    c: Vertical(g2)
    c: PointOnObject(g2,g-4)
    c: InternalAlignment(g4-g7 -> g3) x4
    c: Coincident(g3,g2)
    c: Coincident(g3,g0)
    c: Coincident(g3,g1)
    c: Horizontal(g4)
FEATURE [PartDesign::SubtractivePipe] SubtractivePipe004
  AuxilleryCurvelinear = true
  AuxillerySpineTangent = false
  BaseFeature = -> Pad016
  Binormal = (0,0,0)
  Mode = 0
  Profile = -> Sketch148
  Refine = true
  Spine = -> Pad016 [Edge253]
  SpineTangent = false
  Suppressed = false
  Transformation = 0
  Transition = 0
FEATURE [Sketcher::SketchObject] Sketch149
  ArcFitTolerance = 1e-06
  AttachmentSupport = -> [Pad016]
  ExternalGeometry = -> [Pad016]
  FullyConstrained = true
  MakeInternals = false
  MapMode = 5
  Placement = pos=(0,0,-80.4316) rot=(1,0,0;3.14159rad)
  sketch-geometry (8):
    g0: LineSegment StartX=-215.932 StartY=3.6 StartZ=0 EndX=-205.932 EndY=3.6 EndZ=0
    g1: LineSegment StartX=-215.932 StartY=3.6 StartZ=0 EndX=-215.932 EndY=-4e-16 EndZ=0
    g2: LineSegment [constr] StartX=-205.932 StartY=3.6 StartZ=0 EndX=-205.932 EndY=-9e-16 EndZ=0
    g3: ArcOfEllipse CenterX=-205.932 CenterY=-1e-15 CenterZ=0 NormalX=0 NormalY=0 NormalZ=1 MajorRadius=10 MinorRadius=3.6 AngleXU=-3.14159 StartAngle=4.71239 EndAngle=6.28319
    g4: LineSegment [constr] StartX=-215.932 StartY=-1e-15 StartZ=0 EndX=-195.932 EndY=-1e-15 EndZ=0
    g5: LineSegment [constr] StartX=-205.932 StartY=-3.6 StartZ=0 EndX=-205.932 EndY=3.6 EndZ=0
    g6: GeomPoint [constr] X=-215.262 Y=-2.1e-15 Z=0
    g7: GeomPoint [constr] X=-196.602 Y=-9e-16 Z=0
  constraints (13):
    c: Distance(g0) = 10
    c: Coincident(g0,g-5)
    c: PointOnObject(g0,g-5)
    c: Coincident(g1,g0)
    c: Coincident(g1,g-4)
    c: Coincident(g2,g0)
    c: Vertical(g2)
    c: PointOnObject(g2,g-3)
    c: InternalAlignment(g4-g7 -> g3) x4
    c: Coincident(g3,g2)
    c: Coincident(g3,g0)
    c: Coincident(g3,g1)
    c: Horizontal(g4)
FEATURE [PartDesign::SubtractivePipe] SubtractivePipe005
  AuxilleryCurvelinear = true
  AuxillerySpineTangent = false
  BaseFeature = -> SubtractivePipe004
  Binormal = (0,0,0)
  Mode = 0
  Profile = -> Sketch149
  Refine = true
  Spine = -> Pad016 [Edge251,Edge256,Edge255]
  SpineTangent = false
  Suppressed = false
  Transformation = 0
  Transition = 0
FEATURE [PartDesign::SubtractiveLoft] SubtractiveLoft002
  BaseFeature = -> SubtractivePipe005
  Closed = false
  Profile = -> Sketch129
  Refine = true
  Ruled = false
  Sections = -> [Sketch130]
  Suppressed = false
FEATURE [PartDesign::SubtractiveLoft] SubtractiveLoft003
  BaseFeature = -> SubtractiveLoft002
  Closed = false
  Profile = -> Clone2D001
  Refine = true
  Ruled = false
  Sections = -> [Sketch131]
  Suppressed = false
FEATURE [PartDesign::Chamfer] Chamfer010
  Angle = 45
  Base = -> SubtractiveLoft003 [Edge203,Edge204,Edge202,Edge201,Edge195]
  BaseFeature = -> SubtractiveLoft003
  ChamferType = 0
  FlipDirection = false
  Refine = true
  Size = 1.5
  Size2 = 1
  SupportTransform = false
  Suppressed = false
  UseAllEdges = false
FEATURE [PartDesign::Chamfer] Chamfer011
  Angle = 45
  Base = -> Chamfer010 [Edge15]
  BaseFeature = -> Chamfer010
  ChamferType = 0
  FlipDirection = false
  Refine = true
  Size = 1.6
  Size2 = 1
  SupportTransform = false
  Suppressed = false
  UseAllEdges = false
FEATURE [PartDesign::Chamfer] Chamfer012
  Angle = 45
  Base = -> Chamfer011 [Edge10]
  BaseFeature = -> Chamfer011
  ChamferType = 0
  FlipDirection = false
  Refine = true
  Size = 3.5
  Size2 = 1
  SupportTransform = false
  Suppressed = false
  UseAllEdges = false
FEATURE [PartDesign::Chamfer] Chamfer013
  Angle = 45
  Base = -> Chamfer012 [Edge94]
  BaseFeature = -> Chamfer012
  ChamferType = 0
  FlipDirection = false
  Refine = true
  Size = 1.9
  Size2 = 1
  SupportTransform = false
  Suppressed = false
  UseAllEdges = false
FEATURE [PartDesign::Fillet] Fillet007
  Base = -> Chamfer013 [Edge83]
  BaseFeature = -> Chamfer013
  Radius = 1.1
  Refine = true
  SupportTransform = false
  Suppressed = false
  UseAllEdges = false
FEATURE [PartDesign::Fillet] Fillet008
  Base = -> Fillet007 [Edge75]
  BaseFeature = -> Fillet007
  Radius = 1.9
  Refine = true
  SupportTransform = false
  Suppressed = false
  UseAllEdges = false
FEATURE [PartDesign::Pocket] Pocket011
  BaseFeature = -> Fillet008
  Direction = (0,1,-2e-16)
  Length = 0.8
  Length2 = 5
  Profile = -> Sketch132
  ReferenceAxis = -> Sketch132 [N_Axis]
  Refine = true
  Suppressed = false
  Type = 0
FEATURE [PartDesign::Pocket] Pocket012
  BaseFeature = -> Pocket011
  Direction = (0,1,0)
  Length = 1
  Length2 = 5
  Profile = -> ShapeString
  ReferenceAxis = -> ShapeString [N_Axis]
  Refine = true
  Suppressed = false
  Type = 0
FEATURE [Sketcher::SketchObject] Sketch150
  ArcFitTolerance = 1e-06
  AttachmentSupport = -> [Pad008]
  ExternalGeometry = -> [Pad008]
  FullyConstrained = true
  MakeInternals = false
  MapMode = 5
  Placement = pos=(0,3.6,0) rot=(0,0.707107,0.707107;3.14159rad)
  sketch-geometry (7):
    g0: LineSegment [constr] StartX=210.343 StartY=-66.0316 StartZ=0 EndX=210.343 EndY=-72.8316 EndZ=0
    g1: LineSegment [constr] StartX=210.343 StartY=-72.8316 StartZ=0 EndX=216.543 EndY=-72.8316 EndZ=0
    g2: LineSegment [constr] StartX=216.543 StartY=-72.8316 StartZ=0 EndX=216.543 EndY=-66.0316 EndZ=0
    g3: LineSegment [constr] StartX=216.543 StartY=-66.0316 StartZ=0 EndX=210.343 EndY=-66.0316 EndZ=0
    g4: LineSegment [constr] StartX=210.343 StartY=-72.8316 StartZ=0 EndX=216.543 EndY=-66.0316 EndZ=0
    g5: LineSegment [constr] StartX=210.343 StartY=-66.0316 StartZ=0 EndX=213.443 EndY=-69.4316 EndZ=0
    g6: Circle CenterX=213.443 CenterY=-69.4316 CenterZ=0 NormalX=0 NormalY=0 NormalZ=1 AngleXU=0 Radius=2
  constraints (18):
    c: Coincident(g0,g1)
    c: Coincident(g1,g2)
    c: Coincident(g2,g3)
    c: Coincident(g3,g0)
    c: Vertical(g0)
    c: Vertical(g2)
    c: Horizontal(g1)
    c: Horizontal(g3)
    c: Distance(g0,g2) = 6.2
    c: Distance(g1,g3) = 6.8
    c: DistanceY(g-3,g1) = 4
    c: Coincident(g4,g0)
    c: Coincident(g4,g2)
    c: Coincident(g5,g0)
    c: Symmetric(g0,g2,g5)
    c: Diameter(g6) = 4
    c: Coincident(g6,g5)
    c: Vertical(g5,g-3)
FEATURE [Sketcher::SketchObject] Sketch151
  ArcFitTolerance = 1e-06
  AttachmentSupport = -> [Pad008]
  ExternalGeometry = -> [Pad008]
  FullyConstrained = true
  MakeInternals = false
  MapMode = 5
  Placement = pos=(0,3.6,0) rot=(0,0.707107,0.707107;3.14159rad)
  sketch-geometry (10):
    g0: LineSegment [constr] StartX=211.143 StartY=-56.2316 StartZ=0 EndX=211.143 EndY=-65.4316 EndZ=0
    g1: LineSegment [constr] StartX=211.143 StartY=-65.4316 StartZ=0 EndX=215.743 EndY=-65.4316 EndZ=0
    g2: LineSegment [constr] StartX=215.743 StartY=-65.4316 StartZ=0 EndX=215.743 EndY=-56.2316 EndZ=0
    g3: LineSegment [constr] StartX=215.743 StartY=-56.2316 StartZ=0 EndX=211.143 EndY=-56.2316 EndZ=0
    g4: LineSegment StartX=212.243 StartY=-63.8316 StartZ=0 EndX=214.643 EndY=-63.8316 EndZ=0
    g5: LineSegment StartX=214.643 StartY=-63.8316 StartZ=0 EndX=214.643 EndY=-57.0316 EndZ=0
    g6: LineSegment StartX=214.643 StartY=-57.0316 StartZ=0 EndX=212.243 EndY=-57.0316 EndZ=0
    g7: LineSegment StartX=212.243 StartY=-57.0316 StartZ=0 EndX=212.243 EndY=-63.8316 EndZ=0
    g8: GeomPoint [constr] X=213.443 Y=-60.4316 Z=0
    g9: GeomPoint [constr] X=213.443 Y=-60.8316 Z=0
  constraints (26):
    c: Coincident(g0,g1)
    c: Coincident(g1,g2)
    c: Coincident(g2,g3)
    c: Coincident(g3,g0)
    c: Vertical(g0)
    c: Vertical(g2)
    c: Horizontal(g1)
    c: Horizontal(g3)
    c: Distance(g0,g2) = 4.6
    c: Distance(g1,g3) = 9.2
    c: DistanceY(g-3,g1) = 11.4
    c: Coincident(g4,g5)
    c: Coincident(g5,g6)
    c: Coincident(g6,g7)
    c: Coincident(g7,g4)
    c: Horizontal(g4)
    c: Horizontal(g6)
    c: Vertical(g5)
    c: Vertical(g7)
    c: Symmetric(g6,g4,g8)
    c: Distance(g5,g7) = 2.4
    c: Distance(g4,g6) = 6.8
    c: Symmetric(g2,g0,g9)
    c: Vertical(g8,g9)
    c: DistanceY(g1,g4) = 1.6
    c: Vertical(g9,g-3)
FEATURE [PartDesign::Pocket] Pocket019
  BaseFeature = -> Pocket013
  Direction = (0,-1,2e-16)
  Length = 3.6
  Length2 = 5
  Profile = -> Sketch151
  ReferenceAxis = -> Sketch151 [N_Axis]
  Refine = true
  Suppressed = false
  Type = 0
FEATURE [PartDesign::Pocket] Pocket018
  BaseFeature = -> Pocket019
  Direction = (0,-1,2e-16)
  Length = 3.6
  Length2 = 5
  Profile = -> Sketch150
  ReferenceAxis = -> Sketch150 [N_Axis]
  Refine = true
  Suppressed = false
  Type = 0
FEATURE [PartDesign::Point] DatumPoint
  AttacherType = Attacher::AttachEnginePoint
  AttachmentSupport = -> [Sketch150]
  MapMode = 36
  Placement = pos=(-213.443,3.6,-69.4316) rot=(0,1,0;3.14159rad)
FEATURE [PartDesign::Plane] DatumPlane002
  AttachmentSupport = -> [DatumPoint]
  Length = 265.655
  MapMode = 1
  Placement = pos=(-213.443,3.6,-69.4316) rot=(0,0,1;0rad)
  ResizeMode = 0
  Width = 72.0719
FEATURE [Sketcher::SketchObject] Sketch152
  ArcFitTolerance = 1e-06
  AttachmentSupport = -> [DatumPlane002]
  ExternalGeometry = -> [Sketch150]
  FullyConstrained = true
  MakeInternals = false
  MapMode = 5
  Placement = pos=(-213.443,3.6,-69.4316) rot=(0,0,1;0rad)
  sketch-geometry (7):
    g0: LineSegment StartX=0 StartY=0 StartZ=0 EndX=-4 EndY=5.1e-15 EndZ=0
    g1: ArcOfEllipse CenterX=0 CenterY=0 CenterZ=0 NormalX=0 NormalY=0 NormalZ=1 MajorRadius=4 MinorRadius=3.6 AngleXU=3.14159 StartAngle=2e-16 EndAngle=1.5708
    g2: LineSegment [constr] StartX=-4 StartY=9e-16 StartZ=0 EndX=4 EndY=-9e-16 EndZ=0
    g3: LineSegment [constr] StartX=0 StartY=-3.6 StartZ=0 EndX=0 EndY=3.6 EndZ=0
    g4: GeomPoint [constr] X=-1.74356 Y=2.5e-15 Z=0
    g5: GeomPoint [constr] X=1.74356 Y=-2e-15 Z=0
    g6: LineSegment StartX=0 StartY=0 StartZ=0 EndX=-5.5e-15 EndY=-3.6 EndZ=0
  constraints (11):
    c: PointOnObject(g1,g-2)
    c: Distance(g0) = 4
    c: PointOnObject(g0,g-1)
    c: InternalAlignment(g2-g5 -> g1) x4
    c: Coincident(g1,g0)
    c: Vertical(g3)
    c: Coincident(g1,g-1)
    c: Distance(g6) = 3.6
    c: Coincident(g6,g1)
    c: Coincident(g1,g6)
    c: Coincident(g0,g1)
FEATURE [PartDesign::Groove] Groove
  Angle = 360
  Angle2 = 60
  Axis = (0,1,0)
  Base = (-213.443,3.6,-69.4316)
  BaseFeature = -> Pocket018
  Profile = -> Sketch152
  ReferenceAxis = -> Sketch152 [V_Axis]
  Refine = true
  Reversed = true
  Suppressed = false
  Type = 0
FEATURE [PartDesign::Body] Body006  label="lato SX"
  AllowCompound = false
  Group = -> [Binder,Pad019,Chamfer015,Pocket002,Sketch133,Sketch091,Pad005,Sketch092,Pocket001,Sketch093,Sketch094,Pad006,Sketch095,Pad007,Sketch096,Pad008,Sketch097,Pad009,Chamfer005,Pocket004,Sketch098,Pad010,Chamfer006,Pocket003,SubtractivePipe,SubtractivePipe001,Sketch099,Sketch106,Sketch107,Sketch108,Clone2D,Sketch109,SubtractiveLoft,SubtractiveLoft001,Sketch110,Sketch111,Sketch112,Chamfer016,Chamfer017,+15 more]
  Origin = -> Origin006
  Tip = -> Groove
FEATURE [Sketcher::SketchObject] Sketch153  label="ripieno_per_sostegno_led_batteria"
  ArcFitTolerance = 1e-06
  AttachmentSupport = -> [XZ_Plane]
  ExternalGeometry = -> [Sketch036]
  FullyConstrained = true
  MakeInternals = false
  MapMode = 5
  Placement = pos=(0,0,0) rot=(1,0,0;1.5708rad)
  sketch-geometry (4):
    g0: LineSegment StartX=-217.343 StartY=-54.5944 StartZ=0 EndX=-217.343 EndY=-63.1944 EndZ=0
    g1: LineSegment StartX=-217.343 StartY=-63.1944 StartZ=0 EndX=-211.843 EndY=-63.1944 EndZ=0
    g2: LineSegment StartX=-211.843 StartY=-63.1944 StartZ=0 EndX=-211.843 EndY=-54.5944 EndZ=0
    g3: LineSegment StartX=-211.843 StartY=-54.5944 StartZ=0 EndX=-217.343 EndY=-54.5944 EndZ=0
  constraints (11):
    c: Coincident(g0,g1)
    c: Coincident(g1,g2)
    c: Coincident(g2,g3)
    c: Coincident(g3,g0)
    c: Vertical(g0)
    c: Horizontal(g1)
    c: Horizontal(g3)
    c: Tangent(g2,g-3)
    c: DistanceY(g2,g-3) = 4.5
    c: DistanceX(g3,g3) = 5.5
    c: DistanceY(g0,g0) = 8.6
FEATURE [Part::Extrusion] Extrude088  label="Extrude088 - ripieno_per_sostegno_led_batteria"
  Base = -> Sketch153
  Dir = (0,-1,2e-16)
  DirMode = 2
  FaceMakerClass = Part::FaceMakerBullseye
  FaceMakerMode = 3
  LengthFwd = 4
  LengthRev = 0
  Placement = pos=(0,12.6,0) rot=(0,0,1;0rad)
  Solid = true
  Symmetric = false
FEATURE [Part::MultiFuse] Fusion004
  Refine = true
  Shapes = -> [Cut050,Extrude088]
FEATURE [Part::Cut] Cut051
  Base = -> Fusion004
  Refine = true
  Tool = -> Extrude087
FEATURE [Part::Cut] Cut052
  Base = -> Cut051
  Refine = true
  Tool = -> Extrude086
FEATURE [Sketcher::SketchObject] Sketch154
  ArcFitTolerance = 1e-06
  AttachmentSupport = -> [Pad016]
  ExternalGeometry = -> [Binder001]
  FullyConstrained = true
  MakeInternals = false
  MapMode = 5
  Placement = pos=(0,-3.6,0) rot=(1,0,0;1.5708rad)
  sketch-geometry (25):
    g0: LineSegment StartX=-214.643 StartY=-72.4316 StartZ=0 EndX=-212.243 EndY=-72.4316 EndZ=0
    g1: LineSegment StartX=-212.243 StartY=-72.4316 StartZ=0 EndX=-212.243 EndY=-71.2316 EndZ=0
    g2: LineSegment StartX=-212.243 StartY=-71.2316 StartZ=0 EndX=-214.643 EndY=-71.2316 EndZ=0
    g3: LineSegment StartX=-214.643 StartY=-71.2316 StartZ=0 EndX=-214.643 EndY=-72.4316 EndZ=0
    g4: GeomPoint [constr] X=-213.443 Y=-71.8316 Z=0
    g5: LineSegment StartX=-214.643 StartY=-69.6316 StartZ=0 EndX=-212.243 EndY=-69.6316 EndZ=0
    g6: LineSegment StartX=-212.243 StartY=-69.6316 StartZ=0 EndX=-212.243 EndY=-68.4316 EndZ=0
    g7: LineSegment StartX=-212.243 StartY=-68.4316 StartZ=0 EndX=-214.643 EndY=-68.4316 EndZ=0
    g8: LineSegment StartX=-214.643 StartY=-68.4316 StartZ=0 EndX=-214.643 EndY=-69.6316 EndZ=0
    g9: GeomPoint [constr] X=-213.443 Y=-69.0316 Z=0
    g10: LineSegment StartX=-214.643 StartY=-66.8316 StartZ=0 EndX=-212.243 EndY=-66.8316 EndZ=0
    g11: LineSegment StartX=-212.243 StartY=-66.8316 StartZ=0 EndX=-212.243 EndY=-65.6316 EndZ=0
    g12: LineSegment StartX=-212.243 StartY=-65.6316 StartZ=0 EndX=-214.643 EndY=-65.6316 EndZ=0
    g13: LineSegment StartX=-214.643 StartY=-65.6316 StartZ=0 EndX=-214.643 EndY=-66.8316 EndZ=0
    g14: GeomPoint [constr] X=-213.443 Y=-66.2316 Z=0
    g15: LineSegment StartX=-214.643 StartY=-64.0316 StartZ=0 EndX=-212.243 EndY=-64.0316 EndZ=0
    g16: LineSegment StartX=-212.243 StartY=-64.0316 StartZ=0 EndX=-212.243 EndY=-62.8316 EndZ=0
    g17: LineSegment StartX=-212.243 StartY=-62.8316 StartZ=0 EndX=-214.643 EndY=-62.8316 EndZ=0
    g18: LineSegment StartX=-214.643 StartY=-62.8316 StartZ=0 EndX=-214.643 EndY=-64.0316 EndZ=0
    g19: GeomPoint [constr] X=-213.443 Y=-63.4316 Z=0
    g20: LineSegment StartX=-214.643 StartY=-61.2316 StartZ=0 EndX=-212.243 EndY=-61.2316 EndZ=0
    g21: LineSegment StartX=-212.243 StartY=-61.2316 StartZ=0 EndX=-212.243 EndY=-60.0316 EndZ=0
    g22: LineSegment StartX=-212.243 StartY=-60.0316 StartZ=0 EndX=-214.643 EndY=-60.0316 EndZ=0
    g23: LineSegment StartX=-214.643 StartY=-60.0316 StartZ=0 EndX=-214.643 EndY=-61.2316 EndZ=0
    g24: GeomPoint [constr] X=-213.443 Y=-60.6316 Z=0
  constraints (65):
    c: Coincident(g0,g1)
    c: Coincident(g1,g2)
    c: Coincident(g2,g3)
    c: Coincident(g3,g0)
    c: Horizontal(g0)
    c: Horizontal(g2)
    c: Vertical(g1)
    c: Vertical(g3)
    c: Symmetric(g2,g0,g4)
    c: Distance(g1,g3) = 2.4
    c: Distance(g0,g2) = 1.2
    c: Coincident(g5,g6)
    c: Coincident(g6,g7)
    c: Coincident(g7,g8)
    c: Coincident(g8,g5)
    c: Horizontal(g5)
    c: Horizontal(g7)
    c: Vertical(g6)
    c: Vertical(g8)
    c: Symmetric(g7,g5,g9)
    c: Distance(g6,g8) = 2.4
    c: Distance(g5,g7) = 1.2
    c: Coincident(g10,g11)
    c: Coincident(g11,g12)
    c: Coincident(g12,g13)
    c: Coincident(g13,g10)
    c: Horizontal(g10)
    c: Horizontal(g12)
    c: Vertical(g11)
    c: Vertical(g13)
    c: Symmetric(g12,g10,g14)
    c: Distance(g11,g13) = 2.4
    c: Distance(g10,g12) = 1.2
    c: Coincident(g15,g16)
    c: Coincident(g16,g17)
    c: Coincident(g17,g18)
    c: Coincident(g18,g15)
    c: Horizontal(g15)
    c: Horizontal(g17)
    c: Vertical(g16)
    c: Vertical(g18)
    c: Symmetric(g17,g15,g19)
    c: Distance(g16,g18) = 2.4
    c: Distance(g15,g17) = 1.2
    c: Vertical(g4,g-3)
    c: Vertical(g9,g-3)
    c: Vertical(g14,g-3)
    c: Vertical(g19,g-3)
    c: DistanceY(g-3,g4) = 5
    c: DistanceY(g4,g9) = 2.8
    c: DistanceY(g9,g14) = 2.8
    c: DistanceY(g14,g19) = 2.8
    c: Coincident(g20,g21)
    c: Coincident(g21,g22)
    c: Coincident(g22,g23)
    c: Coincident(g23,g20)
    c: Horizontal(g20)
    c: Horizontal(g22)
    c: Vertical(g21)
    c: Vertical(g23)
    c: Symmetric(g22,g20,g24)
    c: Distance(g21,g23) = 2.4
    c: Distance(g20,g22) = 1.2
    c: DistanceY(g19,g24) = 2.8
    c: Vertical(g-3,g24)
FEATURE [PartDesign::Pocket] Pocket020
  BaseFeature = -> Pocket012
  Direction = (0,1,-2e-16)
  Length = 3.6
  Length2 = 5
  Profile = -> Sketch154
  ReferenceAxis = -> Sketch154 [N_Axis]
  Refine = true
  Suppressed = false
  Type = 0
FEATURE [PartDesign::Body] Body007  label="lato DX"
  AllowCompound = false
  Group = -> [Binder001,Sketch114,Pad011,Chamfer014,Sketch115,Pocket006,Sketch116,Pad012,Sketch117,Pocket007,Sketch118,Pad013,Sketch119,Pocket008,Pad017,Chamfer009,Pocket009,Sketch123,Sketch120,Pad014,Pad018,Chamfer008,Pocket010,Sketch121,Pad015,Sketch122,Pad016,SubtractivePipe004,SubtractivePipe005,Sketch149,Sketch148,Sketch124,Sketch125,Sketch126,Sketch129,Sketch130,Clone2D001,Sketch131,SubtractiveLoft002,+13 more]
  Origin = -> Origin007
  Tip = -> Pocket020
FEATURE [Sketcher::SketchObject] Sketch155  label="fermo per protezione batteria"
  ArcFitTolerance = 1e-06
  AttachmentSupport = -> [XZ_Plane]
  ExternalGeometry = -> [Sketch016,Sketch]
  FullyConstrained = true
  MakeInternals = false
  MapMode = 5
  Placement = pos=(0,0,0) rot=(1,0,0;1.5708rad)
  sketch-geometry (5):
    g0: LineSegment StartX=-183.305 StartY=-76.0316 StartZ=0 EndX=-179.305 EndY=-76.0316 EndZ=0
    g1: LineSegment StartX=-179.305 StartY=-76.0316 StartZ=0 EndX=-179.305 EndY=-74.4316 EndZ=0
    g2: LineSegment StartX=-179.305 StartY=-74.4316 StartZ=0 EndX=-183.305 EndY=-74.4316 EndZ=0
    g3: LineSegment [constr] StartX=-183.305 StartY=-76.0316 StartZ=0 EndX=-183.305 EndY=-78.4316 EndZ=0
    g4: LineSegment StartX=-183.305 StartY=-74.4316 StartZ=0 EndX=-183.305 EndY=-76.0316 EndZ=0
  constraints (16):
    c: Horizontal(g0)
    c: Distance(g1) = 1.6
    c: Coincident(g1,g0)
    c: Vertical(g1)
    c: Coincident(g2,g1)
    c: Horizontal(g2)
    c: Vertical(g3)
    c: PointOnObject(g3,g-4)
    c: Horizontal(g3,g0)
    c: Tangent(g3,g-3)
    c: Vertical(g0,g-3)
    c: Coincident(g4,g2)
    c: Coincident(g4,g0)
    c: Vertical(g4)
    c: Vertical(g0,g3)
    c: DistanceY(g3,g3) = 2.4
FEATURE [Part::Extrusion] Extrude089  label="Extrude089 - fermo per protezione batteria"
  Base = -> Sketch155
  Dir = (0,-1,2e-16)
  DirMode = 2
  FaceMakerClass = Part::FaceMakerBullseye
  FaceMakerMode = 3
  LengthFwd = 8
  LengthRev = 0
  Solid = true
  Symmetric = true
FEATURE [Sketcher::SketchObject] Sketch156  label="buco per protezione batteria"
  ArcFitTolerance = 1e-06
  AttachmentSupport = -> [XZ_Plane]
  ExternalGeometry = -> [Sketch,Sketch016]
  FullyConstrained = true
  MakeInternals = false
  MapMode = 5
  Placement = pos=(0,0,0) rot=(1,0,0;1.5708rad)
  sketch-geometry (5):
    g0: LineSegment [constr] StartX=-183.305 StartY=-76.8316 StartZ=0 EndX=-183.305 EndY=-78.4316 EndZ=0
    g1: LineSegment StartX=-200.305 StartY=-78.4316 StartZ=0 EndX=-200.305 EndY=-80.4316 EndZ=0
    g2: LineSegment StartX=-200.305 StartY=-80.4316 StartZ=0 EndX=-198.505 EndY=-80.4316 EndZ=0
    g3: LineSegment StartX=-198.505 StartY=-80.4316 StartZ=0 EndX=-198.505 EndY=-78.4316 EndZ=0
    g4: LineSegment StartX=-198.505 StartY=-78.4316 StartZ=0 EndX=-200.305 EndY=-78.4316 EndZ=0
  constraints (15):
    c: Vertical(g0)
    c: Tangent(g0,g-4)
    c: PointOnObject(g0,g-3)
    c: Horizontal(g0,g-4)
    c: Coincident(g1,g2)
    c: Coincident(g2,g3)
    c: Coincident(g3,g4)
    c: Coincident(g4,g1)
    c: Vertical(g1)
    c: Vertical(g3)
    c: Horizontal(g2)
    c: Distance(g1,g3) = 1.8
    c: Distance(g2,g4) = 2
    c: Tangent(g4,g-3)
    c: Distance(g3,g0) = 15.2
FEATURE [Part::Extrusion] Extrude090  label="Extrude090 - buco per protezione batteria"
  Base = -> Sketch156
  Dir = (0,-1,2e-16)
  DirMode = 2
  FaceMakerClass = Part::FaceMakerBullseye
  FaceMakerMode = 3
  LengthFwd = 4.8
  LengthRev = 0
  Solid = true
  Symmetric = true
FEATURE [Sketcher::SketchObject] Sketch157
  ArcFitTolerance = 1e-06
  AttachmentSupport = -> [XY_Plane010]
  FullyConstrained = true
  MakeInternals = false
  MapMode = 5
  sketch-geometry (9):
    g0: LineSegment [constr] StartX=1.8 StartY=8 StartZ=0 EndX=1.8 EndY=-8 EndZ=0
    g1: LineSegment StartX=1.8 StartY=8 StartZ=0 EndX=17 EndY=8 EndZ=0
    g2: LineSegment StartX=1.8 StartY=-8 StartZ=0 EndX=17 EndY=-8 EndZ=0
    g3: LineSegment StartX=0 StartY=8 StartZ=0 EndX=0 EndY=-8 EndZ=0
    g4: LineSegment StartX=1.8 StartY=8 StartZ=0 EndX=0 EndY=8 EndZ=0
    g5: LineSegment StartX=1.8 StartY=-8 StartZ=0 EndX=0 EndY=-8 EndZ=0
    g6: LineSegment StartX=17 StartY=8 StartZ=0 EndX=17 EndY=-8 EndZ=0
    g7: Circle CenterX=8.5 CenterY=0 CenterZ=0 NormalX=0 NormalY=0 NormalZ=1 AngleXU=0 Radius=5
    g8: LineSegment [constr] StartX=17 StartY=8 StartZ=0 EndX=17 EndY=0 EndZ=0
  constraints (23):
    c: DistanceY(g0,g0) = 16
    c: Distance(g1) = 15.2
    c: Coincident(g1,g0)
    c: Horizontal(g1)
    c: Coincident(g2,g0)
    c: Horizontal(g2)
    c: Equal(g1,g2)
    c: Symmetric(g0,g0,g-1)
    c: Equal(g3,g0)
    c: Coincident(g4,g0)
    c: Horizontal(g4)
    c: DistanceX(g4,g4) = 1.8
    c: Coincident(g5,g0)
    c: Horizontal(g5)
    c: Equal(g4,g5)
    c: Coincident(g3,g4)
    c: Tangent(g3,g-2)
    c: Coincident(g6,g1)
    c: Coincident(g6,g2)
    c: Coincident(g8,g1)
    c: Symmetric(g6,g6,g8)
    c: Symmetric(g8,g-1,g7)
    c: Diameter(g7) = 10
FEATURE [PartDesign::Pad] Pad031
  Direction = (0,0,1)
  Length = 1.4
  Length2 = 10
  Profile = -> Sketch157
  ReferenceAxis = -> Sketch157 [N_Axis]
  Refine = true
  Suppressed = false
  Type = 0
FEATURE [Sketcher::SketchObject] Sketch158
  ArcFitTolerance = 1e-06
  AttachmentSupport = -> [Pad031]
  ExternalGeometry = -> [Pad031]
  FullyConstrained = true
  MakeInternals = false
  MapMode = 5
  Placement = pos=(0,0,1.4) rot=(0,0,1;0rad)
  sketch-geometry (4):
    g0: LineSegment StartX=0 StartY=8 StartZ=0 EndX=0 EndY=-8 EndZ=0
    g1: LineSegment StartX=0 StartY=8 StartZ=0 EndX=1.8 EndY=8 EndZ=0
    g2: LineSegment StartX=1.8 StartY=8 StartZ=0 EndX=1.8 EndY=-8 EndZ=0
    g3: LineSegment StartX=0 StartY=-8 StartZ=0 EndX=1.8 EndY=-8 EndZ=0
  constraints (10):
    c: Coincident(g0,g-3)
    c: Coincident(g0,g-4)
    c: Distance(g1) = 1.8
    c: Coincident(g1,g0)
    c: PointOnObject(g1,g-3)
    c: Coincident(g2,g1)
    c: Vertical(g2)
    c: Coincident(g3,g0)
    c: PointOnObject(g3,g-4)
    c: Coincident(g3,g2)
FEATURE [PartDesign::Pad] Pad032
  BaseFeature = -> Pad031
  Direction = (0,0,1)
  Length = 6.4
  Length2 = 10
  Profile = -> Sketch158
  ReferenceAxis = -> Sketch158 [N_Axis]
  Refine = true
  Suppressed = false
  Type = 0
FEATURE [Sketcher::SketchObject] Sketch159
  ArcFitTolerance = 1e-06
  AttachmentSupport = -> [Pad032]
  ExternalGeometry = -> [Pad032,Pad031]
  FullyConstrained = true
  MakeInternals = false
  MapMode = 5
  Placement = pos=(0,0,7.8) rot=(0,0,1;0rad)
  sketch-geometry (7):
    g0: LineSegment StartX=0.1 StartY=2.2 StartZ=0 EndX=0.1 EndY=-2.2 EndZ=0
    g1: LineSegment StartX=0.1 StartY=-2.2 StartZ=0 EndX=1.7 EndY=-2.2 EndZ=0
    g2: LineSegment StartX=1.7 StartY=-2.2 StartZ=0 EndX=1.7 EndY=2.2 EndZ=0
    g3: LineSegment StartX=1.7 StartY=2.2 StartZ=0 EndX=0.1 EndY=2.2 EndZ=0
    g4: GeomPoint [constr] X=0.9 Y=8 Z=0
    g5: GeomPoint [constr] X=0.9 Y=-8 Z=0
    g6: LineSegment [constr] StartX=0.9 StartY=8 StartZ=0 EndX=0.9 EndY=-8 EndZ=0
  constraints (14):
    c: Coincident(g0,g1)
    c: Coincident(g1,g2)
    c: Coincident(g2,g3)
    c: Coincident(g3,g0)
    c: Vertical(g2)
    c: Horizontal(g1)
    c: Distance(g0,g2) = 1.6
    c: Distance(g1,g3) = 4.4
    c: Symmetric(g0,g0,g-1)
    c: Symmetric(g-4,g-4,g4)
    c: Symmetric(g-3,g-5,g5)
    c: Coincident(g6,g4)
    c: Coincident(g6,g5)
    c: Symmetric(g0,g2,g6)
FEATURE [PartDesign::Pad] Pad033
  BaseFeature = -> Pad032
  Direction = (0,0,1)
  Length = 1.4
  Length2 = 10
  Profile = -> Sketch159
  ReferenceAxis = -> Sketch159 [N_Axis]
  Refine = true
  Suppressed = false
  Type = 0
FEATURE [Part::Cut] Cut053
  Base = -> Cut052
  Refine = true
  Tool = -> Extrude089
FEATURE [Part::Cut] Cut054
  Base = -> Cut053
  Refine = true
  Tool = -> Extrude090
FEATURE [Sketcher::SketchObject] Sketch160
  ArcFitTolerance = 1e-06
  AttachmentSupport = -> [Pad033]
  ExternalGeometry = -> [Pad033]
  FullyConstrained = true
  MakeInternals = false
  MapMode = 5
  Placement = pos=(0,0,1.4) rot=(0,0,1;0rad)
  sketch-geometry (4):
    g0: LineSegment StartX=15.6 StartY=3.7 StartZ=0 EndX=15.6 EndY=-3.7 EndZ=0
    g1: LineSegment StartX=15.6 StartY=-3.7 StartZ=0 EndX=17 EndY=-3.7 EndZ=0
    g2: LineSegment StartX=17 StartY=-3.7 StartZ=0 EndX=17 EndY=3.7 EndZ=0
    g3: LineSegment StartX=17 StartY=3.7 StartZ=0 EndX=15.6 EndY=3.7 EndZ=0
  constraints (10):
    c: Coincident(g0,g1)
    c: Coincident(g1,g2)
    c: Coincident(g2,g3)
    c: Coincident(g3,g0)
    c: Horizontal(g1)
    c: Horizontal(g3)
    c: Distance(g0,g2) = 1.4
    c: Distance(g1,g3) = 7.4
    c: Symmetric(g0,g0,g-1)
    c: Tangent(g2,g-3)
FEATURE [PartDesign::Pad] Pad034
  BaseFeature = -> Pad033
  Direction = (0,0,1)
  Length = 2.4
  Length2 = 10
  Profile = -> Sketch160
  ReferenceAxis = -> Sketch160 [N_Axis]
  Refine = true
  Suppressed = false
  Type = 0
FEATURE [Sketcher::SketchObject] Sketch161
  ArcFitTolerance = 1e-06
  AttachmentSupport = -> [Pad034]
  ExternalGeometry = -> [Pad034]
  FullyConstrained = true
  MakeInternals = false
  MapMode = 5
  Placement = pos=(0,0,3.8) rot=(0,0,1;0rad)
  sketch-geometry (6):
    g0: LineSegment StartX=17 StartY=3.7 StartZ=0 EndX=21 EndY=3.7 EndZ=0
    g1: LineSegment StartX=17 StartY=3.7 StartZ=0 EndX=15.6 EndY=3.7 EndZ=0
    g2: LineSegment StartX=15.6 StartY=3.7 StartZ=0 EndX=15.6 EndY=-3.7 EndZ=0
    g3: LineSegment StartX=15.6 StartY=-3.7 StartZ=0 EndX=17 EndY=-3.7 EndZ=0
    g4: LineSegment StartX=17 StartY=-3.7 StartZ=0 EndX=21 EndY=-3.7 EndZ=0
    g5: LineSegment StartX=21 StartY=3.7 StartZ=0 EndX=21 EndY=-3.7 EndZ=0
  constraints (14):
    c: Distance(g0) = 4
    c: Coincident(g0,g-4)
    c: Horizontal(g0)
    c: Coincident(g1,g0)
    c: Coincident(g1,g-3)
    c: Coincident(g2,g1)
    c: Coincident(g2,g-5)
    c: Coincident(g3,g2)
    c: Coincident(g3,g-5)
    c: Coincident(g4,g3)
    c: Horizontal(g4)
    c: Equal(g4,g0)
    c: Coincident(g5,g0)
    c: Coincident(g5,g4)
FEATURE [PartDesign::Pad] Pad035
  BaseFeature = -> Pad034
  Direction = (0,0,1)
  Length = 1.4
  Length2 = 10
  Profile = -> Sketch161
  ReferenceAxis = -> Sketch161 [N_Axis]
  Refine = true
  Suppressed = false
  Type = 0
FEATURE [PartDesign::Body] Body010  label="Protezione_inferiore_batteria"
  AllowCompound = false
  Group = -> [Sketch157,Pad031,Sketch158,Pad032,Sketch159,Pad033,Sketch160,Pad034,Sketch161,Pad035]
  Origin = -> Origin010
  Tip = -> Pad035
FEATURE [Sketcher::SketchObject] Sketch162  label="scavo_saldature_nuovo_driver_alto"
  ArcFitTolerance = 1e-06
  AttachmentSupport = -> [XZ_Plane]
  ExternalGeometry = -> [Sketch138]
  FullyConstrained = true
  MakeInternals = false
  MapMode = 5
  Placement = pos=(0,0,0) rot=(1,0,0;1.5708rad)
  sketch-geometry (4):
    g0: LineSegment StartX=-192.503 StartY=17.8001 StartZ=0 EndX=-191.336 EndY=4.65187 EndZ=0
    g1: LineSegment StartX=-192.503 StartY=17.8001 StartZ=0 EndX=-190.909 EndY=17.9416 EndZ=0
    g2: LineSegment StartX=-190.909 StartY=17.9416 StartZ=0 EndX=-189.742 EndY=4.79337 EndZ=0
    g3: LineSegment StartX=-189.742 StartY=4.79337 StartZ=0 EndX=-191.336 EndY=4.65187 EndZ=0
  constraints (10):
    c: Parallel(g0,g-3)
    c: Equal(g0,g-3)
    c: Coincident(g1,g0)
    c: Perpendicular(g0,g1)
    c: Coincident(g1,g-3)
    c: Coincident(g2,g1)
    c: Coincident(g2,g-3)
    c: Coincident(g3,g2)
    c: Coincident(g3,g0)
    c: Distance(g1) = 1.6
FEATURE [PartDesign::Body] Body  label="Struttura pistola"
  AllowCompound = false
  Group = -> [Sketch,Sketch002,Sketch004,DatumPlane,Sketch005,DatumPlane001,CopyCut,Sketch008,Sketch009,Sketch010,Sketch011,Sketch012,Sketch013,Sketch014,Sketch015,Sketch016,Sketch017,Sketch018,Sketch019,Sketch020,Sketch022,Sketch023,Sketch024,Sketch025,Sketch026,Sketch027,Sketch029,Sketch030,Sketch031,Sketch032,Sketch033,Sketch034,Sketch035,Sketch036,Sketch037,Sketch038,Sketch039,Sketch040,Sketch041,Sketch042,+31 more]
  Origin = -> Origin
FEATURE [Part::Extrusion] Extrude091  label="Extrude091 - scavo_saldature_nuovo_driver_alto"
  Base = -> Sketch162
  Dir = (0,-1,2e-16)
  DirMode = 2
  FaceMakerClass = Part::FaceMakerBullseye
  FaceMakerMode = 3
  LengthFwd = 4
  LengthRev = 0
  Placement = pos=(0,-3.8,0) rot=(0,0,1;0rad)
  Solid = true
  Symmetric = false
FEATURE [Part::Cut] Cut055
  Base = -> Cut054
  Refine = true
  Tool = -> Extrude091
note: 2 file-system paths scrubbed to <path> (originals preserved in the JSON sidecar)
